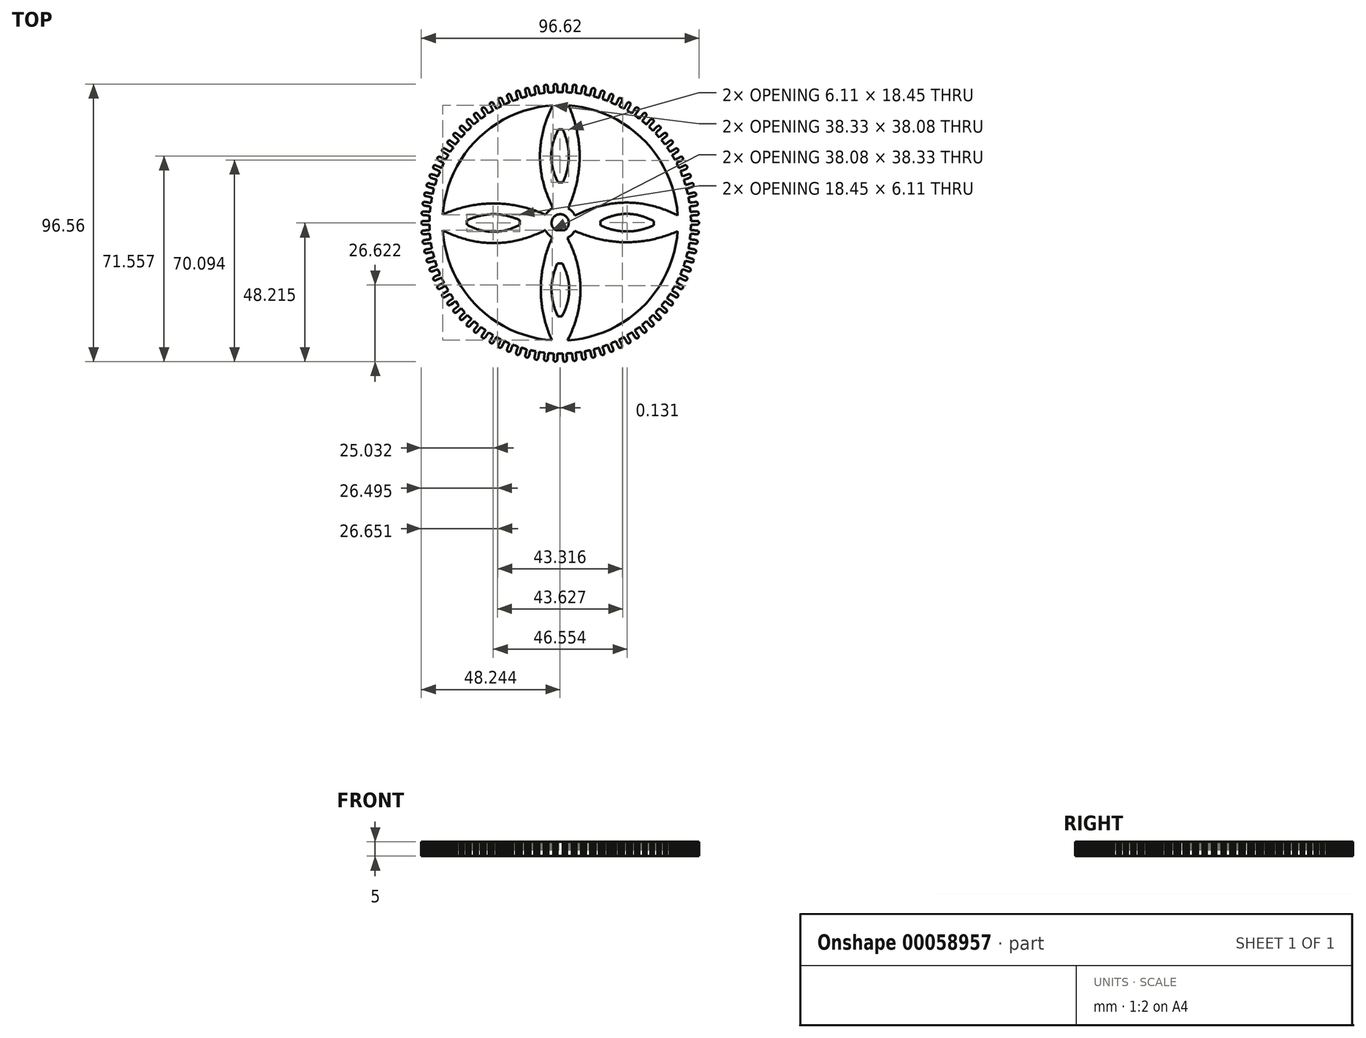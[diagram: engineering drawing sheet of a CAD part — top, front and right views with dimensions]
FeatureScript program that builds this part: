
annotation { "Feature Type Name" : "Feature", "Feature Type Description" : "" }
export const myFeature = defineFeature(function(context is Context, id is Id, definition is map)
    precondition{}
    {
        {
            var Q0;
            Q0=qCreatedBy(makeId("Top.planeOp"),FACE);
            var sketch = newSketch(context, id + "F0", { "sketchPlane" : qUnion([Q0])});
            skLineSegment(sketch, "E0", {"start": v(44.7, -0.63) * mm, "end": v(44.84, -0.63) * mm});
            skLineSegment(sketch, "E1", {"start": v(44.84, -0.63) * mm, "end": v(45, -0.64) * mm});
            skLineSegment(sketch, "E2", {"start": v(45, -0.64) * mm, "end": v(45.17, -0.64) * mm});
            skLineSegment(sketch, "E3", {"start": v(45.17, -0.64) * mm, "end": v(45.34, -0.64) * mm});
            skLineSegment(sketch, "E4", {"start": v(45.34, -0.64) * mm, "end": v(45.5, -0.64) * mm});
            skLineSegment(sketch, "E5", {"start": v(45.5, -0.64) * mm, "end": v(45.67, -0.65) * mm});
            skLineSegment(sketch, "E6", {"start": v(45.67, -0.65) * mm, "end": v(45.84, -0.65) * mm});
            skLineSegment(sketch, "E7", {"start": v(45.84, -0.65) * mm, "end": v(46.01, -0.65) * mm});
            skLineSegment(sketch, "E8", {"start": v(46.01, -0.65) * mm, "end": v(46.18, -0.65) * mm});
            skLineSegment(sketch, "E9", {"start": v(46.18, -0.65) * mm, "end": v(46.35, -0.66) * mm});
            skLineSegment(sketch, "E10", {"start": v(46.35, -0.66) * mm, "end": v(46.51, -0.66) * mm});
            skLineSegment(sketch, "E11", {"start": v(46.51, -0.66) * mm, "end": v(46.68, -0.66) * mm});
            skLineSegment(sketch, "E12", {"start": v(46.68, -0.66) * mm, "end": v(46.85, -0.66) * mm});
            skLineSegment(sketch, "E13", {"start": v(46.85, -0.66) * mm, "end": v(47.02, -0.64) * mm});
            skLineSegment(sketch, "E14", {"start": v(47.02, -0.64) * mm, "end": v(47.18, -0.57) * mm});
            skLineSegment(sketch, "E15", {"start": v(47.18, -0.57) * mm, "end": v(47.32, -0.47) * mm});
            skLineSegment(sketch, "E16", {"start": v(47.32, -0.47) * mm, "end": v(47.43, -0.33) * mm});
            skLineSegment(sketch, "E17", {"start": v(47.43, -0.33) * mm, "end": v(47.5, -0.17) * mm});
            skLineSegment(sketch, "E18", {"start": v(47.5, -0.17) * mm, "end": v(47.52, 0) * mm});
            skLineSegment(sketch, "E19", {"start": v(47.52, 0) * mm, "end": v(47.5, 0.17) * mm});
            skLineSegment(sketch, "E20", {"start": v(47.5, 0.17) * mm, "end": v(47.43, 0.33) * mm});
            skLineSegment(sketch, "E21", {"start": v(47.43, 0.33) * mm, "end": v(47.32, 0.47) * mm});
            skLineSegment(sketch, "E22", {"start": v(47.32, 0.47) * mm, "end": v(47.18, 0.57) * mm});
            skLineSegment(sketch, "E23", {"start": v(47.18, 0.57) * mm, "end": v(47.02, 0.64) * mm});
            skLineSegment(sketch, "E24", {"start": v(47.02, 0.64) * mm, "end": v(46.85, 0.66) * mm});
            skLineSegment(sketch, "E25", {"start": v(46.85, 0.66) * mm, "end": v(46.69, 0.66) * mm});
            skLineSegment(sketch, "E26", {"start": v(46.69, 0.66) * mm, "end": v(46.52, 0.66) * mm});
            skLineSegment(sketch, "E27", {"start": v(46.52, 0.66) * mm, "end": v(46.35, 0.66) * mm});
            skLineSegment(sketch, "E28", {"start": v(46.35, 0.66) * mm, "end": v(46.18, 0.65) * mm});
            skLineSegment(sketch, "E29", {"start": v(46.18, 0.65) * mm, "end": v(46.02, 0.65) * mm});
            skLineSegment(sketch, "E30", {"start": v(46.02, 0.65) * mm, "end": v(45.84, 0.65) * mm});
            skLineSegment(sketch, "E31", {"start": v(45.84, 0.65) * mm, "end": v(45.68, 0.65) * mm});
            skLineSegment(sketch, "E32", {"start": v(45.68, 0.65) * mm, "end": v(45.51, 0.64) * mm});
            skLineSegment(sketch, "E33", {"start": v(45.51, 0.64) * mm, "end": v(45.34, 0.64) * mm});
            skLineSegment(sketch, "E34", {"start": v(45.34, 0.64) * mm, "end": v(45.17, 0.64) * mm});
            skLineSegment(sketch, "E35", {"start": v(45.17, 0.64) * mm, "end": v(45, 0.64) * mm});
            skLineSegment(sketch, "E36", {"start": v(45, 0.64) * mm, "end": v(44.84, 0.63) * mm});
            skLineSegment(sketch, "E37", {"start": v(44.84, 0.63) * mm, "end": v(44.7, 0.63) * mm});
            skLineSegment(sketch, "E38", {"start": v(44.7, 0.63) * mm, "end": v(44.69, 0.8) * mm});
            skLineSegment(sketch, "E39", {"start": v(44.69, 0.8) * mm, "end": v(44.68, 0.96) * mm});
            skLineSegment(sketch, "E40", {"start": v(44.68, 0.96) * mm, "end": v(44.67, 1.13) * mm});
            skLineSegment(sketch, "E41", {"start": v(44.67, 1.13) * mm, "end": v(44.67, 1.3) * mm});
            skLineSegment(sketch, "E42", {"start": v(44.67, 1.3) * mm, "end": v(44.66, 1.46) * mm});
            skLineSegment(sketch, "E43", {"start": v(44.66, 1.46) * mm, "end": v(44.66, 1.63) * mm});
            skLineSegment(sketch, "E44", {"start": v(44.66, 1.63) * mm, "end": v(44.65, 1.8) * mm});
            skLineSegment(sketch, "E45", {"start": v(44.65, 1.8) * mm, "end": v(44.65, 1.96) * mm});
            skLineSegment(sketch, "E46", {"start": v(44.65, 1.96) * mm, "end": v(44.64, 2.13) * mm});
            skLineSegment(sketch, "E47", {"start": v(44.64, 2.13) * mm, "end": v(44.63, 2.3) * mm});
            skLineSegment(sketch, "E48", {"start": v(44.63, 2.3) * mm, "end": v(44.63, 2.46) * mm});
            skLineSegment(sketch, "E49", {"start": v(44.63, 2.46) * mm, "end": v(44.63, 2.54) * mm});
            skLineSegment(sketch, "E50", {"start": v(44.63, 2.54) * mm, "end": v(44.8, 2.55) * mm});
            skLineSegment(sketch, "E51", {"start": v(44.8, 2.55) * mm, "end": v(44.96, 2.56) * mm});
            skLineSegment(sketch, "E52", {"start": v(44.96, 2.56) * mm, "end": v(45.13, 2.57) * mm});
            skLineSegment(sketch, "E53", {"start": v(45.13, 2.57) * mm, "end": v(45.3, 2.58) * mm});
            skLineSegment(sketch, "E54", {"start": v(45.3, 2.58) * mm, "end": v(45.46, 2.59) * mm});
            skLineSegment(sketch, "E55", {"start": v(45.46, 2.59) * mm, "end": v(45.63, 2.6) * mm});
            skLineSegment(sketch, "E56", {"start": v(45.63, 2.6) * mm, "end": v(45.8, 2.6) * mm});
            skLineSegment(sketch, "E57", {"start": v(45.8, 2.6) * mm, "end": v(45.96, 2.62) * mm});
            skLineSegment(sketch, "E58", {"start": v(45.96, 2.62) * mm, "end": v(46.13, 2.63) * mm});
            skLineSegment(sketch, "E59", {"start": v(46.13, 2.63) * mm, "end": v(46.3, 2.64) * mm});
            skLineSegment(sketch, "E60", {"start": v(46.3, 2.64) * mm, "end": v(46.47, 2.65) * mm});
            skLineSegment(sketch, "E61", {"start": v(46.47, 2.65) * mm, "end": v(46.64, 2.65) * mm});
            skLineSegment(sketch, "E62", {"start": v(46.64, 2.65) * mm, "end": v(46.82, 2.67) * mm});
            skLineSegment(sketch, "E63", {"start": v(46.82, 2.67) * mm, "end": v(46.98, 2.7) * mm});
            skLineSegment(sketch, "E64", {"start": v(46.98, 2.7) * mm, "end": v(47.14, 2.8) * mm});
            skLineSegment(sketch, "E65", {"start": v(47.14, 2.8) * mm, "end": v(47.26, 2.91) * mm});
            skLineSegment(sketch, "E66", {"start": v(47.26, 2.91) * mm, "end": v(47.35, 3.06) * mm});
            skLineSegment(sketch, "E67", {"start": v(47.35, 3.06) * mm, "end": v(47.4, 3.23) * mm});
            skLineSegment(sketch, "E68", {"start": v(47.4, 3.23) * mm, "end": v(47.4, 3.4) * mm});
            skLineSegment(sketch, "E69", {"start": v(47.4, 3.4) * mm, "end": v(47.35, 3.57) * mm});
            skLineSegment(sketch, "E70", {"start": v(47.35, 3.57) * mm, "end": v(47.27, 3.72) * mm});
            skLineSegment(sketch, "E71", {"start": v(47.27, 3.72) * mm, "end": v(47.15, 3.85) * mm});
            skLineSegment(sketch, "E72", {"start": v(47.15, 3.85) * mm, "end": v(47, 3.93) * mm});
            skLineSegment(sketch, "E73", {"start": v(47, 3.93) * mm, "end": v(46.83, 3.98) * mm});
            skLineSegment(sketch, "E74", {"start": v(46.83, 3.98) * mm, "end": v(46.72, 3.99) * mm});
            skLineSegment(sketch, "E75", {"start": v(46.72, 3.99) * mm, "end": v(46.55, 3.97) * mm});
            skLineSegment(sketch, "E76", {"start": v(46.55, 3.97) * mm, "end": v(46.38, 3.96) * mm});
            skLineSegment(sketch, "E77", {"start": v(46.38, 3.96) * mm, "end": v(46.21, 3.94) * mm});
            skLineSegment(sketch, "E78", {"start": v(46.21, 3.94) * mm, "end": v(46.04, 3.93) * mm});
            skLineSegment(sketch, "E79", {"start": v(46.04, 3.93) * mm, "end": v(45.88, 3.92) * mm});
            skLineSegment(sketch, "E80", {"start": v(45.88, 3.92) * mm, "end": v(45.71, 3.9) * mm});
            skLineSegment(sketch, "E81", {"start": v(45.71, 3.9) * mm, "end": v(45.54, 3.89) * mm});
            skLineSegment(sketch, "E82", {"start": v(45.54, 3.89) * mm, "end": v(45.38, 3.87) * mm});
            skLineSegment(sketch, "E83", {"start": v(45.38, 3.87) * mm, "end": v(45.21, 3.86) * mm});
            skLineSegment(sketch, "E84", {"start": v(45.21, 3.86) * mm, "end": v(45.04, 3.85) * mm});
            skLineSegment(sketch, "E85", {"start": v(45.04, 3.85) * mm, "end": v(44.87, 3.83) * mm});
            skLineSegment(sketch, "E86", {"start": v(44.87, 3.83) * mm, "end": v(44.7, 3.82) * mm});
            skLineSegment(sketch, "E87", {"start": v(44.7, 3.82) * mm, "end": v(44.54, 3.8) * mm});
            skLineSegment(sketch, "E88", {"start": v(44.54, 3.8) * mm, "end": v(44.52, 3.97) * mm});
            skLineSegment(sketch, "E89", {"start": v(44.52, 3.97) * mm, "end": v(44.5, 4.13) * mm});
            skLineSegment(sketch, "E90", {"start": v(44.5, 4.13) * mm, "end": v(44.49, 4.3) * mm});
            skLineSegment(sketch, "E91", {"start": v(44.49, 4.3) * mm, "end": v(44.47, 4.47) * mm});
            skLineSegment(sketch, "E92", {"start": v(44.47, 4.47) * mm, "end": v(44.45, 4.63) * mm});
            skLineSegment(sketch, "E93", {"start": v(44.45, 4.63) * mm, "end": v(44.43, 4.8) * mm});
            skLineSegment(sketch, "E94", {"start": v(44.43, 4.8) * mm, "end": v(44.42, 4.96) * mm});
            skLineSegment(sketch, "E95", {"start": v(44.42, 4.96) * mm, "end": v(44.4, 5.13) * mm});
            skLineSegment(sketch, "E96", {"start": v(44.4, 5.13) * mm, "end": v(44.38, 5.3) * mm});
            skLineSegment(sketch, "E97", {"start": v(44.38, 5.3) * mm, "end": v(44.36, 5.46) * mm});
            skLineSegment(sketch, "E98", {"start": v(44.36, 5.46) * mm, "end": v(44.35, 5.62) * mm});
            skLineSegment(sketch, "E99", {"start": v(44.35, 5.62) * mm, "end": v(44.34, 5.7) * mm});
            skLineSegment(sketch, "E100", {"start": v(44.34, 5.7) * mm, "end": v(44.5, 5.72) * mm});
            skLineSegment(sketch, "E101", {"start": v(44.5, 5.72) * mm, "end": v(44.67, 5.75) * mm});
            skLineSegment(sketch, "E102", {"start": v(44.67, 5.75) * mm, "end": v(44.84, 5.77) * mm});
            skLineSegment(sketch, "E103", {"start": v(44.84, 5.77) * mm, "end": v(45, 5.79) * mm});
            skLineSegment(sketch, "E104", {"start": v(45, 5.79) * mm, "end": v(45.17, 5.8) * mm});
            skLineSegment(sketch, "E105", {"start": v(45.17, 5.8) * mm, "end": v(45.34, 5.83) * mm});
            skLineSegment(sketch, "E106", {"start": v(45.34, 5.83) * mm, "end": v(45.5, 5.85) * mm});
            skLineSegment(sketch, "E107", {"start": v(45.5, 5.85) * mm, "end": v(45.67, 5.87) * mm});
            skLineSegment(sketch, "E108", {"start": v(45.67, 5.87) * mm, "end": v(45.84, 5.9) * mm});
            skLineSegment(sketch, "E109", {"start": v(45.84, 5.9) * mm, "end": v(46, 5.91) * mm});
            skLineSegment(sketch, "E110", {"start": v(46, 5.91) * mm, "end": v(46.17, 5.94) * mm});
            skLineSegment(sketch, "E111", {"start": v(46.17, 5.94) * mm, "end": v(46.34, 5.96) * mm});
            skLineSegment(sketch, "E112", {"start": v(46.34, 5.96) * mm, "end": v(46.51, 5.98) * mm});
            skLineSegment(sketch, "E113", {"start": v(46.51, 5.98) * mm, "end": v(46.68, 6.03) * mm});
            skLineSegment(sketch, "E114", {"start": v(46.68, 6.03) * mm, "end": v(46.82, 6.13) * mm});
            skLineSegment(sketch, "E115", {"start": v(46.82, 6.13) * mm, "end": v(46.94, 6.26) * mm});
            skLineSegment(sketch, "E116", {"start": v(46.94, 6.26) * mm, "end": v(47.02, 6.41) * mm});
            skLineSegment(sketch, "E117", {"start": v(47.02, 6.41) * mm, "end": v(47.05, 6.58) * mm});
            skLineSegment(sketch, "E118", {"start": v(47.05, 6.58) * mm, "end": v(47.04, 6.76) * mm});
            skLineSegment(sketch, "E119", {"start": v(47.04, 6.76) * mm, "end": v(46.99, 6.92) * mm});
            skLineSegment(sketch, "E120", {"start": v(46.99, 6.92) * mm, "end": v(46.9, 7.07) * mm});
            skLineSegment(sketch, "E121", {"start": v(46.9, 7.07) * mm, "end": v(46.76, 7.18) * mm});
            skLineSegment(sketch, "E122", {"start": v(46.76, 7.18) * mm, "end": v(46.6, 7.26) * mm});
            skLineSegment(sketch, "E123", {"start": v(46.6, 7.26) * mm, "end": v(46.43, 7.3) * mm});
            skLineSegment(sketch, "E124", {"start": v(46.43, 7.3) * mm, "end": v(46.4, 7.3) * mm});
            skLineSegment(sketch, "E125", {"start": v(46.4, 7.3) * mm, "end": v(46.22, 7.28) * mm});
            skLineSegment(sketch, "E126", {"start": v(46.22, 7.28) * mm, "end": v(46.06, 7.25) * mm});
            skLineSegment(sketch, "E127", {"start": v(46.06, 7.25) * mm, "end": v(45.9, 7.22) * mm});
            skLineSegment(sketch, "E128", {"start": v(45.9, 7.22) * mm, "end": v(45.73, 7.2) * mm});
            skLineSegment(sketch, "E129", {"start": v(45.73, 7.2) * mm, "end": v(45.56, 7.17) * mm});
            skLineSegment(sketch, "E130", {"start": v(45.56, 7.17) * mm, "end": v(45.4, 7.15) * mm});
            skLineSegment(sketch, "E131", {"start": v(45.4, 7.15) * mm, "end": v(45.23, 7.12) * mm});
            skLineSegment(sketch, "E132", {"start": v(45.23, 7.12) * mm, "end": v(45.06, 7.1) * mm});
            skLineSegment(sketch, "E133", {"start": v(45.06, 7.1) * mm, "end": v(44.9, 7.07) * mm});
            skLineSegment(sketch, "E134", {"start": v(44.9, 7.07) * mm, "end": v(44.73, 7.04) * mm});
            skLineSegment(sketch, "E135", {"start": v(44.73, 7.04) * mm, "end": v(44.57, 7.02) * mm});
            skLineSegment(sketch, "E136", {"start": v(44.57, 7.02) * mm, "end": v(44.4, 7) * mm});
            skLineSegment(sketch, "E137", {"start": v(44.4, 7) * mm, "end": v(44.23, 6.97) * mm});
            skLineSegment(sketch, "E138", {"start": v(44.23, 6.97) * mm, "end": v(44.16, 6.96) * mm});
            skLineSegment(sketch, "E139", {"start": v(44.16, 6.96) * mm, "end": v(44.13, 7.12) * mm});
            skLineSegment(sketch, "E140", {"start": v(44.13, 7.12) * mm, "end": v(44.1, 7.28) * mm});
            skLineSegment(sketch, "E141", {"start": v(44.1, 7.28) * mm, "end": v(44.08, 7.45) * mm});
            skLineSegment(sketch, "E142", {"start": v(44.08, 7.45) * mm, "end": v(44.05, 7.61) * mm});
            skLineSegment(sketch, "E143", {"start": v(44.05, 7.61) * mm, "end": v(44.02, 7.78) * mm});
            skLineSegment(sketch, "E144", {"start": v(44.02, 7.78) * mm, "end": v(43.99, 7.94) * mm});
            skLineSegment(sketch, "E145", {"start": v(43.99, 7.94) * mm, "end": v(43.96, 8.1) * mm});
            skLineSegment(sketch, "E146", {"start": v(43.96, 8.1) * mm, "end": v(43.93, 8.27) * mm});
            skLineSegment(sketch, "E147", {"start": v(43.93, 8.27) * mm, "end": v(43.9, 8.43) * mm});
            skLineSegment(sketch, "E148", {"start": v(43.9, 8.43) * mm, "end": v(43.87, 8.6) * mm});
            skLineSegment(sketch, "E149", {"start": v(43.87, 8.6) * mm, "end": v(43.84, 8.76) * mm});
            skLineSegment(sketch, "E150", {"start": v(43.84, 8.76) * mm, "end": v(43.83, 8.84) * mm});
            skLineSegment(sketch, "E151", {"start": v(43.83, 8.84) * mm, "end": v(44, 8.87) * mm});
            skLineSegment(sketch, "E152", {"start": v(44, 8.87) * mm, "end": v(44.16, 8.9) * mm});
            skLineSegment(sketch, "E153", {"start": v(44.16, 8.9) * mm, "end": v(44.32, 8.94) * mm});
            skLineSegment(sketch, "E154", {"start": v(44.32, 8.94) * mm, "end": v(44.49, 8.97) * mm});
            skLineSegment(sketch, "E155", {"start": v(44.49, 8.97) * mm, "end": v(44.65, 9) * mm});
            skLineSegment(sketch, "E156", {"start": v(44.65, 9) * mm, "end": v(44.82, 9.03) * mm});
            skLineSegment(sketch, "E157", {"start": v(44.82, 9.03) * mm, "end": v(44.98, 9.07) * mm});
            skLineSegment(sketch, "E158", {"start": v(44.98, 9.07) * mm, "end": v(45.14, 9.1) * mm});
            skLineSegment(sketch, "E159", {"start": v(45.14, 9.1) * mm, "end": v(45.31, 9.13) * mm});
            skLineSegment(sketch, "E160", {"start": v(45.31, 9.13) * mm, "end": v(45.48, 9.16) * mm});
            skLineSegment(sketch, "E161", {"start": v(45.48, 9.16) * mm, "end": v(45.64, 9.2) * mm});
            skLineSegment(sketch, "E162", {"start": v(45.64, 9.2) * mm, "end": v(45.8, 9.23) * mm});
            skLineSegment(sketch, "E163", {"start": v(45.8, 9.23) * mm, "end": v(45.98, 9.27) * mm});
            skLineSegment(sketch, "E164", {"start": v(45.98, 9.27) * mm, "end": v(46.14, 9.33) * mm});
            skLineSegment(sketch, "E165", {"start": v(46.14, 9.33) * mm, "end": v(46.28, 9.44) * mm});
            skLineSegment(sketch, "E166", {"start": v(46.28, 9.44) * mm, "end": v(46.39, 9.57) * mm});
            skLineSegment(sketch, "E167", {"start": v(46.39, 9.57) * mm, "end": v(46.45, 9.73) * mm});
            skLineSegment(sketch, "E168", {"start": v(46.45, 9.73) * mm, "end": v(46.48, 9.9) * mm});
            skLineSegment(sketch, "E169", {"start": v(46.48, 9.9) * mm, "end": v(46.45, 10.08) * mm});
            skLineSegment(sketch, "E170", {"start": v(46.45, 10.08) * mm, "end": v(46.39, 10.24) * mm});
            skLineSegment(sketch, "E171", {"start": v(46.39, 10.24) * mm, "end": v(46.28, 10.38) * mm});
            skLineSegment(sketch, "E172", {"start": v(46.28, 10.38) * mm, "end": v(46.14, 10.48) * mm});
            skLineSegment(sketch, "E173", {"start": v(46.14, 10.48) * mm, "end": v(45.98, 10.55) * mm});
            skLineSegment(sketch, "E174", {"start": v(45.98, 10.55) * mm, "end": v(45.81, 10.57) * mm});
            skLineSegment(sketch, "E175", {"start": v(45.81, 10.57) * mm, "end": v(45.65, 10.54) * mm});
            skLineSegment(sketch, "E176", {"start": v(45.65, 10.54) * mm, "end": v(45.48, 10.5) * mm});
            skLineSegment(sketch, "E177", {"start": v(45.48, 10.5) * mm, "end": v(45.32, 10.47) * mm});
            skLineSegment(sketch, "E178", {"start": v(45.32, 10.47) * mm, "end": v(45.16, 10.44) * mm});
            skLineSegment(sketch, "E179", {"start": v(45.16, 10.44) * mm, "end": v(45, 10.4) * mm});
            skLineSegment(sketch, "E180", {"start": v(45, 10.4) * mm, "end": v(44.83, 10.36) * mm});
            skLineSegment(sketch, "E181", {"start": v(44.83, 10.36) * mm, "end": v(44.67, 10.32) * mm});
            skLineSegment(sketch, "E182", {"start": v(44.67, 10.32) * mm, "end": v(44.5, 10.29) * mm});
            skLineSegment(sketch, "E183", {"start": v(44.5, 10.29) * mm, "end": v(44.34, 10.25) * mm});
            skLineSegment(sketch, "E184", {"start": v(44.34, 10.25) * mm, "end": v(44.18, 10.21) * mm});
            skLineSegment(sketch, "E185", {"start": v(44.18, 10.21) * mm, "end": v(44.01, 10.18) * mm});
            skLineSegment(sketch, "E186", {"start": v(44.01, 10.18) * mm, "end": v(43.85, 10.14) * mm});
            skLineSegment(sketch, "E187", {"start": v(43.85, 10.14) * mm, "end": v(43.69, 10.1) * mm});
            skLineSegment(sketch, "E188", {"start": v(43.69, 10.1) * mm, "end": v(43.57, 10.07) * mm});
            skLineSegment(sketch, "E189", {"start": v(43.57, 10.07) * mm, "end": v(43.53, 10.24) * mm});
            skLineSegment(sketch, "E190", {"start": v(43.53, 10.24) * mm, "end": v(43.49, 10.4) * mm});
            skLineSegment(sketch, "E191", {"start": v(43.49, 10.4) * mm, "end": v(43.45, 10.56) * mm});
            skLineSegment(sketch, "E192", {"start": v(43.45, 10.56) * mm, "end": v(43.4, 10.72) * mm});
            skLineSegment(sketch, "E193", {"start": v(43.4, 10.72) * mm, "end": v(43.37, 10.88) * mm});
            skLineSegment(sketch, "E194", {"start": v(43.37, 10.88) * mm, "end": v(43.33, 11.04) * mm});
            skLineSegment(sketch, "E195", {"start": v(43.33, 11.04) * mm, "end": v(43.29, 11.2) * mm});
            skLineSegment(sketch, "E196", {"start": v(43.29, 11.2) * mm, "end": v(43.25, 11.37) * mm});
            skLineSegment(sketch, "E197", {"start": v(43.25, 11.37) * mm, "end": v(43.2, 11.53) * mm});
            skLineSegment(sketch, "E198", {"start": v(43.2, 11.53) * mm, "end": v(43.16, 11.69) * mm});
            skLineSegment(sketch, "E199", {"start": v(43.16, 11.69) * mm, "end": v(43.12, 11.85) * mm});
            skLineSegment(sketch, "E200", {"start": v(43.12, 11.85) * mm, "end": v(43.1, 11.93) * mm});
            skLineSegment(sketch, "E201", {"start": v(43.1, 11.93) * mm, "end": v(43.27, 11.97) * mm});
            skLineSegment(sketch, "E202", {"start": v(43.27, 11.97) * mm, "end": v(43.43, 12.02) * mm});
            skLineSegment(sketch, "E203", {"start": v(43.43, 12.02) * mm, "end": v(43.6, 12.06) * mm});
            skLineSegment(sketch, "E204", {"start": v(43.6, 12.06) * mm, "end": v(43.75, 12.1) * mm});
            skLineSegment(sketch, "E205", {"start": v(43.75, 12.1) * mm, "end": v(43.91, 12.15) * mm});
            skLineSegment(sketch, "E206", {"start": v(43.91, 12.15) * mm, "end": v(44.08, 12.2) * mm});
            skLineSegment(sketch, "E207", {"start": v(44.08, 12.2) * mm, "end": v(44.24, 12.24) * mm});
            skLineSegment(sketch, "E208", {"start": v(44.24, 12.24) * mm, "end": v(44.4, 12.28) * mm});
            skLineSegment(sketch, "E209", {"start": v(44.4, 12.28) * mm, "end": v(44.56, 12.33) * mm});
            skLineSegment(sketch, "E210", {"start": v(44.56, 12.33) * mm, "end": v(44.72, 12.37) * mm});
            skLineSegment(sketch, "E211", {"start": v(44.72, 12.37) * mm, "end": v(44.88, 12.41) * mm});
            skLineSegment(sketch, "E212", {"start": v(44.88, 12.41) * mm, "end": v(45.05, 12.46) * mm});
            skLineSegment(sketch, "E213", {"start": v(45.05, 12.46) * mm, "end": v(45.22, 12.5) * mm});
            skLineSegment(sketch, "E214", {"start": v(45.22, 12.5) * mm, "end": v(45.38, 12.58) * mm});
            skLineSegment(sketch, "E215", {"start": v(45.38, 12.58) * mm, "end": v(45.5, 12.7) * mm});
            skLineSegment(sketch, "E216", {"start": v(45.5, 12.7) * mm, "end": v(45.6, 12.84) * mm});
            skLineSegment(sketch, "E217", {"start": v(45.6, 12.84) * mm, "end": v(45.66, 13) * mm});
            skLineSegment(sketch, "E218", {"start": v(45.66, 13) * mm, "end": v(45.67, 13.18) * mm});
            skLineSegment(sketch, "E219", {"start": v(45.67, 13.18) * mm, "end": v(45.64, 13.35) * mm});
            skLineSegment(sketch, "E220", {"start": v(45.64, 13.35) * mm, "end": v(45.56, 13.5) * mm});
            skLineSegment(sketch, "E221", {"start": v(45.56, 13.5) * mm, "end": v(45.44, 13.63) * mm});
            skLineSegment(sketch, "E222", {"start": v(45.44, 13.63) * mm, "end": v(45.3, 13.73) * mm});
            skLineSegment(sketch, "E223", {"start": v(45.3, 13.73) * mm, "end": v(45.13, 13.78) * mm});
            skLineSegment(sketch, "E224", {"start": v(45.13, 13.78) * mm, "end": v(45, 13.8) * mm});
            skLineSegment(sketch, "E225", {"start": v(45, 13.8) * mm, "end": v(44.82, 13.77) * mm});
            skLineSegment(sketch, "E226", {"start": v(44.82, 13.77) * mm, "end": v(44.66, 13.72) * mm});
            skLineSegment(sketch, "E227", {"start": v(44.66, 13.72) * mm, "end": v(44.5, 13.67) * mm});
            skLineSegment(sketch, "E228", {"start": v(44.5, 13.67) * mm, "end": v(44.34, 13.62) * mm});
            skLineSegment(sketch, "E229", {"start": v(44.34, 13.62) * mm, "end": v(44.18, 13.57) * mm});
            skLineSegment(sketch, "E230", {"start": v(44.18, 13.57) * mm, "end": v(44.02, 13.53) * mm});
            skLineSegment(sketch, "E231", {"start": v(44.02, 13.53) * mm, "end": v(43.86, 13.48) * mm});
            skLineSegment(sketch, "E232", {"start": v(43.86, 13.48) * mm, "end": v(43.7, 13.43) * mm});
            skLineSegment(sketch, "E233", {"start": v(43.7, 13.43) * mm, "end": v(43.54, 13.38) * mm});
            skLineSegment(sketch, "E234", {"start": v(43.54, 13.38) * mm, "end": v(43.38, 13.33) * mm});
            skLineSegment(sketch, "E235", {"start": v(43.38, 13.33) * mm, "end": v(43.22, 13.28) * mm});
            skLineSegment(sketch, "E236", {"start": v(43.22, 13.28) * mm, "end": v(43.06, 13.24) * mm});
            skLineSegment(sketch, "E237", {"start": v(43.06, 13.24) * mm, "end": v(42.9, 13.19) * mm});
            skLineSegment(sketch, "E238", {"start": v(42.9, 13.19) * mm, "end": v(42.76, 13.14) * mm});
            skLineSegment(sketch, "E239", {"start": v(42.76, 13.14) * mm, "end": v(42.7, 13.3) * mm});
            skLineSegment(sketch, "E240", {"start": v(42.7, 13.3) * mm, "end": v(42.65, 13.46) * mm});
            skLineSegment(sketch, "E241", {"start": v(42.65, 13.46) * mm, "end": v(42.6, 13.62) * mm});
            skLineSegment(sketch, "E242", {"start": v(42.6, 13.62) * mm, "end": v(42.55, 13.78) * mm});
            skLineSegment(sketch, "E243", {"start": v(42.55, 13.78) * mm, "end": v(42.5, 13.94) * mm});
            skLineSegment(sketch, "E244", {"start": v(42.5, 13.94) * mm, "end": v(42.45, 14.1) * mm});
            skLineSegment(sketch, "E245", {"start": v(42.45, 14.1) * mm, "end": v(42.4, 14.25) * mm});
            skLineSegment(sketch, "E246", {"start": v(42.4, 14.25) * mm, "end": v(42.34, 14.41) * mm});
            skLineSegment(sketch, "E247", {"start": v(42.34, 14.41) * mm, "end": v(42.3, 14.57) * mm});
            skLineSegment(sketch, "E248", {"start": v(42.3, 14.57) * mm, "end": v(42.24, 14.73) * mm});
            skLineSegment(sketch, "E249", {"start": v(42.24, 14.73) * mm, "end": v(42.2, 14.89) * mm});
            skLineSegment(sketch, "E250", {"start": v(42.2, 14.89) * mm, "end": v(42.17, 14.96) * mm});
            skLineSegment(sketch, "E251", {"start": v(42.17, 14.96) * mm, "end": v(42.32, 15.02) * mm});
            skLineSegment(sketch, "E252", {"start": v(42.32, 15.02) * mm, "end": v(42.48, 15.07) * mm});
            skLineSegment(sketch, "E253", {"start": v(42.48, 15.07) * mm, "end": v(42.64, 15.13) * mm});
            skLineSegment(sketch, "E254", {"start": v(42.64, 15.13) * mm, "end": v(42.8, 15.18) * mm});
            skLineSegment(sketch, "E255", {"start": v(42.8, 15.18) * mm, "end": v(42.96, 15.24) * mm});
            skLineSegment(sketch, "E256", {"start": v(42.96, 15.24) * mm, "end": v(43.12, 15.3) * mm});
            skLineSegment(sketch, "E257", {"start": v(43.12, 15.3) * mm, "end": v(43.27, 15.35) * mm});
            skLineSegment(sketch, "E258", {"start": v(43.27, 15.35) * mm, "end": v(43.43, 15.4) * mm});
            skLineSegment(sketch, "E259", {"start": v(43.43, 15.4) * mm, "end": v(43.6, 15.46) * mm});
            skLineSegment(sketch, "E260", {"start": v(43.6, 15.46) * mm, "end": v(43.75, 15.51) * mm});
            skLineSegment(sketch, "E261", {"start": v(43.75, 15.51) * mm, "end": v(43.9, 15.57) * mm});
            skLineSegment(sketch, "E262", {"start": v(43.9, 15.57) * mm, "end": v(44.07, 15.63) * mm});
            skLineSegment(sketch, "E263", {"start": v(44.07, 15.63) * mm, "end": v(44.24, 15.69) * mm});
            skLineSegment(sketch, "E264", {"start": v(44.24, 15.69) * mm, "end": v(44.39, 15.77) * mm});
            skLineSegment(sketch, "E265", {"start": v(44.39, 15.77) * mm, "end": v(44.5, 15.9) * mm});
            skLineSegment(sketch, "E266", {"start": v(44.5, 15.9) * mm, "end": v(44.6, 16.05) * mm});
            skLineSegment(sketch, "E267", {"start": v(44.6, 16.05) * mm, "end": v(44.64, 16.21) * mm});
            skLineSegment(sketch, "E268", {"start": v(44.64, 16.21) * mm, "end": v(44.64, 16.39) * mm});
            skLineSegment(sketch, "E269", {"start": v(44.64, 16.39) * mm, "end": v(44.6, 16.55) * mm});
            skLineSegment(sketch, "E270", {"start": v(44.6, 16.55) * mm, "end": v(44.5, 16.7) * mm});
            skLineSegment(sketch, "E271", {"start": v(44.5, 16.7) * mm, "end": v(44.38, 16.83) * mm});
            skLineSegment(sketch, "E272", {"start": v(44.38, 16.83) * mm, "end": v(44.23, 16.91) * mm});
            skLineSegment(sketch, "E273", {"start": v(44.23, 16.91) * mm, "end": v(44.06, 16.95) * mm});
            skLineSegment(sketch, "E274", {"start": v(44.06, 16.95) * mm, "end": v(44, 16.96) * mm});
            skLineSegment(sketch, "E275", {"start": v(44, 16.96) * mm, "end": v(43.82, 16.94) * mm});
            skLineSegment(sketch, "E276", {"start": v(43.82, 16.94) * mm, "end": v(43.66, 16.88) * mm});
            skLineSegment(sketch, "E277", {"start": v(43.66, 16.88) * mm, "end": v(43.5, 16.82) * mm});
            skLineSegment(sketch, "E278", {"start": v(43.5, 16.82) * mm, "end": v(43.35, 16.76) * mm});
            skLineSegment(sketch, "E279", {"start": v(43.35, 16.76) * mm, "end": v(43.2, 16.7) * mm});
            skLineSegment(sketch, "E280", {"start": v(43.2, 16.7) * mm, "end": v(43.04, 16.65) * mm});
            skLineSegment(sketch, "E281", {"start": v(43.04, 16.65) * mm, "end": v(42.88, 16.58) * mm});
            skLineSegment(sketch, "E282", {"start": v(42.88, 16.58) * mm, "end": v(42.72, 16.53) * mm});
            skLineSegment(sketch, "E283", {"start": v(42.72, 16.53) * mm, "end": v(42.57, 16.47) * mm});
            skLineSegment(sketch, "E284", {"start": v(42.57, 16.47) * mm, "end": v(42.4, 16.4) * mm});
            skLineSegment(sketch, "E285", {"start": v(42.4, 16.4) * mm, "end": v(42.25, 16.35) * mm});
            skLineSegment(sketch, "E286", {"start": v(42.25, 16.35) * mm, "end": v(42.1, 16.29) * mm});
            skLineSegment(sketch, "E287", {"start": v(42.1, 16.29) * mm, "end": v(41.94, 16.23) * mm});
            skLineSegment(sketch, "E288", {"start": v(41.94, 16.23) * mm, "end": v(41.78, 16.17) * mm});
            skLineSegment(sketch, "E289", {"start": v(41.78, 16.17) * mm, "end": v(41.73, 16.15) * mm});
            skLineSegment(sketch, "E290", {"start": v(41.73, 16.15) * mm, "end": v(41.67, 16.3) * mm});
            skLineSegment(sketch, "E291", {"start": v(41.67, 16.3) * mm, "end": v(41.6, 16.46) * mm});
            skLineSegment(sketch, "E292", {"start": v(41.6, 16.46) * mm, "end": v(41.55, 16.61) * mm});
            skLineSegment(sketch, "E293", {"start": v(41.55, 16.61) * mm, "end": v(41.48, 16.77) * mm});
            skLineSegment(sketch, "E294", {"start": v(41.48, 16.77) * mm, "end": v(41.42, 16.92) * mm});
            skLineSegment(sketch, "E295", {"start": v(41.42, 16.92) * mm, "end": v(41.36, 17.08) * mm});
            skLineSegment(sketch, "E296", {"start": v(41.36, 17.08) * mm, "end": v(41.3, 17.23) * mm});
            skLineSegment(sketch, "E297", {"start": v(41.3, 17.23) * mm, "end": v(41.23, 17.38) * mm});
            skLineSegment(sketch, "E298", {"start": v(41.23, 17.38) * mm, "end": v(41.17, 17.54) * mm});
            skLineSegment(sketch, "E299", {"start": v(41.17, 17.54) * mm, "end": v(41.1, 17.7) * mm});
            skLineSegment(sketch, "E300", {"start": v(41.1, 17.7) * mm, "end": v(41.05, 17.85) * mm});
            skLineSegment(sketch, "E301", {"start": v(41.05, 17.85) * mm, "end": v(41.02, 17.92) * mm});
            skLineSegment(sketch, "E302", {"start": v(41.02, 17.92) * mm, "end": v(41.17, 17.99) * mm});
            skLineSegment(sketch, "E303", {"start": v(41.17, 17.99) * mm, "end": v(41.32, 18.05) * mm});
            skLineSegment(sketch, "E304", {"start": v(41.32, 18.05) * mm, "end": v(41.48, 18.12) * mm});
            skLineSegment(sketch, "E305", {"start": v(41.48, 18.12) * mm, "end": v(41.63, 18.19) * mm});
            skLineSegment(sketch, "E306", {"start": v(41.63, 18.19) * mm, "end": v(41.79, 18.25) * mm});
            skLineSegment(sketch, "E307", {"start": v(41.79, 18.25) * mm, "end": v(41.94, 18.32) * mm});
            skLineSegment(sketch, "E308", {"start": v(41.94, 18.32) * mm, "end": v(42.1, 18.38) * mm});
            skLineSegment(sketch, "E309", {"start": v(42.1, 18.38) * mm, "end": v(42.25, 18.45) * mm});
            skLineSegment(sketch, "E310", {"start": v(42.25, 18.45) * mm, "end": v(42.4, 18.52) * mm});
            skLineSegment(sketch, "E311", {"start": v(42.4, 18.52) * mm, "end": v(42.56, 18.58) * mm});
            skLineSegment(sketch, "E312", {"start": v(42.56, 18.58) * mm, "end": v(42.71, 18.65) * mm});
            skLineSegment(sketch, "E313", {"start": v(42.71, 18.65) * mm, "end": v(42.87, 18.72) * mm});
            skLineSegment(sketch, "E314", {"start": v(42.87, 18.72) * mm, "end": v(43.03, 18.79) * mm});
            skLineSegment(sketch, "E315", {"start": v(43.03, 18.79) * mm, "end": v(43.18, 18.89) * mm});
            skLineSegment(sketch, "E316", {"start": v(43.18, 18.89) * mm, "end": v(43.3, 19.02) * mm});
            skLineSegment(sketch, "E317", {"start": v(43.3, 19.02) * mm, "end": v(43.37, 19.17) * mm});
            skLineSegment(sketch, "E318", {"start": v(43.37, 19.17) * mm, "end": v(43.4, 19.34) * mm});
            skLineSegment(sketch, "E319", {"start": v(43.4, 19.34) * mm, "end": v(43.38, 19.52) * mm});
            skLineSegment(sketch, "E320", {"start": v(43.38, 19.52) * mm, "end": v(43.33, 19.68) * mm});
            skLineSegment(sketch, "E321", {"start": v(43.33, 19.68) * mm, "end": v(43.23, 19.82) * mm});
            skLineSegment(sketch, "E322", {"start": v(43.23, 19.82) * mm, "end": v(43.1, 19.94) * mm});
            skLineSegment(sketch, "E323", {"start": v(43.1, 19.94) * mm, "end": v(42.94, 20.01) * mm});
            skLineSegment(sketch, "E324", {"start": v(42.94, 20.01) * mm, "end": v(42.77, 20.04) * mm});
            skLineSegment(sketch, "E325", {"start": v(42.77, 20.04) * mm, "end": v(42.73, 20.04) * mm});
            skLineSegment(sketch, "E326", {"start": v(42.73, 20.04) * mm, "end": v(42.56, 20.02) * mm});
            skLineSegment(sketch, "E327", {"start": v(42.56, 20.02) * mm, "end": v(42.4, 19.95) * mm});
            skLineSegment(sketch, "E328", {"start": v(42.4, 19.95) * mm, "end": v(42.25, 19.88) * mm});
            skLineSegment(sketch, "E329", {"start": v(42.25, 19.88) * mm, "end": v(42.1, 19.81) * mm});
            skLineSegment(sketch, "E330", {"start": v(42.1, 19.81) * mm, "end": v(41.94, 19.74) * mm});
            skLineSegment(sketch, "E331", {"start": v(41.94, 19.74) * mm, "end": v(41.79, 19.67) * mm});
            skLineSegment(sketch, "E332", {"start": v(41.79, 19.67) * mm, "end": v(41.64, 19.6) * mm});
            skLineSegment(sketch, "E333", {"start": v(41.64, 19.6) * mm, "end": v(41.48, 19.53) * mm});
            skLineSegment(sketch, "E334", {"start": v(41.48, 19.53) * mm, "end": v(41.33, 19.46) * mm});
            skLineSegment(sketch, "E335", {"start": v(41.33, 19.46) * mm, "end": v(41.18, 19.4) * mm});
            skLineSegment(sketch, "E336", {"start": v(41.18, 19.4) * mm, "end": v(41.03, 19.32) * mm});
            skLineSegment(sketch, "E337", {"start": v(41.03, 19.32) * mm, "end": v(40.87, 19.25) * mm});
            skLineSegment(sketch, "E338", {"start": v(40.87, 19.25) * mm, "end": v(40.72, 19.18) * mm});
            skLineSegment(sketch, "E339", {"start": v(40.72, 19.18) * mm, "end": v(40.57, 19.1) * mm});
            skLineSegment(sketch, "E340", {"start": v(40.57, 19.1) * mm, "end": v(40.5, 19.08) * mm});
            skLineSegment(sketch, "E341", {"start": v(40.5, 19.08) * mm, "end": v(40.43, 19.23) * mm});
            skLineSegment(sketch, "E342", {"start": v(40.43, 19.23) * mm, "end": v(40.36, 19.38) * mm});
            skLineSegment(sketch, "E343", {"start": v(40.36, 19.38) * mm, "end": v(40.28, 19.53) * mm});
            skLineSegment(sketch, "E344", {"start": v(40.28, 19.53) * mm, "end": v(40.21, 19.68) * mm});
            skLineSegment(sketch, "E345", {"start": v(40.21, 19.68) * mm, "end": v(40.14, 19.82) * mm});
            skLineSegment(sketch, "E346", {"start": v(40.14, 19.82) * mm, "end": v(40.07, 19.97) * mm});
            skLineSegment(sketch, "E347", {"start": v(40.07, 19.97) * mm, "end": v(40, 20.12) * mm});
            skLineSegment(sketch, "E348", {"start": v(40, 20.12) * mm, "end": v(39.92, 20.27) * mm});
            skLineSegment(sketch, "E349", {"start": v(39.92, 20.27) * mm, "end": v(39.85, 20.42) * mm});
            skLineSegment(sketch, "E350", {"start": v(39.85, 20.42) * mm, "end": v(39.77, 20.57) * mm});
            skLineSegment(sketch, "E351", {"start": v(39.77, 20.57) * mm, "end": v(39.7, 20.72) * mm});
            skLineSegment(sketch, "E352", {"start": v(39.7, 20.72) * mm, "end": v(39.67, 20.8) * mm});
            skLineSegment(sketch, "E353", {"start": v(39.67, 20.8) * mm, "end": v(39.81, 20.87) * mm});
            skLineSegment(sketch, "E354", {"start": v(39.81, 20.87) * mm, "end": v(39.96, 20.95) * mm});
            skLineSegment(sketch, "E355", {"start": v(39.96, 20.95) * mm, "end": v(40.11, 21.03) * mm});
            skLineSegment(sketch, "E356", {"start": v(40.11, 21.03) * mm, "end": v(40.26, 21.1) * mm});
            skLineSegment(sketch, "E357", {"start": v(40.26, 21.1) * mm, "end": v(40.4, 21.18) * mm});
            skLineSegment(sketch, "E358", {"start": v(40.4, 21.18) * mm, "end": v(40.56, 21.26) * mm});
            skLineSegment(sketch, "E359", {"start": v(40.56, 21.26) * mm, "end": v(40.7, 21.33) * mm});
            skLineSegment(sketch, "E360", {"start": v(40.7, 21.33) * mm, "end": v(40.86, 21.4) * mm});
            skLineSegment(sketch, "E361", {"start": v(40.86, 21.4) * mm, "end": v(41, 21.49) * mm});
            skLineSegment(sketch, "E362", {"start": v(41, 21.49) * mm, "end": v(41.16, 21.56) * mm});
            skLineSegment(sketch, "E363", {"start": v(41.16, 21.56) * mm, "end": v(41.3, 21.64) * mm});
            skLineSegment(sketch, "E364", {"start": v(41.3, 21.64) * mm, "end": v(41.46, 21.72) * mm});
            skLineSegment(sketch, "E365", {"start": v(41.46, 21.72) * mm, "end": v(41.62, 21.8) * mm});
            skLineSegment(sketch, "E366", {"start": v(41.62, 21.8) * mm, "end": v(41.75, 21.9) * mm});
            skLineSegment(sketch, "E367", {"start": v(41.75, 21.9) * mm, "end": v(41.86, 22.05) * mm});
            skLineSegment(sketch, "E368", {"start": v(41.86, 22.05) * mm, "end": v(41.92, 22.2) * mm});
            skLineSegment(sketch, "E369", {"start": v(41.92, 22.2) * mm, "end": v(41.94, 22.38) * mm});
            skLineSegment(sketch, "E370", {"start": v(41.94, 22.38) * mm, "end": v(41.92, 22.55) * mm});
            skLineSegment(sketch, "E371", {"start": v(41.92, 22.55) * mm, "end": v(41.85, 22.7) * mm});
            skLineSegment(sketch, "E372", {"start": v(41.85, 22.7) * mm, "end": v(41.74, 22.85) * mm});
            skLineSegment(sketch, "E373", {"start": v(41.74, 22.85) * mm, "end": v(41.6, 22.95) * mm});
            skLineSegment(sketch, "E374", {"start": v(41.6, 22.95) * mm, "end": v(41.44, 23.01) * mm});
            skLineSegment(sketch, "E375", {"start": v(41.44, 23.01) * mm, "end": v(41.26, 23.03) * mm});
            skLineSegment(sketch, "E376", {"start": v(41.26, 23.03) * mm, "end": v(41.1, 23) * mm});
            skLineSegment(sketch, "E377", {"start": v(41.1, 23) * mm, "end": v(40.94, 22.94) * mm});
            skLineSegment(sketch, "E378", {"start": v(40.94, 22.94) * mm, "end": v(40.8, 22.86) * mm});
            skLineSegment(sketch, "E379", {"start": v(40.8, 22.86) * mm, "end": v(40.65, 22.78) * mm});
            skLineSegment(sketch, "E380", {"start": v(40.65, 22.78) * mm, "end": v(40.5, 22.7) * mm});
            skLineSegment(sketch, "E381", {"start": v(40.5, 22.7) * mm, "end": v(40.36, 22.62) * mm});
            skLineSegment(sketch, "E382", {"start": v(40.36, 22.62) * mm, "end": v(40.2, 22.54) * mm});
            skLineSegment(sketch, "E383", {"start": v(40.2, 22.54) * mm, "end": v(40.06, 22.46) * mm});
            skLineSegment(sketch, "E384", {"start": v(40.06, 22.46) * mm, "end": v(39.92, 22.38) * mm});
            skLineSegment(sketch, "E385", {"start": v(39.92, 22.38) * mm, "end": v(39.77, 22.3) * mm});
            skLineSegment(sketch, "E386", {"start": v(39.77, 22.3) * mm, "end": v(39.62, 22.21) * mm});
            skLineSegment(sketch, "E387", {"start": v(39.62, 22.21) * mm, "end": v(39.47, 22.13) * mm});
            skLineSegment(sketch, "E388", {"start": v(39.47, 22.13) * mm, "end": v(39.32, 22.05) * mm});
            skLineSegment(sketch, "E389", {"start": v(39.32, 22.05) * mm, "end": v(39.18, 21.97) * mm});
            skLineSegment(sketch, "E390", {"start": v(39.18, 21.97) * mm, "end": v(39.07, 21.91) * mm});
            skLineSegment(sketch, "E391", {"start": v(39.07, 21.91) * mm, "end": v(38.99, 22.06) * mm});
            skLineSegment(sketch, "E392", {"start": v(38.99, 22.06) * mm, "end": v(38.9, 22.2) * mm});
            skLineSegment(sketch, "E393", {"start": v(38.9, 22.2) * mm, "end": v(38.82, 22.34) * mm});
            skLineSegment(sketch, "E394", {"start": v(38.82, 22.34) * mm, "end": v(38.74, 22.49) * mm});
            skLineSegment(sketch, "E395", {"start": v(38.74, 22.49) * mm, "end": v(38.66, 22.63) * mm});
            skLineSegment(sketch, "E396", {"start": v(38.66, 22.63) * mm, "end": v(38.57, 22.78) * mm});
            skLineSegment(sketch, "E397", {"start": v(38.57, 22.78) * mm, "end": v(38.49, 22.92) * mm});
            skLineSegment(sketch, "E398", {"start": v(38.49, 22.92) * mm, "end": v(38.4, 23.06) * mm});
            skLineSegment(sketch, "E399", {"start": v(38.4, 23.06) * mm, "end": v(38.32, 23.2) * mm});
            skLineSegment(sketch, "E400", {"start": v(38.32, 23.2) * mm, "end": v(38.24, 23.35) * mm});
            skLineSegment(sketch, "E401", {"start": v(38.24, 23.35) * mm, "end": v(38.16, 23.5) * mm});
            skLineSegment(sketch, "E402", {"start": v(38.16, 23.5) * mm, "end": v(38.12, 23.57) * mm});
            skLineSegment(sketch, "E403", {"start": v(38.12, 23.57) * mm, "end": v(38.26, 23.65) * mm});
            skLineSegment(sketch, "E404", {"start": v(38.26, 23.65) * mm, "end": v(38.4, 23.74) * mm});
            skLineSegment(sketch, "E405", {"start": v(38.4, 23.74) * mm, "end": v(38.55, 23.83) * mm});
            skLineSegment(sketch, "E406", {"start": v(38.55, 23.83) * mm, "end": v(38.69, 23.91) * mm});
            skLineSegment(sketch, "E407", {"start": v(38.69, 23.91) * mm, "end": v(38.83, 24) * mm});
            skLineSegment(sketch, "E408", {"start": v(38.83, 24) * mm, "end": v(38.98, 24.09) * mm});
            skLineSegment(sketch, "E409", {"start": v(38.98, 24.09) * mm, "end": v(39.12, 24.17) * mm});
            skLineSegment(sketch, "E410", {"start": v(39.12, 24.17) * mm, "end": v(39.26, 24.26) * mm});
            skLineSegment(sketch, "E411", {"start": v(39.26, 24.26) * mm, "end": v(39.4, 24.35) * mm});
            skLineSegment(sketch, "E412", {"start": v(39.4, 24.35) * mm, "end": v(39.55, 24.44) * mm});
            skLineSegment(sketch, "E413", {"start": v(39.55, 24.44) * mm, "end": v(39.7, 24.52) * mm});
            skLineSegment(sketch, "E414", {"start": v(39.7, 24.52) * mm, "end": v(39.84, 24.61) * mm});
            skLineSegment(sketch, "E415", {"start": v(39.84, 24.61) * mm, "end": v(40, 24.7) * mm});
            skLineSegment(sketch, "E416", {"start": v(40, 24.7) * mm, "end": v(40.12, 24.82) * mm});
            skLineSegment(sketch, "E417", {"start": v(40.12, 24.82) * mm, "end": v(40.21, 24.97) * mm});
            skLineSegment(sketch, "E418", {"start": v(40.21, 24.97) * mm, "end": v(40.27, 25.13) * mm});
            skLineSegment(sketch, "E419", {"start": v(40.27, 25.13) * mm, "end": v(40.28, 25.3) * mm});
            skLineSegment(sketch, "E420", {"start": v(40.28, 25.3) * mm, "end": v(40.24, 25.47) * mm});
            skLineSegment(sketch, "E421", {"start": v(40.24, 25.47) * mm, "end": v(40.16, 25.63) * mm});
            skLineSegment(sketch, "E422", {"start": v(40.16, 25.63) * mm, "end": v(40.04, 25.76) * mm});
            skLineSegment(sketch, "E423", {"start": v(40.04, 25.76) * mm, "end": v(39.9, 25.85) * mm});
            skLineSegment(sketch, "E424", {"start": v(39.9, 25.85) * mm, "end": v(39.73, 25.9) * mm});
            skLineSegment(sketch, "E425", {"start": v(39.73, 25.9) * mm, "end": v(39.62, 25.91) * mm});
            skLineSegment(sketch, "E426", {"start": v(39.62, 25.91) * mm, "end": v(39.45, 25.9) * mm});
            skLineSegment(sketch, "E427", {"start": v(39.45, 25.9) * mm, "end": v(39.3, 25.83) * mm});
            skLineSegment(sketch, "E428", {"start": v(39.3, 25.83) * mm, "end": v(39.14, 25.73) * mm});
            skLineSegment(sketch, "E429", {"start": v(39.14, 25.73) * mm, "end": v(39, 25.64) * mm});
            skLineSegment(sketch, "E430", {"start": v(39, 25.64) * mm, "end": v(38.86, 25.55) * mm});
            skLineSegment(sketch, "E431", {"start": v(38.86, 25.55) * mm, "end": v(38.72, 25.46) * mm});
            skLineSegment(sketch, "E432", {"start": v(38.72, 25.46) * mm, "end": v(38.58, 25.37) * mm});
            skLineSegment(sketch, "E433", {"start": v(38.58, 25.37) * mm, "end": v(38.44, 25.28) * mm});
            skLineSegment(sketch, "E434", {"start": v(38.44, 25.28) * mm, "end": v(38.3, 25.18) * mm});
            skLineSegment(sketch, "E435", {"start": v(38.3, 25.18) * mm, "end": v(38.15, 25.1) * mm});
            skLineSegment(sketch, "E436", {"start": v(38.15, 25.1) * mm, "end": v(38.01, 25) * mm});
            skLineSegment(sketch, "E437", {"start": v(38.01, 25) * mm, "end": v(37.87, 24.91) * mm});
            skLineSegment(sketch, "E438", {"start": v(37.87, 24.91) * mm, "end": v(37.73, 24.82) * mm});
            skLineSegment(sketch, "E439", {"start": v(37.73, 24.82) * mm, "end": v(37.6, 24.73) * mm});
            skLineSegment(sketch, "E440", {"start": v(37.6, 24.73) * mm, "end": v(37.45, 24.64) * mm});
            skLineSegment(sketch, "E441", {"start": v(37.45, 24.64) * mm, "end": v(37.35, 24.78) * mm});
            skLineSegment(sketch, "E442", {"start": v(37.35, 24.78) * mm, "end": v(37.26, 24.91) * mm});
            skLineSegment(sketch, "E443", {"start": v(37.26, 24.91) * mm, "end": v(37.17, 25.05) * mm});
            skLineSegment(sketch, "E444", {"start": v(37.17, 25.05) * mm, "end": v(37.07, 25.2) * mm});
            skLineSegment(sketch, "E445", {"start": v(37.07, 25.2) * mm, "end": v(36.98, 25.33) * mm});
            skLineSegment(sketch, "E446", {"start": v(36.98, 25.33) * mm, "end": v(36.89, 25.47) * mm});
            skLineSegment(sketch, "E447", {"start": v(36.89, 25.47) * mm, "end": v(36.8, 25.6) * mm});
            skLineSegment(sketch, "E448", {"start": v(36.8, 25.6) * mm, "end": v(36.7, 25.74) * mm});
            skLineSegment(sketch, "E449", {"start": v(36.7, 25.74) * mm, "end": v(36.6, 25.88) * mm});
            skLineSegment(sketch, "E450", {"start": v(36.6, 25.88) * mm, "end": v(36.52, 26.02) * mm});
            skLineSegment(sketch, "E451", {"start": v(36.52, 26.02) * mm, "end": v(36.42, 26.16) * mm});
            skLineSegment(sketch, "E452", {"start": v(36.42, 26.16) * mm, "end": v(36.38, 26.22) * mm});
            skLineSegment(sketch, "E453", {"start": v(36.38, 26.22) * mm, "end": v(36.51, 26.32) * mm});
            skLineSegment(sketch, "E454", {"start": v(36.51, 26.32) * mm, "end": v(36.65, 26.41) * mm});
            skLineSegment(sketch, "E455", {"start": v(36.65, 26.41) * mm, "end": v(36.79, 26.51) * mm});
            skLineSegment(sketch, "E456", {"start": v(36.79, 26.51) * mm, "end": v(36.93, 26.6) * mm});
            skLineSegment(sketch, "E457", {"start": v(36.93, 26.6) * mm, "end": v(37.06, 26.7) * mm});
            skLineSegment(sketch, "E458", {"start": v(37.06, 26.7) * mm, "end": v(37.2, 26.8) * mm});
            skLineSegment(sketch, "E459", {"start": v(37.2, 26.8) * mm, "end": v(37.34, 26.9) * mm});
            skLineSegment(sketch, "E460", {"start": v(37.34, 26.9) * mm, "end": v(37.47, 27) * mm});
            skLineSegment(sketch, "E461", {"start": v(37.47, 27) * mm, "end": v(37.61, 27.1) * mm});
            skLineSegment(sketch, "E462", {"start": v(37.61, 27.1) * mm, "end": v(37.75, 27.2) * mm});
            skLineSegment(sketch, "E463", {"start": v(37.75, 27.2) * mm, "end": v(37.88, 27.29) * mm});
            skLineSegment(sketch, "E464", {"start": v(37.88, 27.29) * mm, "end": v(38.02, 27.38) * mm});
            skLineSegment(sketch, "E465", {"start": v(38.02, 27.38) * mm, "end": v(38.17, 27.49) * mm});
            skLineSegment(sketch, "E466", {"start": v(38.17, 27.49) * mm, "end": v(38.29, 27.61) * mm});
            skLineSegment(sketch, "E467", {"start": v(38.29, 27.61) * mm, "end": v(38.37, 27.77) * mm});
            skLineSegment(sketch, "E468", {"start": v(38.37, 27.77) * mm, "end": v(38.41, 27.93) * mm});
            skLineSegment(sketch, "E469", {"start": v(38.41, 27.93) * mm, "end": v(38.41, 28.1) * mm});
            skLineSegment(sketch, "E470", {"start": v(38.41, 28.1) * mm, "end": v(38.36, 28.27) * mm});
            skLineSegment(sketch, "E471", {"start": v(38.36, 28.27) * mm, "end": v(38.27, 28.42) * mm});
            skLineSegment(sketch, "E472", {"start": v(38.27, 28.42) * mm, "end": v(38.14, 28.54) * mm});
            skLineSegment(sketch, "E473", {"start": v(38.14, 28.54) * mm, "end": v(38, 28.62) * mm});
            skLineSegment(sketch, "E474", {"start": v(38, 28.62) * mm, "end": v(37.82, 28.66) * mm});
            skLineSegment(sketch, "E475", {"start": v(37.82, 28.66) * mm, "end": v(37.75, 28.67) * mm});
            skLineSegment(sketch, "E476", {"start": v(37.75, 28.67) * mm, "end": v(37.58, 28.64) * mm});
            skLineSegment(sketch, "E477", {"start": v(37.58, 28.64) * mm, "end": v(37.42, 28.58) * mm});
            skLineSegment(sketch, "E478", {"start": v(37.42, 28.58) * mm, "end": v(37.29, 28.48) * mm});
            skLineSegment(sketch, "E479", {"start": v(37.29, 28.48) * mm, "end": v(37.15, 28.38) * mm});
            skLineSegment(sketch, "E480", {"start": v(37.15, 28.38) * mm, "end": v(37.02, 28.28) * mm});
            skLineSegment(sketch, "E481", {"start": v(37.02, 28.28) * mm, "end": v(36.88, 28.18) * mm});
            skLineSegment(sketch, "E482", {"start": v(36.88, 28.18) * mm, "end": v(36.75, 28.08) * mm});
            skLineSegment(sketch, "E483", {"start": v(36.75, 28.08) * mm, "end": v(36.61, 27.98) * mm});
            skLineSegment(sketch, "E484", {"start": v(36.61, 27.98) * mm, "end": v(36.48, 27.88) * mm});
            skLineSegment(sketch, "E485", {"start": v(36.48, 27.88) * mm, "end": v(36.35, 27.78) * mm});
            skLineSegment(sketch, "E486", {"start": v(36.35, 27.78) * mm, "end": v(36.21, 27.68) * mm});
            skLineSegment(sketch, "E487", {"start": v(36.21, 27.68) * mm, "end": v(36.08, 27.58) * mm});
            skLineSegment(sketch, "E488", {"start": v(36.08, 27.58) * mm, "end": v(35.94, 27.48) * mm});
            skLineSegment(sketch, "E489", {"start": v(35.94, 27.48) * mm, "end": v(35.8, 27.38) * mm});
            skLineSegment(sketch, "E490", {"start": v(35.8, 27.38) * mm, "end": v(35.67, 27.28) * mm});
            skLineSegment(sketch, "E491", {"start": v(35.67, 27.28) * mm, "end": v(35.63, 27.25) * mm});
            skLineSegment(sketch, "E492", {"start": v(35.63, 27.25) * mm, "end": v(35.53, 27.38) * mm});
            skLineSegment(sketch, "E493", {"start": v(35.53, 27.38) * mm, "end": v(35.43, 27.5) * mm});
            skLineSegment(sketch, "E494", {"start": v(35.43, 27.5) * mm, "end": v(35.33, 27.64) * mm});
            skLineSegment(sketch, "E495", {"start": v(35.33, 27.64) * mm, "end": v(35.22, 27.77) * mm});
            skLineSegment(sketch, "E496", {"start": v(35.22, 27.77) * mm, "end": v(35.12, 27.9) * mm});
            skLineSegment(sketch, "E497", {"start": v(35.12, 27.9) * mm, "end": v(35.02, 28.03) * mm});
            skLineSegment(sketch, "E498", {"start": v(35.02, 28.03) * mm, "end": v(34.92, 28.16) * mm});
            skLineSegment(sketch, "E499", {"start": v(34.92, 28.16) * mm, "end": v(34.81, 28.3) * mm});
            skLineSegment(sketch, "E500", {"start": v(34.81, 28.3) * mm, "end": v(34.71, 28.43) * mm});
            skLineSegment(sketch, "E501", {"start": v(34.71, 28.43) * mm, "end": v(34.61, 28.56) * mm});
            skLineSegment(sketch, "E502", {"start": v(34.61, 28.56) * mm, "end": v(34.5, 28.69) * mm});
            skLineSegment(sketch, "E503", {"start": v(34.5, 28.69) * mm, "end": v(34.46, 28.75) * mm});
            skLineSegment(sketch, "E504", {"start": v(34.46, 28.75) * mm, "end": v(34.59, 28.86) * mm});
            skLineSegment(sketch, "E505", {"start": v(34.59, 28.86) * mm, "end": v(34.72, 28.96) * mm});
            skLineSegment(sketch, "E506", {"start": v(34.72, 28.96) * mm, "end": v(34.85, 29.07) * mm});
            skLineSegment(sketch, "E507", {"start": v(34.85, 29.07) * mm, "end": v(34.98, 29.18) * mm});
            skLineSegment(sketch, "E508", {"start": v(34.98, 29.18) * mm, "end": v(35.1, 29.28) * mm});
            skLineSegment(sketch, "E509", {"start": v(35.1, 29.28) * mm, "end": v(35.24, 29.39) * mm});
            skLineSegment(sketch, "E510", {"start": v(35.24, 29.39) * mm, "end": v(35.37, 29.5) * mm});
            skLineSegment(sketch, "E511", {"start": v(35.37, 29.5) * mm, "end": v(35.5, 29.6) * mm});
            skLineSegment(sketch, "E512", {"start": v(35.5, 29.6) * mm, "end": v(35.63, 29.7) * mm});
            skLineSegment(sketch, "E513", {"start": v(35.63, 29.7) * mm, "end": v(35.76, 29.81) * mm});
            skLineSegment(sketch, "E514", {"start": v(35.76, 29.81) * mm, "end": v(35.89, 29.92) * mm});
            skLineSegment(sketch, "E515", {"start": v(35.89, 29.92) * mm, "end": v(36.02, 30.03) * mm});
            skLineSegment(sketch, "E516", {"start": v(36.02, 30.03) * mm, "end": v(36.16, 30.14) * mm});
            skLineSegment(sketch, "E517", {"start": v(36.16, 30.14) * mm, "end": v(36.27, 30.27) * mm});
            skLineSegment(sketch, "E518", {"start": v(36.27, 30.27) * mm, "end": v(36.34, 30.43) * mm});
            skLineSegment(sketch, "E519", {"start": v(36.34, 30.43) * mm, "end": v(36.37, 30.6) * mm});
            skLineSegment(sketch, "E520", {"start": v(36.37, 30.6) * mm, "end": v(36.35, 30.77) * mm});
            skLineSegment(sketch, "E521", {"start": v(36.35, 30.77) * mm, "end": v(36.3, 30.94) * mm});
            skLineSegment(sketch, "E522", {"start": v(36.3, 30.94) * mm, "end": v(36.2, 31.08) * mm});
            skLineSegment(sketch, "E523", {"start": v(36.2, 31.08) * mm, "end": v(36.06, 31.19) * mm});
            skLineSegment(sketch, "E524", {"start": v(36.06, 31.19) * mm, "end": v(35.9, 31.26) * mm});
            skLineSegment(sketch, "E525", {"start": v(35.9, 31.26) * mm, "end": v(35.73, 31.29) * mm});
            skLineSegment(sketch, "E526", {"start": v(35.73, 31.29) * mm, "end": v(35.7, 31.29) * mm});
            skLineSegment(sketch, "E527", {"start": v(35.7, 31.29) * mm, "end": v(35.52, 31.26) * mm});
            skLineSegment(sketch, "E528", {"start": v(35.52, 31.26) * mm, "end": v(35.36, 31.2) * mm});
            skLineSegment(sketch, "E529", {"start": v(35.36, 31.2) * mm, "end": v(35.23, 31.08) * mm});
            skLineSegment(sketch, "E530", {"start": v(35.23, 31.08) * mm, "end": v(35.1, 30.98) * mm});
            skLineSegment(sketch, "E531", {"start": v(35.1, 30.98) * mm, "end": v(34.97, 30.87) * mm});
            skLineSegment(sketch, "E532", {"start": v(34.97, 30.87) * mm, "end": v(34.84, 30.75) * mm});
            skLineSegment(sketch, "E533", {"start": v(34.84, 30.75) * mm, "end": v(34.72, 30.65) * mm});
            skLineSegment(sketch, "E534", {"start": v(34.72, 30.65) * mm, "end": v(34.6, 30.54) * mm});
            skLineSegment(sketch, "E535", {"start": v(34.6, 30.54) * mm, "end": v(34.46, 30.43) * mm});
            skLineSegment(sketch, "E536", {"start": v(34.46, 30.43) * mm, "end": v(34.34, 30.32) * mm});
            skLineSegment(sketch, "E537", {"start": v(34.34, 30.32) * mm, "end": v(34.21, 30.2) * mm});
            skLineSegment(sketch, "E538", {"start": v(34.21, 30.2) * mm, "end": v(34.08, 30.1) * mm});
            skLineSegment(sketch, "E539", {"start": v(34.08, 30.1) * mm, "end": v(33.96, 29.99) * mm});
            skLineSegment(sketch, "E540", {"start": v(33.96, 29.99) * mm, "end": v(33.83, 29.88) * mm});
            skLineSegment(sketch, "E541", {"start": v(33.83, 29.88) * mm, "end": v(33.7, 29.77) * mm});
            skLineSegment(sketch, "E542", {"start": v(33.7, 29.77) * mm, "end": v(33.65, 29.72) * mm});
            skLineSegment(sketch, "E543", {"start": v(33.65, 29.72) * mm, "end": v(33.53, 29.84) * mm});
            skLineSegment(sketch, "E544", {"start": v(33.53, 29.84) * mm, "end": v(33.42, 29.97) * mm});
            skLineSegment(sketch, "E545", {"start": v(33.42, 29.97) * mm, "end": v(33.31, 30.1) * mm});
            skLineSegment(sketch, "E546", {"start": v(33.31, 30.1) * mm, "end": v(33.2, 30.21) * mm});
            skLineSegment(sketch, "E547", {"start": v(33.2, 30.21) * mm, "end": v(33.09, 30.34) * mm});
            skLineSegment(sketch, "E548", {"start": v(33.09, 30.34) * mm, "end": v(32.98, 30.46) * mm});
            skLineSegment(sketch, "E549", {"start": v(32.98, 30.46) * mm, "end": v(32.87, 30.59) * mm});
            skLineSegment(sketch, "E550", {"start": v(32.87, 30.59) * mm, "end": v(32.75, 30.7) * mm});
            skLineSegment(sketch, "E551", {"start": v(32.75, 30.7) * mm, "end": v(32.64, 30.83) * mm});
            skLineSegment(sketch, "E552", {"start": v(32.64, 30.83) * mm, "end": v(32.53, 30.96) * mm});
            skLineSegment(sketch, "E553", {"start": v(32.53, 30.96) * mm, "end": v(32.42, 31.08) * mm});
            skLineSegment(sketch, "E554", {"start": v(32.42, 31.08) * mm, "end": v(32.37, 31.14) * mm});
            skLineSegment(sketch, "E555", {"start": v(32.37, 31.14) * mm, "end": v(32.49, 31.25) * mm});
            skLineSegment(sketch, "E556", {"start": v(32.49, 31.25) * mm, "end": v(32.6, 31.37) * mm});
            skLineSegment(sketch, "E557", {"start": v(32.6, 31.37) * mm, "end": v(32.73, 31.49) * mm});
            skLineSegment(sketch, "E558", {"start": v(32.73, 31.49) * mm, "end": v(32.85, 31.6) * mm});
            skLineSegment(sketch, "E559", {"start": v(32.85, 31.6) * mm, "end": v(32.98, 31.71) * mm});
            skLineSegment(sketch, "E560", {"start": v(32.98, 31.71) * mm, "end": v(33.1, 31.83) * mm});
            skLineSegment(sketch, "E561", {"start": v(33.1, 31.83) * mm, "end": v(33.22, 31.94) * mm});
            skLineSegment(sketch, "E562", {"start": v(33.22, 31.94) * mm, "end": v(33.34, 32.06) * mm});
            skLineSegment(sketch, "E563", {"start": v(33.34, 32.06) * mm, "end": v(33.47, 32.18) * mm});
            skLineSegment(sketch, "E564", {"start": v(33.47, 32.18) * mm, "end": v(33.59, 32.29) * mm});
            skLineSegment(sketch, "E565", {"start": v(33.59, 32.29) * mm, "end": v(33.71, 32.4) * mm});
            skLineSegment(sketch, "E566", {"start": v(33.71, 32.4) * mm, "end": v(33.84, 32.52) * mm});
            skLineSegment(sketch, "E567", {"start": v(33.84, 32.52) * mm, "end": v(33.96, 32.64) * mm});
            skLineSegment(sketch, "E568", {"start": v(33.96, 32.64) * mm, "end": v(34.07, 32.78) * mm});
            skLineSegment(sketch, "E569", {"start": v(34.07, 32.78) * mm, "end": v(34.13, 32.95) * mm});
            skLineSegment(sketch, "E570", {"start": v(34.13, 32.95) * mm, "end": v(34.15, 33.12) * mm});
            skLineSegment(sketch, "E571", {"start": v(34.15, 33.12) * mm, "end": v(34.12, 33.3) * mm});
            skLineSegment(sketch, "E572", {"start": v(34.12, 33.3) * mm, "end": v(34.05, 33.45) * mm});
            skLineSegment(sketch, "E573", {"start": v(34.05, 33.45) * mm, "end": v(33.93, 33.58) * mm});
            skLineSegment(sketch, "E574", {"start": v(33.93, 33.58) * mm, "end": v(33.8, 33.68) * mm});
            skLineSegment(sketch, "E575", {"start": v(33.8, 33.68) * mm, "end": v(33.63, 33.74) * mm});
            skLineSegment(sketch, "E576", {"start": v(33.63, 33.74) * mm, "end": v(33.5, 33.76) * mm});
            skLineSegment(sketch, "E577", {"start": v(33.5, 33.76) * mm, "end": v(33.32, 33.74) * mm});
            skLineSegment(sketch, "E578", {"start": v(33.32, 33.74) * mm, "end": v(33.16, 33.68) * mm});
            skLineSegment(sketch, "E579", {"start": v(33.16, 33.68) * mm, "end": v(33.02, 33.57) * mm});
            skLineSegment(sketch, "E580", {"start": v(33.02, 33.57) * mm, "end": v(32.9, 33.45) * mm});
            skLineSegment(sketch, "E581", {"start": v(32.9, 33.45) * mm, "end": v(32.78, 33.34) * mm});
            skLineSegment(sketch, "E582", {"start": v(32.78, 33.34) * mm, "end": v(32.66, 33.22) * mm});
            skLineSegment(sketch, "E583", {"start": v(32.66, 33.22) * mm, "end": v(32.54, 33.1) * mm});
            skLineSegment(sketch, "E584", {"start": v(32.54, 33.1) * mm, "end": v(32.43, 32.98) * mm});
            skLineSegment(sketch, "E585", {"start": v(32.43, 32.98) * mm, "end": v(32.3, 32.86) * mm});
            skLineSegment(sketch, "E586", {"start": v(32.3, 32.86) * mm, "end": v(32.19, 32.74) * mm});
            skLineSegment(sketch, "E587", {"start": v(32.19, 32.74) * mm, "end": v(32.07, 32.63) * mm});
            skLineSegment(sketch, "E588", {"start": v(32.07, 32.63) * mm, "end": v(31.95, 32.5) * mm});
            skLineSegment(sketch, "E589", {"start": v(31.95, 32.5) * mm, "end": v(31.83, 32.39) * mm});
            skLineSegment(sketch, "E590", {"start": v(31.83, 32.39) * mm, "end": v(31.71, 32.27) * mm});
            skLineSegment(sketch, "E591", {"start": v(31.71, 32.27) * mm, "end": v(31.6, 32.15) * mm});
            skLineSegment(sketch, "E592", {"start": v(31.6, 32.15) * mm, "end": v(31.49, 32.05) * mm});
            skLineSegment(sketch, "E593", {"start": v(31.49, 32.05) * mm, "end": v(31.37, 32.17) * mm});
            skLineSegment(sketch, "E594", {"start": v(31.37, 32.17) * mm, "end": v(31.25, 32.28) * mm});
            skLineSegment(sketch, "E595", {"start": v(31.25, 32.28) * mm, "end": v(31.13, 32.4) * mm});
            skLineSegment(sketch, "E596", {"start": v(31.13, 32.4) * mm, "end": v(31, 32.51) * mm});
            skLineSegment(sketch, "E597", {"start": v(31, 32.51) * mm, "end": v(30.89, 32.63) * mm});
            skLineSegment(sketch, "E598", {"start": v(30.89, 32.63) * mm, "end": v(30.77, 32.74) * mm});
            skLineSegment(sketch, "E599", {"start": v(30.77, 32.74) * mm, "end": v(30.65, 32.86) * mm});
            skLineSegment(sketch, "E600", {"start": v(30.65, 32.86) * mm, "end": v(30.53, 32.97) * mm});
            skLineSegment(sketch, "E601", {"start": v(30.53, 32.97) * mm, "end": v(30.41, 33.1) * mm});
            skLineSegment(sketch, "E602", {"start": v(30.41, 33.1) * mm, "end": v(30.3, 33.2) * mm});
            skLineSegment(sketch, "E603", {"start": v(30.3, 33.2) * mm, "end": v(30.17, 33.32) * mm});
            skLineSegment(sketch, "E604", {"start": v(30.17, 33.32) * mm, "end": v(30.11, 33.38) * mm});
            skLineSegment(sketch, "E605", {"start": v(30.11, 33.38) * mm, "end": v(30.23, 33.5) * mm});
            skLineSegment(sketch, "E606", {"start": v(30.23, 33.5) * mm, "end": v(30.34, 33.62) * mm});
            skLineSegment(sketch, "E607", {"start": v(30.34, 33.62) * mm, "end": v(30.46, 33.75) * mm});
            skLineSegment(sketch, "E608", {"start": v(30.46, 33.75) * mm, "end": v(30.57, 33.87) * mm});
            skLineSegment(sketch, "E609", {"start": v(30.57, 33.87) * mm, "end": v(30.68, 34) * mm});
            skLineSegment(sketch, "E610", {"start": v(30.68, 34) * mm, "end": v(30.8, 34.12) * mm});
            skLineSegment(sketch, "E611", {"start": v(30.8, 34.12) * mm, "end": v(30.91, 34.24) * mm});
            skLineSegment(sketch, "E612", {"start": v(30.91, 34.24) * mm, "end": v(31.02, 34.36) * mm});
            skLineSegment(sketch, "E613", {"start": v(31.02, 34.36) * mm, "end": v(31.14, 34.49) * mm});
            skLineSegment(sketch, "E614", {"start": v(31.14, 34.49) * mm, "end": v(31.25, 34.6) * mm});
            skLineSegment(sketch, "E615", {"start": v(31.25, 34.6) * mm, "end": v(31.37, 34.73) * mm});
            skLineSegment(sketch, "E616", {"start": v(31.37, 34.73) * mm, "end": v(31.48, 34.86) * mm});
            skLineSegment(sketch, "E617", {"start": v(31.48, 34.86) * mm, "end": v(31.6, 34.99) * mm});
            skLineSegment(sketch, "E618", {"start": v(31.6, 34.99) * mm, "end": v(31.7, 35.14) * mm});
            skLineSegment(sketch, "E619", {"start": v(31.7, 35.14) * mm, "end": v(31.74, 35.3) * mm});
            skLineSegment(sketch, "E620", {"start": v(31.74, 35.3) * mm, "end": v(31.75, 35.48) * mm});
            skLineSegment(sketch, "E621", {"start": v(31.75, 35.48) * mm, "end": v(31.7, 35.64) * mm});
            skLineSegment(sketch, "E622", {"start": v(31.7, 35.64) * mm, "end": v(31.63, 35.8) * mm});
            skLineSegment(sketch, "E623", {"start": v(31.63, 35.8) * mm, "end": v(31.5, 35.92) * mm});
            skLineSegment(sketch, "E624", {"start": v(31.5, 35.92) * mm, "end": v(31.36, 36.01) * mm});
            skLineSegment(sketch, "E625", {"start": v(31.36, 36.01) * mm, "end": v(31.2, 36.06) * mm});
            skLineSegment(sketch, "E626", {"start": v(31.2, 36.06) * mm, "end": v(31.09, 36.07) * mm});
            skLineSegment(sketch, "E627", {"start": v(31.09, 36.07) * mm, "end": v(30.92, 36.05) * mm});
            skLineSegment(sketch, "E628", {"start": v(30.92, 36.05) * mm, "end": v(30.76, 35.98) * mm});
            skLineSegment(sketch, "E629", {"start": v(30.76, 35.98) * mm, "end": v(30.62, 35.87) * mm});
            skLineSegment(sketch, "E630", {"start": v(30.62, 35.87) * mm, "end": v(30.5, 35.74) * mm});
            skLineSegment(sketch, "E631", {"start": v(30.5, 35.74) * mm, "end": v(30.4, 35.61) * mm});
            skLineSegment(sketch, "E632", {"start": v(30.4, 35.61) * mm, "end": v(30.28, 35.49) * mm});
            skLineSegment(sketch, "E633", {"start": v(30.28, 35.49) * mm, "end": v(30.17, 35.36) * mm});
            skLineSegment(sketch, "E634", {"start": v(30.17, 35.36) * mm, "end": v(30.06, 35.24) * mm});
            skLineSegment(sketch, "E635", {"start": v(30.06, 35.24) * mm, "end": v(29.95, 35.11) * mm});
            skLineSegment(sketch, "E636", {"start": v(29.95, 35.11) * mm, "end": v(29.84, 34.98) * mm});
            skLineSegment(sketch, "E637", {"start": v(29.84, 34.98) * mm, "end": v(29.73, 34.86) * mm});
            skLineSegment(sketch, "E638", {"start": v(29.73, 34.86) * mm, "end": v(29.62, 34.73) * mm});
            skLineSegment(sketch, "E639", {"start": v(29.62, 34.73) * mm, "end": v(29.5, 34.6) * mm});
            skLineSegment(sketch, "E640", {"start": v(29.5, 34.6) * mm, "end": v(29.4, 34.48) * mm});
            skLineSegment(sketch, "E641", {"start": v(29.4, 34.48) * mm, "end": v(29.29, 34.35) * mm});
            skLineSegment(sketch, "E642", {"start": v(29.29, 34.35) * mm, "end": v(29.17, 34.22) * mm});
            skLineSegment(sketch, "E643", {"start": v(29.17, 34.22) * mm, "end": v(29.05, 34.33) * mm});
            skLineSegment(sketch, "E644", {"start": v(29.05, 34.33) * mm, "end": v(28.92, 34.44) * mm});
            skLineSegment(sketch, "E645", {"start": v(28.92, 34.44) * mm, "end": v(28.8, 34.54) * mm});
            skLineSegment(sketch, "E646", {"start": v(28.8, 34.54) * mm, "end": v(28.66, 34.65) * mm});
            skLineSegment(sketch, "E647", {"start": v(28.66, 34.65) * mm, "end": v(28.54, 34.76) * mm});
            skLineSegment(sketch, "E648", {"start": v(28.54, 34.76) * mm, "end": v(28.4, 34.87) * mm});
            skLineSegment(sketch, "E649", {"start": v(28.4, 34.87) * mm, "end": v(28.28, 34.97) * mm});
            skLineSegment(sketch, "E650", {"start": v(28.28, 34.97) * mm, "end": v(28.15, 35.08) * mm});
            skLineSegment(sketch, "E651", {"start": v(28.15, 35.08) * mm, "end": v(28.03, 35.19) * mm});
            skLineSegment(sketch, "E652", {"start": v(28.03, 35.19) * mm, "end": v(27.9, 35.3) * mm});
            skLineSegment(sketch, "E653", {"start": v(27.9, 35.3) * mm, "end": v(27.77, 35.4) * mm});
            skLineSegment(sketch, "E654", {"start": v(27.77, 35.4) * mm, "end": v(27.7, 35.45) * mm});
            skLineSegment(sketch, "E655", {"start": v(27.7, 35.45) * mm, "end": v(27.81, 35.58) * mm});
            skLineSegment(sketch, "E656", {"start": v(27.81, 35.58) * mm, "end": v(27.92, 35.71) * mm});
            skLineSegment(sketch, "E657", {"start": v(27.92, 35.71) * mm, "end": v(28.03, 35.84) * mm});
            skLineSegment(sketch, "E658", {"start": v(28.03, 35.84) * mm, "end": v(28.13, 35.97) * mm});
            skLineSegment(sketch, "E659", {"start": v(28.13, 35.97) * mm, "end": v(28.23, 36.1) * mm});
            skLineSegment(sketch, "E660", {"start": v(28.23, 36.1) * mm, "end": v(28.34, 36.24) * mm});
            skLineSegment(sketch, "E661", {"start": v(28.34, 36.24) * mm, "end": v(28.45, 36.37) * mm});
            skLineSegment(sketch, "E662", {"start": v(28.45, 36.37) * mm, "end": v(28.55, 36.5) * mm});
            skLineSegment(sketch, "E663", {"start": v(28.55, 36.5) * mm, "end": v(28.66, 36.63) * mm});
            skLineSegment(sketch, "E664", {"start": v(28.66, 36.63) * mm, "end": v(28.76, 36.76) * mm});
            skLineSegment(sketch, "E665", {"start": v(28.76, 36.76) * mm, "end": v(28.87, 36.89) * mm});
            skLineSegment(sketch, "E666", {"start": v(28.87, 36.89) * mm, "end": v(28.97, 37.02) * mm});
            skLineSegment(sketch, "E667", {"start": v(28.97, 37.02) * mm, "end": v(29.08, 37.16) * mm});
            skLineSegment(sketch, "E668", {"start": v(29.08, 37.16) * mm, "end": v(29.16, 37.32) * mm});
            skLineSegment(sketch, "E669", {"start": v(29.16, 37.32) * mm, "end": v(29.2, 37.49) * mm});
            skLineSegment(sketch, "E670", {"start": v(29.2, 37.49) * mm, "end": v(29.2, 37.66) * mm});
            skLineSegment(sketch, "E671", {"start": v(29.2, 37.66) * mm, "end": v(29.14, 37.82) * mm});
            skLineSegment(sketch, "E672", {"start": v(29.14, 37.82) * mm, "end": v(29.05, 37.97) * mm});
            skLineSegment(sketch, "E673", {"start": v(29.05, 37.97) * mm, "end": v(28.92, 38.09) * mm});
            skLineSegment(sketch, "E674", {"start": v(28.92, 38.09) * mm, "end": v(28.77, 38.17) * mm});
            skLineSegment(sketch, "E675", {"start": v(28.77, 38.17) * mm, "end": v(28.6, 38.2) * mm});
            skLineSegment(sketch, "E676", {"start": v(28.6, 38.2) * mm, "end": v(28.53, 38.2) * mm});
            skLineSegment(sketch, "E677", {"start": v(28.53, 38.2) * mm, "end": v(28.36, 38.18) * mm});
            skLineSegment(sketch, "E678", {"start": v(28.36, 38.18) * mm, "end": v(28.2, 38.11) * mm});
            skLineSegment(sketch, "E679", {"start": v(28.2, 38.11) * mm, "end": v(28.06, 38) * mm});
            skLineSegment(sketch, "E680", {"start": v(28.06, 38) * mm, "end": v(27.96, 37.87) * mm});
            skLineSegment(sketch, "E681", {"start": v(27.96, 37.87) * mm, "end": v(27.86, 37.74) * mm});
            skLineSegment(sketch, "E682", {"start": v(27.86, 37.74) * mm, "end": v(27.76, 37.6) * mm});
            skLineSegment(sketch, "E683", {"start": v(27.76, 37.6) * mm, "end": v(27.66, 37.47) * mm});
            skLineSegment(sketch, "E684", {"start": v(27.66, 37.47) * mm, "end": v(27.56, 37.34) * mm});
            skLineSegment(sketch, "E685", {"start": v(27.56, 37.34) * mm, "end": v(27.45, 37.2) * mm});
            skLineSegment(sketch, "E686", {"start": v(27.45, 37.2) * mm, "end": v(27.35, 37.07) * mm});
            skLineSegment(sketch, "E687", {"start": v(27.35, 37.07) * mm, "end": v(27.25, 36.94) * mm});
            skLineSegment(sketch, "E688", {"start": v(27.25, 36.94) * mm, "end": v(27.15, 36.8) * mm});
            skLineSegment(sketch, "E689", {"start": v(27.15, 36.8) * mm, "end": v(27.05, 36.67) * mm});
            skLineSegment(sketch, "E690", {"start": v(27.05, 36.67) * mm, "end": v(26.95, 36.54) * mm});
            skLineSegment(sketch, "E691", {"start": v(26.95, 36.54) * mm, "end": v(26.84, 36.4) * mm});
            skLineSegment(sketch, "E692", {"start": v(26.84, 36.4) * mm, "end": v(26.74, 36.27) * mm});
            skLineSegment(sketch, "E693", {"start": v(26.74, 36.27) * mm, "end": v(26.71, 36.23) * mm});
            skLineSegment(sketch, "E694", {"start": v(26.71, 36.23) * mm, "end": v(26.58, 36.33) * mm});
            skLineSegment(sketch, "E695", {"start": v(26.58, 36.33) * mm, "end": v(26.44, 36.43) * mm});
            skLineSegment(sketch, "E696", {"start": v(26.44, 36.43) * mm, "end": v(26.3, 36.52) * mm});
            skLineSegment(sketch, "E697", {"start": v(26.3, 36.52) * mm, "end": v(26.17, 36.62) * mm});
            skLineSegment(sketch, "E698", {"start": v(26.17, 36.62) * mm, "end": v(26.04, 36.72) * mm});
            skLineSegment(sketch, "E699", {"start": v(26.04, 36.72) * mm, "end": v(25.9, 36.82) * mm});
            skLineSegment(sketch, "E700", {"start": v(25.9, 36.82) * mm, "end": v(25.77, 36.91) * mm});
            skLineSegment(sketch, "E701", {"start": v(25.77, 36.91) * mm, "end": v(25.64, 37.01) * mm});
            skLineSegment(sketch, "E702", {"start": v(25.64, 37.01) * mm, "end": v(25.5, 37.11) * mm});
            skLineSegment(sketch, "E703", {"start": v(25.5, 37.11) * mm, "end": v(25.37, 37.2) * mm});
            skLineSegment(sketch, "E704", {"start": v(25.37, 37.2) * mm, "end": v(25.23, 37.3) * mm});
            skLineSegment(sketch, "E705", {"start": v(25.23, 37.3) * mm, "end": v(25.17, 37.35) * mm});
            skLineSegment(sketch, "E706", {"start": v(25.17, 37.35) * mm, "end": v(25.26, 37.5) * mm});
            skLineSegment(sketch, "E707", {"start": v(25.26, 37.5) * mm, "end": v(25.36, 37.63) * mm});
            skLineSegment(sketch, "E708", {"start": v(25.36, 37.63) * mm, "end": v(25.45, 37.77) * mm});
            skLineSegment(sketch, "E709", {"start": v(25.45, 37.77) * mm, "end": v(25.55, 37.9) * mm});
            skLineSegment(sketch, "E710", {"start": v(25.55, 37.9) * mm, "end": v(25.64, 38.04) * mm});
            skLineSegment(sketch, "E711", {"start": v(25.64, 38.04) * mm, "end": v(25.74, 38.18) * mm});
            skLineSegment(sketch, "E712", {"start": v(25.74, 38.18) * mm, "end": v(25.84, 38.32) * mm});
            skLineSegment(sketch, "E713", {"start": v(25.84, 38.32) * mm, "end": v(25.93, 38.45) * mm});
            skLineSegment(sketch, "E714", {"start": v(25.93, 38.45) * mm, "end": v(26.03, 38.6) * mm});
            skLineSegment(sketch, "E715", {"start": v(26.03, 38.6) * mm, "end": v(26.12, 38.73) * mm});
            skLineSegment(sketch, "E716", {"start": v(26.12, 38.73) * mm, "end": v(26.22, 38.87) * mm});
            skLineSegment(sketch, "E717", {"start": v(26.22, 38.87) * mm, "end": v(26.32, 39) * mm});
            skLineSegment(sketch, "E718", {"start": v(26.32, 39) * mm, "end": v(26.42, 39.16) * mm});
            skLineSegment(sketch, "E719", {"start": v(26.42, 39.16) * mm, "end": v(26.49, 39.32) * mm});
            skLineSegment(sketch, "E720", {"start": v(26.49, 39.32) * mm, "end": v(26.51, 39.49) * mm});
            skLineSegment(sketch, "E721", {"start": v(26.51, 39.49) * mm, "end": v(26.5, 39.66) * mm});
            skLineSegment(sketch, "E722", {"start": v(26.5, 39.66) * mm, "end": v(26.43, 39.82) * mm});
            skLineSegment(sketch, "E723", {"start": v(26.43, 39.82) * mm, "end": v(26.33, 39.96) * mm});
            skLineSegment(sketch, "E724", {"start": v(26.33, 39.96) * mm, "end": v(26.2, 40.07) * mm});
            skLineSegment(sketch, "E725", {"start": v(26.2, 40.07) * mm, "end": v(26.03, 40.14) * mm});
            skLineSegment(sketch, "E726", {"start": v(26.03, 40.14) * mm, "end": v(25.86, 40.16) * mm});
            skLineSegment(sketch, "E727", {"start": v(25.86, 40.16) * mm, "end": v(25.7, 40.14) * mm});
            skLineSegment(sketch, "E728", {"start": v(25.7, 40.14) * mm, "end": v(25.53, 40.08) * mm});
            skLineSegment(sketch, "E729", {"start": v(25.53, 40.08) * mm, "end": v(25.4, 39.97) * mm});
            skLineSegment(sketch, "E730", {"start": v(25.4, 39.97) * mm, "end": v(25.29, 39.84) * mm});
            skLineSegment(sketch, "E731", {"start": v(25.29, 39.84) * mm, "end": v(25.2, 39.7) * mm});
            skLineSegment(sketch, "E732", {"start": v(25.2, 39.7) * mm, "end": v(25.1, 39.57) * mm});
            skLineSegment(sketch, "E733", {"start": v(25.1, 39.57) * mm, "end": v(25.01, 39.43) * mm});
            skLineSegment(sketch, "E734", {"start": v(25.01, 39.43) * mm, "end": v(24.92, 39.29) * mm});
            skLineSegment(sketch, "E735", {"start": v(24.92, 39.29) * mm, "end": v(24.83, 39.14) * mm});
            skLineSegment(sketch, "E736", {"start": v(24.83, 39.14) * mm, "end": v(24.74, 39) * mm});
            skLineSegment(sketch, "E737", {"start": v(24.74, 39) * mm, "end": v(24.65, 38.87) * mm});
            skLineSegment(sketch, "E738", {"start": v(24.65, 38.87) * mm, "end": v(24.55, 38.72) * mm});
            skLineSegment(sketch, "E739", {"start": v(24.55, 38.72) * mm, "end": v(24.46, 38.58) * mm});
            skLineSegment(sketch, "E740", {"start": v(24.46, 38.58) * mm, "end": v(24.37, 38.44) * mm});
            skLineSegment(sketch, "E741", {"start": v(24.37, 38.44) * mm, "end": v(24.28, 38.3) * mm});
            skLineSegment(sketch, "E742", {"start": v(24.28, 38.3) * mm, "end": v(24.19, 38.16) * mm});
            skLineSegment(sketch, "E743", {"start": v(24.19, 38.16) * mm, "end": v(24.12, 38.06) * mm});
            skLineSegment(sketch, "E744", {"start": v(24.12, 38.06) * mm, "end": v(23.98, 38.15) * mm});
            skLineSegment(sketch, "E745", {"start": v(23.98, 38.15) * mm, "end": v(23.84, 38.24) * mm});
            skLineSegment(sketch, "E746", {"start": v(23.84, 38.24) * mm, "end": v(23.7, 38.33) * mm});
            skLineSegment(sketch, "E747", {"start": v(23.7, 38.33) * mm, "end": v(23.55, 38.41) * mm});
            skLineSegment(sketch, "E748", {"start": v(23.55, 38.41) * mm, "end": v(23.41, 38.5) * mm});
            skLineSegment(sketch, "E749", {"start": v(23.41, 38.5) * mm, "end": v(23.27, 38.59) * mm});
            skLineSegment(sketch, "E750", {"start": v(23.27, 38.59) * mm, "end": v(23.13, 38.68) * mm});
            skLineSegment(sketch, "E751", {"start": v(23.13, 38.68) * mm, "end": v(23, 38.77) * mm});
            skLineSegment(sketch, "E752", {"start": v(23, 38.77) * mm, "end": v(22.85, 38.85) * mm});
            skLineSegment(sketch, "E753", {"start": v(22.85, 38.85) * mm, "end": v(22.7, 38.94) * mm});
            skLineSegment(sketch, "E754", {"start": v(22.7, 38.94) * mm, "end": v(22.57, 39.03) * mm});
            skLineSegment(sketch, "E755", {"start": v(22.57, 39.03) * mm, "end": v(22.5, 39.07) * mm});
            skLineSegment(sketch, "E756", {"start": v(22.5, 39.07) * mm, "end": v(22.58, 39.22) * mm});
            skLineSegment(sketch, "E757", {"start": v(22.58, 39.22) * mm, "end": v(22.67, 39.36) * mm});
            skLineSegment(sketch, "E758", {"start": v(22.67, 39.36) * mm, "end": v(22.76, 39.5) * mm});
            skLineSegment(sketch, "E759", {"start": v(22.76, 39.5) * mm, "end": v(22.84, 39.65) * mm});
            skLineSegment(sketch, "E760", {"start": v(22.84, 39.65) * mm, "end": v(22.93, 39.8) * mm});
            skLineSegment(sketch, "E761", {"start": v(22.93, 39.8) * mm, "end": v(23.01, 39.94) * mm});
            skLineSegment(sketch, "E762", {"start": v(23.01, 39.94) * mm, "end": v(23.1, 40.08) * mm});
            skLineSegment(sketch, "E763", {"start": v(23.1, 40.08) * mm, "end": v(23.18, 40.23) * mm});
            skLineSegment(sketch, "E764", {"start": v(23.18, 40.23) * mm, "end": v(23.27, 40.37) * mm});
            skLineSegment(sketch, "E765", {"start": v(23.27, 40.37) * mm, "end": v(23.36, 40.51) * mm});
            skLineSegment(sketch, "E766", {"start": v(23.36, 40.51) * mm, "end": v(23.44, 40.66) * mm});
            skLineSegment(sketch, "E767", {"start": v(23.44, 40.66) * mm, "end": v(23.53, 40.8) * mm});
            skLineSegment(sketch, "E768", {"start": v(23.53, 40.8) * mm, "end": v(23.62, 40.96) * mm});
            skLineSegment(sketch, "E769", {"start": v(23.62, 40.96) * mm, "end": v(23.68, 41.12) * mm});
            skLineSegment(sketch, "E770", {"start": v(23.68, 41.12) * mm, "end": v(23.7, 41.3) * mm});
            skLineSegment(sketch, "E771", {"start": v(23.7, 41.3) * mm, "end": v(23.66, 41.47) * mm});
            skLineSegment(sketch, "E772", {"start": v(23.66, 41.47) * mm, "end": v(23.59, 41.62) * mm});
            skLineSegment(sketch, "E773", {"start": v(23.59, 41.62) * mm, "end": v(23.48, 41.75) * mm});
            skLineSegment(sketch, "E774", {"start": v(23.48, 41.75) * mm, "end": v(23.33, 41.85) * mm});
            skLineSegment(sketch, "E775", {"start": v(23.33, 41.85) * mm, "end": v(23.17, 41.91) * mm});
            skLineSegment(sketch, "E776", {"start": v(23.17, 41.91) * mm, "end": v(23.03, 41.93) * mm});
            skLineSegment(sketch, "E777", {"start": v(23.03, 41.93) * mm, "end": v(22.86, 41.9) * mm});
            skLineSegment(sketch, "E778", {"start": v(22.86, 41.9) * mm, "end": v(22.7, 41.84) * mm});
            skLineSegment(sketch, "E779", {"start": v(22.7, 41.84) * mm, "end": v(22.56, 41.73) * mm});
            skLineSegment(sketch, "E780", {"start": v(22.56, 41.73) * mm, "end": v(22.46, 41.6) * mm});
            skLineSegment(sketch, "E781", {"start": v(22.46, 41.6) * mm, "end": v(22.38, 41.45) * mm});
            skLineSegment(sketch, "E782", {"start": v(22.38, 41.45) * mm, "end": v(22.3, 41.3) * mm});
            skLineSegment(sketch, "E783", {"start": v(22.3, 41.3) * mm, "end": v(22.21, 41.15) * mm});
            skLineSegment(sketch, "E784", {"start": v(22.21, 41.15) * mm, "end": v(22.13, 41) * mm});
            skLineSegment(sketch, "E785", {"start": v(22.13, 41) * mm, "end": v(22.05, 40.86) * mm});
            skLineSegment(sketch, "E786", {"start": v(22.05, 40.86) * mm, "end": v(21.97, 40.71) * mm});
            skLineSegment(sketch, "E787", {"start": v(21.97, 40.71) * mm, "end": v(21.88, 40.57) * mm});
            skLineSegment(sketch, "E788", {"start": v(21.88, 40.57) * mm, "end": v(21.8, 40.42) * mm});
            skLineSegment(sketch, "E789", {"start": v(21.8, 40.42) * mm, "end": v(21.72, 40.27) * mm});
            skLineSegment(sketch, "E790", {"start": v(21.72, 40.27) * mm, "end": v(21.64, 40.13) * mm});
            skLineSegment(sketch, "E791", {"start": v(21.64, 40.13) * mm, "end": v(21.56, 39.98) * mm});
            skLineSegment(sketch, "E792", {"start": v(21.56, 39.98) * mm, "end": v(21.47, 39.83) * mm});
            skLineSegment(sketch, "E793", {"start": v(21.47, 39.83) * mm, "end": v(21.4, 39.7) * mm});
            skLineSegment(sketch, "E794", {"start": v(21.4, 39.7) * mm, "end": v(21.26, 39.78) * mm});
            skLineSegment(sketch, "E795", {"start": v(21.26, 39.78) * mm, "end": v(21.1, 39.86) * mm});
            skLineSegment(sketch, "E796", {"start": v(21.1, 39.86) * mm, "end": v(20.96, 39.94) * mm});
            skLineSegment(sketch, "E797", {"start": v(20.96, 39.94) * mm, "end": v(20.82, 40.02) * mm});
            skLineSegment(sketch, "E798", {"start": v(20.82, 40.02) * mm, "end": v(20.67, 40.1) * mm});
            skLineSegment(sketch, "E799", {"start": v(20.67, 40.1) * mm, "end": v(20.52, 40.17) * mm});
            skLineSegment(sketch, "E800", {"start": v(20.52, 40.17) * mm, "end": v(20.38, 40.25) * mm});
            skLineSegment(sketch, "E801", {"start": v(20.38, 40.25) * mm, "end": v(20.23, 40.33) * mm});
            skLineSegment(sketch, "E802", {"start": v(20.23, 40.33) * mm, "end": v(20.08, 40.4) * mm});
            skLineSegment(sketch, "E803", {"start": v(20.08, 40.4) * mm, "end": v(19.93, 40.49) * mm});
            skLineSegment(sketch, "E804", {"start": v(19.93, 40.49) * mm, "end": v(19.79, 40.56) * mm});
            skLineSegment(sketch, "E805", {"start": v(19.79, 40.56) * mm, "end": v(19.72, 40.6) * mm});
            skLineSegment(sketch, "E806", {"start": v(19.72, 40.6) * mm, "end": v(19.8, 40.75) * mm});
            skLineSegment(sketch, "E807", {"start": v(19.8, 40.75) * mm, "end": v(19.87, 40.9) * mm});
            skLineSegment(sketch, "E808", {"start": v(19.87, 40.9) * mm, "end": v(19.94, 41.05) * mm});
            skLineSegment(sketch, "E809", {"start": v(19.94, 41.05) * mm, "end": v(20.02, 41.2) * mm});
            skLineSegment(sketch, "E810", {"start": v(20.02, 41.2) * mm, "end": v(20.1, 41.35) * mm});
            skLineSegment(sketch, "E811", {"start": v(20.1, 41.35) * mm, "end": v(20.17, 41.5) * mm});
            skLineSegment(sketch, "E812", {"start": v(20.17, 41.5) * mm, "end": v(20.25, 41.65) * mm});
            skLineSegment(sketch, "E813", {"start": v(20.25, 41.65) * mm, "end": v(20.32, 41.8) * mm});
            skLineSegment(sketch, "E814", {"start": v(20.32, 41.8) * mm, "end": v(20.4, 41.95) * mm});
            skLineSegment(sketch, "E815", {"start": v(20.4, 41.95) * mm, "end": v(20.47, 42.1) * mm});
            skLineSegment(sketch, "E816", {"start": v(20.47, 42.1) * mm, "end": v(20.55, 42.25) * mm});
            skLineSegment(sketch, "E817", {"start": v(20.55, 42.25) * mm, "end": v(20.62, 42.4) * mm});
            skLineSegment(sketch, "E818", {"start": v(20.62, 42.4) * mm, "end": v(20.7, 42.56) * mm});
            skLineSegment(sketch, "E819", {"start": v(20.7, 42.56) * mm, "end": v(20.75, 42.73) * mm});
            skLineSegment(sketch, "E820", {"start": v(20.75, 42.73) * mm, "end": v(20.75, 42.9) * mm});
            skLineSegment(sketch, "E821", {"start": v(20.75, 42.9) * mm, "end": v(20.71, 43.07) * mm});
            skLineSegment(sketch, "E822", {"start": v(20.71, 43.07) * mm, "end": v(20.63, 43.22) * mm});
            skLineSegment(sketch, "E823", {"start": v(20.63, 43.22) * mm, "end": v(20.5, 43.35) * mm});
            skLineSegment(sketch, "E824", {"start": v(20.5, 43.35) * mm, "end": v(20.35, 43.43) * mm});
            skLineSegment(sketch, "E825", {"start": v(20.35, 43.43) * mm, "end": v(20.19, 43.48) * mm});
            skLineSegment(sketch, "E826", {"start": v(20.19, 43.48) * mm, "end": v(20.08, 43.49) * mm});
            skLineSegment(sketch, "E827", {"start": v(20.08, 43.49) * mm, "end": v(19.91, 43.46) * mm});
            skLineSegment(sketch, "E828", {"start": v(19.91, 43.46) * mm, "end": v(19.75, 43.4) * mm});
            skLineSegment(sketch, "E829", {"start": v(19.75, 43.4) * mm, "end": v(19.62, 43.28) * mm});
            skLineSegment(sketch, "E830", {"start": v(19.62, 43.28) * mm, "end": v(19.52, 43.14) * mm});
            skLineSegment(sketch, "E831", {"start": v(19.52, 43.14) * mm, "end": v(19.44, 42.98) * mm});
            skLineSegment(sketch, "E832", {"start": v(19.44, 42.98) * mm, "end": v(19.37, 42.83) * mm});
            skLineSegment(sketch, "E833", {"start": v(19.37, 42.83) * mm, "end": v(19.3, 42.68) * mm});
            skLineSegment(sketch, "E834", {"start": v(19.3, 42.68) * mm, "end": v(19.22, 42.52) * mm});
            skLineSegment(sketch, "E835", {"start": v(19.22, 42.52) * mm, "end": v(19.15, 42.37) * mm});
            skLineSegment(sketch, "E836", {"start": v(19.15, 42.37) * mm, "end": v(19.08, 42.22) * mm});
            skLineSegment(sketch, "E837", {"start": v(19.08, 42.22) * mm, "end": v(19, 42.07) * mm});
            skLineSegment(sketch, "E838", {"start": v(19, 42.07) * mm, "end": v(18.94, 41.92) * mm});
            skLineSegment(sketch, "E839", {"start": v(18.94, 41.92) * mm, "end": v(18.87, 41.77) * mm});
            skLineSegment(sketch, "E840", {"start": v(18.87, 41.77) * mm, "end": v(18.8, 41.61) * mm});
            skLineSegment(sketch, "E841", {"start": v(18.8, 41.61) * mm, "end": v(18.72, 41.46) * mm});
            skLineSegment(sketch, "E842", {"start": v(18.72, 41.46) * mm, "end": v(18.65, 41.31) * mm});
            skLineSegment(sketch, "E843", {"start": v(18.65, 41.31) * mm, "end": v(18.58, 41.16) * mm});
            skLineSegment(sketch, "E844", {"start": v(18.58, 41.16) * mm, "end": v(18.43, 41.22) * mm});
            skLineSegment(sketch, "E845", {"start": v(18.43, 41.22) * mm, "end": v(18.28, 41.3) * mm});
            skLineSegment(sketch, "E846", {"start": v(18.28, 41.3) * mm, "end": v(18.12, 41.36) * mm});
            skLineSegment(sketch, "E847", {"start": v(18.12, 41.36) * mm, "end": v(17.97, 41.43) * mm});
            skLineSegment(sketch, "E848", {"start": v(17.97, 41.43) * mm, "end": v(17.82, 41.5) * mm});
            skLineSegment(sketch, "E849", {"start": v(17.82, 41.5) * mm, "end": v(17.67, 41.56) * mm});
            skLineSegment(sketch, "E850", {"start": v(17.67, 41.56) * mm, "end": v(17.52, 41.63) * mm});
            skLineSegment(sketch, "E851", {"start": v(17.52, 41.63) * mm, "end": v(17.36, 41.7) * mm});
            skLineSegment(sketch, "E852", {"start": v(17.36, 41.7) * mm, "end": v(17.21, 41.77) * mm});
            skLineSegment(sketch, "E853", {"start": v(17.21, 41.77) * mm, "end": v(17.06, 41.83) * mm});
            skLineSegment(sketch, "E854", {"start": v(17.06, 41.83) * mm, "end": v(16.9, 41.9) * mm});
            skLineSegment(sketch, "E855", {"start": v(16.9, 41.9) * mm, "end": v(16.83, 41.93) * mm});
            skLineSegment(sketch, "E856", {"start": v(16.83, 41.93) * mm, "end": v(16.9, 42.09) * mm});
            skLineSegment(sketch, "E857", {"start": v(16.9, 42.09) * mm, "end": v(16.96, 42.24) * mm});
            skLineSegment(sketch, "E858", {"start": v(16.96, 42.24) * mm, "end": v(17.03, 42.4) * mm});
            skLineSegment(sketch, "E859", {"start": v(17.03, 42.4) * mm, "end": v(17.1, 42.55) * mm});
            skLineSegment(sketch, "E860", {"start": v(17.1, 42.55) * mm, "end": v(17.16, 42.7) * mm});
            skLineSegment(sketch, "E861", {"start": v(17.16, 42.7) * mm, "end": v(17.22, 42.86) * mm});
            skLineSegment(sketch, "E862", {"start": v(17.22, 42.86) * mm, "end": v(17.29, 43.02) * mm});
            skLineSegment(sketch, "E863", {"start": v(17.29, 43.02) * mm, "end": v(17.35, 43.17) * mm});
            skLineSegment(sketch, "E864", {"start": v(17.35, 43.17) * mm, "end": v(17.42, 43.33) * mm});
            skLineSegment(sketch, "E865", {"start": v(17.42, 43.33) * mm, "end": v(17.48, 43.48) * mm});
            skLineSegment(sketch, "E866", {"start": v(17.48, 43.48) * mm, "end": v(17.55, 43.63) * mm});
            skLineSegment(sketch, "E867", {"start": v(17.55, 43.63) * mm, "end": v(17.61, 43.8) * mm});
            skLineSegment(sketch, "E868", {"start": v(17.61, 43.8) * mm, "end": v(17.68, 43.96) * mm});
            skLineSegment(sketch, "E869", {"start": v(17.68, 43.96) * mm, "end": v(17.72, 44.13) * mm});
            skLineSegment(sketch, "E870", {"start": v(17.72, 44.13) * mm, "end": v(17.7, 44.3) * mm});
            skLineSegment(sketch, "E871", {"start": v(17.7, 44.3) * mm, "end": v(17.65, 44.47) * mm});
            skLineSegment(sketch, "E872", {"start": v(17.65, 44.47) * mm, "end": v(17.56, 44.61) * mm});
            skLineSegment(sketch, "E873", {"start": v(17.56, 44.61) * mm, "end": v(17.43, 44.73) * mm});
            skLineSegment(sketch, "E874", {"start": v(17.43, 44.73) * mm, "end": v(17.27, 44.8) * mm});
            skLineSegment(sketch, "E875", {"start": v(17.27, 44.8) * mm, "end": v(17.1, 44.84) * mm});
            skLineSegment(sketch, "E876", {"start": v(17.1, 44.84) * mm, "end": v(17.07, 44.84) * mm});
            skLineSegment(sketch, "E877", {"start": v(17.07, 44.84) * mm, "end": v(16.9, 44.82) * mm});
            skLineSegment(sketch, "E878", {"start": v(16.9, 44.82) * mm, "end": v(16.73, 44.76) * mm});
            skLineSegment(sketch, "E879", {"start": v(16.73, 44.76) * mm, "end": v(16.6, 44.65) * mm});
            skLineSegment(sketch, "E880", {"start": v(16.6, 44.65) * mm, "end": v(16.49, 44.52) * mm});
            skLineSegment(sketch, "E881", {"start": v(16.49, 44.52) * mm, "end": v(16.42, 44.35) * mm});
            skLineSegment(sketch, "E882", {"start": v(16.42, 44.35) * mm, "end": v(16.36, 44.2) * mm});
            skLineSegment(sketch, "E883", {"start": v(16.36, 44.2) * mm, "end": v(16.3, 44.04) * mm});
            skLineSegment(sketch, "E884", {"start": v(16.3, 44.04) * mm, "end": v(16.23, 43.88) * mm});
            skLineSegment(sketch, "E885", {"start": v(16.23, 43.88) * mm, "end": v(16.17, 43.73) * mm});
            skLineSegment(sketch, "E886", {"start": v(16.17, 43.73) * mm, "end": v(16.11, 43.57) * mm});
            skLineSegment(sketch, "E887", {"start": v(16.11, 43.57) * mm, "end": v(16.05, 43.41) * mm});
            skLineSegment(sketch, "E888", {"start": v(16.05, 43.41) * mm, "end": v(16, 43.26) * mm});
            skLineSegment(sketch, "E889", {"start": v(16, 43.26) * mm, "end": v(15.93, 43.1) * mm});
            skLineSegment(sketch, "E890", {"start": v(15.93, 43.1) * mm, "end": v(15.87, 42.94) * mm});
            skLineSegment(sketch, "E891", {"start": v(15.87, 42.94) * mm, "end": v(15.8, 42.79) * mm});
            skLineSegment(sketch, "E892", {"start": v(15.8, 42.79) * mm, "end": v(15.75, 42.63) * mm});
            skLineSegment(sketch, "E893", {"start": v(15.75, 42.63) * mm, "end": v(15.69, 42.48) * mm});
            skLineSegment(sketch, "E894", {"start": v(15.69, 42.48) * mm, "end": v(15.66, 42.4) * mm});
            skLineSegment(sketch, "E895", {"start": v(15.66, 42.4) * mm, "end": v(15.5, 42.47) * mm});
            skLineSegment(sketch, "E896", {"start": v(15.5, 42.47) * mm, "end": v(15.35, 42.52) * mm});
            skLineSegment(sketch, "E897", {"start": v(15.35, 42.52) * mm, "end": v(15.2, 42.58) * mm});
            skLineSegment(sketch, "E898", {"start": v(15.2, 42.58) * mm, "end": v(15.04, 42.64) * mm});
            skLineSegment(sketch, "E899", {"start": v(15.04, 42.64) * mm, "end": v(14.88, 42.7) * mm});
            skLineSegment(sketch, "E900", {"start": v(14.88, 42.7) * mm, "end": v(14.72, 42.75) * mm});
            skLineSegment(sketch, "E901", {"start": v(14.72, 42.75) * mm, "end": v(14.57, 42.8) * mm});
            skLineSegment(sketch, "E902", {"start": v(14.57, 42.8) * mm, "end": v(14.41, 42.86) * mm});
            skLineSegment(sketch, "E903", {"start": v(14.41, 42.86) * mm, "end": v(14.25, 42.92) * mm});
            skLineSegment(sketch, "E904", {"start": v(14.25, 42.92) * mm, "end": v(14.1, 42.98) * mm});
            skLineSegment(sketch, "E905", {"start": v(14.1, 42.98) * mm, "end": v(13.94, 43.03) * mm});
            skLineSegment(sketch, "E906", {"start": v(13.94, 43.03) * mm, "end": v(13.87, 43.06) * mm});
            skLineSegment(sketch, "E907", {"start": v(13.87, 43.06) * mm, "end": v(13.92, 43.22) * mm});
            skLineSegment(sketch, "E908", {"start": v(13.92, 43.22) * mm, "end": v(13.97, 43.38) * mm});
            skLineSegment(sketch, "E909", {"start": v(13.97, 43.38) * mm, "end": v(14.03, 43.54) * mm});
            skLineSegment(sketch, "E910", {"start": v(14.03, 43.54) * mm, "end": v(14.08, 43.7) * mm});
            skLineSegment(sketch, "E911", {"start": v(14.08, 43.7) * mm, "end": v(14.13, 43.85) * mm});
            skLineSegment(sketch, "E912", {"start": v(14.13, 43.85) * mm, "end": v(14.2, 44.02) * mm});
            skLineSegment(sketch, "E913", {"start": v(14.2, 44.02) * mm, "end": v(14.24, 44.17) * mm});
            skLineSegment(sketch, "E914", {"start": v(14.24, 44.17) * mm, "end": v(14.3, 44.33) * mm});
            skLineSegment(sketch, "E915", {"start": v(14.3, 44.33) * mm, "end": v(14.35, 44.5) * mm});
            skLineSegment(sketch, "E916", {"start": v(14.35, 44.5) * mm, "end": v(14.4, 44.65) * mm});
            skLineSegment(sketch, "E917", {"start": v(14.4, 44.65) * mm, "end": v(14.46, 44.8) * mm});
            skLineSegment(sketch, "E918", {"start": v(14.46, 44.8) * mm, "end": v(14.51, 44.97) * mm});
            skLineSegment(sketch, "E919", {"start": v(14.51, 44.97) * mm, "end": v(14.57, 45.14) * mm});
            skLineSegment(sketch, "E920", {"start": v(14.57, 45.14) * mm, "end": v(14.6, 45.31) * mm});
            skLineSegment(sketch, "E921", {"start": v(14.6, 45.31) * mm, "end": v(14.57, 45.48) * mm});
            skLineSegment(sketch, "E922", {"start": v(14.57, 45.48) * mm, "end": v(14.5, 45.64) * mm});
            skLineSegment(sketch, "E923", {"start": v(14.5, 45.64) * mm, "end": v(14.4, 45.78) * mm});
            skLineSegment(sketch, "E924", {"start": v(14.4, 45.78) * mm, "end": v(14.26, 45.89) * mm});
            skLineSegment(sketch, "E925", {"start": v(14.26, 45.89) * mm, "end": v(14.1, 45.95) * mm});
            skLineSegment(sketch, "E926", {"start": v(14.1, 45.95) * mm, "end": v(13.93, 45.98) * mm});
            skLineSegment(sketch, "E927", {"start": v(13.93, 45.98) * mm, "end": v(13.76, 45.95) * mm});
            skLineSegment(sketch, "E928", {"start": v(13.76, 45.95) * mm, "end": v(13.6, 45.89) * mm});
            skLineSegment(sketch, "E929", {"start": v(13.6, 45.89) * mm, "end": v(13.46, 45.78) * mm});
            skLineSegment(sketch, "E930", {"start": v(13.46, 45.78) * mm, "end": v(13.36, 45.64) * mm});
            skLineSegment(sketch, "E931", {"start": v(13.36, 45.64) * mm, "end": v(13.3, 45.49) * mm});
            skLineSegment(sketch, "E932", {"start": v(13.3, 45.49) * mm, "end": v(13.24, 45.33) * mm});
            skLineSegment(sketch, "E933", {"start": v(13.24, 45.33) * mm, "end": v(13.2, 45.17) * mm});
            skLineSegment(sketch, "E934", {"start": v(13.2, 45.17) * mm, "end": v(13.15, 45.01) * mm});
            skLineSegment(sketch, "E935", {"start": v(13.15, 45.01) * mm, "end": v(13.1, 44.85) * mm});
            skLineSegment(sketch, "E936", {"start": v(13.1, 44.85) * mm, "end": v(13.05, 44.7) * mm});
            skLineSegment(sketch, "E937", {"start": v(13.05, 44.7) * mm, "end": v(13, 44.53) * mm});
            skLineSegment(sketch, "E938", {"start": v(13, 44.53) * mm, "end": v(12.95, 44.37) * mm});
            skLineSegment(sketch, "E939", {"start": v(12.95, 44.37) * mm, "end": v(12.9, 44.2) * mm});
            skLineSegment(sketch, "E940", {"start": v(12.9, 44.2) * mm, "end": v(12.85, 44.05) * mm});
            skLineSegment(sketch, "E941", {"start": v(12.85, 44.05) * mm, "end": v(12.8, 43.9) * mm});
            skLineSegment(sketch, "E942", {"start": v(12.8, 43.9) * mm, "end": v(12.75, 43.73) * mm});
            skLineSegment(sketch, "E943", {"start": v(12.75, 43.73) * mm, "end": v(12.7, 43.57) * mm});
            skLineSegment(sketch, "E944", {"start": v(12.7, 43.57) * mm, "end": v(12.66, 43.45) * mm});
            skLineSegment(sketch, "E945", {"start": v(12.66, 43.45) * mm, "end": v(12.5, 43.5) * mm});
            skLineSegment(sketch, "E946", {"start": v(12.5, 43.5) * mm, "end": v(12.34, 43.54) * mm});
            skLineSegment(sketch, "E947", {"start": v(12.34, 43.54) * mm, "end": v(12.18, 43.6) * mm});
            skLineSegment(sketch, "E948", {"start": v(12.18, 43.6) * mm, "end": v(12.02, 43.64) * mm});
            skLineSegment(sketch, "E949", {"start": v(12.02, 43.64) * mm, "end": v(11.86, 43.68) * mm});
            skLineSegment(sketch, "E950", {"start": v(11.86, 43.68) * mm, "end": v(11.7, 43.73) * mm});
            skLineSegment(sketch, "E951", {"start": v(11.7, 43.73) * mm, "end": v(11.54, 43.77) * mm});
            skLineSegment(sketch, "E952", {"start": v(11.54, 43.77) * mm, "end": v(11.38, 43.82) * mm});
            skLineSegment(sketch, "E953", {"start": v(11.38, 43.82) * mm, "end": v(11.22, 43.87) * mm});
            skLineSegment(sketch, "E954", {"start": v(11.22, 43.87) * mm, "end": v(11.06, 43.91) * mm});
            skLineSegment(sketch, "E955", {"start": v(11.06, 43.91) * mm, "end": v(10.9, 43.96) * mm});
            skLineSegment(sketch, "E956", {"start": v(10.9, 43.96) * mm, "end": v(10.83, 43.98) * mm});
            skLineSegment(sketch, "E957", {"start": v(10.83, 43.98) * mm, "end": v(10.87, 44.14) * mm});
            skLineSegment(sketch, "E958", {"start": v(10.87, 44.14) * mm, "end": v(10.91, 44.3) * mm});
            skLineSegment(sketch, "E959", {"start": v(10.91, 44.3) * mm, "end": v(10.95, 44.47) * mm});
            skLineSegment(sketch, "E960", {"start": v(10.95, 44.47) * mm, "end": v(11, 44.63) * mm});
            skLineSegment(sketch, "E961", {"start": v(11, 44.63) * mm, "end": v(11.04, 44.79) * mm});
            skLineSegment(sketch, "E962", {"start": v(11.04, 44.79) * mm, "end": v(11.08, 44.95) * mm});
            skLineSegment(sketch, "E963", {"start": v(11.08, 44.95) * mm, "end": v(11.13, 45.11) * mm});
            skLineSegment(sketch, "E964", {"start": v(11.13, 45.11) * mm, "end": v(11.17, 45.28) * mm});
            skLineSegment(sketch, "E965", {"start": v(11.17, 45.28) * mm, "end": v(11.21, 45.44) * mm});
            skLineSegment(sketch, "E966", {"start": v(11.21, 45.44) * mm, "end": v(11.25, 45.6) * mm});
            skLineSegment(sketch, "E967", {"start": v(11.25, 45.6) * mm, "end": v(11.3, 45.76) * mm});
            skLineSegment(sketch, "E968", {"start": v(11.3, 45.76) * mm, "end": v(11.34, 45.93) * mm});
            skLineSegment(sketch, "E969", {"start": v(11.34, 45.93) * mm, "end": v(11.39, 46.1) * mm});
            skLineSegment(sketch, "E970", {"start": v(11.39, 46.1) * mm, "end": v(11.4, 46.27) * mm});
            skLineSegment(sketch, "E971", {"start": v(11.4, 46.27) * mm, "end": v(11.36, 46.44) * mm});
            skLineSegment(sketch, "E972", {"start": v(11.36, 46.44) * mm, "end": v(11.29, 46.6) * mm});
            skLineSegment(sketch, "E973", {"start": v(11.29, 46.6) * mm, "end": v(11.17, 46.73) * mm});
            skLineSegment(sketch, "E974", {"start": v(11.17, 46.73) * mm, "end": v(11.03, 46.83) * mm});
            skLineSegment(sketch, "E975", {"start": v(11.03, 46.83) * mm, "end": v(10.86, 46.88) * mm});
            skLineSegment(sketch, "E976", {"start": v(10.86, 46.88) * mm, "end": v(10.72, 46.9) * mm});
            skLineSegment(sketch, "E977", {"start": v(10.72, 46.9) * mm, "end": v(10.55, 46.87) * mm});
            skLineSegment(sketch, "E978", {"start": v(10.55, 46.87) * mm, "end": v(10.4, 46.8) * mm});
            skLineSegment(sketch, "E979", {"start": v(10.4, 46.8) * mm, "end": v(10.26, 46.69) * mm});
            skLineSegment(sketch, "E980", {"start": v(10.26, 46.69) * mm, "end": v(10.16, 46.55) * mm});
            skLineSegment(sketch, "E981", {"start": v(10.16, 46.55) * mm, "end": v(10.1, 46.39) * mm});
            skLineSegment(sketch, "E982", {"start": v(10.1, 46.39) * mm, "end": v(10.05, 46.23) * mm});
            skLineSegment(sketch, "E983", {"start": v(10.05, 46.23) * mm, "end": v(10.02, 46.06) * mm});
            skLineSegment(sketch, "E984", {"start": v(10.02, 46.06) * mm, "end": v(9.98, 45.9) * mm});
            skLineSegment(sketch, "E985", {"start": v(9.98, 45.9) * mm, "end": v(9.94, 45.73) * mm});
            skLineSegment(sketch, "E986", {"start": v(9.94, 45.73) * mm, "end": v(9.9, 45.57) * mm});
            skLineSegment(sketch, "E987", {"start": v(9.9, 45.57) * mm, "end": v(9.86, 45.4) * mm});
            skLineSegment(sketch, "E988", {"start": v(9.86, 45.4) * mm, "end": v(9.82, 45.24) * mm});
            skLineSegment(sketch, "E989", {"start": v(9.82, 45.24) * mm, "end": v(9.79, 45.08) * mm});
            skLineSegment(sketch, "E990", {"start": v(9.79, 45.08) * mm, "end": v(9.75, 44.92) * mm});
            skLineSegment(sketch, "E991", {"start": v(9.75, 44.92) * mm, "end": v(9.7, 44.75) * mm});
            skLineSegment(sketch, "E992", {"start": v(9.7, 44.75) * mm, "end": v(9.67, 44.6) * mm});
            skLineSegment(sketch, "E993", {"start": v(9.67, 44.6) * mm, "end": v(9.63, 44.43) * mm});
            skLineSegment(sketch, "E994", {"start": v(9.63, 44.43) * mm, "end": v(9.6, 44.29) * mm});
            skLineSegment(sketch, "E995", {"start": v(9.6, 44.29) * mm, "end": v(9.44, 44.32) * mm});
            skLineSegment(sketch, "E996", {"start": v(9.44, 44.32) * mm, "end": v(9.27, 44.35) * mm});
            skLineSegment(sketch, "E997", {"start": v(9.27, 44.35) * mm, "end": v(9.11, 44.39) * mm});
            skLineSegment(sketch, "E998", {"start": v(9.11, 44.39) * mm, "end": v(8.95, 44.42) * mm});
            skLineSegment(sketch, "E999", {"start": v(8.95, 44.42) * mm, "end": v(8.79, 44.46) * mm});
            skLineSegment(sketch, "E1000", {"start": v(8.79, 44.46) * mm, "end": v(8.62, 44.5) * mm});
            skLineSegment(sketch, "E1001", {"start": v(8.62, 44.5) * mm, "end": v(8.46, 44.53) * mm});
            skLineSegment(sketch, "E1002", {"start": v(8.46, 44.53) * mm, "end": v(8.3, 44.56) * mm});
            skLineSegment(sketch, "E1003", {"start": v(8.3, 44.56) * mm, "end": v(8.13, 44.6) * mm});
            skLineSegment(sketch, "E1004", {"start": v(8.13, 44.6) * mm, "end": v(7.97, 44.63) * mm});
            skLineSegment(sketch, "E1005", {"start": v(7.97, 44.63) * mm, "end": v(7.8, 44.67) * mm});
            skLineSegment(sketch, "E1006", {"start": v(7.8, 44.67) * mm, "end": v(7.73, 44.68) * mm});
            skLineSegment(sketch, "E1007", {"start": v(7.73, 44.68) * mm, "end": v(7.76, 44.85) * mm});
            skLineSegment(sketch, "E1008", {"start": v(7.76, 44.85) * mm, "end": v(7.8, 45) * mm});
            skLineSegment(sketch, "E1009", {"start": v(7.8, 45) * mm, "end": v(7.82, 45.18) * mm});
            skLineSegment(sketch, "E1010", {"start": v(7.82, 45.18) * mm, "end": v(7.86, 45.34) * mm});
            skLineSegment(sketch, "E1011", {"start": v(7.86, 45.34) * mm, "end": v(7.89, 45.5) * mm});
            skLineSegment(sketch, "E1012", {"start": v(7.89, 45.5) * mm, "end": v(7.92, 45.67) * mm});
            skLineSegment(sketch, "E1013", {"start": v(7.92, 45.67) * mm, "end": v(7.95, 45.84) * mm});
            skLineSegment(sketch, "E1014", {"start": v(7.95, 45.84) * mm, "end": v(7.98, 46) * mm});
            skLineSegment(sketch, "E1015", {"start": v(7.98, 46) * mm, "end": v(8.01, 46.17) * mm});
            skLineSegment(sketch, "E1016", {"start": v(8.01, 46.17) * mm, "end": v(8.04, 46.33) * mm});
            skLineSegment(sketch, "E1017", {"start": v(8.04, 46.33) * mm, "end": v(8.08, 46.5) * mm});
            skLineSegment(sketch, "E1018", {"start": v(8.08, 46.5) * mm, "end": v(8.1, 46.66) * mm});
            skLineSegment(sketch, "E1019", {"start": v(8.1, 46.66) * mm, "end": v(8.14, 46.84) * mm});
            skLineSegment(sketch, "E1020", {"start": v(8.14, 46.84) * mm, "end": v(8.14, 47.01) * mm});
            skLineSegment(sketch, "E1021", {"start": v(8.14, 47.01) * mm, "end": v(8.1, 47.18) * mm});
            skLineSegment(sketch, "E1022", {"start": v(8.1, 47.18) * mm, "end": v(8, 47.33) * mm});
            skLineSegment(sketch, "E1023", {"start": v(8, 47.33) * mm, "end": v(7.88, 47.45) * mm});
            skLineSegment(sketch, "E1024", {"start": v(7.88, 47.45) * mm, "end": v(7.73, 47.54) * mm});
            skLineSegment(sketch, "E1025", {"start": v(7.73, 47.54) * mm, "end": v(7.56, 47.58) * mm});
            skLineSegment(sketch, "E1026", {"start": v(7.56, 47.58) * mm, "end": v(7.5, 47.58) * mm});
            skLineSegment(sketch, "E1027", {"start": v(7.5, 47.58) * mm, "end": v(7.32, 47.57) * mm});
            skLineSegment(sketch, "E1028", {"start": v(7.32, 47.57) * mm, "end": v(7.16, 47.5) * mm});
            skLineSegment(sketch, "E1029", {"start": v(7.16, 47.5) * mm, "end": v(7.02, 47.4) * mm});
            skLineSegment(sketch, "E1030", {"start": v(7.02, 47.4) * mm, "end": v(6.91, 47.26) * mm});
            skLineSegment(sketch, "E1031", {"start": v(6.91, 47.26) * mm, "end": v(6.85, 47.1) * mm});
            skLineSegment(sketch, "E1032", {"start": v(6.85, 47.1) * mm, "end": v(6.82, 46.94) * mm});
            skLineSegment(sketch, "E1033", {"start": v(6.82, 46.94) * mm, "end": v(6.79, 46.77) * mm});
            skLineSegment(sketch, "E1034", {"start": v(6.79, 46.77) * mm, "end": v(6.76, 46.6) * mm});
            skLineSegment(sketch, "E1035", {"start": v(6.76, 46.6) * mm, "end": v(6.73, 46.44) * mm});
            skLineSegment(sketch, "E1036", {"start": v(6.73, 46.44) * mm, "end": v(6.7, 46.28) * mm});
            skLineSegment(sketch, "E1037", {"start": v(6.7, 46.28) * mm, "end": v(6.68, 46.1) * mm});
            skLineSegment(sketch, "E1038", {"start": v(6.68, 46.1) * mm, "end": v(6.65, 45.95) * mm});
            skLineSegment(sketch, "E1039", {"start": v(6.65, 45.95) * mm, "end": v(6.63, 45.78) * mm});
            skLineSegment(sketch, "E1040", {"start": v(6.63, 45.78) * mm, "end": v(6.6, 45.61) * mm});
            skLineSegment(sketch, "E1041", {"start": v(6.6, 45.61) * mm, "end": v(6.57, 45.45) * mm});
            skLineSegment(sketch, "E1042", {"start": v(6.57, 45.45) * mm, "end": v(6.55, 45.28) * mm});
            skLineSegment(sketch, "E1043", {"start": v(6.55, 45.28) * mm, "end": v(6.52, 45.12) * mm});
            skLineSegment(sketch, "E1044", {"start": v(6.52, 45.12) * mm, "end": v(6.5, 44.95) * mm});
            skLineSegment(sketch, "E1045", {"start": v(6.5, 44.95) * mm, "end": v(6.48, 44.9) * mm});
            skLineSegment(sketch, "E1046", {"start": v(6.48, 44.9) * mm, "end": v(6.32, 44.93) * mm});
            skLineSegment(sketch, "E1047", {"start": v(6.32, 44.93) * mm, "end": v(6.16, 44.95) * mm});
            skLineSegment(sketch, "E1048", {"start": v(6.16, 44.95) * mm, "end": v(6, 44.97) * mm});
            skLineSegment(sketch, "E1049", {"start": v(6, 44.97) * mm, "end": v(5.83, 45) * mm});
            skLineSegment(sketch, "E1050", {"start": v(5.83, 45) * mm, "end": v(5.66, 45.02) * mm});
            skLineSegment(sketch, "E1051", {"start": v(5.66, 45.02) * mm, "end": v(5.5, 45.04) * mm});
            skLineSegment(sketch, "E1052", {"start": v(5.5, 45.04) * mm, "end": v(5.33, 45.06) * mm});
            skLineSegment(sketch, "E1053", {"start": v(5.33, 45.06) * mm, "end": v(5.17, 45.09) * mm});
            skLineSegment(sketch, "E1054", {"start": v(5.17, 45.09) * mm, "end": v(5, 45.11) * mm});
            skLineSegment(sketch, "E1055", {"start": v(5, 45.11) * mm, "end": v(4.84, 45.13) * mm});
            skLineSegment(sketch, "E1056", {"start": v(4.84, 45.13) * mm, "end": v(4.67, 45.16) * mm});
            skLineSegment(sketch, "E1057", {"start": v(4.67, 45.16) * mm, "end": v(4.6, 45.17) * mm});
            skLineSegment(sketch, "E1058", {"start": v(4.6, 45.17) * mm, "end": v(4.61, 45.33) * mm});
            skLineSegment(sketch, "E1059", {"start": v(4.61, 45.33) * mm, "end": v(4.63, 45.5) * mm});
            skLineSegment(sketch, "E1060", {"start": v(4.63, 45.5) * mm, "end": v(4.65, 45.67) * mm});
            skLineSegment(sketch, "E1061", {"start": v(4.65, 45.67) * mm, "end": v(4.67, 45.83) * mm});
            skLineSegment(sketch, "E1062", {"start": v(4.67, 45.83) * mm, "end": v(4.7, 46) * mm});
            skLineSegment(sketch, "E1063", {"start": v(4.7, 46) * mm, "end": v(4.71, 46.17) * mm});
            skLineSegment(sketch, "E1064", {"start": v(4.71, 46.17) * mm, "end": v(4.73, 46.33) * mm});
            skLineSegment(sketch, "E1065", {"start": v(4.73, 46.33) * mm, "end": v(4.75, 46.5) * mm});
            skLineSegment(sketch, "E1066", {"start": v(4.75, 46.5) * mm, "end": v(4.77, 46.67) * mm});
            skLineSegment(sketch, "E1067", {"start": v(4.77, 46.67) * mm, "end": v(4.8, 46.83) * mm});
            skLineSegment(sketch, "E1068", {"start": v(4.8, 46.83) * mm, "end": v(4.81, 47) * mm});
            skLineSegment(sketch, "E1069", {"start": v(4.81, 47) * mm, "end": v(4.83, 47.17) * mm});
            skLineSegment(sketch, "E1070", {"start": v(4.83, 47.17) * mm, "end": v(4.85, 47.35) * mm});
            skLineSegment(sketch, "E1071", {"start": v(4.85, 47.35) * mm, "end": v(4.84, 47.52) * mm});
            skLineSegment(sketch, "E1072", {"start": v(4.84, 47.52) * mm, "end": v(4.78, 47.68) * mm});
            skLineSegment(sketch, "E1073", {"start": v(4.78, 47.68) * mm, "end": v(4.68, 47.83) * mm});
            skLineSegment(sketch, "E1074", {"start": v(4.68, 47.83) * mm, "end": v(4.55, 47.94) * mm});
            skLineSegment(sketch, "E1075", {"start": v(4.55, 47.94) * mm, "end": v(4.4, 48.02) * mm});
            skLineSegment(sketch, "E1076", {"start": v(4.4, 48.02) * mm, "end": v(4.22, 48.05) * mm});
            skLineSegment(sketch, "E1077", {"start": v(4.22, 48.05) * mm, "end": v(4.19, 48.05) * mm});
            skLineSegment(sketch, "E1078", {"start": v(4.19, 48.05) * mm, "end": v(4.02, 48.03) * mm});
            skLineSegment(sketch, "E1079", {"start": v(4.02, 48.03) * mm, "end": v(3.86, 47.96) * mm});
            skLineSegment(sketch, "E1080", {"start": v(3.86, 47.96) * mm, "end": v(3.72, 47.85) * mm});
            skLineSegment(sketch, "E1081", {"start": v(3.72, 47.85) * mm, "end": v(3.61, 47.71) * mm});
            skLineSegment(sketch, "E1082", {"start": v(3.61, 47.71) * mm, "end": v(3.55, 47.55) * mm});
            skLineSegment(sketch, "E1083", {"start": v(3.55, 47.55) * mm, "end": v(3.52, 47.38) * mm});
            skLineSegment(sketch, "E1084", {"start": v(3.52, 47.38) * mm, "end": v(3.5, 47.21) * mm});
            skLineSegment(sketch, "E1085", {"start": v(3.5, 47.21) * mm, "end": v(3.5, 47.05) * mm});
            skLineSegment(sketch, "E1086", {"start": v(3.5, 47.05) * mm, "end": v(3.48, 46.88) * mm});
            skLineSegment(sketch, "E1087", {"start": v(3.48, 46.88) * mm, "end": v(3.46, 46.71) * mm});
            skLineSegment(sketch, "E1088", {"start": v(3.46, 46.71) * mm, "end": v(3.45, 46.55) * mm});
            skLineSegment(sketch, "E1089", {"start": v(3.45, 46.55) * mm, "end": v(3.43, 46.38) * mm});
            skLineSegment(sketch, "E1090", {"start": v(3.43, 46.38) * mm, "end": v(3.42, 46.2) * mm});
            skLineSegment(sketch, "E1091", {"start": v(3.42, 46.2) * mm, "end": v(3.4, 46.04) * mm});
            skLineSegment(sketch, "E1092", {"start": v(3.4, 46.04) * mm, "end": v(3.39, 45.87) * mm});
            skLineSegment(sketch, "E1093", {"start": v(3.39, 45.87) * mm, "end": v(3.37, 45.7) * mm});
            skLineSegment(sketch, "E1094", {"start": v(3.37, 45.7) * mm, "end": v(3.36, 45.54) * mm});
            skLineSegment(sketch, "E1095", {"start": v(3.36, 45.54) * mm, "end": v(3.34, 45.37) * mm});
            skLineSegment(sketch, "E1096", {"start": v(3.34, 45.37) * mm, "end": v(3.33, 45.3) * mm});
            skLineSegment(sketch, "E1097", {"start": v(3.33, 45.3) * mm, "end": v(3.17, 45.31) * mm});
            skLineSegment(sketch, "E1098", {"start": v(3.17, 45.31) * mm, "end": v(3, 45.32) * mm});
            skLineSegment(sketch, "E1099", {"start": v(3, 45.32) * mm, "end": v(2.84, 45.33) * mm});
            skLineSegment(sketch, "E1100", {"start": v(2.84, 45.33) * mm, "end": v(2.67, 45.35) * mm});
            skLineSegment(sketch, "E1101", {"start": v(2.67, 45.35) * mm, "end": v(2.5, 45.36) * mm});
            skLineSegment(sketch, "E1102", {"start": v(2.5, 45.36) * mm, "end": v(2.34, 45.37) * mm});
            skLineSegment(sketch, "E1103", {"start": v(2.34, 45.37) * mm, "end": v(2.17, 45.38) * mm});
            skLineSegment(sketch, "E1104", {"start": v(2.17, 45.38) * mm, "end": v(2, 45.4) * mm});
            skLineSegment(sketch, "E1105", {"start": v(2, 45.4) * mm, "end": v(1.84, 45.4) * mm});
            skLineSegment(sketch, "E1106", {"start": v(1.84, 45.4) * mm, "end": v(1.68, 45.42) * mm});
            skLineSegment(sketch, "E1107", {"start": v(1.68, 45.42) * mm, "end": v(1.5, 45.43) * mm});
            skLineSegment(sketch, "E1108", {"start": v(1.5, 45.43) * mm, "end": v(1.43, 45.43) * mm});
            skLineSegment(sketch, "E1109", {"start": v(1.43, 45.43) * mm, "end": v(1.44, 45.6) * mm});
            skLineSegment(sketch, "E1110", {"start": v(1.44, 45.6) * mm, "end": v(1.44, 45.77) * mm});
            skLineSegment(sketch, "E1111", {"start": v(1.44, 45.77) * mm, "end": v(1.45, 45.94) * mm});
            skLineSegment(sketch, "E1112", {"start": v(1.45, 45.94) * mm, "end": v(1.46, 46.1) * mm});
            skLineSegment(sketch, "E1113", {"start": v(1.46, 46.1) * mm, "end": v(1.47, 46.27) * mm});
            skLineSegment(sketch, "E1114", {"start": v(1.47, 46.27) * mm, "end": v(1.48, 46.44) * mm});
            skLineSegment(sketch, "E1115", {"start": v(1.48, 46.44) * mm, "end": v(1.49, 46.6) * mm});
            skLineSegment(sketch, "E1116", {"start": v(1.49, 46.6) * mm, "end": v(1.5, 46.77) * mm});
            skLineSegment(sketch, "E1117", {"start": v(1.5, 46.77) * mm, "end": v(1.5, 46.94) * mm});
            skLineSegment(sketch, "E1118", {"start": v(1.5, 46.94) * mm, "end": v(1.51, 47.1) * mm});
            skLineSegment(sketch, "E1119", {"start": v(1.51, 47.1) * mm, "end": v(1.52, 47.28) * mm});
            skLineSegment(sketch, "E1120", {"start": v(1.52, 47.28) * mm, "end": v(1.53, 47.45) * mm});
            skLineSegment(sketch, "E1121", {"start": v(1.53, 47.45) * mm, "end": v(1.53, 47.63) * mm});
            skLineSegment(sketch, "E1122", {"start": v(1.53, 47.63) * mm, "end": v(1.5, 47.8) * mm});
            skLineSegment(sketch, "E1123", {"start": v(1.5, 47.8) * mm, "end": v(1.44, 47.96) * mm});
            skLineSegment(sketch, "E1124", {"start": v(1.44, 47.96) * mm, "end": v(1.33, 48.1) * mm});
            skLineSegment(sketch, "E1125", {"start": v(1.33, 48.1) * mm, "end": v(1.2, 48.2) * mm});
            skLineSegment(sketch, "E1126", {"start": v(1.2, 48.2) * mm, "end": v(1.03, 48.26) * mm});
            skLineSegment(sketch, "E1127", {"start": v(1.03, 48.26) * mm, "end": v(0.86, 48.28) * mm});
            skLineSegment(sketch, "E1128", {"start": v(0.86, 48.28) * mm, "end": v(0.69, 48.25) * mm});
            skLineSegment(sketch, "E1129", {"start": v(0.69, 48.25) * mm, "end": v(0.53, 48.18) * mm});
            skLineSegment(sketch, "E1130", {"start": v(0.53, 48.18) * mm, "end": v(0.4, 48.08) * mm});
            skLineSegment(sketch, "E1131", {"start": v(0.4, 48.08) * mm, "end": v(0.3, 47.94) * mm});
            skLineSegment(sketch, "E1132", {"start": v(0.3, 47.94) * mm, "end": v(0.23, 47.77) * mm});
            skLineSegment(sketch, "E1133", {"start": v(0.23, 47.77) * mm, "end": v(0.21, 47.6) * mm});
            skLineSegment(sketch, "E1134", {"start": v(0.21, 47.6) * mm, "end": v(0.2, 47.44) * mm});
            skLineSegment(sketch, "E1135", {"start": v(0.2, 47.44) * mm, "end": v(0.2, 47.28) * mm});
            skLineSegment(sketch, "E1136", {"start": v(0.2, 47.28) * mm, "end": v(0.2, 47.11) * mm});
            skLineSegment(sketch, "E1137", {"start": v(0.2, 47.11) * mm, "end": v(0.2, 46.94) * mm});
            skLineSegment(sketch, "E1138", {"start": v(0.2, 46.94) * mm, "end": v(0.2, 46.77) * mm});
            skLineSegment(sketch, "E1139", {"start": v(0.2, 46.77) * mm, "end": v(0.19, 46.6) * mm});
            skLineSegment(sketch, "E1140", {"start": v(0.19, 46.6) * mm, "end": v(0.19, 46.44) * mm});
            skLineSegment(sketch, "E1141", {"start": v(0.19, 46.44) * mm, "end": v(0.18, 46.27) * mm});
            skLineSegment(sketch, "E1142", {"start": v(0.18, 46.27) * mm, "end": v(0.18, 46.1) * mm});
            skLineSegment(sketch, "E1143", {"start": v(0.18, 46.1) * mm, "end": v(0.17, 45.94) * mm});
            skLineSegment(sketch, "E1144", {"start": v(0.17, 45.94) * mm, "end": v(0.17, 45.77) * mm});
            skLineSegment(sketch, "E1145", {"start": v(0.17, 45.77) * mm, "end": v(0.17, 45.6) * mm});
            skLineSegment(sketch, "E1146", {"start": v(0.17, 45.6) * mm, "end": v(0.16, 45.48) * mm});
            skLineSegment(sketch, "E1147", {"start": v(0.16, 45.48) * mm, "end": v(0, 45.48) * mm});
            skLineSegment(sketch, "E1148", {"start": v(0, 45.48) * mm, "end": v(-0.17, 45.48) * mm});
            skLineSegment(sketch, "E1149", {"start": v(-0.17, 45.48) * mm, "end": v(-0.33, 45.48) * mm});
            skLineSegment(sketch, "E1150", {"start": v(-0.33, 45.48) * mm, "end": v(-0.5, 45.48) * mm});
            skLineSegment(sketch, "E1151", {"start": v(-0.5, 45.48) * mm, "end": v(-0.67, 45.48) * mm});
            skLineSegment(sketch, "E1152", {"start": v(-0.67, 45.48) * mm, "end": v(-0.83, 45.48) * mm});
            skLineSegment(sketch, "E1153", {"start": v(-0.83, 45.48) * mm, "end": v(-1, 45.48) * mm});
            skLineSegment(sketch, "E1154", {"start": v(-1, 45.48) * mm, "end": v(-1.17, 45.48) * mm});
            skLineSegment(sketch, "E1155", {"start": v(-1.17, 45.48) * mm, "end": v(-1.33, 45.48) * mm});
            skLineSegment(sketch, "E1156", {"start": v(-1.33, 45.48) * mm, "end": v(-1.5, 45.48) * mm});
            skLineSegment(sketch, "E1157", {"start": v(-1.5, 45.48) * mm, "end": v(-1.67, 45.48) * mm});
            skLineSegment(sketch, "E1158", {"start": v(-1.67, 45.48) * mm, "end": v(-1.75, 45.48) * mm});
            skLineSegment(sketch, "E1159", {"start": v(-1.75, 45.48) * mm, "end": v(-1.75, 45.64) * mm});
            skLineSegment(sketch, "E1160", {"start": v(-1.75, 45.64) * mm, "end": v(-1.75, 45.81) * mm});
            skLineSegment(sketch, "E1161", {"start": v(-1.75, 45.81) * mm, "end": v(-1.76, 45.98) * mm});
            skLineSegment(sketch, "E1162", {"start": v(-1.76, 45.98) * mm, "end": v(-1.76, 46.15) * mm});
            skLineSegment(sketch, "E1163", {"start": v(-1.76, 46.15) * mm, "end": v(-1.76, 46.31) * mm});
            skLineSegment(sketch, "E1164", {"start": v(-1.76, 46.31) * mm, "end": v(-1.77, 46.49) * mm});
            skLineSegment(sketch, "E1165", {"start": v(-1.77, 46.49) * mm, "end": v(-1.77, 46.65) * mm});
            skLineSegment(sketch, "E1166", {"start": v(-1.77, 46.65) * mm, "end": v(-1.77, 46.82) * mm});
            skLineSegment(sketch, "E1167", {"start": v(-1.77, 46.82) * mm, "end": v(-1.78, 46.99) * mm});
            skLineSegment(sketch, "E1168", {"start": v(-1.78, 46.99) * mm, "end": v(-1.78, 47.16) * mm});
            skLineSegment(sketch, "E1169", {"start": v(-1.78, 47.16) * mm, "end": v(-1.79, 47.32) * mm});
            skLineSegment(sketch, "E1170", {"start": v(-1.79, 47.32) * mm, "end": v(-1.79, 47.5) * mm});
            skLineSegment(sketch, "E1171", {"start": v(-1.79, 47.5) * mm, "end": v(-1.8, 47.67) * mm});
            skLineSegment(sketch, "E1172", {"start": v(-1.8, 47.67) * mm, "end": v(-1.83, 47.84) * mm});
            skLineSegment(sketch, "E1173", {"start": v(-1.83, 47.84) * mm, "end": v(-1.9, 48) * mm});
            skLineSegment(sketch, "E1174", {"start": v(-1.9, 48) * mm, "end": v(-2.03, 48.12) * mm});
            skLineSegment(sketch, "E1175", {"start": v(-2.03, 48.12) * mm, "end": v(-2.17, 48.22) * mm});
            skLineSegment(sketch, "E1176", {"start": v(-2.17, 48.22) * mm, "end": v(-2.34, 48.27) * mm});
            skLineSegment(sketch, "E1177", {"start": v(-2.34, 48.27) * mm, "end": v(-2.44, 48.28) * mm});
            skLineSegment(sketch, "E1178", {"start": v(-2.44, 48.28) * mm, "end": v(-2.61, 48.26) * mm});
            skLineSegment(sketch, "E1179", {"start": v(-2.61, 48.26) * mm, "end": v(-2.78, 48.2) * mm});
            skLineSegment(sketch, "E1180", {"start": v(-2.78, 48.2) * mm, "end": v(-2.92, 48.1) * mm});
            skLineSegment(sketch, "E1181", {"start": v(-2.92, 48.1) * mm, "end": v(-3.02, 47.96) * mm});
            skLineSegment(sketch, "E1182", {"start": v(-3.02, 47.96) * mm, "end": v(-3.1, 47.8) * mm});
            skLineSegment(sketch, "E1183", {"start": v(-3.1, 47.8) * mm, "end": v(-3.12, 47.63) * mm});
            skLineSegment(sketch, "E1184", {"start": v(-3.12, 47.63) * mm, "end": v(-3.1, 47.45) * mm});
            skLineSegment(sketch, "E1185", {"start": v(-3.1, 47.45) * mm, "end": v(-3.1, 47.28) * mm});
            skLineSegment(sketch, "E1186", {"start": v(-3.1, 47.28) * mm, "end": v(-3.1, 47.11) * mm});
            skLineSegment(sketch, "E1187", {"start": v(-3.1, 47.11) * mm, "end": v(-3.08, 46.94) * mm});
            skLineSegment(sketch, "E1188", {"start": v(-3.08, 46.94) * mm, "end": v(-3.08, 46.78) * mm});
            skLineSegment(sketch, "E1189", {"start": v(-3.08, 46.78) * mm, "end": v(-3.07, 46.61) * mm});
            skLineSegment(sketch, "E1190", {"start": v(-3.07, 46.61) * mm, "end": v(-3.06, 46.44) * mm});
            skLineSegment(sketch, "E1191", {"start": v(-3.06, 46.44) * mm, "end": v(-3.05, 46.27) * mm});
            skLineSegment(sketch, "E1192", {"start": v(-3.05, 46.27) * mm, "end": v(-3.04, 46.1) * mm});
            skLineSegment(sketch, "E1193", {"start": v(-3.04, 46.1) * mm, "end": v(-3.03, 45.94) * mm});
            skLineSegment(sketch, "E1194", {"start": v(-3.03, 45.94) * mm, "end": v(-3.03, 45.77) * mm});
            skLineSegment(sketch, "E1195", {"start": v(-3.03, 45.77) * mm, "end": v(-3.02, 45.6) * mm});
            skLineSegment(sketch, "E1196", {"start": v(-3.02, 45.6) * mm, "end": v(-3, 45.43) * mm});
            skLineSegment(sketch, "E1197", {"start": v(-3, 45.43) * mm, "end": v(-3.18, 45.42) * mm});
            skLineSegment(sketch, "E1198", {"start": v(-3.18, 45.42) * mm, "end": v(-3.34, 45.41) * mm});
            skLineSegment(sketch, "E1199", {"start": v(-3.34, 45.41) * mm, "end": v(-3.5, 45.4) * mm});
            skLineSegment(sketch, "E1200", {"start": v(-3.5, 45.4) * mm, "end": v(-3.67, 45.39) * mm});
            skLineSegment(sketch, "E1201", {"start": v(-3.67, 45.39) * mm, "end": v(-3.84, 45.38) * mm});
            skLineSegment(sketch, "E1202", {"start": v(-3.84, 45.38) * mm, "end": v(-4, 45.36) * mm});
            skLineSegment(sketch, "E1203", {"start": v(-4, 45.36) * mm, "end": v(-4.17, 45.35) * mm});
            skLineSegment(sketch, "E1204", {"start": v(-4.17, 45.35) * mm, "end": v(-4.34, 45.34) * mm});
            skLineSegment(sketch, "E1205", {"start": v(-4.34, 45.34) * mm, "end": v(-4.5, 45.33) * mm});
            skLineSegment(sketch, "E1206", {"start": v(-4.5, 45.33) * mm, "end": v(-4.67, 45.32) * mm});
            skLineSegment(sketch, "E1207", {"start": v(-4.67, 45.32) * mm, "end": v(-4.84, 45.3) * mm});
            skLineSegment(sketch, "E1208", {"start": v(-4.84, 45.3) * mm, "end": v(-4.92, 45.3) * mm});
            skLineSegment(sketch, "E1209", {"start": v(-4.92, 45.3) * mm, "end": v(-4.93, 45.47) * mm});
            skLineSegment(sketch, "E1210", {"start": v(-4.93, 45.47) * mm, "end": v(-4.95, 45.63) * mm});
            skLineSegment(sketch, "E1211", {"start": v(-4.95, 45.63) * mm, "end": v(-4.96, 45.8) * mm});
            skLineSegment(sketch, "E1212", {"start": v(-4.96, 45.8) * mm, "end": v(-4.98, 45.97) * mm});
            skLineSegment(sketch, "E1213", {"start": v(-4.98, 45.97) * mm, "end": v(-5, 46.13) * mm});
            skLineSegment(sketch, "E1214", {"start": v(-5, 46.13) * mm, "end": v(-5, 46.3) * mm});
            skLineSegment(sketch, "E1215", {"start": v(-5, 46.3) * mm, "end": v(-5.02, 46.47) * mm});
            skLineSegment(sketch, "E1216", {"start": v(-5.02, 46.47) * mm, "end": v(-5.04, 46.64) * mm});
            skLineSegment(sketch, "E1217", {"start": v(-5.04, 46.64) * mm, "end": v(-5.05, 46.8) * mm});
            skLineSegment(sketch, "E1218", {"start": v(-5.05, 46.8) * mm, "end": v(-5.07, 46.97) * mm});
            skLineSegment(sketch, "E1219", {"start": v(-5.07, 46.97) * mm, "end": v(-5.08, 47.14) * mm});
            skLineSegment(sketch, "E1220", {"start": v(-5.08, 47.14) * mm, "end": v(-5.1, 47.3) * mm});
            skLineSegment(sketch, "E1221", {"start": v(-5.1, 47.3) * mm, "end": v(-5.12, 47.49) * mm});
            skLineSegment(sketch, "E1222", {"start": v(-5.12, 47.49) * mm, "end": v(-5.16, 47.65) * mm});
            skLineSegment(sketch, "E1223", {"start": v(-5.16, 47.65) * mm, "end": v(-5.25, 47.8) * mm});
            skLineSegment(sketch, "E1224", {"start": v(-5.25, 47.8) * mm, "end": v(-5.38, 47.92) * mm});
            skLineSegment(sketch, "E1225", {"start": v(-5.38, 47.92) * mm, "end": v(-5.53, 48) * mm});
            skLineSegment(sketch, "E1226", {"start": v(-5.53, 48) * mm, "end": v(-5.7, 48.04) * mm});
            skLineSegment(sketch, "E1227", {"start": v(-5.7, 48.04) * mm, "end": v(-5.77, 48.05) * mm});
            skLineSegment(sketch, "E1228", {"start": v(-5.77, 48.05) * mm, "end": v(-5.94, 48.03) * mm});
            skLineSegment(sketch, "E1229", {"start": v(-5.94, 48.03) * mm, "end": v(-6.1, 47.96) * mm});
            skLineSegment(sketch, "E1230", {"start": v(-6.1, 47.96) * mm, "end": v(-6.24, 47.85) * mm});
            skLineSegment(sketch, "E1231", {"start": v(-6.24, 47.85) * mm, "end": v(-6.35, 47.71) * mm});
            skLineSegment(sketch, "E1232", {"start": v(-6.35, 47.71) * mm, "end": v(-6.41, 47.55) * mm});
            skLineSegment(sketch, "E1233", {"start": v(-6.41, 47.55) * mm, "end": v(-6.43, 47.38) * mm});
            skLineSegment(sketch, "E1234", {"start": v(-6.43, 47.38) * mm, "end": v(-6.42, 47.22) * mm});
            skLineSegment(sketch, "E1235", {"start": v(-6.42, 47.22) * mm, "end": v(-6.4, 47.05) * mm});
            skLineSegment(sketch, "E1236", {"start": v(-6.4, 47.05) * mm, "end": v(-6.38, 46.88) * mm});
            skLineSegment(sketch, "E1237", {"start": v(-6.38, 46.88) * mm, "end": v(-6.36, 46.72) * mm});
            skLineSegment(sketch, "E1238", {"start": v(-6.36, 46.72) * mm, "end": v(-6.34, 46.55) * mm});
            skLineSegment(sketch, "E1239", {"start": v(-6.34, 46.55) * mm, "end": v(-6.32, 46.38) * mm});
            skLineSegment(sketch, "E1240", {"start": v(-6.32, 46.38) * mm, "end": v(-6.3, 46.22) * mm});
            skLineSegment(sketch, "E1241", {"start": v(-6.3, 46.22) * mm, "end": v(-6.28, 46.05) * mm});
            skLineSegment(sketch, "E1242", {"start": v(-6.28, 46.05) * mm, "end": v(-6.26, 45.88) * mm});
            skLineSegment(sketch, "E1243", {"start": v(-6.26, 45.88) * mm, "end": v(-6.24, 45.72) * mm});
            skLineSegment(sketch, "E1244", {"start": v(-6.24, 45.72) * mm, "end": v(-6.22, 45.55) * mm});
            skLineSegment(sketch, "E1245", {"start": v(-6.22, 45.55) * mm, "end": v(-6.2, 45.38) * mm});
            skLineSegment(sketch, "E1246", {"start": v(-6.2, 45.38) * mm, "end": v(-6.18, 45.22) * mm});
            skLineSegment(sketch, "E1247", {"start": v(-6.18, 45.22) * mm, "end": v(-6.17, 45.17) * mm});
            skLineSegment(sketch, "E1248", {"start": v(-6.17, 45.17) * mm, "end": v(-6.34, 45.14) * mm});
            skLineSegment(sketch, "E1249", {"start": v(-6.34, 45.14) * mm, "end": v(-6.5, 45.12) * mm});
            skLineSegment(sketch, "E1250", {"start": v(-6.5, 45.12) * mm, "end": v(-6.67, 45.1) * mm});
            skLineSegment(sketch, "E1251", {"start": v(-6.67, 45.1) * mm, "end": v(-6.83, 45.08) * mm});
            skLineSegment(sketch, "E1252", {"start": v(-6.83, 45.08) * mm, "end": v(-7, 45.05) * mm});
            skLineSegment(sketch, "E1253", {"start": v(-7, 45.05) * mm, "end": v(-7.16, 45.03) * mm});
            skLineSegment(sketch, "E1254", {"start": v(-7.16, 45.03) * mm, "end": v(-7.33, 45) * mm});
            skLineSegment(sketch, "E1255", {"start": v(-7.33, 45) * mm, "end": v(-7.5, 44.98) * mm});
            skLineSegment(sketch, "E1256", {"start": v(-7.5, 44.98) * mm, "end": v(-7.66, 44.96) * mm});
            skLineSegment(sketch, "E1257", {"start": v(-7.66, 44.96) * mm, "end": v(-7.82, 44.94) * mm});
            skLineSegment(sketch, "E1258", {"start": v(-7.82, 44.94) * mm, "end": v(-7.99, 44.91) * mm});
            skLineSegment(sketch, "E1259", {"start": v(-7.99, 44.91) * mm, "end": v(-8.07, 44.9) * mm});
            skLineSegment(sketch, "E1260", {"start": v(-8.07, 44.9) * mm, "end": v(-8.1, 45.07) * mm});
            skLineSegment(sketch, "E1261", {"start": v(-8.1, 45.07) * mm, "end": v(-8.12, 45.23) * mm});
            skLineSegment(sketch, "E1262", {"start": v(-8.12, 45.23) * mm, "end": v(-8.15, 45.4) * mm});
            skLineSegment(sketch, "E1263", {"start": v(-8.15, 45.4) * mm, "end": v(-8.17, 45.56) * mm});
            skLineSegment(sketch, "E1264", {"start": v(-8.17, 45.56) * mm, "end": v(-8.2, 45.73) * mm});
            skLineSegment(sketch, "E1265", {"start": v(-8.2, 45.73) * mm, "end": v(-8.23, 45.9) * mm});
            skLineSegment(sketch, "E1266", {"start": v(-8.23, 45.9) * mm, "end": v(-8.25, 46.06) * mm});
            skLineSegment(sketch, "E1267", {"start": v(-8.25, 46.06) * mm, "end": v(-8.28, 46.23) * mm});
            skLineSegment(sketch, "E1268", {"start": v(-8.28, 46.23) * mm, "end": v(-8.3, 46.4) * mm});
            skLineSegment(sketch, "E1269", {"start": v(-8.3, 46.4) * mm, "end": v(-8.33, 46.56) * mm});
            skLineSegment(sketch, "E1270", {"start": v(-8.33, 46.56) * mm, "end": v(-8.36, 46.72) * mm});
            skLineSegment(sketch, "E1271", {"start": v(-8.36, 46.72) * mm, "end": v(-8.39, 46.9) * mm});
            skLineSegment(sketch, "E1272", {"start": v(-8.39, 46.9) * mm, "end": v(-8.42, 47.07) * mm});
            skLineSegment(sketch, "E1273", {"start": v(-8.42, 47.07) * mm, "end": v(-8.48, 47.23) * mm});
            skLineSegment(sketch, "E1274", {"start": v(-8.48, 47.23) * mm, "end": v(-8.58, 47.37) * mm});
            skLineSegment(sketch, "E1275", {"start": v(-8.58, 47.37) * mm, "end": v(-8.71, 47.48) * mm});
            skLineSegment(sketch, "E1276", {"start": v(-8.71, 47.48) * mm, "end": v(-8.87, 47.56) * mm});
            skLineSegment(sketch, "E1277", {"start": v(-8.87, 47.56) * mm, "end": v(-9.04, 47.58) * mm});
            skLineSegment(sketch, "E1278", {"start": v(-9.04, 47.58) * mm, "end": v(-9.08, 47.58) * mm});
            skLineSegment(sketch, "E1279", {"start": v(-9.08, 47.58) * mm, "end": v(-9.25, 47.56) * mm});
            skLineSegment(sketch, "E1280", {"start": v(-9.25, 47.56) * mm, "end": v(-9.4, 47.49) * mm});
            skLineSegment(sketch, "E1281", {"start": v(-9.4, 47.49) * mm, "end": v(-9.54, 47.38) * mm});
            skLineSegment(sketch, "E1282", {"start": v(-9.54, 47.38) * mm, "end": v(-9.64, 47.24) * mm});
            skLineSegment(sketch, "E1283", {"start": v(-9.64, 47.24) * mm, "end": v(-9.7, 47.08) * mm});
            skLineSegment(sketch, "E1284", {"start": v(-9.7, 47.08) * mm, "end": v(-9.73, 46.9) * mm});
            skLineSegment(sketch, "E1285", {"start": v(-9.73, 46.9) * mm, "end": v(-9.7, 46.73) * mm});
            skLineSegment(sketch, "E1286", {"start": v(-9.7, 46.73) * mm, "end": v(-9.67, 46.57) * mm});
            skLineSegment(sketch, "E1287", {"start": v(-9.67, 46.57) * mm, "end": v(-9.64, 46.4) * mm});
            skLineSegment(sketch, "E1288", {"start": v(-9.64, 46.4) * mm, "end": v(-9.6, 46.24) * mm});
            skLineSegment(sketch, "E1289", {"start": v(-9.6, 46.24) * mm, "end": v(-9.58, 46.07) * mm});
            skLineSegment(sketch, "E1290", {"start": v(-9.58, 46.07) * mm, "end": v(-9.55, 45.91) * mm});
            skLineSegment(sketch, "E1291", {"start": v(-9.55, 45.91) * mm, "end": v(-9.51, 45.74) * mm});
            skLineSegment(sketch, "E1292", {"start": v(-9.51, 45.74) * mm, "end": v(-9.48, 45.58) * mm});
            skLineSegment(sketch, "E1293", {"start": v(-9.48, 45.58) * mm, "end": v(-9.45, 45.42) * mm});
            skLineSegment(sketch, "E1294", {"start": v(-9.45, 45.42) * mm, "end": v(-9.42, 45.25) * mm});
            skLineSegment(sketch, "E1295", {"start": v(-9.42, 45.25) * mm, "end": v(-9.39, 45.08) * mm});
            skLineSegment(sketch, "E1296", {"start": v(-9.39, 45.08) * mm, "end": v(-9.36, 44.92) * mm});
            skLineSegment(sketch, "E1297", {"start": v(-9.36, 44.92) * mm, "end": v(-9.32, 44.75) * mm});
            skLineSegment(sketch, "E1298", {"start": v(-9.32, 44.75) * mm, "end": v(-9.31, 44.68) * mm});
            skLineSegment(sketch, "E1299", {"start": v(-9.31, 44.68) * mm, "end": v(-9.47, 44.65) * mm});
            skLineSegment(sketch, "E1300", {"start": v(-9.47, 44.65) * mm, "end": v(-9.64, 44.61) * mm});
            skLineSegment(sketch, "E1301", {"start": v(-9.64, 44.61) * mm, "end": v(-9.8, 44.58) * mm});
            skLineSegment(sketch, "E1302", {"start": v(-9.8, 44.58) * mm, "end": v(-9.96, 44.54) * mm});
            skLineSegment(sketch, "E1303", {"start": v(-9.96, 44.54) * mm, "end": v(-10.13, 44.5) * mm});
            skLineSegment(sketch, "E1304", {"start": v(-10.13, 44.5) * mm, "end": v(-10.29, 44.47) * mm});
            skLineSegment(sketch, "E1305", {"start": v(-10.29, 44.47) * mm, "end": v(-10.45, 44.44) * mm});
            skLineSegment(sketch, "E1306", {"start": v(-10.45, 44.44) * mm, "end": v(-10.61, 44.4) * mm});
            skLineSegment(sketch, "E1307", {"start": v(-10.61, 44.4) * mm, "end": v(-10.78, 44.37) * mm});
            skLineSegment(sketch, "E1308", {"start": v(-10.78, 44.37) * mm, "end": v(-10.94, 44.34) * mm});
            skLineSegment(sketch, "E1309", {"start": v(-10.94, 44.34) * mm, "end": v(-11.1, 44.3) * mm});
            skLineSegment(sketch, "E1310", {"start": v(-11.1, 44.3) * mm, "end": v(-11.18, 44.29) * mm});
            skLineSegment(sketch, "E1311", {"start": v(-11.18, 44.29) * mm, "end": v(-11.22, 44.45) * mm});
            skLineSegment(sketch, "E1312", {"start": v(-11.22, 44.45) * mm, "end": v(-11.26, 44.6) * mm});
            skLineSegment(sketch, "E1313", {"start": v(-11.26, 44.6) * mm, "end": v(-11.3, 44.78) * mm});
            skLineSegment(sketch, "E1314", {"start": v(-11.3, 44.78) * mm, "end": v(-11.33, 44.94) * mm});
            skLineSegment(sketch, "E1315", {"start": v(-11.33, 44.94) * mm, "end": v(-11.37, 45.1) * mm});
            skLineSegment(sketch, "E1316", {"start": v(-11.37, 45.1) * mm, "end": v(-11.41, 45.27) * mm});
            skLineSegment(sketch, "E1317", {"start": v(-11.41, 45.27) * mm, "end": v(-11.45, 45.43) * mm});
            skLineSegment(sketch, "E1318", {"start": v(-11.45, 45.43) * mm, "end": v(-11.49, 45.6) * mm});
            skLineSegment(sketch, "E1319", {"start": v(-11.49, 45.6) * mm, "end": v(-11.53, 45.76) * mm});
            skLineSegment(sketch, "E1320", {"start": v(-11.53, 45.76) * mm, "end": v(-11.56, 45.92) * mm});
            skLineSegment(sketch, "E1321", {"start": v(-11.56, 45.92) * mm, "end": v(-11.6, 46.08) * mm});
            skLineSegment(sketch, "E1322", {"start": v(-11.6, 46.08) * mm, "end": v(-11.64, 46.25) * mm});
            skLineSegment(sketch, "E1323", {"start": v(-11.64, 46.25) * mm, "end": v(-11.68, 46.42) * mm});
            skLineSegment(sketch, "E1324", {"start": v(-11.68, 46.42) * mm, "end": v(-11.75, 46.58) * mm});
            skLineSegment(sketch, "E1325", {"start": v(-11.75, 46.58) * mm, "end": v(-11.86, 46.71) * mm});
            skLineSegment(sketch, "E1326", {"start": v(-11.86, 46.71) * mm, "end": v(-12, 46.82) * mm});
            skLineSegment(sketch, "E1327", {"start": v(-12, 46.82) * mm, "end": v(-12.17, 46.88) * mm});
            skLineSegment(sketch, "E1328", {"start": v(-12.17, 46.88) * mm, "end": v(-12.3, 46.9) * mm});
            skLineSegment(sketch, "E1329", {"start": v(-12.3, 46.9) * mm, "end": v(-12.48, 46.87) * mm});
            skLineSegment(sketch, "E1330", {"start": v(-12.48, 46.87) * mm, "end": v(-12.64, 46.81) * mm});
            skLineSegment(sketch, "E1331", {"start": v(-12.64, 46.81) * mm, "end": v(-12.78, 46.7) * mm});
            skLineSegment(sketch, "E1332", {"start": v(-12.78, 46.7) * mm, "end": v(-12.89, 46.57) * mm});
            skLineSegment(sketch, "E1333", {"start": v(-12.89, 46.57) * mm, "end": v(-12.95, 46.41) * mm});
            skLineSegment(sketch, "E1334", {"start": v(-12.95, 46.41) * mm, "end": v(-12.98, 46.24) * mm});
            skLineSegment(sketch, "E1335", {"start": v(-12.98, 46.24) * mm, "end": v(-12.96, 46.07) * mm});
            skLineSegment(sketch, "E1336", {"start": v(-12.96, 46.07) * mm, "end": v(-12.92, 45.9) * mm});
            skLineSegment(sketch, "E1337", {"start": v(-12.92, 45.9) * mm, "end": v(-12.87, 45.75) * mm});
            skLineSegment(sketch, "E1338", {"start": v(-12.87, 45.75) * mm, "end": v(-12.83, 45.58) * mm});
            skLineSegment(sketch, "E1339", {"start": v(-12.83, 45.58) * mm, "end": v(-12.79, 45.42) * mm});
            skLineSegment(sketch, "E1340", {"start": v(-12.79, 45.42) * mm, "end": v(-12.75, 45.26) * mm});
            skLineSegment(sketch, "E1341", {"start": v(-12.75, 45.26) * mm, "end": v(-12.7, 45.1) * mm});
            skLineSegment(sketch, "E1342", {"start": v(-12.7, 45.1) * mm, "end": v(-12.66, 44.93) * mm});
            skLineSegment(sketch, "E1343", {"start": v(-12.66, 44.93) * mm, "end": v(-12.62, 44.77) * mm});
            skLineSegment(sketch, "E1344", {"start": v(-12.62, 44.77) * mm, "end": v(-12.57, 44.6) * mm});
            skLineSegment(sketch, "E1345", {"start": v(-12.57, 44.6) * mm, "end": v(-12.53, 44.44) * mm});
            skLineSegment(sketch, "E1346", {"start": v(-12.53, 44.44) * mm, "end": v(-12.49, 44.28) * mm});
            skLineSegment(sketch, "E1347", {"start": v(-12.49, 44.28) * mm, "end": v(-12.44, 44.12) * mm});
            skLineSegment(sketch, "E1348", {"start": v(-12.44, 44.12) * mm, "end": v(-12.4, 43.98) * mm});
            skLineSegment(sketch, "E1349", {"start": v(-12.4, 43.98) * mm, "end": v(-12.57, 43.93) * mm});
            skLineSegment(sketch, "E1350", {"start": v(-12.57, 43.93) * mm, "end": v(-12.73, 43.89) * mm});
            skLineSegment(sketch, "E1351", {"start": v(-12.73, 43.89) * mm, "end": v(-12.89, 43.84) * mm});
            skLineSegment(sketch, "E1352", {"start": v(-12.89, 43.84) * mm, "end": v(-13.05, 43.8) * mm});
            skLineSegment(sketch, "E1353", {"start": v(-13.05, 43.8) * mm, "end": v(-13.2, 43.75) * mm});
            skLineSegment(sketch, "E1354", {"start": v(-13.2, 43.75) * mm, "end": v(-13.37, 43.7) * mm});
            skLineSegment(sketch, "E1355", {"start": v(-13.37, 43.7) * mm, "end": v(-13.53, 43.66) * mm});
            skLineSegment(sketch, "E1356", {"start": v(-13.53, 43.66) * mm, "end": v(-13.69, 43.61) * mm});
            skLineSegment(sketch, "E1357", {"start": v(-13.69, 43.61) * mm, "end": v(-13.85, 43.57) * mm});
            skLineSegment(sketch, "E1358", {"start": v(-13.85, 43.57) * mm, "end": v(-14, 43.52) * mm});
            skLineSegment(sketch, "E1359", {"start": v(-14, 43.52) * mm, "end": v(-14.17, 43.47) * mm});
            skLineSegment(sketch, "E1360", {"start": v(-14.17, 43.47) * mm, "end": v(-14.24, 43.45) * mm});
            skLineSegment(sketch, "E1361", {"start": v(-14.24, 43.45) * mm, "end": v(-14.3, 43.61) * mm});
            skLineSegment(sketch, "E1362", {"start": v(-14.3, 43.61) * mm, "end": v(-14.34, 43.77) * mm});
            skLineSegment(sketch, "E1363", {"start": v(-14.34, 43.77) * mm, "end": v(-14.4, 43.93) * mm});
            skLineSegment(sketch, "E1364", {"start": v(-14.4, 43.93) * mm, "end": v(-14.44, 44.1) * mm});
            skLineSegment(sketch, "E1365", {"start": v(-14.44, 44.1) * mm, "end": v(-14.5, 44.25) * mm});
            skLineSegment(sketch, "E1366", {"start": v(-14.5, 44.25) * mm, "end": v(-14.54, 44.42) * mm});
            skLineSegment(sketch, "E1367", {"start": v(-14.54, 44.42) * mm, "end": v(-14.6, 44.57) * mm});
            skLineSegment(sketch, "E1368", {"start": v(-14.6, 44.57) * mm, "end": v(-14.64, 44.73) * mm});
            skLineSegment(sketch, "E1369", {"start": v(-14.64, 44.73) * mm, "end": v(-14.7, 44.9) * mm});
            skLineSegment(sketch, "E1370", {"start": v(-14.7, 44.9) * mm, "end": v(-14.74, 45.06) * mm});
            skLineSegment(sketch, "E1371", {"start": v(-14.74, 45.06) * mm, "end": v(-14.8, 45.21) * mm});
            skLineSegment(sketch, "E1372", {"start": v(-14.8, 45.21) * mm, "end": v(-14.84, 45.38) * mm});
            skLineSegment(sketch, "E1373", {"start": v(-14.84, 45.38) * mm, "end": v(-14.9, 45.55) * mm});
            skLineSegment(sketch, "E1374", {"start": v(-14.9, 45.55) * mm, "end": v(-14.98, 45.7) * mm});
            skLineSegment(sketch, "E1375", {"start": v(-14.98, 45.7) * mm, "end": v(-15.1, 45.83) * mm});
            skLineSegment(sketch, "E1376", {"start": v(-15.1, 45.83) * mm, "end": v(-15.24, 45.92) * mm});
            skLineSegment(sketch, "E1377", {"start": v(-15.24, 45.92) * mm, "end": v(-15.4, 45.97) * mm});
            skLineSegment(sketch, "E1378", {"start": v(-15.4, 45.97) * mm, "end": v(-15.51, 45.98) * mm});
            skLineSegment(sketch, "E1379", {"start": v(-15.51, 45.98) * mm, "end": v(-15.69, 45.95) * mm});
            skLineSegment(sketch, "E1380", {"start": v(-15.69, 45.95) * mm, "end": v(-15.85, 45.89) * mm});
            skLineSegment(sketch, "E1381", {"start": v(-15.85, 45.89) * mm, "end": v(-15.98, 45.78) * mm});
            skLineSegment(sketch, "E1382", {"start": v(-15.98, 45.78) * mm, "end": v(-16.09, 45.64) * mm});
            skLineSegment(sketch, "E1383", {"start": v(-16.09, 45.64) * mm, "end": v(-16.15, 45.48) * mm});
            skLineSegment(sketch, "E1384", {"start": v(-16.15, 45.48) * mm, "end": v(-16.18, 45.31) * mm});
            skLineSegment(sketch, "E1385", {"start": v(-16.18, 45.31) * mm, "end": v(-16.15, 45.14) * mm});
            skLineSegment(sketch, "E1386", {"start": v(-16.15, 45.14) * mm, "end": v(-16.1, 44.97) * mm});
            skLineSegment(sketch, "E1387", {"start": v(-16.1, 44.97) * mm, "end": v(-16.04, 44.81) * mm});
            skLineSegment(sketch, "E1388", {"start": v(-16.04, 44.81) * mm, "end": v(-15.99, 44.65) * mm});
            skLineSegment(sketch, "E1389", {"start": v(-15.99, 44.65) * mm, "end": v(-15.93, 44.5) * mm});
            skLineSegment(sketch, "E1390", {"start": v(-15.93, 44.5) * mm, "end": v(-15.88, 44.34) * mm});
            skLineSegment(sketch, "E1391", {"start": v(-15.88, 44.34) * mm, "end": v(-15.83, 44.18) * mm});
            skLineSegment(sketch, "E1392", {"start": v(-15.83, 44.18) * mm, "end": v(-15.77, 44.02) * mm});
            skLineSegment(sketch, "E1393", {"start": v(-15.77, 44.02) * mm, "end": v(-15.72, 43.86) * mm});
            skLineSegment(sketch, "E1394", {"start": v(-15.72, 43.86) * mm, "end": v(-15.66, 43.7) * mm});
            skLineSegment(sketch, "E1395", {"start": v(-15.66, 43.7) * mm, "end": v(-15.6, 43.54) * mm});
            skLineSegment(sketch, "E1396", {"start": v(-15.6, 43.54) * mm, "end": v(-15.56, 43.38) * mm});
            skLineSegment(sketch, "E1397", {"start": v(-15.56, 43.38) * mm, "end": v(-15.5, 43.22) * mm});
            skLineSegment(sketch, "E1398", {"start": v(-15.5, 43.22) * mm, "end": v(-15.45, 43.06) * mm});
            skLineSegment(sketch, "E1399", {"start": v(-15.45, 43.06) * mm, "end": v(-15.6, 43) * mm});
            skLineSegment(sketch, "E1400", {"start": v(-15.6, 43) * mm, "end": v(-15.76, 42.95) * mm});
            skLineSegment(sketch, "E1401", {"start": v(-15.76, 42.95) * mm, "end": v(-15.92, 42.9) * mm});
            skLineSegment(sketch, "E1402", {"start": v(-15.92, 42.9) * mm, "end": v(-16.07, 42.83) * mm});
            skLineSegment(sketch, "E1403", {"start": v(-16.07, 42.83) * mm, "end": v(-16.23, 42.78) * mm});
            skLineSegment(sketch, "E1404", {"start": v(-16.23, 42.78) * mm, "end": v(-16.39, 42.72) * mm});
            skLineSegment(sketch, "E1405", {"start": v(-16.39, 42.72) * mm, "end": v(-16.54, 42.66) * mm});
            skLineSegment(sketch, "E1406", {"start": v(-16.54, 42.66) * mm, "end": v(-16.7, 42.6) * mm});
            skLineSegment(sketch, "E1407", {"start": v(-16.7, 42.6) * mm, "end": v(-16.85, 42.55) * mm});
            skLineSegment(sketch, "E1408", {"start": v(-16.85, 42.55) * mm, "end": v(-17.01, 42.5) * mm});
            skLineSegment(sketch, "E1409", {"start": v(-17.01, 42.5) * mm, "end": v(-17.17, 42.44) * mm});
            skLineSegment(sketch, "E1410", {"start": v(-17.17, 42.44) * mm, "end": v(-17.24, 42.4) * mm});
            skLineSegment(sketch, "E1411", {"start": v(-17.24, 42.4) * mm, "end": v(-17.3, 42.56) * mm});
            skLineSegment(sketch, "E1412", {"start": v(-17.3, 42.56) * mm, "end": v(-17.36, 42.72) * mm});
            skLineSegment(sketch, "E1413", {"start": v(-17.36, 42.72) * mm, "end": v(-17.43, 42.88) * mm});
            skLineSegment(sketch, "E1414", {"start": v(-17.43, 42.88) * mm, "end": v(-17.49, 43.03) * mm});
            skLineSegment(sketch, "E1415", {"start": v(-17.49, 43.03) * mm, "end": v(-17.55, 43.19) * mm});
            skLineSegment(sketch, "E1416", {"start": v(-17.55, 43.19) * mm, "end": v(-17.6, 43.35) * mm});
            skLineSegment(sketch, "E1417", {"start": v(-17.6, 43.35) * mm, "end": v(-17.67, 43.5) * mm});
            skLineSegment(sketch, "E1418", {"start": v(-17.67, 43.5) * mm, "end": v(-17.73, 43.66) * mm});
            skLineSegment(sketch, "E1419", {"start": v(-17.73, 43.66) * mm, "end": v(-17.79, 43.82) * mm});
            skLineSegment(sketch, "E1420", {"start": v(-17.79, 43.82) * mm, "end": v(-17.85, 43.97) * mm});
            skLineSegment(sketch, "E1421", {"start": v(-17.85, 43.97) * mm, "end": v(-17.91, 44.13) * mm});
            skLineSegment(sketch, "E1422", {"start": v(-17.91, 44.13) * mm, "end": v(-17.97, 44.29) * mm});
            skLineSegment(sketch, "E1423", {"start": v(-17.97, 44.29) * mm, "end": v(-18.04, 44.45) * mm});
            skLineSegment(sketch, "E1424", {"start": v(-18.04, 44.45) * mm, "end": v(-18.13, 44.6) * mm});
            skLineSegment(sketch, "E1425", {"start": v(-18.13, 44.6) * mm, "end": v(-18.26, 44.72) * mm});
            skLineSegment(sketch, "E1426", {"start": v(-18.26, 44.72) * mm, "end": v(-18.41, 44.8) * mm});
            skLineSegment(sketch, "E1427", {"start": v(-18.41, 44.8) * mm, "end": v(-18.58, 44.84) * mm});
            skLineSegment(sketch, "E1428", {"start": v(-18.58, 44.84) * mm, "end": v(-18.65, 44.84) * mm});
            skLineSegment(sketch, "E1429", {"start": v(-18.65, 44.84) * mm, "end": v(-18.82, 44.81) * mm});
            skLineSegment(sketch, "E1430", {"start": v(-18.82, 44.81) * mm, "end": v(-18.98, 44.74) * mm});
            skLineSegment(sketch, "E1431", {"start": v(-18.98, 44.74) * mm, "end": v(-19.12, 44.64) * mm});
            skLineSegment(sketch, "E1432", {"start": v(-19.12, 44.64) * mm, "end": v(-19.22, 44.5) * mm});
            skLineSegment(sketch, "E1433", {"start": v(-19.22, 44.5) * mm, "end": v(-19.28, 44.34) * mm});
            skLineSegment(sketch, "E1434", {"start": v(-19.28, 44.34) * mm, "end": v(-19.3, 44.16) * mm});
            skLineSegment(sketch, "E1435", {"start": v(-19.3, 44.16) * mm, "end": v(-19.28, 44) * mm});
            skLineSegment(sketch, "E1436", {"start": v(-19.28, 44) * mm, "end": v(-19.21, 43.84) * mm});
            skLineSegment(sketch, "E1437", {"start": v(-19.21, 43.84) * mm, "end": v(-19.15, 43.68) * mm});
            skLineSegment(sketch, "E1438", {"start": v(-19.15, 43.68) * mm, "end": v(-19.08, 43.53) * mm});
            skLineSegment(sketch, "E1439", {"start": v(-19.08, 43.53) * mm, "end": v(-19.02, 43.37) * mm});
            skLineSegment(sketch, "E1440", {"start": v(-19.02, 43.37) * mm, "end": v(-18.96, 43.22) * mm});
            skLineSegment(sketch, "E1441", {"start": v(-18.96, 43.22) * mm, "end": v(-18.89, 43.06) * mm});
            skLineSegment(sketch, "E1442", {"start": v(-18.89, 43.06) * mm, "end": v(-18.82, 42.9) * mm});
            skLineSegment(sketch, "E1443", {"start": v(-18.82, 42.9) * mm, "end": v(-18.76, 42.76) * mm});
            skLineSegment(sketch, "E1444", {"start": v(-18.76, 42.76) * mm, "end": v(-18.7, 42.6) * mm});
            skLineSegment(sketch, "E1445", {"start": v(-18.7, 42.6) * mm, "end": v(-18.63, 42.44) * mm});
            skLineSegment(sketch, "E1446", {"start": v(-18.63, 42.44) * mm, "end": v(-18.57, 42.3) * mm});
            skLineSegment(sketch, "E1447", {"start": v(-18.57, 42.3) * mm, "end": v(-18.5, 42.13) * mm});
            skLineSegment(sketch, "E1448", {"start": v(-18.5, 42.13) * mm, "end": v(-18.43, 41.98) * mm});
            skLineSegment(sketch, "E1449", {"start": v(-18.43, 41.98) * mm, "end": v(-18.42, 41.93) * mm});
            skLineSegment(sketch, "E1450", {"start": v(-18.42, 41.93) * mm, "end": v(-18.57, 41.87) * mm});
            skLineSegment(sketch, "E1451", {"start": v(-18.57, 41.87) * mm, "end": v(-18.72, 41.8) * mm});
            skLineSegment(sketch, "E1452", {"start": v(-18.72, 41.8) * mm, "end": v(-18.87, 41.73) * mm});
            skLineSegment(sketch, "E1453", {"start": v(-18.87, 41.73) * mm, "end": v(-19.02, 41.66) * mm});
            skLineSegment(sketch, "E1454", {"start": v(-19.02, 41.66) * mm, "end": v(-19.18, 41.6) * mm});
            skLineSegment(sketch, "E1455", {"start": v(-19.18, 41.6) * mm, "end": v(-19.33, 41.53) * mm});
            skLineSegment(sketch, "E1456", {"start": v(-19.33, 41.53) * mm, "end": v(-19.48, 41.46) * mm});
            skLineSegment(sketch, "E1457", {"start": v(-19.48, 41.46) * mm, "end": v(-19.63, 41.4) * mm});
            skLineSegment(sketch, "E1458", {"start": v(-19.63, 41.4) * mm, "end": v(-19.78, 41.33) * mm});
            skLineSegment(sketch, "E1459", {"start": v(-19.78, 41.33) * mm, "end": v(-19.94, 41.26) * mm});
            skLineSegment(sketch, "E1460", {"start": v(-19.94, 41.26) * mm, "end": v(-20.09, 41.2) * mm});
            skLineSegment(sketch, "E1461", {"start": v(-20.09, 41.2) * mm, "end": v(-20.16, 41.16) * mm});
            skLineSegment(sketch, "E1462", {"start": v(-20.16, 41.16) * mm, "end": v(-20.23, 41.3) * mm});
            skLineSegment(sketch, "E1463", {"start": v(-20.23, 41.3) * mm, "end": v(-20.3, 41.46) * mm});
            skLineSegment(sketch, "E1464", {"start": v(-20.3, 41.46) * mm, "end": v(-20.38, 41.61) * mm});
            skLineSegment(sketch, "E1465", {"start": v(-20.38, 41.61) * mm, "end": v(-20.45, 41.76) * mm});
            skLineSegment(sketch, "E1466", {"start": v(-20.45, 41.76) * mm, "end": v(-20.52, 41.91) * mm});
            skLineSegment(sketch, "E1467", {"start": v(-20.52, 41.91) * mm, "end": v(-20.6, 42.07) * mm});
            skLineSegment(sketch, "E1468", {"start": v(-20.6, 42.07) * mm, "end": v(-20.66, 42.22) * mm});
            skLineSegment(sketch, "E1469", {"start": v(-20.66, 42.22) * mm, "end": v(-20.73, 42.37) * mm});
            skLineSegment(sketch, "E1470", {"start": v(-20.73, 42.37) * mm, "end": v(-20.8, 42.52) * mm});
            skLineSegment(sketch, "E1471", {"start": v(-20.8, 42.52) * mm, "end": v(-20.88, 42.68) * mm});
            skLineSegment(sketch, "E1472", {"start": v(-20.88, 42.68) * mm, "end": v(-20.95, 42.83) * mm});
            skLineSegment(sketch, "E1473", {"start": v(-20.95, 42.83) * mm, "end": v(-21.02, 42.98) * mm});
            skLineSegment(sketch, "E1474", {"start": v(-21.02, 42.98) * mm, "end": v(-21.1, 43.14) * mm});
            skLineSegment(sketch, "E1475", {"start": v(-21.1, 43.14) * mm, "end": v(-21.2, 43.28) * mm});
            skLineSegment(sketch, "E1476", {"start": v(-21.2, 43.28) * mm, "end": v(-21.33, 43.4) * mm});
            skLineSegment(sketch, "E1477", {"start": v(-21.33, 43.4) * mm, "end": v(-21.5, 43.46) * mm});
            skLineSegment(sketch, "E1478", {"start": v(-21.5, 43.46) * mm, "end": v(-21.66, 43.49) * mm});
            skLineSegment(sketch, "E1479", {"start": v(-21.66, 43.49) * mm, "end": v(-21.84, 43.47) * mm});
            skLineSegment(sketch, "E1480", {"start": v(-21.84, 43.47) * mm, "end": v(-22, 43.4) * mm});
            skLineSegment(sketch, "E1481", {"start": v(-22, 43.4) * mm, "end": v(-22.14, 43.3) * mm});
            skLineSegment(sketch, "E1482", {"start": v(-22.14, 43.3) * mm, "end": v(-22.25, 43.16) * mm});
            skLineSegment(sketch, "E1483", {"start": v(-22.25, 43.16) * mm, "end": v(-22.32, 43) * mm});
            skLineSegment(sketch, "E1484", {"start": v(-22.32, 43) * mm, "end": v(-22.34, 42.83) * mm});
            skLineSegment(sketch, "E1485", {"start": v(-22.34, 42.83) * mm, "end": v(-22.32, 42.66) * mm});
            skLineSegment(sketch, "E1486", {"start": v(-22.32, 42.66) * mm, "end": v(-22.26, 42.5) * mm});
            skLineSegment(sketch, "E1487", {"start": v(-22.26, 42.5) * mm, "end": v(-22.18, 42.36) * mm});
            skLineSegment(sketch, "E1488", {"start": v(-22.18, 42.36) * mm, "end": v(-22.1, 42.2) * mm});
            skLineSegment(sketch, "E1489", {"start": v(-22.1, 42.2) * mm, "end": v(-22.03, 42.06) * mm});
            skLineSegment(sketch, "E1490", {"start": v(-22.03, 42.06) * mm, "end": v(-21.96, 41.91) * mm});
            skLineSegment(sketch, "E1491", {"start": v(-21.96, 41.91) * mm, "end": v(-21.88, 41.76) * mm});
            skLineSegment(sketch, "E1492", {"start": v(-21.88, 41.76) * mm, "end": v(-21.8, 41.61) * mm});
            skLineSegment(sketch, "E1493", {"start": v(-21.8, 41.61) * mm, "end": v(-21.73, 41.46) * mm});
            skLineSegment(sketch, "E1494", {"start": v(-21.73, 41.46) * mm, "end": v(-21.65, 41.3) * mm});
            skLineSegment(sketch, "E1495", {"start": v(-21.65, 41.3) * mm, "end": v(-21.58, 41.16) * mm});
            skLineSegment(sketch, "E1496", {"start": v(-21.58, 41.16) * mm, "end": v(-21.5, 41.01) * mm});
            skLineSegment(sketch, "E1497", {"start": v(-21.5, 41.01) * mm, "end": v(-21.43, 40.86) * mm});
            skLineSegment(sketch, "E1498", {"start": v(-21.43, 40.86) * mm, "end": v(-21.35, 40.71) * mm});
            skLineSegment(sketch, "E1499", {"start": v(-21.35, 40.71) * mm, "end": v(-21.3, 40.6) * mm});
            skLineSegment(sketch, "E1500", {"start": v(-21.3, 40.6) * mm, "end": v(-21.44, 40.52) * mm});
            skLineSegment(sketch, "E1501", {"start": v(-21.44, 40.52) * mm, "end": v(-21.6, 40.45) * mm});
            skLineSegment(sketch, "E1502", {"start": v(-21.6, 40.45) * mm, "end": v(-21.74, 40.37) * mm});
            skLineSegment(sketch, "E1503", {"start": v(-21.74, 40.37) * mm, "end": v(-21.89, 40.3) * mm});
            skLineSegment(sketch, "E1504", {"start": v(-21.89, 40.3) * mm, "end": v(-22.03, 40.21) * mm});
            skLineSegment(sketch, "E1505", {"start": v(-22.03, 40.21) * mm, "end": v(-22.18, 40.13) * mm});
            skLineSegment(sketch, "E1506", {"start": v(-22.18, 40.13) * mm, "end": v(-22.33, 40.06) * mm});
            skLineSegment(sketch, "E1507", {"start": v(-22.33, 40.06) * mm, "end": v(-22.47, 39.98) * mm});
            skLineSegment(sketch, "E1508", {"start": v(-22.47, 39.98) * mm, "end": v(-22.62, 39.9) * mm});
            skLineSegment(sketch, "E1509", {"start": v(-22.62, 39.9) * mm, "end": v(-22.77, 39.82) * mm});
            skLineSegment(sketch, "E1510", {"start": v(-22.77, 39.82) * mm, "end": v(-22.91, 39.74) * mm});
            skLineSegment(sketch, "E1511", {"start": v(-22.91, 39.74) * mm, "end": v(-22.99, 39.7) * mm});
            skLineSegment(sketch, "E1512", {"start": v(-22.99, 39.7) * mm, "end": v(-23.07, 39.85) * mm});
            skLineSegment(sketch, "E1513", {"start": v(-23.07, 39.85) * mm, "end": v(-23.15, 40) * mm});
            skLineSegment(sketch, "E1514", {"start": v(-23.15, 40) * mm, "end": v(-23.23, 40.15) * mm});
            skLineSegment(sketch, "E1515", {"start": v(-23.23, 40.15) * mm, "end": v(-23.31, 40.3) * mm});
            skLineSegment(sketch, "E1516", {"start": v(-23.31, 40.3) * mm, "end": v(-23.4, 40.44) * mm});
            skLineSegment(sketch, "E1517", {"start": v(-23.4, 40.44) * mm, "end": v(-23.48, 40.59) * mm});
            skLineSegment(sketch, "E1518", {"start": v(-23.48, 40.59) * mm, "end": v(-23.56, 40.73) * mm});
            skLineSegment(sketch, "E1519", {"start": v(-23.56, 40.73) * mm, "end": v(-23.64, 40.88) * mm});
            skLineSegment(sketch, "E1520", {"start": v(-23.64, 40.88) * mm, "end": v(-23.72, 41.03) * mm});
            skLineSegment(sketch, "E1521", {"start": v(-23.72, 41.03) * mm, "end": v(-23.8, 41.17) * mm});
            skLineSegment(sketch, "E1522", {"start": v(-23.8, 41.17) * mm, "end": v(-23.88, 41.32) * mm});
            skLineSegment(sketch, "E1523", {"start": v(-23.88, 41.32) * mm, "end": v(-23.97, 41.46) * mm});
            skLineSegment(sketch, "E1524", {"start": v(-23.97, 41.46) * mm, "end": v(-24.06, 41.62) * mm});
            skLineSegment(sketch, "E1525", {"start": v(-24.06, 41.62) * mm, "end": v(-24.17, 41.75) * mm});
            skLineSegment(sketch, "E1526", {"start": v(-24.17, 41.75) * mm, "end": v(-24.31, 41.85) * mm});
            skLineSegment(sketch, "E1527", {"start": v(-24.31, 41.85) * mm, "end": v(-24.47, 41.91) * mm});
            skLineSegment(sketch, "E1528", {"start": v(-24.47, 41.91) * mm, "end": v(-24.61, 41.93) * mm});
            skLineSegment(sketch, "E1529", {"start": v(-24.61, 41.93) * mm, "end": v(-24.78, 41.9) * mm});
            skLineSegment(sketch, "E1530", {"start": v(-24.78, 41.9) * mm, "end": v(-24.95, 41.84) * mm});
            skLineSegment(sketch, "E1531", {"start": v(-24.95, 41.84) * mm, "end": v(-25.08, 41.73) * mm});
            skLineSegment(sketch, "E1532", {"start": v(-25.08, 41.73) * mm, "end": v(-25.19, 41.6) * mm});
            skLineSegment(sketch, "E1533", {"start": v(-25.19, 41.6) * mm, "end": v(-25.25, 41.43) * mm});
            skLineSegment(sketch, "E1534", {"start": v(-25.25, 41.43) * mm, "end": v(-25.28, 41.26) * mm});
            skLineSegment(sketch, "E1535", {"start": v(-25.28, 41.26) * mm, "end": v(-25.25, 41.09) * mm});
            skLineSegment(sketch, "E1536", {"start": v(-25.25, 41.09) * mm, "end": v(-25.19, 40.93) * mm});
            skLineSegment(sketch, "E1537", {"start": v(-25.19, 40.93) * mm, "end": v(-25.1, 40.79) * mm});
            skLineSegment(sketch, "E1538", {"start": v(-25.1, 40.79) * mm, "end": v(-25.02, 40.64) * mm});
            skLineSegment(sketch, "E1539", {"start": v(-25.02, 40.64) * mm, "end": v(-24.93, 40.5) * mm});
            skLineSegment(sketch, "E1540", {"start": v(-24.93, 40.5) * mm, "end": v(-24.84, 40.35) * mm});
            skLineSegment(sketch, "E1541", {"start": v(-24.84, 40.35) * mm, "end": v(-24.76, 40.2) * mm});
            skLineSegment(sketch, "E1542", {"start": v(-24.76, 40.2) * mm, "end": v(-24.67, 40.06) * mm});
            skLineSegment(sketch, "E1543", {"start": v(-24.67, 40.06) * mm, "end": v(-24.58, 39.92) * mm});
            skLineSegment(sketch, "E1544", {"start": v(-24.58, 39.92) * mm, "end": v(-24.5, 39.78) * mm});
            skLineSegment(sketch, "E1545", {"start": v(-24.5, 39.78) * mm, "end": v(-24.41, 39.63) * mm});
            skLineSegment(sketch, "E1546", {"start": v(-24.41, 39.63) * mm, "end": v(-24.33, 39.49) * mm});
            skLineSegment(sketch, "E1547", {"start": v(-24.33, 39.49) * mm, "end": v(-24.24, 39.34) * mm});
            skLineSegment(sketch, "E1548", {"start": v(-24.24, 39.34) * mm, "end": v(-24.15, 39.2) * mm});
            skLineSegment(sketch, "E1549", {"start": v(-24.15, 39.2) * mm, "end": v(-24.08, 39.07) * mm});
            skLineSegment(sketch, "E1550", {"start": v(-24.08, 39.07) * mm, "end": v(-24.22, 38.99) * mm});
            skLineSegment(sketch, "E1551", {"start": v(-24.22, 38.99) * mm, "end": v(-24.36, 38.9) * mm});
            skLineSegment(sketch, "E1552", {"start": v(-24.36, 38.9) * mm, "end": v(-24.5, 38.8) * mm});
            skLineSegment(sketch, "E1553", {"start": v(-24.5, 38.8) * mm, "end": v(-24.64, 38.72) * mm});
            skLineSegment(sketch, "E1554", {"start": v(-24.64, 38.72) * mm, "end": v(-24.79, 38.63) * mm});
            skLineSegment(sketch, "E1555", {"start": v(-24.79, 38.63) * mm, "end": v(-24.93, 38.54) * mm});
            skLineSegment(sketch, "E1556", {"start": v(-24.93, 38.54) * mm, "end": v(-25.07, 38.46) * mm});
            skLineSegment(sketch, "E1557", {"start": v(-25.07, 38.46) * mm, "end": v(-25.2, 38.37) * mm});
            skLineSegment(sketch, "E1558", {"start": v(-25.2, 38.37) * mm, "end": v(-25.35, 38.28) * mm});
            skLineSegment(sketch, "E1559", {"start": v(-25.35, 38.28) * mm, "end": v(-25.5, 38.2) * mm});
            skLineSegment(sketch, "E1560", {"start": v(-25.5, 38.2) * mm, "end": v(-25.63, 38.1) * mm});
            skLineSegment(sketch, "E1561", {"start": v(-25.63, 38.1) * mm, "end": v(-25.7, 38.06) * mm});
            skLineSegment(sketch, "E1562", {"start": v(-25.7, 38.06) * mm, "end": v(-25.8, 38.2) * mm});
            skLineSegment(sketch, "E1563", {"start": v(-25.8, 38.2) * mm, "end": v(-25.88, 38.34) * mm});
            skLineSegment(sketch, "E1564", {"start": v(-25.88, 38.34) * mm, "end": v(-25.98, 38.48) * mm});
            skLineSegment(sketch, "E1565", {"start": v(-25.98, 38.48) * mm, "end": v(-26.07, 38.62) * mm});
            skLineSegment(sketch, "E1566", {"start": v(-26.07, 38.62) * mm, "end": v(-26.16, 38.76) * mm});
            skLineSegment(sketch, "E1567", {"start": v(-26.16, 38.76) * mm, "end": v(-26.25, 38.9) * mm});
            skLineSegment(sketch, "E1568", {"start": v(-26.25, 38.9) * mm, "end": v(-26.34, 39.04) * mm});
            skLineSegment(sketch, "E1569", {"start": v(-26.34, 39.04) * mm, "end": v(-26.43, 39.18) * mm});
            skLineSegment(sketch, "E1570", {"start": v(-26.43, 39.18) * mm, "end": v(-26.53, 39.33) * mm});
            skLineSegment(sketch, "E1571", {"start": v(-26.53, 39.33) * mm, "end": v(-26.62, 39.46) * mm});
            skLineSegment(sketch, "E1572", {"start": v(-26.62, 39.46) * mm, "end": v(-26.71, 39.6) * mm});
            skLineSegment(sketch, "E1573", {"start": v(-26.71, 39.6) * mm, "end": v(-26.8, 39.75) * mm});
            skLineSegment(sketch, "E1574", {"start": v(-26.8, 39.75) * mm, "end": v(-26.9, 39.9) * mm});
            skLineSegment(sketch, "E1575", {"start": v(-26.9, 39.9) * mm, "end": v(-27.02, 40.02) * mm});
            skLineSegment(sketch, "E1576", {"start": v(-27.02, 40.02) * mm, "end": v(-27.17, 40.1) * mm});
            skLineSegment(sketch, "E1577", {"start": v(-27.17, 40.1) * mm, "end": v(-27.34, 40.16) * mm});
            skLineSegment(sketch, "E1578", {"start": v(-27.34, 40.16) * mm, "end": v(-27.44, 40.16) * mm});
            skLineSegment(sketch, "E1579", {"start": v(-27.44, 40.16) * mm, "end": v(-27.62, 40.14) * mm});
            skLineSegment(sketch, "E1580", {"start": v(-27.62, 40.14) * mm, "end": v(-27.78, 40.07) * mm});
            skLineSegment(sketch, "E1581", {"start": v(-27.78, 40.07) * mm, "end": v(-27.91, 39.96) * mm});
            skLineSegment(sketch, "E1582", {"start": v(-27.91, 39.96) * mm, "end": v(-28.01, 39.82) * mm});
            skLineSegment(sketch, "E1583", {"start": v(-28.01, 39.82) * mm, "end": v(-28.08, 39.66) * mm});
            skLineSegment(sketch, "E1584", {"start": v(-28.08, 39.66) * mm, "end": v(-28.1, 39.49) * mm});
            skLineSegment(sketch, "E1585", {"start": v(-28.1, 39.49) * mm, "end": v(-28.07, 39.32) * mm});
            skLineSegment(sketch, "E1586", {"start": v(-28.07, 39.32) * mm, "end": v(-28, 39.16) * mm});
            skLineSegment(sketch, "E1587", {"start": v(-28, 39.16) * mm, "end": v(-27.9, 39) * mm});
            skLineSegment(sketch, "E1588", {"start": v(-27.9, 39) * mm, "end": v(-27.8, 38.87) * mm});
            skLineSegment(sketch, "E1589", {"start": v(-27.8, 38.87) * mm, "end": v(-27.7, 38.74) * mm});
            skLineSegment(sketch, "E1590", {"start": v(-27.7, 38.74) * mm, "end": v(-27.61, 38.6) * mm});
            skLineSegment(sketch, "E1591", {"start": v(-27.61, 38.6) * mm, "end": v(-27.52, 38.46) * mm});
            skLineSegment(sketch, "E1592", {"start": v(-27.52, 38.46) * mm, "end": v(-27.42, 38.32) * mm});
            skLineSegment(sketch, "E1593", {"start": v(-27.42, 38.32) * mm, "end": v(-27.32, 38.18) * mm});
            skLineSegment(sketch, "E1594", {"start": v(-27.32, 38.18) * mm, "end": v(-27.23, 38.04) * mm});
            skLineSegment(sketch, "E1595", {"start": v(-27.23, 38.04) * mm, "end": v(-27.13, 37.9) * mm});
            skLineSegment(sketch, "E1596", {"start": v(-27.13, 37.9) * mm, "end": v(-27.04, 37.77) * mm});
            skLineSegment(sketch, "E1597", {"start": v(-27.04, 37.77) * mm, "end": v(-26.94, 37.63) * mm});
            skLineSegment(sketch, "E1598", {"start": v(-26.94, 37.63) * mm, "end": v(-26.85, 37.5) * mm});
            skLineSegment(sketch, "E1599", {"start": v(-26.85, 37.5) * mm, "end": v(-26.75, 37.35) * mm});
            skLineSegment(sketch, "E1600", {"start": v(-26.75, 37.35) * mm, "end": v(-26.88, 37.26) * mm});
            skLineSegment(sketch, "E1601", {"start": v(-26.88, 37.26) * mm, "end": v(-27.02, 37.16) * mm});
            skLineSegment(sketch, "E1602", {"start": v(-27.02, 37.16) * mm, "end": v(-27.15, 37.06) * mm});
            skLineSegment(sketch, "E1603", {"start": v(-27.15, 37.06) * mm, "end": v(-27.29, 36.96) * mm});
            skLineSegment(sketch, "E1604", {"start": v(-27.29, 36.96) * mm, "end": v(-27.42, 36.86) * mm});
            skLineSegment(sketch, "E1605", {"start": v(-27.42, 36.86) * mm, "end": v(-27.56, 36.77) * mm});
            skLineSegment(sketch, "E1606", {"start": v(-27.56, 36.77) * mm, "end": v(-27.7, 36.67) * mm});
            skLineSegment(sketch, "E1607", {"start": v(-27.7, 36.67) * mm, "end": v(-27.83, 36.57) * mm});
            skLineSegment(sketch, "E1608", {"start": v(-27.83, 36.57) * mm, "end": v(-27.96, 36.47) * mm});
            skLineSegment(sketch, "E1609", {"start": v(-27.96, 36.47) * mm, "end": v(-28.1, 36.38) * mm});
            skLineSegment(sketch, "E1610", {"start": v(-28.1, 36.38) * mm, "end": v(-28.23, 36.28) * mm});
            skLineSegment(sketch, "E1611", {"start": v(-28.23, 36.28) * mm, "end": v(-28.3, 36.23) * mm});
            skLineSegment(sketch, "E1612", {"start": v(-28.3, 36.23) * mm, "end": v(-28.4, 36.36) * mm});
            skLineSegment(sketch, "E1613", {"start": v(-28.4, 36.36) * mm, "end": v(-28.5, 36.5) * mm});
            skLineSegment(sketch, "E1614", {"start": v(-28.5, 36.5) * mm, "end": v(-28.6, 36.63) * mm});
            skLineSegment(sketch, "E1615", {"start": v(-28.6, 36.63) * mm, "end": v(-28.7, 36.76) * mm});
            skLineSegment(sketch, "E1616", {"start": v(-28.7, 36.76) * mm, "end": v(-28.8, 36.9) * mm});
            skLineSegment(sketch, "E1617", {"start": v(-28.8, 36.9) * mm, "end": v(-28.9, 37.03) * mm});
            skLineSegment(sketch, "E1618", {"start": v(-28.9, 37.03) * mm, "end": v(-29, 37.17) * mm});
            skLineSegment(sketch, "E1619", {"start": v(-29, 37.17) * mm, "end": v(-29.1, 37.3) * mm});
            skLineSegment(sketch, "E1620", {"start": v(-29.1, 37.3) * mm, "end": v(-29.2, 37.43) * mm});
            skLineSegment(sketch, "E1621", {"start": v(-29.2, 37.43) * mm, "end": v(-29.3, 37.57) * mm});
            skLineSegment(sketch, "E1622", {"start": v(-29.3, 37.57) * mm, "end": v(-29.41, 37.7) * mm});
            skLineSegment(sketch, "E1623", {"start": v(-29.41, 37.7) * mm, "end": v(-29.51, 37.84) * mm});
            skLineSegment(sketch, "E1624", {"start": v(-29.51, 37.84) * mm, "end": v(-29.62, 37.98) * mm});
            skLineSegment(sketch, "E1625", {"start": v(-29.62, 37.98) * mm, "end": v(-29.75, 38.1) * mm});
            skLineSegment(sketch, "E1626", {"start": v(-29.75, 38.1) * mm, "end": v(-29.9, 38.17) * mm});
            skLineSegment(sketch, "E1627", {"start": v(-29.9, 38.17) * mm, "end": v(-30.08, 38.2) * mm});
            skLineSegment(sketch, "E1628", {"start": v(-30.08, 38.2) * mm, "end": v(-30.11, 38.2) * mm});
            skLineSegment(sketch, "E1629", {"start": v(-30.11, 38.2) * mm, "end": v(-30.28, 38.19) * mm});
            skLineSegment(sketch, "E1630", {"start": v(-30.28, 38.19) * mm, "end": v(-30.45, 38.13) * mm});
            skLineSegment(sketch, "E1631", {"start": v(-30.45, 38.13) * mm, "end": v(-30.59, 38.02) * mm});
            skLineSegment(sketch, "E1632", {"start": v(-30.59, 38.02) * mm, "end": v(-30.7, 37.89) * mm});
            skLineSegment(sketch, "E1633", {"start": v(-30.7, 37.89) * mm, "end": v(-30.76, 37.73) * mm});
            skLineSegment(sketch, "E1634", {"start": v(-30.76, 37.73) * mm, "end": v(-30.79, 37.56) * mm});
            skLineSegment(sketch, "E1635", {"start": v(-30.79, 37.56) * mm, "end": v(-30.77, 37.38) * mm});
            skLineSegment(sketch, "E1636", {"start": v(-30.77, 37.38) * mm, "end": v(-30.7, 37.22) * mm});
            skLineSegment(sketch, "E1637", {"start": v(-30.7, 37.22) * mm, "end": v(-30.6, 37.08) * mm});
            skLineSegment(sketch, "E1638", {"start": v(-30.6, 37.08) * mm, "end": v(-30.5, 36.95) * mm});
            skLineSegment(sketch, "E1639", {"start": v(-30.5, 36.95) * mm, "end": v(-30.4, 36.82) * mm});
            skLineSegment(sketch, "E1640", {"start": v(-30.4, 36.82) * mm, "end": v(-30.28, 36.69) * mm});
            skLineSegment(sketch, "E1641", {"start": v(-30.28, 36.69) * mm, "end": v(-30.18, 36.56) * mm});
            skLineSegment(sketch, "E1642", {"start": v(-30.18, 36.56) * mm, "end": v(-30.07, 36.43) * mm});
            skLineSegment(sketch, "E1643", {"start": v(-30.07, 36.43) * mm, "end": v(-29.97, 36.3) * mm});
            skLineSegment(sketch, "E1644", {"start": v(-29.97, 36.3) * mm, "end": v(-29.86, 36.16) * mm});
            skLineSegment(sketch, "E1645", {"start": v(-29.86, 36.16) * mm, "end": v(-29.76, 36.03) * mm});
            skLineSegment(sketch, "E1646", {"start": v(-29.76, 36.03) * mm, "end": v(-29.65, 35.9) * mm});
            skLineSegment(sketch, "E1647", {"start": v(-29.65, 35.9) * mm, "end": v(-29.55, 35.77) * mm});
            skLineSegment(sketch, "E1648", {"start": v(-29.55, 35.77) * mm, "end": v(-29.44, 35.64) * mm});
            skLineSegment(sketch, "E1649", {"start": v(-29.44, 35.64) * mm, "end": v(-29.34, 35.5) * mm});
            skLineSegment(sketch, "E1650", {"start": v(-29.34, 35.5) * mm, "end": v(-29.3, 35.45) * mm});
            skLineSegment(sketch, "E1651", {"start": v(-29.3, 35.45) * mm, "end": v(-29.42, 35.35) * mm});
            skLineSegment(sketch, "E1652", {"start": v(-29.42, 35.35) * mm, "end": v(-29.55, 35.24) * mm});
            skLineSegment(sketch, "E1653", {"start": v(-29.55, 35.24) * mm, "end": v(-29.67, 35.13) * mm});
            skLineSegment(sketch, "E1654", {"start": v(-29.67, 35.13) * mm, "end": v(-29.8, 35.02) * mm});
            skLineSegment(sketch, "E1655", {"start": v(-29.8, 35.02) * mm, "end": v(-29.93, 34.92) * mm});
            skLineSegment(sketch, "E1656", {"start": v(-29.93, 34.92) * mm, "end": v(-30.06, 34.81) * mm});
            skLineSegment(sketch, "E1657", {"start": v(-30.06, 34.81) * mm, "end": v(-30.18, 34.7) * mm});
            skLineSegment(sketch, "E1658", {"start": v(-30.18, 34.7) * mm, "end": v(-30.31, 34.6) * mm});
            skLineSegment(sketch, "E1659", {"start": v(-30.31, 34.6) * mm, "end": v(-30.44, 34.49) * mm});
            skLineSegment(sketch, "E1660", {"start": v(-30.44, 34.49) * mm, "end": v(-30.57, 34.38) * mm});
            skLineSegment(sketch, "E1661", {"start": v(-30.57, 34.38) * mm, "end": v(-30.7, 34.28) * mm});
            skLineSegment(sketch, "E1662", {"start": v(-30.7, 34.28) * mm, "end": v(-30.76, 34.22) * mm});
            skLineSegment(sketch, "E1663", {"start": v(-30.76, 34.22) * mm, "end": v(-30.86, 34.35) * mm});
            skLineSegment(sketch, "E1664", {"start": v(-30.86, 34.35) * mm, "end": v(-30.97, 34.47) * mm});
            skLineSegment(sketch, "E1665", {"start": v(-30.97, 34.47) * mm, "end": v(-31.09, 34.6) * mm});
            skLineSegment(sketch, "E1666", {"start": v(-31.09, 34.6) * mm, "end": v(-31.2, 34.73) * mm});
            skLineSegment(sketch, "E1667", {"start": v(-31.2, 34.73) * mm, "end": v(-31.3, 34.85) * mm});
            skLineSegment(sketch, "E1668", {"start": v(-31.3, 34.85) * mm, "end": v(-31.42, 34.98) * mm});
            skLineSegment(sketch, "E1669", {"start": v(-31.42, 34.98) * mm, "end": v(-31.53, 35.1) * mm});
            skLineSegment(sketch, "E1670", {"start": v(-31.53, 35.1) * mm, "end": v(-31.64, 35.23) * mm});
            skLineSegment(sketch, "E1671", {"start": v(-31.64, 35.23) * mm, "end": v(-31.75, 35.36) * mm});
            skLineSegment(sketch, "E1672", {"start": v(-31.75, 35.36) * mm, "end": v(-31.86, 35.49) * mm});
            skLineSegment(sketch, "E1673", {"start": v(-31.86, 35.49) * mm, "end": v(-31.97, 35.61) * mm});
            skLineSegment(sketch, "E1674", {"start": v(-31.97, 35.61) * mm, "end": v(-32.08, 35.74) * mm});
            skLineSegment(sketch, "E1675", {"start": v(-32.08, 35.74) * mm, "end": v(-32.2, 35.87) * mm});
            skLineSegment(sketch, "E1676", {"start": v(-32.2, 35.87) * mm, "end": v(-32.34, 35.98) * mm});
            skLineSegment(sketch, "E1677", {"start": v(-32.34, 35.98) * mm, "end": v(-32.5, 36.05) * mm});
            skLineSegment(sketch, "E1678", {"start": v(-32.5, 36.05) * mm, "end": v(-32.67, 36.07) * mm});
            skLineSegment(sketch, "E1679", {"start": v(-32.67, 36.07) * mm, "end": v(-32.84, 36.05) * mm});
            skLineSegment(sketch, "E1680", {"start": v(-32.84, 36.05) * mm, "end": v(-33, 35.98) * mm});
            skLineSegment(sketch, "E1681", {"start": v(-33, 35.98) * mm, "end": v(-33.14, 35.88) * mm});
            skLineSegment(sketch, "E1682", {"start": v(-33.14, 35.88) * mm, "end": v(-33.25, 35.74) * mm});
            skLineSegment(sketch, "E1683", {"start": v(-33.25, 35.74) * mm, "end": v(-33.31, 35.58) * mm});
            skLineSegment(sketch, "E1684", {"start": v(-33.31, 35.58) * mm, "end": v(-33.33, 35.4) * mm});
            skLineSegment(sketch, "E1685", {"start": v(-33.33, 35.4) * mm, "end": v(-33.31, 35.23) * mm});
            skLineSegment(sketch, "E1686", {"start": v(-33.31, 35.23) * mm, "end": v(-33.24, 35.07) * mm});
            skLineSegment(sketch, "E1687", {"start": v(-33.24, 35.07) * mm, "end": v(-33.14, 34.94) * mm});
            skLineSegment(sketch, "E1688", {"start": v(-33.14, 34.94) * mm, "end": v(-33.03, 34.82) * mm});
            skLineSegment(sketch, "E1689", {"start": v(-33.03, 34.82) * mm, "end": v(-32.92, 34.7) * mm});
            skLineSegment(sketch, "E1690", {"start": v(-32.92, 34.7) * mm, "end": v(-32.8, 34.58) * mm});
            skLineSegment(sketch, "E1691", {"start": v(-32.8, 34.58) * mm, "end": v(-32.7, 34.45) * mm});
            skLineSegment(sketch, "E1692", {"start": v(-32.7, 34.45) * mm, "end": v(-32.58, 34.33) * mm});
            skLineSegment(sketch, "E1693", {"start": v(-32.58, 34.33) * mm, "end": v(-32.46, 34.2) * mm});
            skLineSegment(sketch, "E1694", {"start": v(-32.46, 34.2) * mm, "end": v(-32.35, 34.08) * mm});
            skLineSegment(sketch, "E1695", {"start": v(-32.35, 34.08) * mm, "end": v(-32.23, 33.96) * mm});
            skLineSegment(sketch, "E1696", {"start": v(-32.23, 33.96) * mm, "end": v(-32.12, 33.84) * mm});
            skLineSegment(sketch, "E1697", {"start": v(-32.12, 33.84) * mm, "end": v(-32, 33.71) * mm});
            skLineSegment(sketch, "E1698", {"start": v(-32, 33.71) * mm, "end": v(-31.9, 33.59) * mm});
            skLineSegment(sketch, "E1699", {"start": v(-31.9, 33.59) * mm, "end": v(-31.78, 33.47) * mm});
            skLineSegment(sketch, "E1700", {"start": v(-31.78, 33.47) * mm, "end": v(-31.7, 33.38) * mm});
            skLineSegment(sketch, "E1701", {"start": v(-31.7, 33.38) * mm, "end": v(-31.81, 33.26) * mm});
            skLineSegment(sketch, "E1702", {"start": v(-31.81, 33.26) * mm, "end": v(-31.93, 33.15) * mm});
            skLineSegment(sketch, "E1703", {"start": v(-31.93, 33.15) * mm, "end": v(-32.05, 33.03) * mm});
            skLineSegment(sketch, "E1704", {"start": v(-32.05, 33.03) * mm, "end": v(-32.17, 32.92) * mm});
            skLineSegment(sketch, "E1705", {"start": v(-32.17, 32.92) * mm, "end": v(-32.3, 32.8) * mm});
            skLineSegment(sketch, "E1706", {"start": v(-32.3, 32.8) * mm, "end": v(-32.41, 32.68) * mm});
            skLineSegment(sketch, "E1707", {"start": v(-32.41, 32.68) * mm, "end": v(-32.53, 32.57) * mm});
            skLineSegment(sketch, "E1708", {"start": v(-32.53, 32.57) * mm, "end": v(-32.65, 32.45) * mm});
            skLineSegment(sketch, "E1709", {"start": v(-32.65, 32.45) * mm, "end": v(-32.77, 32.34) * mm});
            skLineSegment(sketch, "E1710", {"start": v(-32.77, 32.34) * mm, "end": v(-32.9, 32.22) * mm});
            skLineSegment(sketch, "E1711", {"start": v(-32.9, 32.22) * mm, "end": v(-33.01, 32.1) * mm});
            skLineSegment(sketch, "E1712", {"start": v(-33.01, 32.1) * mm, "end": v(-33.07, 32.05) * mm});
            skLineSegment(sketch, "E1713", {"start": v(-33.07, 32.05) * mm, "end": v(-33.19, 32.17) * mm});
            skLineSegment(sketch, "E1714", {"start": v(-33.19, 32.17) * mm, "end": v(-33.3, 32.28) * mm});
            skLineSegment(sketch, "E1715", {"start": v(-33.3, 32.28) * mm, "end": v(-33.43, 32.4) * mm});
            skLineSegment(sketch, "E1716", {"start": v(-33.43, 32.4) * mm, "end": v(-33.55, 32.52) * mm});
            skLineSegment(sketch, "E1717", {"start": v(-33.55, 32.52) * mm, "end": v(-33.66, 32.64) * mm});
            skLineSegment(sketch, "E1718", {"start": v(-33.66, 32.64) * mm, "end": v(-33.78, 32.76) * mm});
            skLineSegment(sketch, "E1719", {"start": v(-33.78, 32.76) * mm, "end": v(-33.9, 32.88) * mm});
            skLineSegment(sketch, "E1720", {"start": v(-33.9, 32.88) * mm, "end": v(-34.02, 33) * mm});
            skLineSegment(sketch, "E1721", {"start": v(-34.02, 33) * mm, "end": v(-34.14, 33.12) * mm});
            skLineSegment(sketch, "E1722", {"start": v(-34.14, 33.12) * mm, "end": v(-34.26, 33.23) * mm});
            skLineSegment(sketch, "E1723", {"start": v(-34.26, 33.23) * mm, "end": v(-34.38, 33.35) * mm});
            skLineSegment(sketch, "E1724", {"start": v(-34.38, 33.35) * mm, "end": v(-34.5, 33.47) * mm});
            skLineSegment(sketch, "E1725", {"start": v(-34.5, 33.47) * mm, "end": v(-34.63, 33.6) * mm});
            skLineSegment(sketch, "E1726", {"start": v(-34.63, 33.6) * mm, "end": v(-34.77, 33.7) * mm});
            skLineSegment(sketch, "E1727", {"start": v(-34.77, 33.7) * mm, "end": v(-34.94, 33.75) * mm});
            skLineSegment(sketch, "E1728", {"start": v(-34.94, 33.75) * mm, "end": v(-35.07, 33.76) * mm});
            skLineSegment(sketch, "E1729", {"start": v(-35.07, 33.76) * mm, "end": v(-35.25, 33.74) * mm});
            skLineSegment(sketch, "E1730", {"start": v(-35.25, 33.74) * mm, "end": v(-35.4, 33.67) * mm});
            skLineSegment(sketch, "E1731", {"start": v(-35.4, 33.67) * mm, "end": v(-35.54, 33.56) * mm});
            skLineSegment(sketch, "E1732", {"start": v(-35.54, 33.56) * mm, "end": v(-35.64, 33.42) * mm});
            skLineSegment(sketch, "E1733", {"start": v(-35.64, 33.42) * mm, "end": v(-35.7, 33.26) * mm});
            skLineSegment(sketch, "E1734", {"start": v(-35.7, 33.26) * mm, "end": v(-35.73, 33.08) * mm});
            skLineSegment(sketch, "E1735", {"start": v(-35.73, 33.08) * mm, "end": v(-35.7, 32.91) * mm});
            skLineSegment(sketch, "E1736", {"start": v(-35.7, 32.91) * mm, "end": v(-35.63, 32.75) * mm});
            skLineSegment(sketch, "E1737", {"start": v(-35.63, 32.75) * mm, "end": v(-35.52, 32.62) * mm});
            skLineSegment(sketch, "E1738", {"start": v(-35.52, 32.62) * mm, "end": v(-35.4, 32.5) * mm});
            skLineSegment(sketch, "E1739", {"start": v(-35.4, 32.5) * mm, "end": v(-35.28, 32.4) * mm});
            skLineSegment(sketch, "E1740", {"start": v(-35.28, 32.4) * mm, "end": v(-35.15, 32.27) * mm});
            skLineSegment(sketch, "E1741", {"start": v(-35.15, 32.27) * mm, "end": v(-35.03, 32.16) * mm});
            skLineSegment(sketch, "E1742", {"start": v(-35.03, 32.16) * mm, "end": v(-34.91, 32.05) * mm});
            skLineSegment(sketch, "E1743", {"start": v(-34.91, 32.05) * mm, "end": v(-34.79, 31.93) * mm});
            skLineSegment(sketch, "E1744", {"start": v(-34.79, 31.93) * mm, "end": v(-34.67, 31.82) * mm});
            skLineSegment(sketch, "E1745", {"start": v(-34.67, 31.82) * mm, "end": v(-34.54, 31.7) * mm});
            skLineSegment(sketch, "E1746", {"start": v(-34.54, 31.7) * mm, "end": v(-34.42, 31.58) * mm});
            skLineSegment(sketch, "E1747", {"start": v(-34.42, 31.58) * mm, "end": v(-34.3, 31.47) * mm});
            skLineSegment(sketch, "E1748", {"start": v(-34.3, 31.47) * mm, "end": v(-34.18, 31.36) * mm});
            skLineSegment(sketch, "E1749", {"start": v(-34.18, 31.36) * mm, "end": v(-34.05, 31.24) * mm});
            skLineSegment(sketch, "E1750", {"start": v(-34.05, 31.24) * mm, "end": v(-33.95, 31.14) * mm});
            skLineSegment(sketch, "E1751", {"start": v(-33.95, 31.14) * mm, "end": v(-34.06, 31.02) * mm});
            skLineSegment(sketch, "E1752", {"start": v(-34.06, 31.02) * mm, "end": v(-34.17, 30.9) * mm});
            skLineSegment(sketch, "E1753", {"start": v(-34.17, 30.9) * mm, "end": v(-34.28, 30.77) * mm});
            skLineSegment(sketch, "E1754", {"start": v(-34.28, 30.77) * mm, "end": v(-34.4, 30.65) * mm});
            skLineSegment(sketch, "E1755", {"start": v(-34.4, 30.65) * mm, "end": v(-34.5, 30.52) * mm});
            skLineSegment(sketch, "E1756", {"start": v(-34.5, 30.52) * mm, "end": v(-34.62, 30.4) * mm});
            skLineSegment(sketch, "E1757", {"start": v(-34.62, 30.4) * mm, "end": v(-34.73, 30.28) * mm});
            skLineSegment(sketch, "E1758", {"start": v(-34.73, 30.28) * mm, "end": v(-34.84, 30.15) * mm});
            skLineSegment(sketch, "E1759", {"start": v(-34.84, 30.15) * mm, "end": v(-34.95, 30.03) * mm});
            skLineSegment(sketch, "E1760", {"start": v(-34.95, 30.03) * mm, "end": v(-35.06, 29.9) * mm});
            skLineSegment(sketch, "E1761", {"start": v(-35.06, 29.9) * mm, "end": v(-35.17, 29.78) * mm});
            skLineSegment(sketch, "E1762", {"start": v(-35.17, 29.78) * mm, "end": v(-35.23, 29.72) * mm});
            skLineSegment(sketch, "E1763", {"start": v(-35.23, 29.72) * mm, "end": v(-35.35, 29.83) * mm});
            skLineSegment(sketch, "E1764", {"start": v(-35.35, 29.83) * mm, "end": v(-35.48, 29.94) * mm});
            skLineSegment(sketch, "E1765", {"start": v(-35.48, 29.94) * mm, "end": v(-35.6, 30.05) * mm});
            skLineSegment(sketch, "E1766", {"start": v(-35.6, 30.05) * mm, "end": v(-35.73, 30.16) * mm});
            skLineSegment(sketch, "E1767", {"start": v(-35.73, 30.16) * mm, "end": v(-35.86, 30.27) * mm});
            skLineSegment(sketch, "E1768", {"start": v(-35.86, 30.27) * mm, "end": v(-35.99, 30.38) * mm});
            skLineSegment(sketch, "E1769", {"start": v(-35.99, 30.38) * mm, "end": v(-36.12, 30.49) * mm});
            skLineSegment(sketch, "E1770", {"start": v(-36.12, 30.49) * mm, "end": v(-36.24, 30.6) * mm});
            skLineSegment(sketch, "E1771", {"start": v(-36.24, 30.6) * mm, "end": v(-36.37, 30.7) * mm});
            skLineSegment(sketch, "E1772", {"start": v(-36.37, 30.7) * mm, "end": v(-36.5, 30.82) * mm});
            skLineSegment(sketch, "E1773", {"start": v(-36.5, 30.82) * mm, "end": v(-36.62, 30.93) * mm});
            skLineSegment(sketch, "E1774", {"start": v(-36.62, 30.93) * mm, "end": v(-36.75, 31.04) * mm});
            skLineSegment(sketch, "E1775", {"start": v(-36.75, 31.04) * mm, "end": v(-36.89, 31.15) * mm});
            skLineSegment(sketch, "E1776", {"start": v(-36.89, 31.15) * mm, "end": v(-37.04, 31.24) * mm});
            skLineSegment(sketch, "E1777", {"start": v(-37.04, 31.24) * mm, "end": v(-37.2, 31.28) * mm});
            skLineSegment(sketch, "E1778", {"start": v(-37.2, 31.28) * mm, "end": v(-37.28, 31.29) * mm});
            skLineSegment(sketch, "E1779", {"start": v(-37.28, 31.29) * mm, "end": v(-37.45, 31.27) * mm});
            skLineSegment(sketch, "E1780", {"start": v(-37.45, 31.27) * mm, "end": v(-37.61, 31.2) * mm});
            skLineSegment(sketch, "E1781", {"start": v(-37.61, 31.2) * mm, "end": v(-37.75, 31.1) * mm});
            skLineSegment(sketch, "E1782", {"start": v(-37.75, 31.1) * mm, "end": v(-37.86, 30.97) * mm});
            skLineSegment(sketch, "E1783", {"start": v(-37.86, 30.97) * mm, "end": v(-37.93, 30.8) * mm});
            skLineSegment(sketch, "E1784", {"start": v(-37.93, 30.8) * mm, "end": v(-37.95, 30.64) * mm});
            skLineSegment(sketch, "E1785", {"start": v(-37.95, 30.64) * mm, "end": v(-37.93, 30.46) * mm});
            skLineSegment(sketch, "E1786", {"start": v(-37.93, 30.46) * mm, "end": v(-37.87, 30.3) * mm});
            skLineSegment(sketch, "E1787", {"start": v(-37.87, 30.3) * mm, "end": v(-37.76, 30.16) * mm});
            skLineSegment(sketch, "E1788", {"start": v(-37.76, 30.16) * mm, "end": v(-37.64, 30.06) * mm});
            skLineSegment(sketch, "E1789", {"start": v(-37.64, 30.06) * mm, "end": v(-37.5, 29.95) * mm});
            skLineSegment(sketch, "E1790", {"start": v(-37.5, 29.95) * mm, "end": v(-37.38, 29.84) * mm});
            skLineSegment(sketch, "E1791", {"start": v(-37.38, 29.84) * mm, "end": v(-37.25, 29.74) * mm});
            skLineSegment(sketch, "E1792", {"start": v(-37.25, 29.74) * mm, "end": v(-37.12, 29.63) * mm});
            skLineSegment(sketch, "E1793", {"start": v(-37.12, 29.63) * mm, "end": v(-36.99, 29.53) * mm});
            skLineSegment(sketch, "E1794", {"start": v(-36.99, 29.53) * mm, "end": v(-36.86, 29.42) * mm});
            skLineSegment(sketch, "E1795", {"start": v(-36.86, 29.42) * mm, "end": v(-36.73, 29.32) * mm});
            skLineSegment(sketch, "E1796", {"start": v(-36.73, 29.32) * mm, "end": v(-36.6, 29.2) * mm});
            skLineSegment(sketch, "E1797", {"start": v(-36.6, 29.2) * mm, "end": v(-36.47, 29.1) * mm});
            skLineSegment(sketch, "E1798", {"start": v(-36.47, 29.1) * mm, "end": v(-36.34, 29) * mm});
            skLineSegment(sketch, "E1799", {"start": v(-36.34, 29) * mm, "end": v(-36.2, 28.89) * mm});
            skLineSegment(sketch, "E1800", {"start": v(-36.2, 28.89) * mm, "end": v(-36.08, 28.78) * mm});
            skLineSegment(sketch, "E1801", {"start": v(-36.08, 28.78) * mm, "end": v(-36.04, 28.75) * mm});
            skLineSegment(sketch, "E1802", {"start": v(-36.04, 28.75) * mm, "end": v(-36.14, 28.62) * mm});
            skLineSegment(sketch, "E1803", {"start": v(-36.14, 28.62) * mm, "end": v(-36.24, 28.49) * mm});
            skLineSegment(sketch, "E1804", {"start": v(-36.24, 28.49) * mm, "end": v(-36.35, 28.36) * mm});
            skLineSegment(sketch, "E1805", {"start": v(-36.35, 28.36) * mm, "end": v(-36.45, 28.23) * mm});
            skLineSegment(sketch, "E1806", {"start": v(-36.45, 28.23) * mm, "end": v(-36.55, 28.1) * mm});
            skLineSegment(sketch, "E1807", {"start": v(-36.55, 28.1) * mm, "end": v(-36.65, 27.97) * mm});
            skLineSegment(sketch, "E1808", {"start": v(-36.65, 27.97) * mm, "end": v(-36.76, 27.83) * mm});
            skLineSegment(sketch, "E1809", {"start": v(-36.76, 27.83) * mm, "end": v(-36.86, 27.7) * mm});
            skLineSegment(sketch, "E1810", {"start": v(-36.86, 27.7) * mm, "end": v(-36.96, 27.57) * mm});
            skLineSegment(sketch, "E1811", {"start": v(-36.96, 27.57) * mm, "end": v(-37.06, 27.44) * mm});
            skLineSegment(sketch, "E1812", {"start": v(-37.06, 27.44) * mm, "end": v(-37.17, 27.3) * mm});
            skLineSegment(sketch, "E1813", {"start": v(-37.17, 27.3) * mm, "end": v(-37.22, 27.25) * mm});
            skLineSegment(sketch, "E1814", {"start": v(-37.22, 27.25) * mm, "end": v(-37.35, 27.35) * mm});
            skLineSegment(sketch, "E1815", {"start": v(-37.35, 27.35) * mm, "end": v(-37.48, 27.45) * mm});
            skLineSegment(sketch, "E1816", {"start": v(-37.48, 27.45) * mm, "end": v(-37.62, 27.55) * mm});
            skLineSegment(sketch, "E1817", {"start": v(-37.62, 27.55) * mm, "end": v(-37.75, 27.65) * mm});
            skLineSegment(sketch, "E1818", {"start": v(-37.75, 27.65) * mm, "end": v(-37.89, 27.75) * mm});
            skLineSegment(sketch, "E1819", {"start": v(-37.89, 27.75) * mm, "end": v(-38.02, 27.85) * mm});
            skLineSegment(sketch, "E1820", {"start": v(-38.02, 27.85) * mm, "end": v(-38.16, 27.95) * mm});
            skLineSegment(sketch, "E1821", {"start": v(-38.16, 27.95) * mm, "end": v(-38.29, 28.05) * mm});
            skLineSegment(sketch, "E1822", {"start": v(-38.29, 28.05) * mm, "end": v(-38.43, 28.15) * mm});
            skLineSegment(sketch, "E1823", {"start": v(-38.43, 28.15) * mm, "end": v(-38.56, 28.25) * mm});
            skLineSegment(sketch, "E1824", {"start": v(-38.56, 28.25) * mm, "end": v(-38.7, 28.35) * mm});
            skLineSegment(sketch, "E1825", {"start": v(-38.7, 28.35) * mm, "end": v(-38.83, 28.45) * mm});
            skLineSegment(sketch, "E1826", {"start": v(-38.83, 28.45) * mm, "end": v(-38.97, 28.56) * mm});
            skLineSegment(sketch, "E1827", {"start": v(-38.97, 28.56) * mm, "end": v(-39.13, 28.63) * mm});
            skLineSegment(sketch, "E1828", {"start": v(-39.13, 28.63) * mm, "end": v(-39.3, 28.67) * mm});
            skLineSegment(sketch, "E1829", {"start": v(-39.3, 28.67) * mm, "end": v(-39.34, 28.67) * mm});
            skLineSegment(sketch, "E1830", {"start": v(-39.34, 28.67) * mm, "end": v(-39.5, 28.65) * mm});
            skLineSegment(sketch, "E1831", {"start": v(-39.5, 28.65) * mm, "end": v(-39.67, 28.58) * mm});
            skLineSegment(sketch, "E1832", {"start": v(-39.67, 28.58) * mm, "end": v(-39.8, 28.47) * mm});
            skLineSegment(sketch, "E1833", {"start": v(-39.8, 28.47) * mm, "end": v(-39.91, 28.34) * mm});
            skLineSegment(sketch, "E1834", {"start": v(-39.91, 28.34) * mm, "end": v(-39.98, 28.18) * mm});
            skLineSegment(sketch, "E1835", {"start": v(-39.98, 28.18) * mm, "end": v(-40, 28) * mm});
            skLineSegment(sketch, "E1836", {"start": v(-40, 28) * mm, "end": v(-39.98, 27.83) * mm});
            skLineSegment(sketch, "E1837", {"start": v(-39.98, 27.83) * mm, "end": v(-39.9, 27.67) * mm});
            skLineSegment(sketch, "E1838", {"start": v(-39.9, 27.67) * mm, "end": v(-39.8, 27.54) * mm});
            skLineSegment(sketch, "E1839", {"start": v(-39.8, 27.54) * mm, "end": v(-39.66, 27.43) * mm});
            skLineSegment(sketch, "E1840", {"start": v(-39.66, 27.43) * mm, "end": v(-39.53, 27.33) * mm});
            skLineSegment(sketch, "E1841", {"start": v(-39.53, 27.33) * mm, "end": v(-39.4, 27.23) * mm});
            skLineSegment(sketch, "E1842", {"start": v(-39.4, 27.23) * mm, "end": v(-39.25, 27.14) * mm});
            skLineSegment(sketch, "E1843", {"start": v(-39.25, 27.14) * mm, "end": v(-39.12, 27.04) * mm});
            skLineSegment(sketch, "E1844", {"start": v(-39.12, 27.04) * mm, "end": v(-38.98, 26.94) * mm});
            skLineSegment(sketch, "E1845", {"start": v(-38.98, 26.94) * mm, "end": v(-38.84, 26.85) * mm});
            skLineSegment(sketch, "E1846", {"start": v(-38.84, 26.85) * mm, "end": v(-38.7, 26.75) * mm});
            skLineSegment(sketch, "E1847", {"start": v(-38.7, 26.75) * mm, "end": v(-38.57, 26.65) * mm});
            skLineSegment(sketch, "E1848", {"start": v(-38.57, 26.65) * mm, "end": v(-38.43, 26.55) * mm});
            skLineSegment(sketch, "E1849", {"start": v(-38.43, 26.55) * mm, "end": v(-38.3, 26.46) * mm});
            skLineSegment(sketch, "E1850", {"start": v(-38.3, 26.46) * mm, "end": v(-38.16, 26.36) * mm});
            skLineSegment(sketch, "E1851", {"start": v(-38.16, 26.36) * mm, "end": v(-38.02, 26.26) * mm});
            skLineSegment(sketch, "E1852", {"start": v(-38.02, 26.26) * mm, "end": v(-37.96, 26.22) * mm});
            skLineSegment(sketch, "E1853", {"start": v(-37.96, 26.22) * mm, "end": v(-38.05, 26.09) * mm});
            skLineSegment(sketch, "E1854", {"start": v(-38.05, 26.09) * mm, "end": v(-38.15, 25.95) * mm});
            skLineSegment(sketch, "E1855", {"start": v(-38.15, 25.95) * mm, "end": v(-38.24, 25.8) * mm});
            skLineSegment(sketch, "E1856", {"start": v(-38.24, 25.8) * mm, "end": v(-38.33, 25.67) * mm});
            skLineSegment(sketch, "E1857", {"start": v(-38.33, 25.67) * mm, "end": v(-38.42, 25.53) * mm});
            skLineSegment(sketch, "E1858", {"start": v(-38.42, 25.53) * mm, "end": v(-38.52, 25.4) * mm});
            skLineSegment(sketch, "E1859", {"start": v(-38.52, 25.4) * mm, "end": v(-38.61, 25.26) * mm});
            skLineSegment(sketch, "E1860", {"start": v(-38.61, 25.26) * mm, "end": v(-38.7, 25.12) * mm});
            skLineSegment(sketch, "E1861", {"start": v(-38.7, 25.12) * mm, "end": v(-38.8, 24.98) * mm});
            skLineSegment(sketch, "E1862", {"start": v(-38.8, 24.98) * mm, "end": v(-38.89, 24.84) * mm});
            skLineSegment(sketch, "E1863", {"start": v(-38.89, 24.84) * mm, "end": v(-38.98, 24.7) * mm});
            skLineSegment(sketch, "E1864", {"start": v(-38.98, 24.7) * mm, "end": v(-39.03, 24.64) * mm});
            skLineSegment(sketch, "E1865", {"start": v(-39.03, 24.64) * mm, "end": v(-39.17, 24.73) * mm});
            skLineSegment(sketch, "E1866", {"start": v(-39.17, 24.73) * mm, "end": v(-39.3, 24.82) * mm});
            skLineSegment(sketch, "E1867", {"start": v(-39.3, 24.82) * mm, "end": v(-39.45, 24.91) * mm});
            skLineSegment(sketch, "E1868", {"start": v(-39.45, 24.91) * mm, "end": v(-39.6, 25) * mm});
            skLineSegment(sketch, "E1869", {"start": v(-39.6, 25) * mm, "end": v(-39.73, 25.1) * mm});
            skLineSegment(sketch, "E1870", {"start": v(-39.73, 25.1) * mm, "end": v(-39.87, 25.18) * mm});
            skLineSegment(sketch, "E1871", {"start": v(-39.87, 25.18) * mm, "end": v(-40.01, 25.27) * mm});
            skLineSegment(sketch, "E1872", {"start": v(-40.01, 25.27) * mm, "end": v(-40.15, 25.36) * mm});
            skLineSegment(sketch, "E1873", {"start": v(-40.15, 25.36) * mm, "end": v(-40.3, 25.46) * mm});
            skLineSegment(sketch, "E1874", {"start": v(-40.3, 25.46) * mm, "end": v(-40.44, 25.55) * mm});
            skLineSegment(sketch, "E1875", {"start": v(-40.44, 25.55) * mm, "end": v(-40.58, 25.64) * mm});
            skLineSegment(sketch, "E1876", {"start": v(-40.58, 25.64) * mm, "end": v(-40.72, 25.73) * mm});
            skLineSegment(sketch, "E1877", {"start": v(-40.72, 25.73) * mm, "end": v(-40.87, 25.83) * mm});
            skLineSegment(sketch, "E1878", {"start": v(-40.87, 25.83) * mm, "end": v(-41.03, 25.9) * mm});
            skLineSegment(sketch, "E1879", {"start": v(-41.03, 25.9) * mm, "end": v(-41.2, 25.91) * mm});
            skLineSegment(sketch, "E1880", {"start": v(-41.2, 25.91) * mm, "end": v(-41.38, 25.89) * mm});
            skLineSegment(sketch, "E1881", {"start": v(-41.38, 25.89) * mm, "end": v(-41.54, 25.82) * mm});
            skLineSegment(sketch, "E1882", {"start": v(-41.54, 25.82) * mm, "end": v(-41.67, 25.7) * mm});
            skLineSegment(sketch, "E1883", {"start": v(-41.67, 25.7) * mm, "end": v(-41.78, 25.57) * mm});
            skLineSegment(sketch, "E1884", {"start": v(-41.78, 25.57) * mm, "end": v(-41.84, 25.4) * mm});
            skLineSegment(sketch, "E1885", {"start": v(-41.84, 25.4) * mm, "end": v(-41.86, 25.24) * mm});
            skLineSegment(sketch, "E1886", {"start": v(-41.86, 25.24) * mm, "end": v(-41.83, 25.06) * mm});
            skLineSegment(sketch, "E1887", {"start": v(-41.83, 25.06) * mm, "end": v(-41.76, 24.9) * mm});
            skLineSegment(sketch, "E1888", {"start": v(-41.76, 24.9) * mm, "end": v(-41.65, 24.77) * mm});
            skLineSegment(sketch, "E1889", {"start": v(-41.65, 24.77) * mm, "end": v(-41.52, 24.67) * mm});
            skLineSegment(sketch, "E1890", {"start": v(-41.52, 24.67) * mm, "end": v(-41.38, 24.58) * mm});
            skLineSegment(sketch, "E1891", {"start": v(-41.38, 24.58) * mm, "end": v(-41.24, 24.5) * mm});
            skLineSegment(sketch, "E1892", {"start": v(-41.24, 24.5) * mm, "end": v(-41.1, 24.41) * mm});
            skLineSegment(sketch, "E1893", {"start": v(-41.1, 24.41) * mm, "end": v(-40.95, 24.33) * mm});
            skLineSegment(sketch, "E1894", {"start": v(-40.95, 24.33) * mm, "end": v(-40.8, 24.24) * mm});
            skLineSegment(sketch, "E1895", {"start": v(-40.8, 24.24) * mm, "end": v(-40.66, 24.15) * mm});
            skLineSegment(sketch, "E1896", {"start": v(-40.66, 24.15) * mm, "end": v(-40.52, 24.07) * mm});
            skLineSegment(sketch, "E1897", {"start": v(-40.52, 24.07) * mm, "end": v(-40.38, 23.98) * mm});
            skLineSegment(sketch, "E1898", {"start": v(-40.38, 23.98) * mm, "end": v(-40.23, 23.9) * mm});
            skLineSegment(sketch, "E1899", {"start": v(-40.23, 23.9) * mm, "end": v(-40.1, 23.8) * mm});
            skLineSegment(sketch, "E1900", {"start": v(-40.1, 23.8) * mm, "end": v(-39.94, 23.72) * mm});
            skLineSegment(sketch, "E1901", {"start": v(-39.94, 23.72) * mm, "end": v(-39.8, 23.63) * mm});
            skLineSegment(sketch, "E1902", {"start": v(-39.8, 23.63) * mm, "end": v(-39.7, 23.57) * mm});
            skLineSegment(sketch, "E1903", {"start": v(-39.7, 23.57) * mm, "end": v(-39.78, 23.42) * mm});
            skLineSegment(sketch, "E1904", {"start": v(-39.78, 23.42) * mm, "end": v(-39.86, 23.28) * mm});
            skLineSegment(sketch, "E1905", {"start": v(-39.86, 23.28) * mm, "end": v(-39.95, 23.13) * mm});
            skLineSegment(sketch, "E1906", {"start": v(-39.95, 23.13) * mm, "end": v(-40.03, 23) * mm});
            skLineSegment(sketch, "E1907", {"start": v(-40.03, 23) * mm, "end": v(-40.11, 22.85) * mm});
            skLineSegment(sketch, "E1908", {"start": v(-40.11, 22.85) * mm, "end": v(-40.2, 22.7) * mm});
            skLineSegment(sketch, "E1909", {"start": v(-40.2, 22.7) * mm, "end": v(-40.28, 22.56) * mm});
            skLineSegment(sketch, "E1910", {"start": v(-40.28, 22.56) * mm, "end": v(-40.36, 22.41) * mm});
            skLineSegment(sketch, "E1911", {"start": v(-40.36, 22.41) * mm, "end": v(-40.45, 22.27) * mm});
            skLineSegment(sketch, "E1912", {"start": v(-40.45, 22.27) * mm, "end": v(-40.53, 22.13) * mm});
            skLineSegment(sketch, "E1913", {"start": v(-40.53, 22.13) * mm, "end": v(-40.61, 21.98) * mm});
            skLineSegment(sketch, "E1914", {"start": v(-40.61, 21.98) * mm, "end": v(-40.65, 21.91) * mm});
            skLineSegment(sketch, "E1915", {"start": v(-40.65, 21.91) * mm, "end": v(-40.8, 22) * mm});
            skLineSegment(sketch, "E1916", {"start": v(-40.8, 22) * mm, "end": v(-40.95, 22.07) * mm});
            skLineSegment(sketch, "E1917", {"start": v(-40.95, 22.07) * mm, "end": v(-41.1, 22.15) * mm});
            skLineSegment(sketch, "E1918", {"start": v(-41.1, 22.15) * mm, "end": v(-41.24, 22.23) * mm});
            skLineSegment(sketch, "E1919", {"start": v(-41.24, 22.23) * mm, "end": v(-41.39, 22.31) * mm});
            skLineSegment(sketch, "E1920", {"start": v(-41.39, 22.31) * mm, "end": v(-41.54, 22.4) * mm});
            skLineSegment(sketch, "E1921", {"start": v(-41.54, 22.4) * mm, "end": v(-41.68, 22.48) * mm});
            skLineSegment(sketch, "E1922", {"start": v(-41.68, 22.48) * mm, "end": v(-41.83, 22.56) * mm});
            skLineSegment(sketch, "E1923", {"start": v(-41.83, 22.56) * mm, "end": v(-41.98, 22.64) * mm});
            skLineSegment(sketch, "E1924", {"start": v(-41.98, 22.64) * mm, "end": v(-42.12, 22.72) * mm});
            skLineSegment(sketch, "E1925", {"start": v(-42.12, 22.72) * mm, "end": v(-42.27, 22.8) * mm});
            skLineSegment(sketch, "E1926", {"start": v(-42.27, 22.8) * mm, "end": v(-42.42, 22.88) * mm});
            skLineSegment(sketch, "E1927", {"start": v(-42.42, 22.88) * mm, "end": v(-42.58, 22.97) * mm});
            skLineSegment(sketch, "E1928", {"start": v(-42.58, 22.97) * mm, "end": v(-42.74, 23.02) * mm});
            skLineSegment(sketch, "E1929", {"start": v(-42.74, 23.02) * mm, "end": v(-42.85, 23.03) * mm});
            skLineSegment(sketch, "E1930", {"start": v(-42.85, 23.03) * mm, "end": v(-43.02, 23.01) * mm});
            skLineSegment(sketch, "E1931", {"start": v(-43.02, 23.01) * mm, "end": v(-43.18, 22.95) * mm});
            skLineSegment(sketch, "E1932", {"start": v(-43.18, 22.95) * mm, "end": v(-43.32, 22.85) * mm});
            skLineSegment(sketch, "E1933", {"start": v(-43.32, 22.85) * mm, "end": v(-43.43, 22.7) * mm});
            skLineSegment(sketch, "E1934", {"start": v(-43.43, 22.7) * mm, "end": v(-43.5, 22.55) * mm});
            skLineSegment(sketch, "E1935", {"start": v(-43.5, 22.55) * mm, "end": v(-43.52, 22.38) * mm});
            skLineSegment(sketch, "E1936", {"start": v(-43.52, 22.38) * mm, "end": v(-43.5, 22.2) * mm});
            skLineSegment(sketch, "E1937", {"start": v(-43.5, 22.2) * mm, "end": v(-43.44, 22.05) * mm});
            skLineSegment(sketch, "E1938", {"start": v(-43.44, 22.05) * mm, "end": v(-43.33, 21.9) * mm});
            skLineSegment(sketch, "E1939", {"start": v(-43.33, 21.9) * mm, "end": v(-43.2, 21.8) * mm});
            skLineSegment(sketch, "E1940", {"start": v(-43.2, 21.8) * mm, "end": v(-43.04, 21.72) * mm});
            skLineSegment(sketch, "E1941", {"start": v(-43.04, 21.72) * mm, "end": v(-42.9, 21.64) * mm});
            skLineSegment(sketch, "E1942", {"start": v(-42.9, 21.64) * mm, "end": v(-42.74, 21.56) * mm});
            skLineSegment(sketch, "E1943", {"start": v(-42.74, 21.56) * mm, "end": v(-42.6, 21.49) * mm});
            skLineSegment(sketch, "E1944", {"start": v(-42.6, 21.49) * mm, "end": v(-42.44, 21.4) * mm});
            skLineSegment(sketch, "E1945", {"start": v(-42.44, 21.4) * mm, "end": v(-42.3, 21.33) * mm});
            skLineSegment(sketch, "E1946", {"start": v(-42.3, 21.33) * mm, "end": v(-42.14, 21.26) * mm});
            skLineSegment(sketch, "E1947", {"start": v(-42.14, 21.26) * mm, "end": v(-42, 21.18) * mm});
            skLineSegment(sketch, "E1948", {"start": v(-42, 21.18) * mm, "end": v(-41.85, 21.1) * mm});
            skLineSegment(sketch, "E1949", {"start": v(-41.85, 21.1) * mm, "end": v(-41.7, 21.03) * mm});
            skLineSegment(sketch, "E1950", {"start": v(-41.7, 21.03) * mm, "end": v(-41.55, 20.95) * mm});
            skLineSegment(sketch, "E1951", {"start": v(-41.55, 20.95) * mm, "end": v(-41.4, 20.87) * mm});
            skLineSegment(sketch, "E1952", {"start": v(-41.4, 20.87) * mm, "end": v(-41.25, 20.8) * mm});
            skLineSegment(sketch, "E1953", {"start": v(-41.25, 20.8) * mm, "end": v(-41.32, 20.65) * mm});
            skLineSegment(sketch, "E1954", {"start": v(-41.32, 20.65) * mm, "end": v(-41.4, 20.5) * mm});
            skLineSegment(sketch, "E1955", {"start": v(-41.4, 20.5) * mm, "end": v(-41.47, 20.35) * mm});
            skLineSegment(sketch, "E1956", {"start": v(-41.47, 20.35) * mm, "end": v(-41.54, 20.2) * mm});
            skLineSegment(sketch, "E1957", {"start": v(-41.54, 20.2) * mm, "end": v(-41.61, 20.05) * mm});
            skLineSegment(sketch, "E1958", {"start": v(-41.61, 20.05) * mm, "end": v(-41.68, 19.9) * mm});
            skLineSegment(sketch, "E1959", {"start": v(-41.68, 19.9) * mm, "end": v(-41.76, 19.75) * mm});
            skLineSegment(sketch, "E1960", {"start": v(-41.76, 19.75) * mm, "end": v(-41.83, 19.6) * mm});
            skLineSegment(sketch, "E1961", {"start": v(-41.83, 19.6) * mm, "end": v(-41.9, 19.45) * mm});
            skLineSegment(sketch, "E1962", {"start": v(-41.9, 19.45) * mm, "end": v(-41.98, 19.3) * mm});
            skLineSegment(sketch, "E1963", {"start": v(-41.98, 19.3) * mm, "end": v(-42.05, 19.15) * mm});
            skLineSegment(sketch, "E1964", {"start": v(-42.05, 19.15) * mm, "end": v(-42.08, 19.08) * mm});
            skLineSegment(sketch, "E1965", {"start": v(-42.08, 19.08) * mm, "end": v(-42.24, 19.15) * mm});
            skLineSegment(sketch, "E1966", {"start": v(-42.24, 19.15) * mm, "end": v(-42.39, 19.22) * mm});
            skLineSegment(sketch, "E1967", {"start": v(-42.39, 19.22) * mm, "end": v(-42.54, 19.29) * mm});
            skLineSegment(sketch, "E1968", {"start": v(-42.54, 19.29) * mm, "end": v(-42.7, 19.36) * mm});
            skLineSegment(sketch, "E1969", {"start": v(-42.7, 19.36) * mm, "end": v(-42.84, 19.43) * mm});
            skLineSegment(sketch, "E1970", {"start": v(-42.84, 19.43) * mm, "end": v(-43, 19.5) * mm});
            skLineSegment(sketch, "E1971", {"start": v(-43, 19.5) * mm, "end": v(-43.15, 19.57) * mm});
            skLineSegment(sketch, "E1972", {"start": v(-43.15, 19.57) * mm, "end": v(-43.3, 19.64) * mm});
            skLineSegment(sketch, "E1973", {"start": v(-43.3, 19.64) * mm, "end": v(-43.46, 19.71) * mm});
            skLineSegment(sketch, "E1974", {"start": v(-43.46, 19.71) * mm, "end": v(-43.6, 19.78) * mm});
            skLineSegment(sketch, "E1975", {"start": v(-43.6, 19.78) * mm, "end": v(-43.76, 19.85) * mm});
            skLineSegment(sketch, "E1976", {"start": v(-43.76, 19.85) * mm, "end": v(-43.91, 19.92) * mm});
            skLineSegment(sketch, "E1977", {"start": v(-43.91, 19.92) * mm, "end": v(-44.08, 20) * mm});
            skLineSegment(sketch, "E1978", {"start": v(-44.08, 20) * mm, "end": v(-44.25, 20.04) * mm});
            skLineSegment(sketch, "E1979", {"start": v(-44.25, 20.04) * mm, "end": v(-44.32, 20.04) * mm});
            skLineSegment(sketch, "E1980", {"start": v(-44.32, 20.04) * mm, "end": v(-44.49, 20.02) * mm});
            skLineSegment(sketch, "E1981", {"start": v(-44.49, 20.02) * mm, "end": v(-44.65, 19.95) * mm});
            skLineSegment(sketch, "E1982", {"start": v(-44.65, 19.95) * mm, "end": v(-44.79, 19.85) * mm});
            skLineSegment(sketch, "E1983", {"start": v(-44.79, 19.85) * mm, "end": v(-44.9, 19.71) * mm});
            skLineSegment(sketch, "E1984", {"start": v(-44.9, 19.71) * mm, "end": v(-44.96, 19.55) * mm});
            skLineSegment(sketch, "E1985", {"start": v(-44.96, 19.55) * mm, "end": v(-44.98, 19.38) * mm});
            skLineSegment(sketch, "E1986", {"start": v(-44.98, 19.38) * mm, "end": v(-44.96, 19.2) * mm});
            skLineSegment(sketch, "E1987", {"start": v(-44.96, 19.2) * mm, "end": v(-44.9, 19.05) * mm});
            skLineSegment(sketch, "E1988", {"start": v(-44.9, 19.05) * mm, "end": v(-44.78, 18.9) * mm});
            skLineSegment(sketch, "E1989", {"start": v(-44.78, 18.9) * mm, "end": v(-44.65, 18.8) * mm});
            skLineSegment(sketch, "E1990", {"start": v(-44.65, 18.8) * mm, "end": v(-44.5, 18.74) * mm});
            skLineSegment(sketch, "E1991", {"start": v(-44.5, 18.74) * mm, "end": v(-44.34, 18.67) * mm});
            skLineSegment(sketch, "E1992", {"start": v(-44.34, 18.67) * mm, "end": v(-44.19, 18.6) * mm});
            skLineSegment(sketch, "E1993", {"start": v(-44.19, 18.6) * mm, "end": v(-44.03, 18.54) * mm});
            skLineSegment(sketch, "E1994", {"start": v(-44.03, 18.54) * mm, "end": v(-43.88, 18.47) * mm});
            skLineSegment(sketch, "E1995", {"start": v(-43.88, 18.47) * mm, "end": v(-43.72, 18.4) * mm});
            skLineSegment(sketch, "E1996", {"start": v(-43.72, 18.4) * mm, "end": v(-43.57, 18.34) * mm});
            skLineSegment(sketch, "E1997", {"start": v(-43.57, 18.34) * mm, "end": v(-43.42, 18.27) * mm});
            skLineSegment(sketch, "E1998", {"start": v(-43.42, 18.27) * mm, "end": v(-43.26, 18.2) * mm});
            skLineSegment(sketch, "E1999", {"start": v(-43.26, 18.2) * mm, "end": v(-43.1, 18.14) * mm});
            skLineSegment(sketch, "E2000", {"start": v(-43.1, 18.14) * mm, "end": v(-42.95, 18.07) * mm});
            skLineSegment(sketch, "E2001", {"start": v(-42.95, 18.07) * mm, "end": v(-42.8, 18) * mm});
            skLineSegment(sketch, "E2002", {"start": v(-42.8, 18) * mm, "end": v(-42.64, 17.94) * mm});
            skLineSegment(sketch, "E2003", {"start": v(-42.64, 17.94) * mm, "end": v(-42.6, 17.92) * mm});
            skLineSegment(sketch, "E2004", {"start": v(-42.6, 17.92) * mm, "end": v(-42.66, 17.77) * mm});
            skLineSegment(sketch, "E2005", {"start": v(-42.66, 17.77) * mm, "end": v(-42.72, 17.61) * mm});
            skLineSegment(sketch, "E2006", {"start": v(-42.72, 17.61) * mm, "end": v(-42.79, 17.46) * mm});
            skLineSegment(sketch, "E2007", {"start": v(-42.79, 17.46) * mm, "end": v(-42.85, 17.3) * mm});
            skLineSegment(sketch, "E2008", {"start": v(-42.85, 17.3) * mm, "end": v(-42.91, 17.15) * mm});
            skLineSegment(sketch, "E2009", {"start": v(-42.91, 17.15) * mm, "end": v(-42.97, 17) * mm});
            skLineSegment(sketch, "E2010", {"start": v(-42.97, 17) * mm, "end": v(-43.04, 16.84) * mm});
            skLineSegment(sketch, "E2011", {"start": v(-43.04, 16.84) * mm, "end": v(-43.1, 16.69) * mm});
            skLineSegment(sketch, "E2012", {"start": v(-43.1, 16.69) * mm, "end": v(-43.16, 16.53) * mm});
            skLineSegment(sketch, "E2013", {"start": v(-43.16, 16.53) * mm, "end": v(-43.22, 16.38) * mm});
            skLineSegment(sketch, "E2014", {"start": v(-43.22, 16.38) * mm, "end": v(-43.28, 16.23) * mm});
            skLineSegment(sketch, "E2015", {"start": v(-43.28, 16.23) * mm, "end": v(-43.31, 16.15) * mm});
            skLineSegment(sketch, "E2016", {"start": v(-43.31, 16.15) * mm, "end": v(-43.47, 16.2) * mm});
            skLineSegment(sketch, "E2017", {"start": v(-43.47, 16.2) * mm, "end": v(-43.63, 16.27) * mm});
            skLineSegment(sketch, "E2018", {"start": v(-43.63, 16.27) * mm, "end": v(-43.79, 16.33) * mm});
            skLineSegment(sketch, "E2019", {"start": v(-43.79, 16.33) * mm, "end": v(-43.94, 16.39) * mm});
            skLineSegment(sketch, "E2020", {"start": v(-43.94, 16.39) * mm, "end": v(-44.1, 16.45) * mm});
            skLineSegment(sketch, "E2021", {"start": v(-44.1, 16.45) * mm, "end": v(-44.26, 16.5) * mm});
            skLineSegment(sketch, "E2022", {"start": v(-44.26, 16.5) * mm, "end": v(-44.41, 16.57) * mm});
            skLineSegment(sketch, "E2023", {"start": v(-44.41, 16.57) * mm, "end": v(-44.57, 16.63) * mm});
            skLineSegment(sketch, "E2024", {"start": v(-44.57, 16.63) * mm, "end": v(-44.73, 16.69) * mm});
            skLineSegment(sketch, "E2025", {"start": v(-44.73, 16.69) * mm, "end": v(-44.88, 16.75) * mm});
            skLineSegment(sketch, "E2026", {"start": v(-44.88, 16.75) * mm, "end": v(-45.04, 16.8) * mm});
            skLineSegment(sketch, "E2027", {"start": v(-45.04, 16.8) * mm, "end": v(-45.2, 16.87) * mm});
            skLineSegment(sketch, "E2028", {"start": v(-45.2, 16.87) * mm, "end": v(-45.37, 16.93) * mm});
            skLineSegment(sketch, "E2029", {"start": v(-45.37, 16.93) * mm, "end": v(-45.54, 16.96) * mm});
            skLineSegment(sketch, "E2030", {"start": v(-45.54, 16.96) * mm, "end": v(-45.57, 16.96) * mm});
            skLineSegment(sketch, "E2031", {"start": v(-45.57, 16.96) * mm, "end": v(-45.74, 16.93) * mm});
            skLineSegment(sketch, "E2032", {"start": v(-45.74, 16.93) * mm, "end": v(-45.9, 16.86) * mm});
            skLineSegment(sketch, "E2033", {"start": v(-45.9, 16.86) * mm, "end": v(-46.04, 16.76) * mm});
            skLineSegment(sketch, "E2034", {"start": v(-46.04, 16.76) * mm, "end": v(-46.14, 16.62) * mm});
            skLineSegment(sketch, "E2035", {"start": v(-46.14, 16.62) * mm, "end": v(-46.2, 16.46) * mm});
            skLineSegment(sketch, "E2036", {"start": v(-46.2, 16.46) * mm, "end": v(-46.23, 16.28) * mm});
            skLineSegment(sketch, "E2037", {"start": v(-46.23, 16.28) * mm, "end": v(-46.2, 16.11) * mm});
            skLineSegment(sketch, "E2038", {"start": v(-46.2, 16.11) * mm, "end": v(-46.13, 15.95) * mm});
            skLineSegment(sketch, "E2039", {"start": v(-46.13, 15.95) * mm, "end": v(-46.02, 15.82) * mm});
            skLineSegment(sketch, "E2040", {"start": v(-46.02, 15.82) * mm, "end": v(-45.88, 15.72) * mm});
            skLineSegment(sketch, "E2041", {"start": v(-45.88, 15.72) * mm, "end": v(-45.72, 15.65) * mm});
            skLineSegment(sketch, "E2042", {"start": v(-45.72, 15.65) * mm, "end": v(-45.56, 15.6) * mm});
            skLineSegment(sketch, "E2043", {"start": v(-45.56, 15.6) * mm, "end": v(-45.4, 15.54) * mm});
            skLineSegment(sketch, "E2044", {"start": v(-45.4, 15.54) * mm, "end": v(-45.24, 15.48) * mm});
            skLineSegment(sketch, "E2045", {"start": v(-45.24, 15.48) * mm, "end": v(-45.09, 15.43) * mm});
            skLineSegment(sketch, "E2046", {"start": v(-45.09, 15.43) * mm, "end": v(-44.93, 15.37) * mm});
            skLineSegment(sketch, "E2047", {"start": v(-44.93, 15.37) * mm, "end": v(-44.77, 15.32) * mm});
            skLineSegment(sketch, "E2048", {"start": v(-44.77, 15.32) * mm, "end": v(-44.6, 15.26) * mm});
            skLineSegment(sketch, "E2049", {"start": v(-44.6, 15.26) * mm, "end": v(-44.45, 15.2) * mm});
            skLineSegment(sketch, "E2050", {"start": v(-44.45, 15.2) * mm, "end": v(-44.3, 15.15) * mm});
            skLineSegment(sketch, "E2051", {"start": v(-44.3, 15.15) * mm, "end": v(-44.13, 15.1) * mm});
            skLineSegment(sketch, "E2052", {"start": v(-44.13, 15.1) * mm, "end": v(-43.98, 15.04) * mm});
            skLineSegment(sketch, "E2053", {"start": v(-43.98, 15.04) * mm, "end": v(-43.82, 14.99) * mm});
            skLineSegment(sketch, "E2054", {"start": v(-43.82, 14.99) * mm, "end": v(-43.75, 14.96) * mm});
            skLineSegment(sketch, "E2055", {"start": v(-43.75, 14.96) * mm, "end": v(-43.8, 14.8) * mm});
            skLineSegment(sketch, "E2056", {"start": v(-43.8, 14.8) * mm, "end": v(-43.85, 14.65) * mm});
            skLineSegment(sketch, "E2057", {"start": v(-43.85, 14.65) * mm, "end": v(-43.9, 14.49) * mm});
            skLineSegment(sketch, "E2058", {"start": v(-43.9, 14.49) * mm, "end": v(-43.95, 14.33) * mm});
            skLineSegment(sketch, "E2059", {"start": v(-43.95, 14.33) * mm, "end": v(-44, 14.17) * mm});
            skLineSegment(sketch, "E2060", {"start": v(-44, 14.17) * mm, "end": v(-44.06, 14.01) * mm});
            skLineSegment(sketch, "E2061", {"start": v(-44.06, 14.01) * mm, "end": v(-44.1, 13.85) * mm});
            skLineSegment(sketch, "E2062", {"start": v(-44.1, 13.85) * mm, "end": v(-44.16, 13.7) * mm});
            skLineSegment(sketch, "E2063", {"start": v(-44.16, 13.7) * mm, "end": v(-44.21, 13.54) * mm});
            skLineSegment(sketch, "E2064", {"start": v(-44.21, 13.54) * mm, "end": v(-44.26, 13.38) * mm});
            skLineSegment(sketch, "E2065", {"start": v(-44.26, 13.38) * mm, "end": v(-44.31, 13.22) * mm});
            skLineSegment(sketch, "E2066", {"start": v(-44.31, 13.22) * mm, "end": v(-44.34, 13.14) * mm});
            skLineSegment(sketch, "E2067", {"start": v(-44.34, 13.14) * mm, "end": v(-44.5, 13.2) * mm});
            skLineSegment(sketch, "E2068", {"start": v(-44.5, 13.2) * mm, "end": v(-44.66, 13.24) * mm});
            skLineSegment(sketch, "E2069", {"start": v(-44.66, 13.24) * mm, "end": v(-44.82, 13.3) * mm});
            skLineSegment(sketch, "E2070", {"start": v(-44.82, 13.3) * mm, "end": v(-44.98, 13.34) * mm});
            skLineSegment(sketch, "E2071", {"start": v(-44.98, 13.34) * mm, "end": v(-45.14, 13.39) * mm});
            skLineSegment(sketch, "E2072", {"start": v(-45.14, 13.39) * mm, "end": v(-45.3, 13.44) * mm});
            skLineSegment(sketch, "E2073", {"start": v(-45.3, 13.44) * mm, "end": v(-45.46, 13.48) * mm});
            skLineSegment(sketch, "E2074", {"start": v(-45.46, 13.48) * mm, "end": v(-45.62, 13.53) * mm});
            skLineSegment(sketch, "E2075", {"start": v(-45.62, 13.53) * mm, "end": v(-45.79, 13.58) * mm});
            skLineSegment(sketch, "E2076", {"start": v(-45.79, 13.58) * mm, "end": v(-45.94, 13.63) * mm});
            skLineSegment(sketch, "E2077", {"start": v(-45.94, 13.63) * mm, "end": v(-46.1, 13.68) * mm});
            skLineSegment(sketch, "E2078", {"start": v(-46.1, 13.68) * mm, "end": v(-46.27, 13.73) * mm});
            skLineSegment(sketch, "E2079", {"start": v(-46.27, 13.73) * mm, "end": v(-46.44, 13.78) * mm});
            skLineSegment(sketch, "E2080", {"start": v(-46.44, 13.78) * mm, "end": v(-46.58, 13.8) * mm});
            skLineSegment(sketch, "E2081", {"start": v(-46.58, 13.8) * mm, "end": v(-46.75, 13.78) * mm});
            skLineSegment(sketch, "E2082", {"start": v(-46.75, 13.78) * mm, "end": v(-46.91, 13.71) * mm});
            skLineSegment(sketch, "E2083", {"start": v(-46.91, 13.71) * mm, "end": v(-47.05, 13.61) * mm});
            skLineSegment(sketch, "E2084", {"start": v(-47.05, 13.61) * mm, "end": v(-47.16, 13.47) * mm});
            skLineSegment(sketch, "E2085", {"start": v(-47.16, 13.47) * mm, "end": v(-47.23, 13.32) * mm});
            skLineSegment(sketch, "E2086", {"start": v(-47.23, 13.32) * mm, "end": v(-47.25, 13.14) * mm});
            skLineSegment(sketch, "E2087", {"start": v(-47.25, 13.14) * mm, "end": v(-47.23, 12.97) * mm});
            skLineSegment(sketch, "E2088", {"start": v(-47.23, 12.97) * mm, "end": v(-47.17, 12.81) * mm});
            skLineSegment(sketch, "E2089", {"start": v(-47.17, 12.81) * mm, "end": v(-47.07, 12.67) * mm});
            skLineSegment(sketch, "E2090", {"start": v(-47.07, 12.67) * mm, "end": v(-46.93, 12.56) * mm});
            skLineSegment(sketch, "E2091", {"start": v(-46.93, 12.56) * mm, "end": v(-46.77, 12.5) * mm});
            skLineSegment(sketch, "E2092", {"start": v(-46.77, 12.5) * mm, "end": v(-46.6, 12.45) * mm});
            skLineSegment(sketch, "E2093", {"start": v(-46.6, 12.45) * mm, "end": v(-46.45, 12.4) * mm});
            skLineSegment(sketch, "E2094", {"start": v(-46.45, 12.4) * mm, "end": v(-46.28, 12.36) * mm});
            skLineSegment(sketch, "E2095", {"start": v(-46.28, 12.36) * mm, "end": v(-46.12, 12.32) * mm});
            skLineSegment(sketch, "E2096", {"start": v(-46.12, 12.32) * mm, "end": v(-45.96, 12.28) * mm});
            skLineSegment(sketch, "E2097", {"start": v(-45.96, 12.28) * mm, "end": v(-45.8, 12.23) * mm});
            skLineSegment(sketch, "E2098", {"start": v(-45.8, 12.23) * mm, "end": v(-45.64, 12.19) * mm});
            skLineSegment(sketch, "E2099", {"start": v(-45.64, 12.19) * mm, "end": v(-45.48, 12.14) * mm});
            skLineSegment(sketch, "E2100", {"start": v(-45.48, 12.14) * mm, "end": v(-45.31, 12.1) * mm});
            skLineSegment(sketch, "E2101", {"start": v(-45.31, 12.1) * mm, "end": v(-45.15, 12.06) * mm});
            skLineSegment(sketch, "E2102", {"start": v(-45.15, 12.06) * mm, "end": v(-45, 12.01) * mm});
            skLineSegment(sketch, "E2103", {"start": v(-45, 12.01) * mm, "end": v(-44.83, 11.97) * mm});
            skLineSegment(sketch, "E2104", {"start": v(-44.83, 11.97) * mm, "end": v(-44.69, 11.93) * mm});
            skLineSegment(sketch, "E2105", {"start": v(-44.69, 11.93) * mm, "end": v(-44.73, 11.77) * mm});
            skLineSegment(sketch, "E2106", {"start": v(-44.73, 11.77) * mm, "end": v(-44.77, 11.6) * mm});
            skLineSegment(sketch, "E2107", {"start": v(-44.77, 11.6) * mm, "end": v(-44.8, 11.44) * mm});
            skLineSegment(sketch, "E2108", {"start": v(-44.8, 11.44) * mm, "end": v(-44.85, 11.28) * mm});
            skLineSegment(sketch, "E2109", {"start": v(-44.85, 11.28) * mm, "end": v(-44.89, 11.12) * mm});
            skLineSegment(sketch, "E2110", {"start": v(-44.89, 11.12) * mm, "end": v(-44.93, 10.96) * mm});
            skLineSegment(sketch, "E2111", {"start": v(-44.93, 10.96) * mm, "end": v(-44.97, 10.8) * mm});
            skLineSegment(sketch, "E2112", {"start": v(-44.97, 10.8) * mm, "end": v(-45, 10.64) * mm});
            skLineSegment(sketch, "E2113", {"start": v(-45, 10.64) * mm, "end": v(-45.05, 10.48) * mm});
            skLineSegment(sketch, "E2114", {"start": v(-45.05, 10.48) * mm, "end": v(-45.09, 10.31) * mm});
            skLineSegment(sketch, "E2115", {"start": v(-45.09, 10.31) * mm, "end": v(-45.13, 10.15) * mm});
            skLineSegment(sketch, "E2116", {"start": v(-45.13, 10.15) * mm, "end": v(-45.15, 10.07) * mm});
            skLineSegment(sketch, "E2117", {"start": v(-45.15, 10.07) * mm, "end": v(-45.31, 10.11) * mm});
            skLineSegment(sketch, "E2118", {"start": v(-45.31, 10.11) * mm, "end": v(-45.47, 10.15) * mm});
            skLineSegment(sketch, "E2119", {"start": v(-45.47, 10.15) * mm, "end": v(-45.64, 10.19) * mm});
            skLineSegment(sketch, "E2120", {"start": v(-45.64, 10.19) * mm, "end": v(-45.8, 10.22) * mm});
            skLineSegment(sketch, "E2121", {"start": v(-45.8, 10.22) * mm, "end": v(-45.96, 10.26) * mm});
            skLineSegment(sketch, "E2122", {"start": v(-45.96, 10.26) * mm, "end": v(-46.13, 10.3) * mm});
            skLineSegment(sketch, "E2123", {"start": v(-46.13, 10.3) * mm, "end": v(-46.3, 10.33) * mm});
            skLineSegment(sketch, "E2124", {"start": v(-46.3, 10.33) * mm, "end": v(-46.46, 10.37) * mm});
            skLineSegment(sketch, "E2125", {"start": v(-46.46, 10.37) * mm, "end": v(-46.62, 10.4) * mm});
            skLineSegment(sketch, "E2126", {"start": v(-46.62, 10.4) * mm, "end": v(-46.79, 10.45) * mm});
            skLineSegment(sketch, "E2127", {"start": v(-46.79, 10.45) * mm, "end": v(-46.95, 10.48) * mm});
            skLineSegment(sketch, "E2128", {"start": v(-46.95, 10.48) * mm, "end": v(-47.11, 10.52) * mm});
            skLineSegment(sketch, "E2129", {"start": v(-47.11, 10.52) * mm, "end": v(-47.29, 10.56) * mm});
            skLineSegment(sketch, "E2130", {"start": v(-47.29, 10.56) * mm, "end": v(-47.4, 10.57) * mm});
            skLineSegment(sketch, "E2131", {"start": v(-47.4, 10.57) * mm, "end": v(-47.56, 10.55) * mm});
            skLineSegment(sketch, "E2132", {"start": v(-47.56, 10.55) * mm, "end": v(-47.73, 10.48) * mm});
            skLineSegment(sketch, "E2133", {"start": v(-47.73, 10.48) * mm, "end": v(-47.86, 10.38) * mm});
            skLineSegment(sketch, "E2134", {"start": v(-47.86, 10.38) * mm, "end": v(-47.97, 10.24) * mm});
            skLineSegment(sketch, "E2135", {"start": v(-47.97, 10.24) * mm, "end": v(-48.04, 10.08) * mm});
            skLineSegment(sketch, "E2136", {"start": v(-48.04, 10.08) * mm, "end": v(-48.06, 9.9) * mm});
            skLineSegment(sketch, "E2137", {"start": v(-48.06, 9.9) * mm, "end": v(-48.04, 9.73) * mm});
            skLineSegment(sketch, "E2138", {"start": v(-48.04, 9.73) * mm, "end": v(-47.97, 9.57) * mm});
            skLineSegment(sketch, "E2139", {"start": v(-47.97, 9.57) * mm, "end": v(-47.86, 9.44) * mm});
            skLineSegment(sketch, "E2140", {"start": v(-47.86, 9.44) * mm, "end": v(-47.72, 9.33) * mm});
            skLineSegment(sketch, "E2141", {"start": v(-47.72, 9.33) * mm, "end": v(-47.56, 9.27) * mm});
            skLineSegment(sketch, "E2142", {"start": v(-47.56, 9.27) * mm, "end": v(-47.39, 9.23) * mm});
            skLineSegment(sketch, "E2143", {"start": v(-47.39, 9.23) * mm, "end": v(-47.23, 9.2) * mm});
            skLineSegment(sketch, "E2144", {"start": v(-47.23, 9.2) * mm, "end": v(-47.06, 9.17) * mm});
            skLineSegment(sketch, "E2145", {"start": v(-47.06, 9.17) * mm, "end": v(-46.9, 9.13) * mm});
            skLineSegment(sketch, "E2146", {"start": v(-46.9, 9.13) * mm, "end": v(-46.73, 9.1) * mm});
            skLineSegment(sketch, "E2147", {"start": v(-46.73, 9.1) * mm, "end": v(-46.57, 9.07) * mm});
            skLineSegment(sketch, "E2148", {"start": v(-46.57, 9.07) * mm, "end": v(-46.4, 9.03) * mm});
            skLineSegment(sketch, "E2149", {"start": v(-46.4, 9.03) * mm, "end": v(-46.24, 9) * mm});
            skLineSegment(sketch, "E2150", {"start": v(-46.24, 9) * mm, "end": v(-46.07, 8.97) * mm});
            skLineSegment(sketch, "E2151", {"start": v(-46.07, 8.97) * mm, "end": v(-45.9, 8.94) * mm});
            skLineSegment(sketch, "E2152", {"start": v(-45.9, 8.94) * mm, "end": v(-45.74, 8.9) * mm});
            skLineSegment(sketch, "E2153", {"start": v(-45.74, 8.9) * mm, "end": v(-45.58, 8.87) * mm});
            skLineSegment(sketch, "E2154", {"start": v(-45.58, 8.87) * mm, "end": v(-45.41, 8.84) * mm});
            skLineSegment(sketch, "E2155", {"start": v(-45.41, 8.84) * mm, "end": v(-45.44, 8.67) * mm});
            skLineSegment(sketch, "E2156", {"start": v(-45.44, 8.67) * mm, "end": v(-45.47, 8.51) * mm});
            skLineSegment(sketch, "E2157", {"start": v(-45.47, 8.51) * mm, "end": v(-45.5, 8.35) * mm});
            skLineSegment(sketch, "E2158", {"start": v(-45.5, 8.35) * mm, "end": v(-45.53, 8.18) * mm});
            skLineSegment(sketch, "E2159", {"start": v(-45.53, 8.18) * mm, "end": v(-45.56, 8.02) * mm});
            skLineSegment(sketch, "E2160", {"start": v(-45.56, 8.02) * mm, "end": v(-45.58, 7.86) * mm});
            skLineSegment(sketch, "E2161", {"start": v(-45.58, 7.86) * mm, "end": v(-45.61, 7.7) * mm});
            skLineSegment(sketch, "E2162", {"start": v(-45.61, 7.7) * mm, "end": v(-45.64, 7.53) * mm});
            skLineSegment(sketch, "E2163", {"start": v(-45.64, 7.53) * mm, "end": v(-45.67, 7.36) * mm});
            skLineSegment(sketch, "E2164", {"start": v(-45.67, 7.36) * mm, "end": v(-45.7, 7.2) * mm});
            skLineSegment(sketch, "E2165", {"start": v(-45.7, 7.2) * mm, "end": v(-45.73, 7.04) * mm});
            skLineSegment(sketch, "E2166", {"start": v(-45.73, 7.04) * mm, "end": v(-45.74, 6.96) * mm});
            skLineSegment(sketch, "E2167", {"start": v(-45.74, 6.96) * mm, "end": v(-45.9, 6.98) * mm});
            skLineSegment(sketch, "E2168", {"start": v(-45.9, 6.98) * mm, "end": v(-46.07, 7) * mm});
            skLineSegment(sketch, "E2169", {"start": v(-46.07, 7) * mm, "end": v(-46.24, 7.03) * mm});
            skLineSegment(sketch, "E2170", {"start": v(-46.24, 7.03) * mm, "end": v(-46.4, 7.06) * mm});
            skLineSegment(sketch, "E2171", {"start": v(-46.4, 7.06) * mm, "end": v(-46.57, 7.08) * mm});
            skLineSegment(sketch, "E2172", {"start": v(-46.57, 7.08) * mm, "end": v(-46.74, 7.11) * mm});
            skLineSegment(sketch, "E2173", {"start": v(-46.74, 7.11) * mm, "end": v(-46.9, 7.14) * mm});
            skLineSegment(sketch, "E2174", {"start": v(-46.9, 7.14) * mm, "end": v(-47.07, 7.16) * mm});
            skLineSegment(sketch, "E2175", {"start": v(-47.07, 7.16) * mm, "end": v(-47.24, 7.19) * mm});
            skLineSegment(sketch, "E2176", {"start": v(-47.24, 7.19) * mm, "end": v(-47.4, 7.21) * mm});
            skLineSegment(sketch, "E2177", {"start": v(-47.4, 7.21) * mm, "end": v(-47.57, 7.24) * mm});
            skLineSegment(sketch, "E2178", {"start": v(-47.57, 7.24) * mm, "end": v(-47.74, 7.26) * mm});
            skLineSegment(sketch, "E2179", {"start": v(-47.74, 7.26) * mm, "end": v(-47.91, 7.3) * mm});
            skLineSegment(sketch, "E2180", {"start": v(-47.91, 7.3) * mm, "end": v(-47.98, 7.3) * mm});
            skLineSegment(sketch, "E2181", {"start": v(-47.98, 7.3) * mm, "end": v(-48.15, 7.27) * mm});
            skLineSegment(sketch, "E2182", {"start": v(-48.15, 7.27) * mm, "end": v(-48.31, 7.2) * mm});
            skLineSegment(sketch, "E2183", {"start": v(-48.31, 7.2) * mm, "end": v(-48.45, 7.1) * mm});
            skLineSegment(sketch, "E2184", {"start": v(-48.45, 7.1) * mm, "end": v(-48.55, 6.95) * mm});
            skLineSegment(sketch, "E2185", {"start": v(-48.55, 6.95) * mm, "end": v(-48.62, 6.8) * mm});
            skLineSegment(sketch, "E2186", {"start": v(-48.62, 6.8) * mm, "end": v(-48.64, 6.62) * mm});
            skLineSegment(sketch, "E2187", {"start": v(-48.64, 6.62) * mm, "end": v(-48.61, 6.45) * mm});
            skLineSegment(sketch, "E2188", {"start": v(-48.61, 6.45) * mm, "end": v(-48.54, 6.29) * mm});
            skLineSegment(sketch, "E2189", {"start": v(-48.54, 6.29) * mm, "end": v(-48.43, 6.15) * mm});
            skLineSegment(sketch, "E2190", {"start": v(-48.43, 6.15) * mm, "end": v(-48.3, 6.05) * mm});
            skLineSegment(sketch, "E2191", {"start": v(-48.3, 6.05) * mm, "end": v(-48.13, 5.99) * mm});
            skLineSegment(sketch, "E2192", {"start": v(-48.13, 5.99) * mm, "end": v(-47.97, 5.96) * mm});
            skLineSegment(sketch, "E2193", {"start": v(-47.97, 5.96) * mm, "end": v(-47.8, 5.94) * mm});
            skLineSegment(sketch, "E2194", {"start": v(-47.8, 5.94) * mm, "end": v(-47.63, 5.92) * mm});
            skLineSegment(sketch, "E2195", {"start": v(-47.63, 5.92) * mm, "end": v(-47.47, 5.9) * mm});
            skLineSegment(sketch, "E2196", {"start": v(-47.47, 5.9) * mm, "end": v(-47.3, 5.88) * mm});
            skLineSegment(sketch, "E2197", {"start": v(-47.3, 5.88) * mm, "end": v(-47.13, 5.86) * mm});
            skLineSegment(sketch, "E2198", {"start": v(-47.13, 5.86) * mm, "end": v(-46.97, 5.84) * mm});
            skLineSegment(sketch, "E2199", {"start": v(-46.97, 5.84) * mm, "end": v(-46.8, 5.82) * mm});
            skLineSegment(sketch, "E2200", {"start": v(-46.8, 5.82) * mm, "end": v(-46.63, 5.8) * mm});
            skLineSegment(sketch, "E2201", {"start": v(-46.63, 5.8) * mm, "end": v(-46.47, 5.77) * mm});
            skLineSegment(sketch, "E2202", {"start": v(-46.47, 5.77) * mm, "end": v(-46.3, 5.75) * mm});
            skLineSegment(sketch, "E2203", {"start": v(-46.3, 5.75) * mm, "end": v(-46.13, 5.73) * mm});
            skLineSegment(sketch, "E2204", {"start": v(-46.13, 5.73) * mm, "end": v(-45.97, 5.71) * mm});
            skLineSegment(sketch, "E2205", {"start": v(-45.97, 5.71) * mm, "end": v(-45.92, 5.7) * mm});
            skLineSegment(sketch, "E2206", {"start": v(-45.92, 5.7) * mm, "end": v(-45.94, 5.54) * mm});
            skLineSegment(sketch, "E2207", {"start": v(-45.94, 5.54) * mm, "end": v(-45.95, 5.37) * mm});
            skLineSegment(sketch, "E2208", {"start": v(-45.95, 5.37) * mm, "end": v(-45.97, 5.2) * mm});
            skLineSegment(sketch, "E2209", {"start": v(-45.97, 5.2) * mm, "end": v(-45.99, 5.04) * mm});
            skLineSegment(sketch, "E2210", {"start": v(-45.99, 5.04) * mm, "end": v(-46, 4.88) * mm});
            skLineSegment(sketch, "E2211", {"start": v(-46, 4.88) * mm, "end": v(-46.02, 4.71) * mm});
            skLineSegment(sketch, "E2212", {"start": v(-46.02, 4.71) * mm, "end": v(-46.04, 4.55) * mm});
            skLineSegment(sketch, "E2213", {"start": v(-46.04, 4.55) * mm, "end": v(-46.06, 4.38) * mm});
            skLineSegment(sketch, "E2214", {"start": v(-46.06, 4.38) * mm, "end": v(-46.08, 4.21) * mm});
            skLineSegment(sketch, "E2215", {"start": v(-46.08, 4.21) * mm, "end": v(-46.1, 4.05) * mm});
            skLineSegment(sketch, "E2216", {"start": v(-46.1, 4.05) * mm, "end": v(-46.11, 3.88) * mm});
            skLineSegment(sketch, "E2217", {"start": v(-46.11, 3.88) * mm, "end": v(-46.12, 3.8) * mm});
            skLineSegment(sketch, "E2218", {"start": v(-46.12, 3.8) * mm, "end": v(-46.29, 3.82) * mm});
            skLineSegment(sketch, "E2219", {"start": v(-46.29, 3.82) * mm, "end": v(-46.45, 3.83) * mm});
            skLineSegment(sketch, "E2220", {"start": v(-46.45, 3.83) * mm, "end": v(-46.62, 3.85) * mm});
            skLineSegment(sketch, "E2221", {"start": v(-46.62, 3.85) * mm, "end": v(-46.79, 3.86) * mm});
            skLineSegment(sketch, "E2222", {"start": v(-46.79, 3.86) * mm, "end": v(-46.95, 3.87) * mm});
            skLineSegment(sketch, "E2223", {"start": v(-46.95, 3.87) * mm, "end": v(-47.12, 3.89) * mm});
            skLineSegment(sketch, "E2224", {"start": v(-47.12, 3.89) * mm, "end": v(-47.29, 3.9) * mm});
            skLineSegment(sketch, "E2225", {"start": v(-47.29, 3.9) * mm, "end": v(-47.46, 3.92) * mm});
            skLineSegment(sketch, "E2226", {"start": v(-47.46, 3.92) * mm, "end": v(-47.63, 3.93) * mm});
            skLineSegment(sketch, "E2227", {"start": v(-47.63, 3.93) * mm, "end": v(-47.8, 3.94) * mm});
            skLineSegment(sketch, "E2228", {"start": v(-47.8, 3.94) * mm, "end": v(-47.96, 3.96) * mm});
            skLineSegment(sketch, "E2229", {"start": v(-47.96, 3.96) * mm, "end": v(-48.13, 3.97) * mm});
            skLineSegment(sketch, "E2230", {"start": v(-48.13, 3.97) * mm, "end": v(-48.3, 3.99) * mm});
            skLineSegment(sketch, "E2231", {"start": v(-48.3, 3.99) * mm, "end": v(-48.48, 3.97) * mm});
            skLineSegment(sketch, "E2232", {"start": v(-48.48, 3.97) * mm, "end": v(-48.64, 3.9) * mm});
            skLineSegment(sketch, "E2233", {"start": v(-48.64, 3.9) * mm, "end": v(-48.78, 3.8) * mm});
            skLineSegment(sketch, "E2234", {"start": v(-48.78, 3.8) * mm, "end": v(-48.89, 3.67) * mm});
            skLineSegment(sketch, "E2235", {"start": v(-48.89, 3.67) * mm, "end": v(-48.96, 3.5) * mm});
            skLineSegment(sketch, "E2236", {"start": v(-48.96, 3.5) * mm, "end": v(-48.98, 3.34) * mm});
            skLineSegment(sketch, "E2237", {"start": v(-48.98, 3.34) * mm, "end": v(-48.96, 3.16) * mm});
            skLineSegment(sketch, "E2238", {"start": v(-48.96, 3.16) * mm, "end": v(-48.9, 3) * mm});
            skLineSegment(sketch, "E2239", {"start": v(-48.9, 3) * mm, "end": v(-48.8, 2.86) * mm});
            skLineSegment(sketch, "E2240", {"start": v(-48.8, 2.86) * mm, "end": v(-48.66, 2.75) * mm});
            skLineSegment(sketch, "E2241", {"start": v(-48.66, 2.75) * mm, "end": v(-48.5, 2.69) * mm});
            skLineSegment(sketch, "E2242", {"start": v(-48.5, 2.69) * mm, "end": v(-48.34, 2.66) * mm});
            skLineSegment(sketch, "E2243", {"start": v(-48.34, 2.66) * mm, "end": v(-48.17, 2.65) * mm});
            skLineSegment(sketch, "E2244", {"start": v(-48.17, 2.65) * mm, "end": v(-48, 2.64) * mm});
            skLineSegment(sketch, "E2245", {"start": v(-48, 2.64) * mm, "end": v(-47.84, 2.63) * mm});
            skLineSegment(sketch, "E2246", {"start": v(-47.84, 2.63) * mm, "end": v(-47.67, 2.62) * mm});
            skLineSegment(sketch, "E2247", {"start": v(-47.67, 2.62) * mm, "end": v(-47.5, 2.61) * mm});
            skLineSegment(sketch, "E2248", {"start": v(-47.5, 2.61) * mm, "end": v(-47.33, 2.6) * mm});
            skLineSegment(sketch, "E2249", {"start": v(-47.33, 2.6) * mm, "end": v(-47.17, 2.6) * mm});
            skLineSegment(sketch, "E2250", {"start": v(-47.17, 2.6) * mm, "end": v(-47, 2.59) * mm});
            skLineSegment(sketch, "E2251", {"start": v(-47, 2.59) * mm, "end": v(-46.83, 2.58) * mm});
            skLineSegment(sketch, "E2252", {"start": v(-46.83, 2.58) * mm, "end": v(-46.67, 2.57) * mm});
            skLineSegment(sketch, "E2253", {"start": v(-46.67, 2.57) * mm, "end": v(-46.5, 2.56) * mm});
            skLineSegment(sketch, "E2254", {"start": v(-46.5, 2.56) * mm, "end": v(-46.33, 2.55) * mm});
            skLineSegment(sketch, "E2255", {"start": v(-46.33, 2.55) * mm, "end": v(-46.2, 2.54) * mm});
            skLineSegment(sketch, "E2256", {"start": v(-46.2, 2.54) * mm, "end": v(-46.21, 2.38) * mm});
            skLineSegment(sketch, "E2257", {"start": v(-46.21, 2.38) * mm, "end": v(-46.22, 2.2) * mm});
            skLineSegment(sketch, "E2258", {"start": v(-46.22, 2.2) * mm, "end": v(-46.22, 2.04) * mm});
            skLineSegment(sketch, "E2259", {"start": v(-46.22, 2.04) * mm, "end": v(-46.23, 1.88) * mm});
            skLineSegment(sketch, "E2260", {"start": v(-46.23, 1.88) * mm, "end": v(-46.24, 1.71) * mm});
            skLineSegment(sketch, "E2261", {"start": v(-46.24, 1.71) * mm, "end": v(-46.24, 1.54) * mm});
            skLineSegment(sketch, "E2262", {"start": v(-46.24, 1.54) * mm, "end": v(-46.25, 1.38) * mm});
            skLineSegment(sketch, "E2263", {"start": v(-46.25, 1.38) * mm, "end": v(-46.25, 1.21) * mm});
            skLineSegment(sketch, "E2264", {"start": v(-46.25, 1.21) * mm, "end": v(-46.26, 1.05) * mm});
            skLineSegment(sketch, "E2265", {"start": v(-46.26, 1.05) * mm, "end": v(-46.27, 0.88) * mm});
            skLineSegment(sketch, "E2266", {"start": v(-46.27, 0.88) * mm, "end": v(-46.27, 0.71) * mm});
            skLineSegment(sketch, "E2267", {"start": v(-46.27, 0.71) * mm, "end": v(-46.27, 0.63) * mm});
            skLineSegment(sketch, "E2268", {"start": v(-46.27, 0.63) * mm, "end": v(-46.44, 0.63) * mm});
            skLineSegment(sketch, "E2269", {"start": v(-46.44, 0.63) * mm, "end": v(-46.6, 0.64) * mm});
            skLineSegment(sketch, "E2270", {"start": v(-46.6, 0.64) * mm, "end": v(-46.78, 0.64) * mm});
            skLineSegment(sketch, "E2271", {"start": v(-46.78, 0.64) * mm, "end": v(-46.94, 0.64) * mm});
            skLineSegment(sketch, "E2272", {"start": v(-46.94, 0.64) * mm, "end": v(-47.11, 0.64) * mm});
            skLineSegment(sketch, "E2273", {"start": v(-47.11, 0.64) * mm, "end": v(-47.28, 0.65) * mm});
            skLineSegment(sketch, "E2274", {"start": v(-47.28, 0.65) * mm, "end": v(-47.45, 0.65) * mm});
            skLineSegment(sketch, "E2275", {"start": v(-47.45, 0.65) * mm, "end": v(-47.61, 0.65) * mm});
            skLineSegment(sketch, "E2276", {"start": v(-47.61, 0.65) * mm, "end": v(-47.79, 0.65) * mm});
            skLineSegment(sketch, "E2277", {"start": v(-47.79, 0.65) * mm, "end": v(-47.95, 0.66) * mm});
            skLineSegment(sketch, "E2278", {"start": v(-47.95, 0.66) * mm, "end": v(-48.12, 0.66) * mm});
            skLineSegment(sketch, "E2279", {"start": v(-48.12, 0.66) * mm, "end": v(-48.29, 0.66) * mm});
            skLineSegment(sketch, "E2280", {"start": v(-48.29, 0.66) * mm, "end": v(-48.43, 0.66) * mm});
            skLineSegment(sketch, "E2281", {"start": v(-48.43, 0.66) * mm, "end": v(-48.6, 0.64) * mm});
            skLineSegment(sketch, "E2282", {"start": v(-48.6, 0.64) * mm, "end": v(-48.77, 0.57) * mm});
            skLineSegment(sketch, "E2283", {"start": v(-48.77, 0.57) * mm, "end": v(-48.9, 0.47) * mm});
            skLineSegment(sketch, "E2284", {"start": v(-48.9, 0.47) * mm, "end": v(-49.01, 0.33) * mm});
            skLineSegment(sketch, "E2285", {"start": v(-49.01, 0.33) * mm, "end": v(-49.08, 0.17) * mm});
            skLineSegment(sketch, "E2286", {"start": v(-49.08, 0.17) * mm, "end": v(-49.1, 0) * mm});
            skLineSegment(sketch, "E2287", {"start": v(-49.1, 0) * mm, "end": v(-49.08, -0.17) * mm});
            skLineSegment(sketch, "E2288", {"start": v(-49.08, -0.17) * mm, "end": v(-49.01, -0.33) * mm});
            skLineSegment(sketch, "E2289", {"start": v(-49.01, -0.33) * mm, "end": v(-48.9, -0.47) * mm});
            skLineSegment(sketch, "E2290", {"start": v(-48.9, -0.47) * mm, "end": v(-48.77, -0.57) * mm});
            skLineSegment(sketch, "E2291", {"start": v(-48.77, -0.57) * mm, "end": v(-48.6, -0.64) * mm});
            skLineSegment(sketch, "E2292", {"start": v(-48.6, -0.64) * mm, "end": v(-48.43, -0.66) * mm});
            skLineSegment(sketch, "E2293", {"start": v(-48.43, -0.66) * mm, "end": v(-48.27, -0.66) * mm});
            skLineSegment(sketch, "E2294", {"start": v(-48.27, -0.66) * mm, "end": v(-48.1, -0.66) * mm});
            skLineSegment(sketch, "E2295", {"start": v(-48.1, -0.66) * mm, "end": v(-47.93, -0.66) * mm});
            skLineSegment(sketch, "E2296", {"start": v(-47.93, -0.66) * mm, "end": v(-47.76, -0.65) * mm});
            skLineSegment(sketch, "E2297", {"start": v(-47.76, -0.65) * mm, "end": v(-47.6, -0.65) * mm});
            skLineSegment(sketch, "E2298", {"start": v(-47.6, -0.65) * mm, "end": v(-47.43, -0.65) * mm});
            skLineSegment(sketch, "E2299", {"start": v(-47.43, -0.65) * mm, "end": v(-47.26, -0.65) * mm});
            skLineSegment(sketch, "E2300", {"start": v(-47.26, -0.65) * mm, "end": v(-47.1, -0.64) * mm});
            skLineSegment(sketch, "E2301", {"start": v(-47.1, -0.64) * mm, "end": v(-46.92, -0.64) * mm});
            skLineSegment(sketch, "E2302", {"start": v(-46.92, -0.64) * mm, "end": v(-46.76, -0.64) * mm});
            skLineSegment(sketch, "E2303", {"start": v(-46.76, -0.64) * mm, "end": v(-46.59, -0.64) * mm});
            skLineSegment(sketch, "E2304", {"start": v(-46.59, -0.64) * mm, "end": v(-46.42, -0.63) * mm});
            skLineSegment(sketch, "E2305", {"start": v(-46.42, -0.63) * mm, "end": v(-46.27, -0.63) * mm});
            skLineSegment(sketch, "E2306", {"start": v(-46.27, -0.63) * mm, "end": v(-46.27, -0.8) * mm});
            skLineSegment(sketch, "E2307", {"start": v(-46.27, -0.8) * mm, "end": v(-46.26, -0.96) * mm});
            skLineSegment(sketch, "E2308", {"start": v(-46.26, -0.96) * mm, "end": v(-46.26, -1.13) * mm});
            skLineSegment(sketch, "E2309", {"start": v(-46.26, -1.13) * mm, "end": v(-46.25, -1.3) * mm});
            skLineSegment(sketch, "E2310", {"start": v(-46.25, -1.3) * mm, "end": v(-46.25, -1.46) * mm});
            skLineSegment(sketch, "E2311", {"start": v(-46.25, -1.46) * mm, "end": v(-46.24, -1.63) * mm});
            skLineSegment(sketch, "E2312", {"start": v(-46.24, -1.63) * mm, "end": v(-46.23, -1.8) * mm});
            skLineSegment(sketch, "E2313", {"start": v(-46.23, -1.8) * mm, "end": v(-46.23, -1.96) * mm});
            skLineSegment(sketch, "E2314", {"start": v(-46.23, -1.96) * mm, "end": v(-46.22, -2.13) * mm});
            skLineSegment(sketch, "E2315", {"start": v(-46.22, -2.13) * mm, "end": v(-46.22, -2.3) * mm});
            skLineSegment(sketch, "E2316", {"start": v(-46.22, -2.3) * mm, "end": v(-46.21, -2.46) * mm});
            skLineSegment(sketch, "E2317", {"start": v(-46.21, -2.46) * mm, "end": v(-46.2, -2.54) * mm});
            skLineSegment(sketch, "E2318", {"start": v(-46.2, -2.54) * mm, "end": v(-46.37, -2.55) * mm});
            skLineSegment(sketch, "E2319", {"start": v(-46.37, -2.55) * mm, "end": v(-46.54, -2.56) * mm});
            skLineSegment(sketch, "E2320", {"start": v(-46.54, -2.56) * mm, "end": v(-46.71, -2.57) * mm});
            skLineSegment(sketch, "E2321", {"start": v(-46.71, -2.57) * mm, "end": v(-46.88, -2.58) * mm});
            skLineSegment(sketch, "E2322", {"start": v(-46.88, -2.58) * mm, "end": v(-47.04, -2.59) * mm});
            skLineSegment(sketch, "E2323", {"start": v(-47.04, -2.59) * mm, "end": v(-47.21, -2.6) * mm});
            skLineSegment(sketch, "E2324", {"start": v(-47.21, -2.6) * mm, "end": v(-47.38, -2.6) * mm});
            skLineSegment(sketch, "E2325", {"start": v(-47.38, -2.6) * mm, "end": v(-47.55, -2.62) * mm});
            skLineSegment(sketch, "E2326", {"start": v(-47.55, -2.62) * mm, "end": v(-47.72, -2.63) * mm});
            skLineSegment(sketch, "E2327", {"start": v(-47.72, -2.63) * mm, "end": v(-47.88, -2.64) * mm});
            skLineSegment(sketch, "E2328", {"start": v(-47.88, -2.64) * mm, "end": v(-48.05, -2.65) * mm});
            skLineSegment(sketch, "E2329", {"start": v(-48.05, -2.65) * mm, "end": v(-48.22, -2.65) * mm});
            skLineSegment(sketch, "E2330", {"start": v(-48.22, -2.65) * mm, "end": v(-48.4, -2.67) * mm});
            skLineSegment(sketch, "E2331", {"start": v(-48.4, -2.67) * mm, "end": v(-48.57, -2.7) * mm});
            skLineSegment(sketch, "E2332", {"start": v(-48.57, -2.7) * mm, "end": v(-48.72, -2.8) * mm});
            skLineSegment(sketch, "E2333", {"start": v(-48.72, -2.8) * mm, "end": v(-48.84, -2.91) * mm});
            skLineSegment(sketch, "E2334", {"start": v(-48.84, -2.91) * mm, "end": v(-48.93, -3.06) * mm});
            skLineSegment(sketch, "E2335", {"start": v(-48.93, -3.06) * mm, "end": v(-48.98, -3.23) * mm});
            skLineSegment(sketch, "E2336", {"start": v(-48.98, -3.23) * mm, "end": v(-48.98, -3.4) * mm});
            skLineSegment(sketch, "E2337", {"start": v(-48.98, -3.4) * mm, "end": v(-48.94, -3.57) * mm});
            skLineSegment(sketch, "E2338", {"start": v(-48.94, -3.57) * mm, "end": v(-48.85, -3.72) * mm});
            skLineSegment(sketch, "E2339", {"start": v(-48.85, -3.72) * mm, "end": v(-48.73, -3.85) * mm});
            skLineSegment(sketch, "E2340", {"start": v(-48.73, -3.85) * mm, "end": v(-48.58, -3.93) * mm});
            skLineSegment(sketch, "E2341", {"start": v(-48.58, -3.93) * mm, "end": v(-48.41, -3.98) * mm});
            skLineSegment(sketch, "E2342", {"start": v(-48.41, -3.98) * mm, "end": v(-48.24, -3.98) * mm});
            skLineSegment(sketch, "E2343", {"start": v(-48.24, -3.98) * mm, "end": v(-48.08, -3.97) * mm});
            skLineSegment(sketch, "E2344", {"start": v(-48.08, -3.97) * mm, "end": v(-47.91, -3.95) * mm});
            skLineSegment(sketch, "E2345", {"start": v(-47.91, -3.95) * mm, "end": v(-47.75, -3.94) * mm});
            skLineSegment(sketch, "E2346", {"start": v(-47.75, -3.94) * mm, "end": v(-47.58, -3.93) * mm});
            skLineSegment(sketch, "E2347", {"start": v(-47.58, -3.93) * mm, "end": v(-47.41, -3.91) * mm});
            skLineSegment(sketch, "E2348", {"start": v(-47.41, -3.91) * mm, "end": v(-47.24, -3.9) * mm});
            skLineSegment(sketch, "E2349", {"start": v(-47.24, -3.9) * mm, "end": v(-47.08, -3.88) * mm});
            skLineSegment(sketch, "E2350", {"start": v(-47.08, -3.88) * mm, "end": v(-46.9, -3.87) * mm});
            skLineSegment(sketch, "E2351", {"start": v(-46.9, -3.87) * mm, "end": v(-46.74, -3.86) * mm});
            skLineSegment(sketch, "E2352", {"start": v(-46.74, -3.86) * mm, "end": v(-46.58, -3.84) * mm});
            skLineSegment(sketch, "E2353", {"start": v(-46.58, -3.84) * mm, "end": v(-46.4, -3.83) * mm});
            skLineSegment(sketch, "E2354", {"start": v(-46.4, -3.83) * mm, "end": v(-46.24, -3.81) * mm});
            skLineSegment(sketch, "E2355", {"start": v(-46.24, -3.81) * mm, "end": v(-46.12, -3.8) * mm});
            skLineSegment(sketch, "E2356", {"start": v(-46.12, -3.8) * mm, "end": v(-46.1, -3.97) * mm});
            skLineSegment(sketch, "E2357", {"start": v(-46.1, -3.97) * mm, "end": v(-46.08, -4.13) * mm});
            skLineSegment(sketch, "E2358", {"start": v(-46.08, -4.13) * mm, "end": v(-46.07, -4.3) * mm});
            skLineSegment(sketch, "E2359", {"start": v(-46.07, -4.3) * mm, "end": v(-46.05, -4.47) * mm});
            skLineSegment(sketch, "E2360", {"start": v(-46.05, -4.47) * mm, "end": v(-46.03, -4.63) * mm});
            skLineSegment(sketch, "E2361", {"start": v(-46.03, -4.63) * mm, "end": v(-46.01, -4.8) * mm});
            skLineSegment(sketch, "E2362", {"start": v(-46.01, -4.8) * mm, "end": v(-46, -4.96) * mm});
            skLineSegment(sketch, "E2363", {"start": v(-46, -4.96) * mm, "end": v(-45.98, -5.13) * mm});
            skLineSegment(sketch, "E2364", {"start": v(-45.98, -5.13) * mm, "end": v(-45.96, -5.3) * mm});
            skLineSegment(sketch, "E2365", {"start": v(-45.96, -5.3) * mm, "end": v(-45.95, -5.46) * mm});
            skLineSegment(sketch, "E2366", {"start": v(-45.95, -5.46) * mm, "end": v(-45.93, -5.62) * mm});
            skLineSegment(sketch, "E2367", {"start": v(-45.93, -5.62) * mm, "end": v(-45.92, -5.7) * mm});
            skLineSegment(sketch, "E2368", {"start": v(-45.92, -5.7) * mm, "end": v(-46.08, -5.72) * mm});
            skLineSegment(sketch, "E2369", {"start": v(-46.08, -5.72) * mm, "end": v(-46.25, -5.75) * mm});
            skLineSegment(sketch, "E2370", {"start": v(-46.25, -5.75) * mm, "end": v(-46.42, -5.77) * mm});
            skLineSegment(sketch, "E2371", {"start": v(-46.42, -5.77) * mm, "end": v(-46.58, -5.79) * mm});
            skLineSegment(sketch, "E2372", {"start": v(-46.58, -5.79) * mm, "end": v(-46.75, -5.8) * mm});
            skLineSegment(sketch, "E2373", {"start": v(-46.75, -5.8) * mm, "end": v(-46.92, -5.83) * mm});
            skLineSegment(sketch, "E2374", {"start": v(-46.92, -5.83) * mm, "end": v(-47.08, -5.85) * mm});
            skLineSegment(sketch, "E2375", {"start": v(-47.08, -5.85) * mm, "end": v(-47.25, -5.87) * mm});
            skLineSegment(sketch, "E2376", {"start": v(-47.25, -5.87) * mm, "end": v(-47.42, -5.9) * mm});
            skLineSegment(sketch, "E2377", {"start": v(-47.42, -5.9) * mm, "end": v(-47.58, -5.91) * mm});
            skLineSegment(sketch, "E2378", {"start": v(-47.58, -5.91) * mm, "end": v(-47.75, -5.94) * mm});
            skLineSegment(sketch, "E2379", {"start": v(-47.75, -5.94) * mm, "end": v(-47.92, -5.96) * mm});
            skLineSegment(sketch, "E2380", {"start": v(-47.92, -5.96) * mm, "end": v(-48.1, -5.98) * mm});
            skLineSegment(sketch, "E2381", {"start": v(-48.1, -5.98) * mm, "end": v(-48.26, -6.03) * mm});
            skLineSegment(sketch, "E2382", {"start": v(-48.26, -6.03) * mm, "end": v(-48.4, -6.13) * mm});
            skLineSegment(sketch, "E2383", {"start": v(-48.4, -6.13) * mm, "end": v(-48.52, -6.26) * mm});
            skLineSegment(sketch, "E2384", {"start": v(-48.52, -6.26) * mm, "end": v(-48.6, -6.41) * mm});
            skLineSegment(sketch, "E2385", {"start": v(-48.6, -6.41) * mm, "end": v(-48.63, -6.58) * mm});
            skLineSegment(sketch, "E2386", {"start": v(-48.63, -6.58) * mm, "end": v(-48.62, -6.76) * mm});
            skLineSegment(sketch, "E2387", {"start": v(-48.62, -6.76) * mm, "end": v(-48.57, -6.92) * mm});
            skLineSegment(sketch, "E2388", {"start": v(-48.57, -6.92) * mm, "end": v(-48.47, -7.07) * mm});
            skLineSegment(sketch, "E2389", {"start": v(-48.47, -7.07) * mm, "end": v(-48.34, -7.18) * mm});
            skLineSegment(sketch, "E2390", {"start": v(-48.34, -7.18) * mm, "end": v(-48.19, -7.26) * mm});
            skLineSegment(sketch, "E2391", {"start": v(-48.19, -7.26) * mm, "end": v(-48.02, -7.3) * mm});
            skLineSegment(sketch, "E2392", {"start": v(-48.02, -7.3) * mm, "end": v(-47.85, -7.28) * mm});
            skLineSegment(sketch, "E2393", {"start": v(-47.85, -7.28) * mm, "end": v(-47.69, -7.26) * mm});
            skLineSegment(sketch, "E2394", {"start": v(-47.69, -7.26) * mm, "end": v(-47.52, -7.23) * mm});
            skLineSegment(sketch, "E2395", {"start": v(-47.52, -7.23) * mm, "end": v(-47.36, -7.2) * mm});
            skLineSegment(sketch, "E2396", {"start": v(-47.36, -7.2) * mm, "end": v(-47.2, -7.18) * mm});
            skLineSegment(sketch, "E2397", {"start": v(-47.2, -7.18) * mm, "end": v(-47.02, -7.15) * mm});
            skLineSegment(sketch, "E2398", {"start": v(-47.02, -7.15) * mm, "end": v(-46.86, -7.13) * mm});
            skLineSegment(sketch, "E2399", {"start": v(-46.86, -7.13) * mm, "end": v(-46.7, -7.1) * mm});
            skLineSegment(sketch, "E2400", {"start": v(-46.7, -7.1) * mm, "end": v(-46.53, -7.08) * mm});
            skLineSegment(sketch, "E2401", {"start": v(-46.53, -7.08) * mm, "end": v(-46.36, -7.05) * mm});
            skLineSegment(sketch, "E2402", {"start": v(-46.36, -7.05) * mm, "end": v(-46.2, -7.03) * mm});
            skLineSegment(sketch, "E2403", {"start": v(-46.2, -7.03) * mm, "end": v(-46.03, -7) * mm});
            skLineSegment(sketch, "E2404", {"start": v(-46.03, -7) * mm, "end": v(-45.86, -6.97) * mm});
            skLineSegment(sketch, "E2405", {"start": v(-45.86, -6.97) * mm, "end": v(-45.74, -6.96) * mm});
            skLineSegment(sketch, "E2406", {"start": v(-45.74, -6.96) * mm, "end": v(-45.71, -7.12) * mm});
            skLineSegment(sketch, "E2407", {"start": v(-45.71, -7.12) * mm, "end": v(-45.69, -7.28) * mm});
            skLineSegment(sketch, "E2408", {"start": v(-45.69, -7.28) * mm, "end": v(-45.66, -7.45) * mm});
            skLineSegment(sketch, "E2409", {"start": v(-45.66, -7.45) * mm, "end": v(-45.63, -7.61) * mm});
            skLineSegment(sketch, "E2410", {"start": v(-45.63, -7.61) * mm, "end": v(-45.6, -7.78) * mm});
            skLineSegment(sketch, "E2411", {"start": v(-45.6, -7.78) * mm, "end": v(-45.57, -7.94) * mm});
            skLineSegment(sketch, "E2412", {"start": v(-45.57, -7.94) * mm, "end": v(-45.54, -8.1) * mm});
            skLineSegment(sketch, "E2413", {"start": v(-45.54, -8.1) * mm, "end": v(-45.51, -8.27) * mm});
            skLineSegment(sketch, "E2414", {"start": v(-45.51, -8.27) * mm, "end": v(-45.48, -8.43) * mm});
            skLineSegment(sketch, "E2415", {"start": v(-45.48, -8.43) * mm, "end": v(-45.45, -8.6) * mm});
            skLineSegment(sketch, "E2416", {"start": v(-45.45, -8.6) * mm, "end": v(-45.43, -8.76) * mm});
            skLineSegment(sketch, "E2417", {"start": v(-45.43, -8.76) * mm, "end": v(-45.41, -8.84) * mm});
            skLineSegment(sketch, "E2418", {"start": v(-45.41, -8.84) * mm, "end": v(-45.57, -8.87) * mm});
            skLineSegment(sketch, "E2419", {"start": v(-45.57, -8.87) * mm, "end": v(-45.74, -8.9) * mm});
            skLineSegment(sketch, "E2420", {"start": v(-45.74, -8.9) * mm, "end": v(-45.9, -8.94) * mm});
            skLineSegment(sketch, "E2421", {"start": v(-45.9, -8.94) * mm, "end": v(-46.07, -8.97) * mm});
            skLineSegment(sketch, "E2422", {"start": v(-46.07, -8.97) * mm, "end": v(-46.23, -9) * mm});
            skLineSegment(sketch, "E2423", {"start": v(-46.23, -9) * mm, "end": v(-46.4, -9.03) * mm});
            skLineSegment(sketch, "E2424", {"start": v(-46.4, -9.03) * mm, "end": v(-46.56, -9.07) * mm});
            skLineSegment(sketch, "E2425", {"start": v(-46.56, -9.07) * mm, "end": v(-46.73, -9.1) * mm});
            skLineSegment(sketch, "E2426", {"start": v(-46.73, -9.1) * mm, "end": v(-46.9, -9.13) * mm});
            skLineSegment(sketch, "E2427", {"start": v(-46.9, -9.13) * mm, "end": v(-47.06, -9.16) * mm});
            skLineSegment(sketch, "E2428", {"start": v(-47.06, -9.16) * mm, "end": v(-47.22, -9.2) * mm});
            skLineSegment(sketch, "E2429", {"start": v(-47.22, -9.2) * mm, "end": v(-47.39, -9.23) * mm});
            skLineSegment(sketch, "E2430", {"start": v(-47.39, -9.23) * mm, "end": v(-47.56, -9.27) * mm});
            skLineSegment(sketch, "E2431", {"start": v(-47.56, -9.27) * mm, "end": v(-47.72, -9.33) * mm});
            skLineSegment(sketch, "E2432", {"start": v(-47.72, -9.33) * mm, "end": v(-47.86, -9.44) * mm});
            skLineSegment(sketch, "E2433", {"start": v(-47.86, -9.44) * mm, "end": v(-47.97, -9.57) * mm});
            skLineSegment(sketch, "E2434", {"start": v(-47.97, -9.57) * mm, "end": v(-48.04, -9.73) * mm});
            skLineSegment(sketch, "E2435", {"start": v(-48.04, -9.73) * mm, "end": v(-48.06, -9.9) * mm});
            skLineSegment(sketch, "E2436", {"start": v(-48.06, -9.9) * mm, "end": v(-48.04, -10.08) * mm});
            skLineSegment(sketch, "E2437", {"start": v(-48.04, -10.08) * mm, "end": v(-47.97, -10.24) * mm});
            skLineSegment(sketch, "E2438", {"start": v(-47.97, -10.24) * mm, "end": v(-47.86, -10.38) * mm});
            skLineSegment(sketch, "E2439", {"start": v(-47.86, -10.38) * mm, "end": v(-47.73, -10.48) * mm});
            skLineSegment(sketch, "E2440", {"start": v(-47.73, -10.48) * mm, "end": v(-47.56, -10.55) * mm});
            skLineSegment(sketch, "E2441", {"start": v(-47.56, -10.55) * mm, "end": v(-47.4, -10.57) * mm});
            skLineSegment(sketch, "E2442", {"start": v(-47.4, -10.57) * mm, "end": v(-47.23, -10.54) * mm});
            skLineSegment(sketch, "E2443", {"start": v(-47.23, -10.54) * mm, "end": v(-47.07, -10.5) * mm});
            skLineSegment(sketch, "E2444", {"start": v(-47.07, -10.5) * mm, "end": v(-46.9, -10.47) * mm});
            skLineSegment(sketch, "E2445", {"start": v(-46.9, -10.47) * mm, "end": v(-46.74, -10.44) * mm});
            skLineSegment(sketch, "E2446", {"start": v(-46.74, -10.44) * mm, "end": v(-46.58, -10.4) * mm});
            skLineSegment(sketch, "E2447", {"start": v(-46.58, -10.4) * mm, "end": v(-46.41, -10.36) * mm});
            skLineSegment(sketch, "E2448", {"start": v(-46.41, -10.36) * mm, "end": v(-46.25, -10.32) * mm});
            skLineSegment(sketch, "E2449", {"start": v(-46.25, -10.32) * mm, "end": v(-46.09, -10.29) * mm});
            skLineSegment(sketch, "E2450", {"start": v(-46.09, -10.29) * mm, "end": v(-45.92, -10.25) * mm});
            skLineSegment(sketch, "E2451", {"start": v(-45.92, -10.25) * mm, "end": v(-45.76, -10.21) * mm});
            skLineSegment(sketch, "E2452", {"start": v(-45.76, -10.21) * mm, "end": v(-45.6, -10.18) * mm});
            skLineSegment(sketch, "E2453", {"start": v(-45.6, -10.18) * mm, "end": v(-45.43, -10.14) * mm});
            skLineSegment(sketch, "E2454", {"start": v(-45.43, -10.14) * mm, "end": v(-45.27, -10.1) * mm});
            skLineSegment(sketch, "E2455", {"start": v(-45.27, -10.1) * mm, "end": v(-45.15, -10.07) * mm});
            skLineSegment(sketch, "E2456", {"start": v(-45.15, -10.07) * mm, "end": v(-45.1, -10.24) * mm});
            skLineSegment(sketch, "E2457", {"start": v(-45.1, -10.24) * mm, "end": v(-45.07, -10.4) * mm});
            skLineSegment(sketch, "E2458", {"start": v(-45.07, -10.4) * mm, "end": v(-45.03, -10.56) * mm});
            skLineSegment(sketch, "E2459", {"start": v(-45.03, -10.56) * mm, "end": v(-44.99, -10.72) * mm});
            skLineSegment(sketch, "E2460", {"start": v(-44.99, -10.72) * mm, "end": v(-44.95, -10.88) * mm});
            skLineSegment(sketch, "E2461", {"start": v(-44.95, -10.88) * mm, "end": v(-44.9, -11.04) * mm});
            skLineSegment(sketch, "E2462", {"start": v(-44.9, -11.04) * mm, "end": v(-44.87, -11.2) * mm});
            skLineSegment(sketch, "E2463", {"start": v(-44.87, -11.2) * mm, "end": v(-44.83, -11.37) * mm});
            skLineSegment(sketch, "E2464", {"start": v(-44.83, -11.37) * mm, "end": v(-44.79, -11.53) * mm});
            skLineSegment(sketch, "E2465", {"start": v(-44.79, -11.53) * mm, "end": v(-44.75, -11.69) * mm});
            skLineSegment(sketch, "E2466", {"start": v(-44.75, -11.69) * mm, "end": v(-44.7, -11.85) * mm});
            skLineSegment(sketch, "E2467", {"start": v(-44.7, -11.85) * mm, "end": v(-44.69, -11.93) * mm});
            skLineSegment(sketch, "E2468", {"start": v(-44.69, -11.93) * mm, "end": v(-44.85, -11.97) * mm});
            skLineSegment(sketch, "E2469", {"start": v(-44.85, -11.97) * mm, "end": v(-45, -12.02) * mm});
            skLineSegment(sketch, "E2470", {"start": v(-45, -12.02) * mm, "end": v(-45.17, -12.06) * mm});
            skLineSegment(sketch, "E2471", {"start": v(-45.17, -12.06) * mm, "end": v(-45.33, -12.1) * mm});
            skLineSegment(sketch, "E2472", {"start": v(-45.33, -12.1) * mm, "end": v(-45.5, -12.15) * mm});
            skLineSegment(sketch, "E2473", {"start": v(-45.5, -12.15) * mm, "end": v(-45.66, -12.2) * mm});
            skLineSegment(sketch, "E2474", {"start": v(-45.66, -12.2) * mm, "end": v(-45.82, -12.24) * mm});
            skLineSegment(sketch, "E2475", {"start": v(-45.82, -12.24) * mm, "end": v(-45.98, -12.28) * mm});
            skLineSegment(sketch, "E2476", {"start": v(-45.98, -12.28) * mm, "end": v(-46.15, -12.33) * mm});
            skLineSegment(sketch, "E2477", {"start": v(-46.15, -12.33) * mm, "end": v(-46.3, -12.37) * mm});
            skLineSegment(sketch, "E2478", {"start": v(-46.3, -12.37) * mm, "end": v(-46.47, -12.41) * mm});
            skLineSegment(sketch, "E2479", {"start": v(-46.47, -12.41) * mm, "end": v(-46.63, -12.46) * mm});
            skLineSegment(sketch, "E2480", {"start": v(-46.63, -12.46) * mm, "end": v(-46.8, -12.5) * mm});
            skLineSegment(sketch, "E2481", {"start": v(-46.8, -12.5) * mm, "end": v(-46.96, -12.58) * mm});
            skLineSegment(sketch, "E2482", {"start": v(-46.96, -12.58) * mm, "end": v(-47.09, -12.7) * mm});
            skLineSegment(sketch, "E2483", {"start": v(-47.09, -12.7) * mm, "end": v(-47.19, -12.84) * mm});
            skLineSegment(sketch, "E2484", {"start": v(-47.19, -12.84) * mm, "end": v(-47.24, -13) * mm});
            skLineSegment(sketch, "E2485", {"start": v(-47.24, -13) * mm, "end": v(-47.25, -13.18) * mm});
            skLineSegment(sketch, "E2486", {"start": v(-47.25, -13.18) * mm, "end": v(-47.22, -13.35) * mm});
            skLineSegment(sketch, "E2487", {"start": v(-47.22, -13.35) * mm, "end": v(-47.14, -13.5) * mm});
            skLineSegment(sketch, "E2488", {"start": v(-47.14, -13.5) * mm, "end": v(-47.03, -13.63) * mm});
            skLineSegment(sketch, "E2489", {"start": v(-47.03, -13.63) * mm, "end": v(-46.88, -13.73) * mm});
            skLineSegment(sketch, "E2490", {"start": v(-46.88, -13.73) * mm, "end": v(-46.72, -13.78) * mm});
            skLineSegment(sketch, "E2491", {"start": v(-46.72, -13.78) * mm, "end": v(-46.54, -13.8) * mm});
            skLineSegment(sketch, "E2492", {"start": v(-46.54, -13.8) * mm, "end": v(-46.38, -13.76) * mm});
            skLineSegment(sketch, "E2493", {"start": v(-46.38, -13.76) * mm, "end": v(-46.22, -13.71) * mm});
            skLineSegment(sketch, "E2494", {"start": v(-46.22, -13.71) * mm, "end": v(-46.06, -13.66) * mm});
            skLineSegment(sketch, "E2495", {"start": v(-46.06, -13.66) * mm, "end": v(-45.9, -13.62) * mm});
            skLineSegment(sketch, "E2496", {"start": v(-45.9, -13.62) * mm, "end": v(-45.74, -13.57) * mm});
            skLineSegment(sketch, "E2497", {"start": v(-45.74, -13.57) * mm, "end": v(-45.58, -13.52) * mm});
            skLineSegment(sketch, "E2498", {"start": v(-45.58, -13.52) * mm, "end": v(-45.42, -13.47) * mm});
            skLineSegment(sketch, "E2499", {"start": v(-45.42, -13.47) * mm, "end": v(-45.26, -13.42) * mm});
            skLineSegment(sketch, "E2500", {"start": v(-45.26, -13.42) * mm, "end": v(-45.1, -13.37) * mm});
            skLineSegment(sketch, "E2501", {"start": v(-45.1, -13.37) * mm, "end": v(-44.94, -13.33) * mm});
            skLineSegment(sketch, "E2502", {"start": v(-44.94, -13.33) * mm, "end": v(-44.78, -13.28) * mm});
            skLineSegment(sketch, "E2503", {"start": v(-44.78, -13.28) * mm, "end": v(-44.61, -13.23) * mm});
            skLineSegment(sketch, "E2504", {"start": v(-44.61, -13.23) * mm, "end": v(-44.45, -13.18) * mm});
            skLineSegment(sketch, "E2505", {"start": v(-44.45, -13.18) * mm, "end": v(-44.34, -13.14) * mm});
            skLineSegment(sketch, "E2506", {"start": v(-44.34, -13.14) * mm, "end": v(-44.29, -13.3) * mm});
            skLineSegment(sketch, "E2507", {"start": v(-44.29, -13.3) * mm, "end": v(-44.24, -13.46) * mm});
            skLineSegment(sketch, "E2508", {"start": v(-44.24, -13.46) * mm, "end": v(-44.18, -13.62) * mm});
            skLineSegment(sketch, "E2509", {"start": v(-44.18, -13.62) * mm, "end": v(-44.13, -13.78) * mm});
            skLineSegment(sketch, "E2510", {"start": v(-44.13, -13.78) * mm, "end": v(-44.08, -13.94) * mm});
            skLineSegment(sketch, "E2511", {"start": v(-44.08, -13.94) * mm, "end": v(-44.03, -14.1) * mm});
            skLineSegment(sketch, "E2512", {"start": v(-44.03, -14.1) * mm, "end": v(-43.98, -14.25) * mm});
            skLineSegment(sketch, "E2513", {"start": v(-43.98, -14.25) * mm, "end": v(-43.93, -14.41) * mm});
            skLineSegment(sketch, "E2514", {"start": v(-43.93, -14.41) * mm, "end": v(-43.88, -14.57) * mm});
            skLineSegment(sketch, "E2515", {"start": v(-43.88, -14.57) * mm, "end": v(-43.82, -14.73) * mm});
            skLineSegment(sketch, "E2516", {"start": v(-43.82, -14.73) * mm, "end": v(-43.77, -14.89) * mm});
            skLineSegment(sketch, "E2517", {"start": v(-43.77, -14.89) * mm, "end": v(-43.75, -14.96) * mm});
            skLineSegment(sketch, "E2518", {"start": v(-43.75, -14.96) * mm, "end": v(-43.9, -15.02) * mm});
            skLineSegment(sketch, "E2519", {"start": v(-43.9, -15.02) * mm, "end": v(-44.06, -15.07) * mm});
            skLineSegment(sketch, "E2520", {"start": v(-44.06, -15.07) * mm, "end": v(-44.22, -15.13) * mm});
            skLineSegment(sketch, "E2521", {"start": v(-44.22, -15.13) * mm, "end": v(-44.38, -15.18) * mm});
            skLineSegment(sketch, "E2522", {"start": v(-44.38, -15.18) * mm, "end": v(-44.54, -15.24) * mm});
            skLineSegment(sketch, "E2523", {"start": v(-44.54, -15.24) * mm, "end": v(-44.7, -15.3) * mm});
            skLineSegment(sketch, "E2524", {"start": v(-44.7, -15.3) * mm, "end": v(-44.86, -15.35) * mm});
            skLineSegment(sketch, "E2525", {"start": v(-44.86, -15.35) * mm, "end": v(-45.01, -15.4) * mm});
            skLineSegment(sketch, "E2526", {"start": v(-45.01, -15.4) * mm, "end": v(-45.17, -15.46) * mm});
            skLineSegment(sketch, "E2527", {"start": v(-45.17, -15.46) * mm, "end": v(-45.33, -15.51) * mm});
            skLineSegment(sketch, "E2528", {"start": v(-45.33, -15.51) * mm, "end": v(-45.49, -15.57) * mm});
            skLineSegment(sketch, "E2529", {"start": v(-45.49, -15.57) * mm, "end": v(-45.65, -15.63) * mm});
            skLineSegment(sketch, "E2530", {"start": v(-45.65, -15.63) * mm, "end": v(-45.82, -15.69) * mm});
            skLineSegment(sketch, "E2531", {"start": v(-45.82, -15.69) * mm, "end": v(-45.97, -15.77) * mm});
            skLineSegment(sketch, "E2532", {"start": v(-45.97, -15.77) * mm, "end": v(-46.1, -15.9) * mm});
            skLineSegment(sketch, "E2533", {"start": v(-46.1, -15.9) * mm, "end": v(-46.18, -16.05) * mm});
            skLineSegment(sketch, "E2534", {"start": v(-46.18, -16.05) * mm, "end": v(-46.22, -16.21) * mm});
            skLineSegment(sketch, "E2535", {"start": v(-46.22, -16.21) * mm, "end": v(-46.22, -16.39) * mm});
            skLineSegment(sketch, "E2536", {"start": v(-46.22, -16.39) * mm, "end": v(-46.17, -16.55) * mm});
            skLineSegment(sketch, "E2537", {"start": v(-46.17, -16.55) * mm, "end": v(-46.09, -16.7) * mm});
            skLineSegment(sketch, "E2538", {"start": v(-46.09, -16.7) * mm, "end": v(-45.96, -16.83) * mm});
            skLineSegment(sketch, "E2539", {"start": v(-45.96, -16.83) * mm, "end": v(-45.81, -16.91) * mm});
            skLineSegment(sketch, "E2540", {"start": v(-45.81, -16.91) * mm, "end": v(-45.64, -16.95) * mm});
            skLineSegment(sketch, "E2541", {"start": v(-45.64, -16.95) * mm, "end": v(-45.47, -16.95) * mm});
            skLineSegment(sketch, "E2542", {"start": v(-45.47, -16.95) * mm, "end": v(-45.3, -16.9) * mm});
            skLineSegment(sketch, "E2543", {"start": v(-45.3, -16.9) * mm, "end": v(-45.15, -16.85) * mm});
            skLineSegment(sketch, "E2544", {"start": v(-45.15, -16.85) * mm, "end": v(-45, -16.79) * mm});
            skLineSegment(sketch, "E2545", {"start": v(-45, -16.79) * mm, "end": v(-44.84, -16.73) * mm});
            skLineSegment(sketch, "E2546", {"start": v(-44.84, -16.73) * mm, "end": v(-44.69, -16.67) * mm});
            skLineSegment(sketch, "E2547", {"start": v(-44.69, -16.67) * mm, "end": v(-44.53, -16.61) * mm});
            skLineSegment(sketch, "E2548", {"start": v(-44.53, -16.61) * mm, "end": v(-44.37, -16.55) * mm});
            skLineSegment(sketch, "E2549", {"start": v(-44.37, -16.55) * mm, "end": v(-44.22, -16.5) * mm});
            skLineSegment(sketch, "E2550", {"start": v(-44.22, -16.5) * mm, "end": v(-44.06, -16.43) * mm});
            skLineSegment(sketch, "E2551", {"start": v(-44.06, -16.43) * mm, "end": v(-43.9, -16.37) * mm});
            skLineSegment(sketch, "E2552", {"start": v(-43.9, -16.37) * mm, "end": v(-43.74, -16.31) * mm});
            skLineSegment(sketch, "E2553", {"start": v(-43.74, -16.31) * mm, "end": v(-43.58, -16.25) * mm});
            skLineSegment(sketch, "E2554", {"start": v(-43.58, -16.25) * mm, "end": v(-43.43, -16.2) * mm});
            skLineSegment(sketch, "E2555", {"start": v(-43.43, -16.2) * mm, "end": v(-43.31, -16.15) * mm});
            skLineSegment(sketch, "E2556", {"start": v(-43.31, -16.15) * mm, "end": v(-43.25, -16.3) * mm});
            skLineSegment(sketch, "E2557", {"start": v(-43.25, -16.3) * mm, "end": v(-43.2, -16.46) * mm});
            skLineSegment(sketch, "E2558", {"start": v(-43.2, -16.46) * mm, "end": v(-43.13, -16.61) * mm});
            skLineSegment(sketch, "E2559", {"start": v(-43.13, -16.61) * mm, "end": v(-43.07, -16.77) * mm});
            skLineSegment(sketch, "E2560", {"start": v(-43.07, -16.77) * mm, "end": v(-43, -16.92) * mm});
            skLineSegment(sketch, "E2561", {"start": v(-43, -16.92) * mm, "end": v(-42.94, -17.08) * mm});
            skLineSegment(sketch, "E2562", {"start": v(-42.94, -17.08) * mm, "end": v(-42.88, -17.23) * mm});
            skLineSegment(sketch, "E2563", {"start": v(-42.88, -17.23) * mm, "end": v(-42.82, -17.38) * mm});
            skLineSegment(sketch, "E2564", {"start": v(-42.82, -17.38) * mm, "end": v(-42.75, -17.54) * mm});
            skLineSegment(sketch, "E2565", {"start": v(-42.75, -17.54) * mm, "end": v(-42.7, -17.7) * mm});
            skLineSegment(sketch, "E2566", {"start": v(-42.7, -17.7) * mm, "end": v(-42.63, -17.85) * mm});
            skLineSegment(sketch, "E2567", {"start": v(-42.63, -17.85) * mm, "end": v(-42.6, -17.92) * mm});
            skLineSegment(sketch, "E2568", {"start": v(-42.6, -17.92) * mm, "end": v(-42.75, -17.99) * mm});
            skLineSegment(sketch, "E2569", {"start": v(-42.75, -17.99) * mm, "end": v(-42.9, -18.05) * mm});
            skLineSegment(sketch, "E2570", {"start": v(-42.9, -18.05) * mm, "end": v(-43.06, -18.12) * mm});
            skLineSegment(sketch, "E2571", {"start": v(-43.06, -18.12) * mm, "end": v(-43.21, -18.19) * mm});
            skLineSegment(sketch, "E2572", {"start": v(-43.21, -18.19) * mm, "end": v(-43.37, -18.25) * mm});
            skLineSegment(sketch, "E2573", {"start": v(-43.37, -18.25) * mm, "end": v(-43.53, -18.32) * mm});
            skLineSegment(sketch, "E2574", {"start": v(-43.53, -18.32) * mm, "end": v(-43.68, -18.38) * mm});
            skLineSegment(sketch, "E2575", {"start": v(-43.68, -18.38) * mm, "end": v(-43.83, -18.45) * mm});
            skLineSegment(sketch, "E2576", {"start": v(-43.83, -18.45) * mm, "end": v(-43.99, -18.52) * mm});
            skLineSegment(sketch, "E2577", {"start": v(-43.99, -18.52) * mm, "end": v(-44.14, -18.58) * mm});
            skLineSegment(sketch, "E2578", {"start": v(-44.14, -18.58) * mm, "end": v(-44.3, -18.65) * mm});
            skLineSegment(sketch, "E2579", {"start": v(-44.3, -18.65) * mm, "end": v(-44.45, -18.72) * mm});
            skLineSegment(sketch, "E2580", {"start": v(-44.45, -18.72) * mm, "end": v(-44.62, -18.79) * mm});
            skLineSegment(sketch, "E2581", {"start": v(-44.62, -18.79) * mm, "end": v(-44.76, -18.89) * mm});
            skLineSegment(sketch, "E2582", {"start": v(-44.76, -18.89) * mm, "end": v(-44.87, -19.02) * mm});
            skLineSegment(sketch, "E2583", {"start": v(-44.87, -19.02) * mm, "end": v(-44.95, -19.17) * mm});
            skLineSegment(sketch, "E2584", {"start": v(-44.95, -19.17) * mm, "end": v(-44.98, -19.34) * mm});
            skLineSegment(sketch, "E2585", {"start": v(-44.98, -19.34) * mm, "end": v(-44.97, -19.52) * mm});
            skLineSegment(sketch, "E2586", {"start": v(-44.97, -19.52) * mm, "end": v(-44.9, -19.68) * mm});
            skLineSegment(sketch, "E2587", {"start": v(-44.9, -19.68) * mm, "end": v(-44.8, -19.82) * mm});
            skLineSegment(sketch, "E2588", {"start": v(-44.8, -19.82) * mm, "end": v(-44.68, -19.94) * mm});
            skLineSegment(sketch, "E2589", {"start": v(-44.68, -19.94) * mm, "end": v(-44.52, -20.01) * mm});
            skLineSegment(sketch, "E2590", {"start": v(-44.52, -20.01) * mm, "end": v(-44.35, -20.04) * mm});
            skLineSegment(sketch, "E2591", {"start": v(-44.35, -20.04) * mm, "end": v(-44.18, -20.03) * mm});
            skLineSegment(sketch, "E2592", {"start": v(-44.18, -20.03) * mm, "end": v(-44.02, -19.97) * mm});
            skLineSegment(sketch, "E2593", {"start": v(-44.02, -19.97) * mm, "end": v(-43.87, -19.9) * mm});
            skLineSegment(sketch, "E2594", {"start": v(-43.87, -19.9) * mm, "end": v(-43.72, -19.83) * mm});
            skLineSegment(sketch, "E2595", {"start": v(-43.72, -19.83) * mm, "end": v(-43.57, -19.76) * mm});
            skLineSegment(sketch, "E2596", {"start": v(-43.57, -19.76) * mm, "end": v(-43.42, -19.7) * mm});
            skLineSegment(sketch, "E2597", {"start": v(-43.42, -19.7) * mm, "end": v(-43.26, -19.62) * mm});
            skLineSegment(sketch, "E2598", {"start": v(-43.26, -19.62) * mm, "end": v(-43.1, -19.55) * mm});
            skLineSegment(sketch, "E2599", {"start": v(-43.1, -19.55) * mm, "end": v(-42.96, -19.48) * mm});
            skLineSegment(sketch, "E2600", {"start": v(-42.96, -19.48) * mm, "end": v(-42.8, -19.4) * mm});
            skLineSegment(sketch, "E2601", {"start": v(-42.8, -19.4) * mm, "end": v(-42.65, -19.34) * mm});
            skLineSegment(sketch, "E2602", {"start": v(-42.65, -19.34) * mm, "end": v(-42.5, -19.27) * mm});
            skLineSegment(sketch, "E2603", {"start": v(-42.5, -19.27) * mm, "end": v(-42.35, -19.2) * mm});
            skLineSegment(sketch, "E2604", {"start": v(-42.35, -19.2) * mm, "end": v(-42.2, -19.13) * mm});
            skLineSegment(sketch, "E2605", {"start": v(-42.2, -19.13) * mm, "end": v(-42.08, -19.08) * mm});
            skLineSegment(sketch, "E2606", {"start": v(-42.08, -19.08) * mm, "end": v(-42.01, -19.23) * mm});
            skLineSegment(sketch, "E2607", {"start": v(-42.01, -19.23) * mm, "end": v(-41.94, -19.38) * mm});
            skLineSegment(sketch, "E2608", {"start": v(-41.94, -19.38) * mm, "end": v(-41.87, -19.53) * mm});
            skLineSegment(sketch, "E2609", {"start": v(-41.87, -19.53) * mm, "end": v(-41.8, -19.68) * mm});
            skLineSegment(sketch, "E2610", {"start": v(-41.8, -19.68) * mm, "end": v(-41.72, -19.82) * mm});
            skLineSegment(sketch, "E2611", {"start": v(-41.72, -19.82) * mm, "end": v(-41.65, -19.97) * mm});
            skLineSegment(sketch, "E2612", {"start": v(-41.65, -19.97) * mm, "end": v(-41.57, -20.12) * mm});
            skLineSegment(sketch, "E2613", {"start": v(-41.57, -20.12) * mm, "end": v(-41.5, -20.27) * mm});
            skLineSegment(sketch, "E2614", {"start": v(-41.5, -20.27) * mm, "end": v(-41.43, -20.42) * mm});
            skLineSegment(sketch, "E2615", {"start": v(-41.43, -20.42) * mm, "end": v(-41.36, -20.57) * mm});
            skLineSegment(sketch, "E2616", {"start": v(-41.36, -20.57) * mm, "end": v(-41.28, -20.72) * mm});
            skLineSegment(sketch, "E2617", {"start": v(-41.28, -20.72) * mm, "end": v(-41.25, -20.8) * mm});
            skLineSegment(sketch, "E2618", {"start": v(-41.25, -20.8) * mm, "end": v(-41.4, -20.87) * mm});
            skLineSegment(sketch, "E2619", {"start": v(-41.4, -20.87) * mm, "end": v(-41.54, -20.95) * mm});
            skLineSegment(sketch, "E2620", {"start": v(-41.54, -20.95) * mm, "end": v(-41.7, -21.03) * mm});
            skLineSegment(sketch, "E2621", {"start": v(-41.7, -21.03) * mm, "end": v(-41.84, -21.1) * mm});
            skLineSegment(sketch, "E2622", {"start": v(-41.84, -21.1) * mm, "end": v(-42, -21.18) * mm});
            skLineSegment(sketch, "E2623", {"start": v(-42, -21.18) * mm, "end": v(-42.14, -21.26) * mm});
            skLineSegment(sketch, "E2624", {"start": v(-42.14, -21.26) * mm, "end": v(-42.3, -21.33) * mm});
            skLineSegment(sketch, "E2625", {"start": v(-42.3, -21.33) * mm, "end": v(-42.44, -21.4) * mm});
            skLineSegment(sketch, "E2626", {"start": v(-42.44, -21.4) * mm, "end": v(-42.6, -21.49) * mm});
            skLineSegment(sketch, "E2627", {"start": v(-42.6, -21.49) * mm, "end": v(-42.74, -21.56) * mm});
            skLineSegment(sketch, "E2628", {"start": v(-42.74, -21.56) * mm, "end": v(-42.89, -21.64) * mm});
            skLineSegment(sketch, "E2629", {"start": v(-42.89, -21.64) * mm, "end": v(-43.04, -21.72) * mm});
            skLineSegment(sketch, "E2630", {"start": v(-43.04, -21.72) * mm, "end": v(-43.2, -21.8) * mm});
            skLineSegment(sketch, "E2631", {"start": v(-43.2, -21.8) * mm, "end": v(-43.33, -21.9) * mm});
            skLineSegment(sketch, "E2632", {"start": v(-43.33, -21.9) * mm, "end": v(-43.44, -22.05) * mm});
            skLineSegment(sketch, "E2633", {"start": v(-43.44, -22.05) * mm, "end": v(-43.5, -22.2) * mm});
            skLineSegment(sketch, "E2634", {"start": v(-43.5, -22.2) * mm, "end": v(-43.52, -22.38) * mm});
            skLineSegment(sketch, "E2635", {"start": v(-43.52, -22.38) * mm, "end": v(-43.5, -22.55) * mm});
            skLineSegment(sketch, "E2636", {"start": v(-43.5, -22.55) * mm, "end": v(-43.43, -22.7) * mm});
            skLineSegment(sketch, "E2637", {"start": v(-43.43, -22.7) * mm, "end": v(-43.32, -22.85) * mm});
            skLineSegment(sketch, "E2638", {"start": v(-43.32, -22.85) * mm, "end": v(-43.18, -22.95) * mm});
            skLineSegment(sketch, "E2639", {"start": v(-43.18, -22.95) * mm, "end": v(-43.02, -23.01) * mm});
            skLineSegment(sketch, "E2640", {"start": v(-43.02, -23.01) * mm, "end": v(-42.85, -23.03) * mm});
            skLineSegment(sketch, "E2641", {"start": v(-42.85, -23.03) * mm, "end": v(-42.67, -23) * mm});
            skLineSegment(sketch, "E2642", {"start": v(-42.67, -23) * mm, "end": v(-42.52, -22.94) * mm});
            skLineSegment(sketch, "E2643", {"start": v(-42.52, -22.94) * mm, "end": v(-42.38, -22.86) * mm});
            skLineSegment(sketch, "E2644", {"start": v(-42.38, -22.86) * mm, "end": v(-42.23, -22.78) * mm});
            skLineSegment(sketch, "E2645", {"start": v(-42.23, -22.78) * mm, "end": v(-42.08, -22.7) * mm});
            skLineSegment(sketch, "E2646", {"start": v(-42.08, -22.7) * mm, "end": v(-41.94, -22.62) * mm});
            skLineSegment(sketch, "E2647", {"start": v(-41.94, -22.62) * mm, "end": v(-41.79, -22.54) * mm});
            skLineSegment(sketch, "E2648", {"start": v(-41.79, -22.54) * mm, "end": v(-41.64, -22.46) * mm});
            skLineSegment(sketch, "E2649", {"start": v(-41.64, -22.46) * mm, "end": v(-41.5, -22.38) * mm});
            skLineSegment(sketch, "E2650", {"start": v(-41.5, -22.38) * mm, "end": v(-41.35, -22.3) * mm});
            skLineSegment(sketch, "E2651", {"start": v(-41.35, -22.3) * mm, "end": v(-41.2, -22.21) * mm});
            skLineSegment(sketch, "E2652", {"start": v(-41.2, -22.21) * mm, "end": v(-41.06, -22.13) * mm});
            skLineSegment(sketch, "E2653", {"start": v(-41.06, -22.13) * mm, "end": v(-40.9, -22.05) * mm});
            skLineSegment(sketch, "E2654", {"start": v(-40.9, -22.05) * mm, "end": v(-40.76, -21.97) * mm});
            skLineSegment(sketch, "E2655", {"start": v(-40.76, -21.97) * mm, "end": v(-40.65, -21.91) * mm});
            skLineSegment(sketch, "E2656", {"start": v(-40.65, -21.91) * mm, "end": v(-40.57, -22.06) * mm});
            skLineSegment(sketch, "E2657", {"start": v(-40.57, -22.06) * mm, "end": v(-40.49, -22.2) * mm});
            skLineSegment(sketch, "E2658", {"start": v(-40.49, -22.2) * mm, "end": v(-40.4, -22.34) * mm});
            skLineSegment(sketch, "E2659", {"start": v(-40.4, -22.34) * mm, "end": v(-40.32, -22.49) * mm});
            skLineSegment(sketch, "E2660", {"start": v(-40.32, -22.49) * mm, "end": v(-40.24, -22.63) * mm});
            skLineSegment(sketch, "E2661", {"start": v(-40.24, -22.63) * mm, "end": v(-40.15, -22.78) * mm});
            skLineSegment(sketch, "E2662", {"start": v(-40.15, -22.78) * mm, "end": v(-40.07, -22.92) * mm});
            skLineSegment(sketch, "E2663", {"start": v(-40.07, -22.92) * mm, "end": v(-39.99, -23.06) * mm});
            skLineSegment(sketch, "E2664", {"start": v(-39.99, -23.06) * mm, "end": v(-39.9, -23.2) * mm});
            skLineSegment(sketch, "E2665", {"start": v(-39.9, -23.2) * mm, "end": v(-39.82, -23.35) * mm});
            skLineSegment(sketch, "E2666", {"start": v(-39.82, -23.35) * mm, "end": v(-39.74, -23.5) * mm});
            skLineSegment(sketch, "E2667", {"start": v(-39.74, -23.5) * mm, "end": v(-39.7, -23.57) * mm});
            skLineSegment(sketch, "E2668", {"start": v(-39.7, -23.57) * mm, "end": v(-39.84, -23.65) * mm});
            skLineSegment(sketch, "E2669", {"start": v(-39.84, -23.65) * mm, "end": v(-39.98, -23.74) * mm});
            skLineSegment(sketch, "E2670", {"start": v(-39.98, -23.74) * mm, "end": v(-40.13, -23.83) * mm});
            skLineSegment(sketch, "E2671", {"start": v(-40.13, -23.83) * mm, "end": v(-40.27, -23.91) * mm});
            skLineSegment(sketch, "E2672", {"start": v(-40.27, -23.91) * mm, "end": v(-40.41, -24) * mm});
            skLineSegment(sketch, "E2673", {"start": v(-40.41, -24) * mm, "end": v(-40.56, -24.09) * mm});
            skLineSegment(sketch, "E2674", {"start": v(-40.56, -24.09) * mm, "end": v(-40.7, -24.17) * mm});
            skLineSegment(sketch, "E2675", {"start": v(-40.7, -24.17) * mm, "end": v(-40.84, -24.26) * mm});
            skLineSegment(sketch, "E2676", {"start": v(-40.84, -24.26) * mm, "end": v(-41, -24.35) * mm});
            skLineSegment(sketch, "E2677", {"start": v(-41, -24.35) * mm, "end": v(-41.13, -24.44) * mm});
            skLineSegment(sketch, "E2678", {"start": v(-41.13, -24.44) * mm, "end": v(-41.28, -24.52) * mm});
            skLineSegment(sketch, "E2679", {"start": v(-41.28, -24.52) * mm, "end": v(-41.42, -24.61) * mm});
            skLineSegment(sketch, "E2680", {"start": v(-41.42, -24.61) * mm, "end": v(-41.57, -24.7) * mm});
            skLineSegment(sketch, "E2681", {"start": v(-41.57, -24.7) * mm, "end": v(-41.7, -24.82) * mm});
            skLineSegment(sketch, "E2682", {"start": v(-41.7, -24.82) * mm, "end": v(-41.8, -24.97) * mm});
            skLineSegment(sketch, "E2683", {"start": v(-41.8, -24.97) * mm, "end": v(-41.85, -25.13) * mm});
            skLineSegment(sketch, "E2684", {"start": v(-41.85, -25.13) * mm, "end": v(-41.86, -25.3) * mm});
            skLineSegment(sketch, "E2685", {"start": v(-41.86, -25.3) * mm, "end": v(-41.82, -25.47) * mm});
            skLineSegment(sketch, "E2686", {"start": v(-41.82, -25.47) * mm, "end": v(-41.74, -25.63) * mm});
            skLineSegment(sketch, "E2687", {"start": v(-41.74, -25.63) * mm, "end": v(-41.62, -25.76) * mm});
            skLineSegment(sketch, "E2688", {"start": v(-41.62, -25.76) * mm, "end": v(-41.48, -25.85) * mm});
            skLineSegment(sketch, "E2689", {"start": v(-41.48, -25.85) * mm, "end": v(-41.31, -25.9) * mm});
            skLineSegment(sketch, "E2690", {"start": v(-41.31, -25.9) * mm, "end": v(-41.14, -25.9) * mm});
            skLineSegment(sketch, "E2691", {"start": v(-41.14, -25.9) * mm, "end": v(-40.97, -25.87) * mm});
            skLineSegment(sketch, "E2692", {"start": v(-40.97, -25.87) * mm, "end": v(-40.82, -25.8) * mm});
            skLineSegment(sketch, "E2693", {"start": v(-40.82, -25.8) * mm, "end": v(-40.68, -25.7) * mm});
            skLineSegment(sketch, "E2694", {"start": v(-40.68, -25.7) * mm, "end": v(-40.54, -25.61) * mm});
            skLineSegment(sketch, "E2695", {"start": v(-40.54, -25.61) * mm, "end": v(-40.4, -25.52) * mm});
            skLineSegment(sketch, "E2696", {"start": v(-40.4, -25.52) * mm, "end": v(-40.26, -25.43) * mm});
            skLineSegment(sketch, "E2697", {"start": v(-40.26, -25.43) * mm, "end": v(-40.12, -25.34) * mm});
            skLineSegment(sketch, "E2698", {"start": v(-40.12, -25.34) * mm, "end": v(-39.98, -25.25) * mm});
            skLineSegment(sketch, "E2699", {"start": v(-39.98, -25.25) * mm, "end": v(-39.84, -25.16) * mm});
            skLineSegment(sketch, "E2700", {"start": v(-39.84, -25.16) * mm, "end": v(-39.7, -25.07) * mm});
            skLineSegment(sketch, "E2701", {"start": v(-39.7, -25.07) * mm, "end": v(-39.55, -24.98) * mm});
            skLineSegment(sketch, "E2702", {"start": v(-39.55, -24.98) * mm, "end": v(-39.41, -24.89) * mm});
            skLineSegment(sketch, "E2703", {"start": v(-39.41, -24.89) * mm, "end": v(-39.27, -24.8) * mm});
            skLineSegment(sketch, "E2704", {"start": v(-39.27, -24.8) * mm, "end": v(-39.13, -24.7) * mm});
            skLineSegment(sketch, "E2705", {"start": v(-39.13, -24.7) * mm, "end": v(-39.03, -24.64) * mm});
            skLineSegment(sketch, "E2706", {"start": v(-39.03, -24.64) * mm, "end": v(-38.93, -24.78) * mm});
            skLineSegment(sketch, "E2707", {"start": v(-38.93, -24.78) * mm, "end": v(-38.84, -24.91) * mm});
            skLineSegment(sketch, "E2708", {"start": v(-38.84, -24.91) * mm, "end": v(-38.75, -25.05) * mm});
            skLineSegment(sketch, "E2709", {"start": v(-38.75, -25.05) * mm, "end": v(-38.66, -25.2) * mm});
            skLineSegment(sketch, "E2710", {"start": v(-38.66, -25.2) * mm, "end": v(-38.56, -25.33) * mm});
            skLineSegment(sketch, "E2711", {"start": v(-38.56, -25.33) * mm, "end": v(-38.47, -25.47) * mm});
            skLineSegment(sketch, "E2712", {"start": v(-38.47, -25.47) * mm, "end": v(-38.38, -25.6) * mm});
            skLineSegment(sketch, "E2713", {"start": v(-38.38, -25.6) * mm, "end": v(-38.28, -25.74) * mm});
            skLineSegment(sketch, "E2714", {"start": v(-38.28, -25.74) * mm, "end": v(-38.2, -25.88) * mm});
            skLineSegment(sketch, "E2715", {"start": v(-38.2, -25.88) * mm, "end": v(-38.1, -26.02) * mm});
            skLineSegment(sketch, "E2716", {"start": v(-38.1, -26.02) * mm, "end": v(-38, -26.16) * mm});
            skLineSegment(sketch, "E2717", {"start": v(-38, -26.16) * mm, "end": v(-37.96, -26.22) * mm});
            skLineSegment(sketch, "E2718", {"start": v(-37.96, -26.22) * mm, "end": v(-38.1, -26.32) * mm});
            skLineSegment(sketch, "E2719", {"start": v(-38.1, -26.32) * mm, "end": v(-38.23, -26.41) * mm});
            skLineSegment(sketch, "E2720", {"start": v(-38.23, -26.41) * mm, "end": v(-38.37, -26.51) * mm});
            skLineSegment(sketch, "E2721", {"start": v(-38.37, -26.51) * mm, "end": v(-38.5, -26.6) * mm});
            skLineSegment(sketch, "E2722", {"start": v(-38.5, -26.6) * mm, "end": v(-38.64, -26.7) * mm});
            skLineSegment(sketch, "E2723", {"start": v(-38.64, -26.7) * mm, "end": v(-38.78, -26.8) * mm});
            skLineSegment(sketch, "E2724", {"start": v(-38.78, -26.8) * mm, "end": v(-38.92, -26.9) * mm});
            skLineSegment(sketch, "E2725", {"start": v(-38.92, -26.9) * mm, "end": v(-39.05, -27) * mm});
            skLineSegment(sketch, "E2726", {"start": v(-39.05, -27) * mm, "end": v(-39.2, -27.1) * mm});
            skLineSegment(sketch, "E2727", {"start": v(-39.2, -27.1) * mm, "end": v(-39.33, -27.2) * mm});
            skLineSegment(sketch, "E2728", {"start": v(-39.33, -27.2) * mm, "end": v(-39.47, -27.29) * mm});
            skLineSegment(sketch, "E2729", {"start": v(-39.47, -27.29) * mm, "end": v(-39.6, -27.38) * mm});
            skLineSegment(sketch, "E2730", {"start": v(-39.6, -27.38) * mm, "end": v(-39.75, -27.49) * mm});
            skLineSegment(sketch, "E2731", {"start": v(-39.75, -27.49) * mm, "end": v(-39.87, -27.61) * mm});
            skLineSegment(sketch, "E2732", {"start": v(-39.87, -27.61) * mm, "end": v(-39.96, -27.77) * mm});
            skLineSegment(sketch, "E2733", {"start": v(-39.96, -27.77) * mm, "end": v(-40, -27.93) * mm});
            skLineSegment(sketch, "E2734", {"start": v(-40, -27.93) * mm, "end": v(-40, -28.1) * mm});
            skLineSegment(sketch, "E2735", {"start": v(-40, -28.1) * mm, "end": v(-39.94, -28.27) * mm});
            skLineSegment(sketch, "E2736", {"start": v(-39.94, -28.27) * mm, "end": v(-39.85, -28.42) * mm});
            skLineSegment(sketch, "E2737", {"start": v(-39.85, -28.42) * mm, "end": v(-39.73, -28.54) * mm});
            skLineSegment(sketch, "E2738", {"start": v(-39.73, -28.54) * mm, "end": v(-39.57, -28.62) * mm});
            skLineSegment(sketch, "E2739", {"start": v(-39.57, -28.62) * mm, "end": v(-39.4, -28.66) * mm});
            skLineSegment(sketch, "E2740", {"start": v(-39.4, -28.66) * mm, "end": v(-39.23, -28.66) * mm});
            skLineSegment(sketch, "E2741", {"start": v(-39.23, -28.66) * mm, "end": v(-39.07, -28.6) * mm});
            skLineSegment(sketch, "E2742", {"start": v(-39.07, -28.6) * mm, "end": v(-38.92, -28.52) * mm});
            skLineSegment(sketch, "E2743", {"start": v(-38.92, -28.52) * mm, "end": v(-38.8, -28.42) * mm});
            skLineSegment(sketch, "E2744", {"start": v(-38.8, -28.42) * mm, "end": v(-38.66, -28.32) * mm});
            skLineSegment(sketch, "E2745", {"start": v(-38.66, -28.32) * mm, "end": v(-38.52, -28.22) * mm});
            skLineSegment(sketch, "E2746", {"start": v(-38.52, -28.22) * mm, "end": v(-38.4, -28.12) * mm});
            skLineSegment(sketch, "E2747", {"start": v(-38.4, -28.12) * mm, "end": v(-38.25, -28.02) * mm});
            skLineSegment(sketch, "E2748", {"start": v(-38.25, -28.02) * mm, "end": v(-38.12, -27.92) * mm});
            skLineSegment(sketch, "E2749", {"start": v(-38.12, -27.92) * mm, "end": v(-37.99, -27.82) * mm});
            skLineSegment(sketch, "E2750", {"start": v(-37.99, -27.82) * mm, "end": v(-37.85, -27.72) * mm});
            skLineSegment(sketch, "E2751", {"start": v(-37.85, -27.72) * mm, "end": v(-37.72, -27.62) * mm});
            skLineSegment(sketch, "E2752", {"start": v(-37.72, -27.62) * mm, "end": v(-37.58, -27.52) * mm});
            skLineSegment(sketch, "E2753", {"start": v(-37.58, -27.52) * mm, "end": v(-37.45, -27.42) * mm});
            skLineSegment(sketch, "E2754", {"start": v(-37.45, -27.42) * mm, "end": v(-37.31, -27.32) * mm});
            skLineSegment(sketch, "E2755", {"start": v(-37.31, -27.32) * mm, "end": v(-37.22, -27.25) * mm});
            skLineSegment(sketch, "E2756", {"start": v(-37.22, -27.25) * mm, "end": v(-37.11, -27.38) * mm});
            skLineSegment(sketch, "E2757", {"start": v(-37.11, -27.38) * mm, "end": v(-37.01, -27.5) * mm});
            skLineSegment(sketch, "E2758", {"start": v(-37.01, -27.5) * mm, "end": v(-36.9, -27.64) * mm});
            skLineSegment(sketch, "E2759", {"start": v(-36.9, -27.64) * mm, "end": v(-36.8, -27.77) * mm});
            skLineSegment(sketch, "E2760", {"start": v(-36.8, -27.77) * mm, "end": v(-36.7, -27.9) * mm});
            skLineSegment(sketch, "E2761", {"start": v(-36.7, -27.9) * mm, "end": v(-36.6, -28.03) * mm});
            skLineSegment(sketch, "E2762", {"start": v(-36.6, -28.03) * mm, "end": v(-36.5, -28.16) * mm});
            skLineSegment(sketch, "E2763", {"start": v(-36.5, -28.16) * mm, "end": v(-36.4, -28.3) * mm});
            skLineSegment(sketch, "E2764", {"start": v(-36.4, -28.3) * mm, "end": v(-36.3, -28.43) * mm});
            skLineSegment(sketch, "E2765", {"start": v(-36.3, -28.43) * mm, "end": v(-36.2, -28.56) * mm});
            skLineSegment(sketch, "E2766", {"start": v(-36.2, -28.56) * mm, "end": v(-36.09, -28.69) * mm});
            skLineSegment(sketch, "E2767", {"start": v(-36.09, -28.69) * mm, "end": v(-36.04, -28.75) * mm});
            skLineSegment(sketch, "E2768", {"start": v(-36.04, -28.75) * mm, "end": v(-36.17, -28.86) * mm});
            skLineSegment(sketch, "E2769", {"start": v(-36.17, -28.86) * mm, "end": v(-36.3, -28.96) * mm});
            skLineSegment(sketch, "E2770", {"start": v(-36.3, -28.96) * mm, "end": v(-36.43, -29.07) * mm});
            skLineSegment(sketch, "E2771", {"start": v(-36.43, -29.07) * mm, "end": v(-36.56, -29.18) * mm});
            skLineSegment(sketch, "E2772", {"start": v(-36.56, -29.18) * mm, "end": v(-36.69, -29.28) * mm});
            skLineSegment(sketch, "E2773", {"start": v(-36.69, -29.28) * mm, "end": v(-36.82, -29.39) * mm});
            skLineSegment(sketch, "E2774", {"start": v(-36.82, -29.39) * mm, "end": v(-36.95, -29.5) * mm});
            skLineSegment(sketch, "E2775", {"start": v(-36.95, -29.5) * mm, "end": v(-37.08, -29.6) * mm});
            skLineSegment(sketch, "E2776", {"start": v(-37.08, -29.6) * mm, "end": v(-37.21, -29.7) * mm});
            skLineSegment(sketch, "E2777", {"start": v(-37.21, -29.7) * mm, "end": v(-37.34, -29.81) * mm});
            skLineSegment(sketch, "E2778", {"start": v(-37.34, -29.81) * mm, "end": v(-37.47, -29.92) * mm});
            skLineSegment(sketch, "E2779", {"start": v(-37.47, -29.92) * mm, "end": v(-37.6, -30.03) * mm});
            skLineSegment(sketch, "E2780", {"start": v(-37.6, -30.03) * mm, "end": v(-37.74, -30.14) * mm});
            skLineSegment(sketch, "E2781", {"start": v(-37.74, -30.14) * mm, "end": v(-37.85, -30.27) * mm});
            skLineSegment(sketch, "E2782", {"start": v(-37.85, -30.27) * mm, "end": v(-37.92, -30.43) * mm});
            skLineSegment(sketch, "E2783", {"start": v(-37.92, -30.43) * mm, "end": v(-37.95, -30.6) * mm});
            skLineSegment(sketch, "E2784", {"start": v(-37.95, -30.6) * mm, "end": v(-37.94, -30.77) * mm});
            skLineSegment(sketch, "E2785", {"start": v(-37.94, -30.77) * mm, "end": v(-37.88, -30.94) * mm});
            skLineSegment(sketch, "E2786", {"start": v(-37.88, -30.94) * mm, "end": v(-37.77, -31.08) * mm});
            skLineSegment(sketch, "E2787", {"start": v(-37.77, -31.08) * mm, "end": v(-37.64, -31.19) * mm});
            skLineSegment(sketch, "E2788", {"start": v(-37.64, -31.19) * mm, "end": v(-37.48, -31.26) * mm});
            skLineSegment(sketch, "E2789", {"start": v(-37.48, -31.26) * mm, "end": v(-37.31, -31.29) * mm});
            skLineSegment(sketch, "E2790", {"start": v(-37.31, -31.29) * mm, "end": v(-37.14, -31.27) * mm});
            skLineSegment(sketch, "E2791", {"start": v(-37.14, -31.27) * mm, "end": v(-36.98, -31.2) * mm});
            skLineSegment(sketch, "E2792", {"start": v(-36.98, -31.2) * mm, "end": v(-36.84, -31.11) * mm});
            skLineSegment(sketch, "E2793", {"start": v(-36.84, -31.11) * mm, "end": v(-36.71, -31) * mm});
            skLineSegment(sketch, "E2794", {"start": v(-36.71, -31) * mm, "end": v(-36.59, -30.9) * mm});
            skLineSegment(sketch, "E2795", {"start": v(-36.59, -30.9) * mm, "end": v(-36.46, -30.79) * mm});
            skLineSegment(sketch, "E2796", {"start": v(-36.46, -30.79) * mm, "end": v(-36.34, -30.68) * mm});
            skLineSegment(sketch, "E2797", {"start": v(-36.34, -30.68) * mm, "end": v(-36.2, -30.57) * mm});
            skLineSegment(sketch, "E2798", {"start": v(-36.2, -30.57) * mm, "end": v(-36.08, -30.46) * mm});
            skLineSegment(sketch, "E2799", {"start": v(-36.08, -30.46) * mm, "end": v(-35.96, -30.35) * mm});
            skLineSegment(sketch, "E2800", {"start": v(-35.96, -30.35) * mm, "end": v(-35.83, -30.24) * mm});
            skLineSegment(sketch, "E2801", {"start": v(-35.83, -30.24) * mm, "end": v(-35.7, -30.13) * mm});
            skLineSegment(sketch, "E2802", {"start": v(-35.7, -30.13) * mm, "end": v(-35.57, -30.02) * mm});
            skLineSegment(sketch, "E2803", {"start": v(-35.57, -30.02) * mm, "end": v(-35.44, -29.9) * mm});
            skLineSegment(sketch, "E2804", {"start": v(-35.44, -29.9) * mm, "end": v(-35.32, -29.8) * mm});
            skLineSegment(sketch, "E2805", {"start": v(-35.32, -29.8) * mm, "end": v(-35.23, -29.72) * mm});
            skLineSegment(sketch, "E2806", {"start": v(-35.23, -29.72) * mm, "end": v(-35.12, -29.84) * mm});
            skLineSegment(sketch, "E2807", {"start": v(-35.12, -29.84) * mm, "end": v(-35, -29.97) * mm});
            skLineSegment(sketch, "E2808", {"start": v(-35, -29.97) * mm, "end": v(-34.9, -30.1) * mm});
            skLineSegment(sketch, "E2809", {"start": v(-34.9, -30.1) * mm, "end": v(-34.78, -30.21) * mm});
            skLineSegment(sketch, "E2810", {"start": v(-34.78, -30.21) * mm, "end": v(-34.67, -30.34) * mm});
            skLineSegment(sketch, "E2811", {"start": v(-34.67, -30.34) * mm, "end": v(-34.56, -30.46) * mm});
            skLineSegment(sketch, "E2812", {"start": v(-34.56, -30.46) * mm, "end": v(-34.45, -30.59) * mm});
            skLineSegment(sketch, "E2813", {"start": v(-34.45, -30.59) * mm, "end": v(-34.34, -30.7) * mm});
            skLineSegment(sketch, "E2814", {"start": v(-34.34, -30.7) * mm, "end": v(-34.22, -30.83) * mm});
            skLineSegment(sketch, "E2815", {"start": v(-34.22, -30.83) * mm, "end": v(-34.11, -30.96) * mm});
            skLineSegment(sketch, "E2816", {"start": v(-34.11, -30.96) * mm, "end": v(-34, -31.08) * mm});
            skLineSegment(sketch, "E2817", {"start": v(-34, -31.08) * mm, "end": v(-33.95, -31.14) * mm});
            skLineSegment(sketch, "E2818", {"start": v(-33.95, -31.14) * mm, "end": v(-34.07, -31.25) * mm});
            skLineSegment(sketch, "E2819", {"start": v(-34.07, -31.25) * mm, "end": v(-34.2, -31.37) * mm});
            skLineSegment(sketch, "E2820", {"start": v(-34.2, -31.37) * mm, "end": v(-34.32, -31.49) * mm});
            skLineSegment(sketch, "E2821", {"start": v(-34.32, -31.49) * mm, "end": v(-34.44, -31.6) * mm});
            skLineSegment(sketch, "E2822", {"start": v(-34.44, -31.6) * mm, "end": v(-34.56, -31.71) * mm});
            skLineSegment(sketch, "E2823", {"start": v(-34.56, -31.71) * mm, "end": v(-34.68, -31.83) * mm});
            skLineSegment(sketch, "E2824", {"start": v(-34.68, -31.83) * mm, "end": v(-34.8, -31.94) * mm});
            skLineSegment(sketch, "E2825", {"start": v(-34.8, -31.94) * mm, "end": v(-34.92, -32.06) * mm});
            skLineSegment(sketch, "E2826", {"start": v(-34.92, -32.06) * mm, "end": v(-35.05, -32.18) * mm});
            skLineSegment(sketch, "E2827", {"start": v(-35.05, -32.18) * mm, "end": v(-35.17, -32.29) * mm});
            skLineSegment(sketch, "E2828", {"start": v(-35.17, -32.29) * mm, "end": v(-35.3, -32.4) * mm});
            skLineSegment(sketch, "E2829", {"start": v(-35.3, -32.4) * mm, "end": v(-35.42, -32.52) * mm});
            skLineSegment(sketch, "E2830", {"start": v(-35.42, -32.52) * mm, "end": v(-35.55, -32.64) * mm});
            skLineSegment(sketch, "E2831", {"start": v(-35.55, -32.64) * mm, "end": v(-35.65, -32.78) * mm});
            skLineSegment(sketch, "E2832", {"start": v(-35.65, -32.78) * mm, "end": v(-35.7, -32.95) * mm});
            skLineSegment(sketch, "E2833", {"start": v(-35.7, -32.95) * mm, "end": v(-35.73, -33.12) * mm});
            skLineSegment(sketch, "E2834", {"start": v(-35.73, -33.12) * mm, "end": v(-35.7, -33.3) * mm});
            skLineSegment(sketch, "E2835", {"start": v(-35.7, -33.3) * mm, "end": v(-35.63, -33.45) * mm});
            skLineSegment(sketch, "E2836", {"start": v(-35.63, -33.45) * mm, "end": v(-35.52, -33.58) * mm});
            skLineSegment(sketch, "E2837", {"start": v(-35.52, -33.58) * mm, "end": v(-35.38, -33.68) * mm});
            skLineSegment(sketch, "E2838", {"start": v(-35.38, -33.68) * mm, "end": v(-35.21, -33.74) * mm});
            skLineSegment(sketch, "E2839", {"start": v(-35.21, -33.74) * mm, "end": v(-35.04, -33.76) * mm});
            skLineSegment(sketch, "E2840", {"start": v(-35.04, -33.76) * mm, "end": v(-34.87, -33.73) * mm});
            skLineSegment(sketch, "E2841", {"start": v(-34.87, -33.73) * mm, "end": v(-34.71, -33.66) * mm});
            skLineSegment(sketch, "E2842", {"start": v(-34.71, -33.66) * mm, "end": v(-34.58, -33.55) * mm});
            skLineSegment(sketch, "E2843", {"start": v(-34.58, -33.55) * mm, "end": v(-34.46, -33.43) * mm});
            skLineSegment(sketch, "E2844", {"start": v(-34.46, -33.43) * mm, "end": v(-34.35, -33.32) * mm});
            skLineSegment(sketch, "E2845", {"start": v(-34.35, -33.32) * mm, "end": v(-34.23, -33.2) * mm});
            skLineSegment(sketch, "E2846", {"start": v(-34.23, -33.2) * mm, "end": v(-34.11, -33.08) * mm});
            skLineSegment(sketch, "E2847", {"start": v(-34.11, -33.08) * mm, "end": v(-33.99, -32.96) * mm});
            skLineSegment(sketch, "E2848", {"start": v(-33.99, -32.96) * mm, "end": v(-33.87, -32.85) * mm});
            skLineSegment(sketch, "E2849", {"start": v(-33.87, -32.85) * mm, "end": v(-33.75, -32.73) * mm});
            skLineSegment(sketch, "E2850", {"start": v(-33.75, -32.73) * mm, "end": v(-33.63, -32.6) * mm});
            skLineSegment(sketch, "E2851", {"start": v(-33.63, -32.6) * mm, "end": v(-33.51, -32.5) * mm});
            skLineSegment(sketch, "E2852", {"start": v(-33.51, -32.5) * mm, "end": v(-33.4, -32.37) * mm});
            skLineSegment(sketch, "E2853", {"start": v(-33.4, -32.37) * mm, "end": v(-33.27, -32.25) * mm});
            skLineSegment(sketch, "E2854", {"start": v(-33.27, -32.25) * mm, "end": v(-33.16, -32.14) * mm});
            skLineSegment(sketch, "E2855", {"start": v(-33.16, -32.14) * mm, "end": v(-33.07, -32.05) * mm});
            skLineSegment(sketch, "E2856", {"start": v(-33.07, -32.05) * mm, "end": v(-32.95, -32.17) * mm});
            skLineSegment(sketch, "E2857", {"start": v(-32.95, -32.17) * mm, "end": v(-32.83, -32.28) * mm});
            skLineSegment(sketch, "E2858", {"start": v(-32.83, -32.28) * mm, "end": v(-32.71, -32.4) * mm});
            skLineSegment(sketch, "E2859", {"start": v(-32.71, -32.4) * mm, "end": v(-32.6, -32.51) * mm});
            skLineSegment(sketch, "E2860", {"start": v(-32.6, -32.51) * mm, "end": v(-32.47, -32.63) * mm});
            skLineSegment(sketch, "E2861", {"start": v(-32.47, -32.63) * mm, "end": v(-32.35, -32.74) * mm});
            skLineSegment(sketch, "E2862", {"start": v(-32.35, -32.74) * mm, "end": v(-32.23, -32.86) * mm});
            skLineSegment(sketch, "E2863", {"start": v(-32.23, -32.86) * mm, "end": v(-32.11, -32.97) * mm});
            skLineSegment(sketch, "E2864", {"start": v(-32.11, -32.97) * mm, "end": v(-32, -33.1) * mm});
            skLineSegment(sketch, "E2865", {"start": v(-32, -33.1) * mm, "end": v(-31.87, -33.2) * mm});
            skLineSegment(sketch, "E2866", {"start": v(-31.87, -33.2) * mm, "end": v(-31.75, -33.32) * mm});
            skLineSegment(sketch, "E2867", {"start": v(-31.75, -33.32) * mm, "end": v(-31.7, -33.38) * mm});
            skLineSegment(sketch, "E2868", {"start": v(-31.7, -33.38) * mm, "end": v(-31.8, -33.5) * mm});
            skLineSegment(sketch, "E2869", {"start": v(-31.8, -33.5) * mm, "end": v(-31.92, -33.62) * mm});
            skLineSegment(sketch, "E2870", {"start": v(-31.92, -33.62) * mm, "end": v(-32.04, -33.75) * mm});
            skLineSegment(sketch, "E2871", {"start": v(-32.04, -33.75) * mm, "end": v(-32.15, -33.87) * mm});
            skLineSegment(sketch, "E2872", {"start": v(-32.15, -33.87) * mm, "end": v(-32.26, -34) * mm});
            skLineSegment(sketch, "E2873", {"start": v(-32.26, -34) * mm, "end": v(-32.38, -34.12) * mm});
            skLineSegment(sketch, "E2874", {"start": v(-32.38, -34.12) * mm, "end": v(-32.5, -34.24) * mm});
            skLineSegment(sketch, "E2875", {"start": v(-32.5, -34.24) * mm, "end": v(-32.6, -34.36) * mm});
            skLineSegment(sketch, "E2876", {"start": v(-32.6, -34.36) * mm, "end": v(-32.72, -34.49) * mm});
            skLineSegment(sketch, "E2877", {"start": v(-32.72, -34.49) * mm, "end": v(-32.83, -34.6) * mm});
            skLineSegment(sketch, "E2878", {"start": v(-32.83, -34.6) * mm, "end": v(-32.95, -34.73) * mm});
            skLineSegment(sketch, "E2879", {"start": v(-32.95, -34.73) * mm, "end": v(-33.06, -34.86) * mm});
            skLineSegment(sketch, "E2880", {"start": v(-33.06, -34.86) * mm, "end": v(-33.18, -34.99) * mm});
            skLineSegment(sketch, "E2881", {"start": v(-33.18, -34.99) * mm, "end": v(-33.28, -35.14) * mm});
            skLineSegment(sketch, "E2882", {"start": v(-33.28, -35.14) * mm, "end": v(-33.33, -35.3) * mm});
            skLineSegment(sketch, "E2883", {"start": v(-33.33, -35.3) * mm, "end": v(-33.33, -35.48) * mm});
            skLineSegment(sketch, "E2884", {"start": v(-33.33, -35.48) * mm, "end": v(-33.3, -35.64) * mm});
            skLineSegment(sketch, "E2885", {"start": v(-33.3, -35.64) * mm, "end": v(-33.2, -35.8) * mm});
            skLineSegment(sketch, "E2886", {"start": v(-33.2, -35.8) * mm, "end": v(-33.09, -35.92) * mm});
            skLineSegment(sketch, "E2887", {"start": v(-33.09, -35.92) * mm, "end": v(-32.94, -36.01) * mm});
            skLineSegment(sketch, "E2888", {"start": v(-32.94, -36.01) * mm, "end": v(-32.77, -36.06) * mm});
            skLineSegment(sketch, "E2889", {"start": v(-32.77, -36.06) * mm, "end": v(-32.6, -36.07) * mm});
            skLineSegment(sketch, "E2890", {"start": v(-32.6, -36.07) * mm, "end": v(-32.43, -36.03) * mm});
            skLineSegment(sketch, "E2891", {"start": v(-32.43, -36.03) * mm, "end": v(-32.28, -35.94) * mm});
            skLineSegment(sketch, "E2892", {"start": v(-32.28, -35.94) * mm, "end": v(-32.16, -35.83) * mm});
            skLineSegment(sketch, "E2893", {"start": v(-32.16, -35.83) * mm, "end": v(-32.05, -35.7) * mm});
            skLineSegment(sketch, "E2894", {"start": v(-32.05, -35.7) * mm, "end": v(-31.94, -35.58) * mm});
            skLineSegment(sketch, "E2895", {"start": v(-31.94, -35.58) * mm, "end": v(-31.83, -35.45) * mm});
            skLineSegment(sketch, "E2896", {"start": v(-31.83, -35.45) * mm, "end": v(-31.72, -35.33) * mm});
            skLineSegment(sketch, "E2897", {"start": v(-31.72, -35.33) * mm, "end": v(-31.6, -35.2) * mm});
            skLineSegment(sketch, "E2898", {"start": v(-31.6, -35.2) * mm, "end": v(-31.5, -35.07) * mm});
            skLineSegment(sketch, "E2899", {"start": v(-31.5, -35.07) * mm, "end": v(-31.39, -34.95) * mm});
            skLineSegment(sketch, "E2900", {"start": v(-31.39, -34.95) * mm, "end": v(-31.28, -34.82) * mm});
            skLineSegment(sketch, "E2901", {"start": v(-31.28, -34.82) * mm, "end": v(-31.17, -34.7) * mm});
            skLineSegment(sketch, "E2902", {"start": v(-31.17, -34.7) * mm, "end": v(-31.06, -34.57) * mm});
            skLineSegment(sketch, "E2903", {"start": v(-31.06, -34.57) * mm, "end": v(-30.95, -34.44) * mm});
            skLineSegment(sketch, "E2904", {"start": v(-30.95, -34.44) * mm, "end": v(-30.84, -34.32) * mm});
            skLineSegment(sketch, "E2905", {"start": v(-30.84, -34.32) * mm, "end": v(-30.76, -34.22) * mm});
            skLineSegment(sketch, "E2906", {"start": v(-30.76, -34.22) * mm, "end": v(-30.63, -34.33) * mm});
            skLineSegment(sketch, "E2907", {"start": v(-30.63, -34.33) * mm, "end": v(-30.5, -34.44) * mm});
            skLineSegment(sketch, "E2908", {"start": v(-30.5, -34.44) * mm, "end": v(-30.37, -34.54) * mm});
            skLineSegment(sketch, "E2909", {"start": v(-30.37, -34.54) * mm, "end": v(-30.25, -34.65) * mm});
            skLineSegment(sketch, "E2910", {"start": v(-30.25, -34.65) * mm, "end": v(-30.12, -34.76) * mm});
            skLineSegment(sketch, "E2911", {"start": v(-30.12, -34.76) * mm, "end": v(-30, -34.87) * mm});
            skLineSegment(sketch, "E2912", {"start": v(-30, -34.87) * mm, "end": v(-29.86, -34.97) * mm});
            skLineSegment(sketch, "E2913", {"start": v(-29.86, -34.97) * mm, "end": v(-29.74, -35.08) * mm});
            skLineSegment(sketch, "E2914", {"start": v(-29.74, -35.08) * mm, "end": v(-29.6, -35.19) * mm});
            skLineSegment(sketch, "E2915", {"start": v(-29.6, -35.19) * mm, "end": v(-29.48, -35.3) * mm});
            skLineSegment(sketch, "E2916", {"start": v(-29.48, -35.3) * mm, "end": v(-29.35, -35.4) * mm});
            skLineSegment(sketch, "E2917", {"start": v(-29.35, -35.4) * mm, "end": v(-29.3, -35.45) * mm});
            skLineSegment(sketch, "E2918", {"start": v(-29.3, -35.45) * mm, "end": v(-29.4, -35.58) * mm});
            skLineSegment(sketch, "E2919", {"start": v(-29.4, -35.58) * mm, "end": v(-29.5, -35.71) * mm});
            skLineSegment(sketch, "E2920", {"start": v(-29.5, -35.71) * mm, "end": v(-29.6, -35.84) * mm});
            skLineSegment(sketch, "E2921", {"start": v(-29.6, -35.84) * mm, "end": v(-29.71, -35.97) * mm});
            skLineSegment(sketch, "E2922", {"start": v(-29.71, -35.97) * mm, "end": v(-29.82, -36.1) * mm});
            skLineSegment(sketch, "E2923", {"start": v(-29.82, -36.1) * mm, "end": v(-29.92, -36.24) * mm});
            skLineSegment(sketch, "E2924", {"start": v(-29.92, -36.24) * mm, "end": v(-30.03, -36.37) * mm});
            skLineSegment(sketch, "E2925", {"start": v(-30.03, -36.37) * mm, "end": v(-30.13, -36.5) * mm});
            skLineSegment(sketch, "E2926", {"start": v(-30.13, -36.5) * mm, "end": v(-30.24, -36.63) * mm});
            skLineSegment(sketch, "E2927", {"start": v(-30.24, -36.63) * mm, "end": v(-30.34, -36.76) * mm});
            skLineSegment(sketch, "E2928", {"start": v(-30.34, -36.76) * mm, "end": v(-30.45, -36.89) * mm});
            skLineSegment(sketch, "E2929", {"start": v(-30.45, -36.89) * mm, "end": v(-30.55, -37.02) * mm});
            skLineSegment(sketch, "E2930", {"start": v(-30.55, -37.02) * mm, "end": v(-30.67, -37.16) * mm});
            skLineSegment(sketch, "E2931", {"start": v(-30.67, -37.16) * mm, "end": v(-30.75, -37.32) * mm});
            skLineSegment(sketch, "E2932", {"start": v(-30.75, -37.32) * mm, "end": v(-30.78, -37.49) * mm});
            skLineSegment(sketch, "E2933", {"start": v(-30.78, -37.49) * mm, "end": v(-30.78, -37.66) * mm});
            skLineSegment(sketch, "E2934", {"start": v(-30.78, -37.66) * mm, "end": v(-30.73, -37.82) * mm});
            skLineSegment(sketch, "E2935", {"start": v(-30.73, -37.82) * mm, "end": v(-30.63, -37.97) * mm});
            skLineSegment(sketch, "E2936", {"start": v(-30.63, -37.97) * mm, "end": v(-30.5, -38.09) * mm});
            skLineSegment(sketch, "E2937", {"start": v(-30.5, -38.09) * mm, "end": v(-30.35, -38.17) * mm});
            skLineSegment(sketch, "E2938", {"start": v(-30.35, -38.17) * mm, "end": v(-30.18, -38.2) * mm});
            skLineSegment(sketch, "E2939", {"start": v(-30.18, -38.2) * mm, "end": v(-30, -38.2) * mm});
            skLineSegment(sketch, "E2940", {"start": v(-30, -38.2) * mm, "end": v(-29.84, -38.15) * mm});
            skLineSegment(sketch, "E2941", {"start": v(-29.84, -38.15) * mm, "end": v(-29.7, -38.05) * mm});
            skLineSegment(sketch, "E2942", {"start": v(-29.7, -38.05) * mm, "end": v(-29.59, -37.93) * mm});
            skLineSegment(sketch, "E2943", {"start": v(-29.59, -37.93) * mm, "end": v(-29.48, -37.8) * mm});
            skLineSegment(sketch, "E2944", {"start": v(-29.48, -37.8) * mm, "end": v(-29.38, -37.66) * mm});
            skLineSegment(sketch, "E2945", {"start": v(-29.38, -37.66) * mm, "end": v(-29.28, -37.53) * mm});
            skLineSegment(sketch, "E2946", {"start": v(-29.28, -37.53) * mm, "end": v(-29.18, -37.4) * mm});
            skLineSegment(sketch, "E2947", {"start": v(-29.18, -37.4) * mm, "end": v(-29.08, -37.26) * mm});
            skLineSegment(sketch, "E2948", {"start": v(-29.08, -37.26) * mm, "end": v(-28.98, -37.13) * mm});
            skLineSegment(sketch, "E2949", {"start": v(-28.98, -37.13) * mm, "end": v(-28.88, -37) * mm});
            skLineSegment(sketch, "E2950", {"start": v(-28.88, -37) * mm, "end": v(-28.77, -36.86) * mm});
            skLineSegment(sketch, "E2951", {"start": v(-28.77, -36.86) * mm, "end": v(-28.67, -36.73) * mm});
            skLineSegment(sketch, "E2952", {"start": v(-28.67, -36.73) * mm, "end": v(-28.57, -36.6) * mm});
            skLineSegment(sketch, "E2953", {"start": v(-28.57, -36.6) * mm, "end": v(-28.47, -36.46) * mm});
            skLineSegment(sketch, "E2954", {"start": v(-28.47, -36.46) * mm, "end": v(-28.37, -36.33) * mm});
            skLineSegment(sketch, "E2955", {"start": v(-28.37, -36.33) * mm, "end": v(-28.3, -36.23) * mm});
            skLineSegment(sketch, "E2956", {"start": v(-28.3, -36.23) * mm, "end": v(-28.16, -36.33) * mm});
            skLineSegment(sketch, "E2957", {"start": v(-28.16, -36.33) * mm, "end": v(-28.03, -36.43) * mm});
            skLineSegment(sketch, "E2958", {"start": v(-28.03, -36.43) * mm, "end": v(-27.9, -36.52) * mm});
            skLineSegment(sketch, "E2959", {"start": v(-27.9, -36.52) * mm, "end": v(-27.76, -36.62) * mm});
            skLineSegment(sketch, "E2960", {"start": v(-27.76, -36.62) * mm, "end": v(-27.62, -36.72) * mm});
            skLineSegment(sketch, "E2961", {"start": v(-27.62, -36.72) * mm, "end": v(-27.49, -36.82) * mm});
            skLineSegment(sketch, "E2962", {"start": v(-27.49, -36.82) * mm, "end": v(-27.35, -36.91) * mm});
            skLineSegment(sketch, "E2963", {"start": v(-27.35, -36.91) * mm, "end": v(-27.22, -37.01) * mm});
            skLineSegment(sketch, "E2964", {"start": v(-27.22, -37.01) * mm, "end": v(-27.08, -37.11) * mm});
            skLineSegment(sketch, "E2965", {"start": v(-27.08, -37.11) * mm, "end": v(-26.95, -37.2) * mm});
            skLineSegment(sketch, "E2966", {"start": v(-26.95, -37.2) * mm, "end": v(-26.81, -37.3) * mm});
            skLineSegment(sketch, "E2967", {"start": v(-26.81, -37.3) * mm, "end": v(-26.75, -37.35) * mm});
            skLineSegment(sketch, "E2968", {"start": v(-26.75, -37.35) * mm, "end": v(-26.84, -37.5) * mm});
            skLineSegment(sketch, "E2969", {"start": v(-26.84, -37.5) * mm, "end": v(-26.94, -37.63) * mm});
            skLineSegment(sketch, "E2970", {"start": v(-26.94, -37.63) * mm, "end": v(-27.04, -37.77) * mm});
            skLineSegment(sketch, "E2971", {"start": v(-27.04, -37.77) * mm, "end": v(-27.13, -37.9) * mm});
            skLineSegment(sketch, "E2972", {"start": v(-27.13, -37.9) * mm, "end": v(-27.23, -38.04) * mm});
            skLineSegment(sketch, "E2973", {"start": v(-27.23, -38.04) * mm, "end": v(-27.32, -38.18) * mm});
            skLineSegment(sketch, "E2974", {"start": v(-27.32, -38.18) * mm, "end": v(-27.42, -38.32) * mm});
            skLineSegment(sketch, "E2975", {"start": v(-27.42, -38.32) * mm, "end": v(-27.51, -38.45) * mm});
            skLineSegment(sketch, "E2976", {"start": v(-27.51, -38.45) * mm, "end": v(-27.61, -38.6) * mm});
            skLineSegment(sketch, "E2977", {"start": v(-27.61, -38.6) * mm, "end": v(-27.7, -38.73) * mm});
            skLineSegment(sketch, "E2978", {"start": v(-27.7, -38.73) * mm, "end": v(-27.8, -38.87) * mm});
            skLineSegment(sketch, "E2979", {"start": v(-27.8, -38.87) * mm, "end": v(-27.9, -39) * mm});
            skLineSegment(sketch, "E2980", {"start": v(-27.9, -39) * mm, "end": v(-28, -39.16) * mm});
            skLineSegment(sketch, "E2981", {"start": v(-28, -39.16) * mm, "end": v(-28.07, -39.32) * mm});
            skLineSegment(sketch, "E2982", {"start": v(-28.07, -39.32) * mm, "end": v(-28.1, -39.49) * mm});
            skLineSegment(sketch, "E2983", {"start": v(-28.1, -39.49) * mm, "end": v(-28.08, -39.66) * mm});
            skLineSegment(sketch, "E2984", {"start": v(-28.08, -39.66) * mm, "end": v(-28.01, -39.82) * mm});
            skLineSegment(sketch, "E2985", {"start": v(-28.01, -39.82) * mm, "end": v(-27.91, -39.96) * mm});
            skLineSegment(sketch, "E2986", {"start": v(-27.91, -39.96) * mm, "end": v(-27.78, -40.07) * mm});
            skLineSegment(sketch, "E2987", {"start": v(-27.78, -40.07) * mm, "end": v(-27.62, -40.14) * mm});
            skLineSegment(sketch, "E2988", {"start": v(-27.62, -40.14) * mm, "end": v(-27.44, -40.16) * mm});
            skLineSegment(sketch, "E2989", {"start": v(-27.44, -40.16) * mm, "end": v(-27.27, -40.14) * mm});
            skLineSegment(sketch, "E2990", {"start": v(-27.27, -40.14) * mm, "end": v(-27.11, -40.08) * mm});
            skLineSegment(sketch, "E2991", {"start": v(-27.11, -40.08) * mm, "end": v(-26.97, -39.97) * mm});
            skLineSegment(sketch, "E2992", {"start": v(-26.97, -39.97) * mm, "end": v(-26.87, -39.84) * mm});
            skLineSegment(sketch, "E2993", {"start": v(-26.87, -39.84) * mm, "end": v(-26.78, -39.7) * mm});
            skLineSegment(sketch, "E2994", {"start": v(-26.78, -39.7) * mm, "end": v(-26.69, -39.57) * mm});
            skLineSegment(sketch, "E2995", {"start": v(-26.69, -39.57) * mm, "end": v(-26.6, -39.43) * mm});
            skLineSegment(sketch, "E2996", {"start": v(-26.6, -39.43) * mm, "end": v(-26.5, -39.29) * mm});
            skLineSegment(sketch, "E2997", {"start": v(-26.5, -39.29) * mm, "end": v(-26.41, -39.14) * mm});
            skLineSegment(sketch, "E2998", {"start": v(-26.41, -39.14) * mm, "end": v(-26.32, -39) * mm});
            skLineSegment(sketch, "E2999", {"start": v(-26.32, -39) * mm, "end": v(-26.23, -38.87) * mm});
            skLineSegment(sketch, "E3000", {"start": v(-26.23, -38.87) * mm, "end": v(-26.13, -38.72) * mm});
            skLineSegment(sketch, "E3001", {"start": v(-26.13, -38.72) * mm, "end": v(-26.04, -38.58) * mm});
            skLineSegment(sketch, "E3002", {"start": v(-26.04, -38.58) * mm, "end": v(-25.95, -38.44) * mm});
            skLineSegment(sketch, "E3003", {"start": v(-25.95, -38.44) * mm, "end": v(-25.86, -38.3) * mm});
            skLineSegment(sketch, "E3004", {"start": v(-25.86, -38.3) * mm, "end": v(-25.77, -38.16) * mm});
            skLineSegment(sketch, "E3005", {"start": v(-25.77, -38.16) * mm, "end": v(-25.7, -38.06) * mm});
            skLineSegment(sketch, "E3006", {"start": v(-25.7, -38.06) * mm, "end": v(-25.56, -38.15) * mm});
            skLineSegment(sketch, "E3007", {"start": v(-25.56, -38.15) * mm, "end": v(-25.42, -38.24) * mm});
            skLineSegment(sketch, "E3008", {"start": v(-25.42, -38.24) * mm, "end": v(-25.28, -38.33) * mm});
            skLineSegment(sketch, "E3009", {"start": v(-25.28, -38.33) * mm, "end": v(-25.14, -38.41) * mm});
            skLineSegment(sketch, "E3010", {"start": v(-25.14, -38.41) * mm, "end": v(-25, -38.5) * mm});
            skLineSegment(sketch, "E3011", {"start": v(-25, -38.5) * mm, "end": v(-24.85, -38.59) * mm});
            skLineSegment(sketch, "E3012", {"start": v(-24.85, -38.59) * mm, "end": v(-24.71, -38.68) * mm});
            skLineSegment(sketch, "E3013", {"start": v(-24.71, -38.68) * mm, "end": v(-24.57, -38.77) * mm});
            skLineSegment(sketch, "E3014", {"start": v(-24.57, -38.77) * mm, "end": v(-24.43, -38.85) * mm});
            skLineSegment(sketch, "E3015", {"start": v(-24.43, -38.85) * mm, "end": v(-24.29, -38.94) * mm});
            skLineSegment(sketch, "E3016", {"start": v(-24.29, -38.94) * mm, "end": v(-24.15, -39.03) * mm});
            skLineSegment(sketch, "E3017", {"start": v(-24.15, -39.03) * mm, "end": v(-24.08, -39.07) * mm});
            skLineSegment(sketch, "E3018", {"start": v(-24.08, -39.07) * mm, "end": v(-24.17, -39.22) * mm});
            skLineSegment(sketch, "E3019", {"start": v(-24.17, -39.22) * mm, "end": v(-24.25, -39.36) * mm});
            skLineSegment(sketch, "E3020", {"start": v(-24.25, -39.36) * mm, "end": v(-24.34, -39.5) * mm});
            skLineSegment(sketch, "E3021", {"start": v(-24.34, -39.5) * mm, "end": v(-24.42, -39.65) * mm});
            skLineSegment(sketch, "E3022", {"start": v(-24.42, -39.65) * mm, "end": v(-24.5, -39.8) * mm});
            skLineSegment(sketch, "E3023", {"start": v(-24.5, -39.8) * mm, "end": v(-24.6, -39.94) * mm});
            skLineSegment(sketch, "E3024", {"start": v(-24.6, -39.94) * mm, "end": v(-24.68, -40.08) * mm});
            skLineSegment(sketch, "E3025", {"start": v(-24.68, -40.08) * mm, "end": v(-24.77, -40.23) * mm});
            skLineSegment(sketch, "E3026", {"start": v(-24.77, -40.23) * mm, "end": v(-24.85, -40.37) * mm});
            skLineSegment(sketch, "E3027", {"start": v(-24.85, -40.37) * mm, "end": v(-24.94, -40.51) * mm});
            skLineSegment(sketch, "E3028", {"start": v(-24.94, -40.51) * mm, "end": v(-25.02, -40.66) * mm});
            skLineSegment(sketch, "E3029", {"start": v(-25.02, -40.66) * mm, "end": v(-25.11, -40.8) * mm});
            skLineSegment(sketch, "E3030", {"start": v(-25.11, -40.8) * mm, "end": v(-25.2, -40.96) * mm});
            skLineSegment(sketch, "E3031", {"start": v(-25.2, -40.96) * mm, "end": v(-25.26, -41.12) * mm});
            skLineSegment(sketch, "E3032", {"start": v(-25.26, -41.12) * mm, "end": v(-25.28, -41.3) * mm});
            skLineSegment(sketch, "E3033", {"start": v(-25.28, -41.3) * mm, "end": v(-25.24, -41.47) * mm});
            skLineSegment(sketch, "E3034", {"start": v(-25.24, -41.47) * mm, "end": v(-25.17, -41.62) * mm});
            skLineSegment(sketch, "E3035", {"start": v(-25.17, -41.62) * mm, "end": v(-25.06, -41.75) * mm});
            skLineSegment(sketch, "E3036", {"start": v(-25.06, -41.75) * mm, "end": v(-24.91, -41.85) * mm});
            skLineSegment(sketch, "E3037", {"start": v(-24.91, -41.85) * mm, "end": v(-24.75, -41.91) * mm});
            skLineSegment(sketch, "E3038", {"start": v(-24.75, -41.91) * mm, "end": v(-24.58, -41.92) * mm});
            skLineSegment(sketch, "E3039", {"start": v(-24.58, -41.92) * mm, "end": v(-24.4, -41.9) * mm});
            skLineSegment(sketch, "E3040", {"start": v(-24.4, -41.9) * mm, "end": v(-24.25, -41.82) * mm});
            skLineSegment(sketch, "E3041", {"start": v(-24.25, -41.82) * mm, "end": v(-24.12, -41.7) * mm});
            skLineSegment(sketch, "E3042", {"start": v(-24.12, -41.7) * mm, "end": v(-24.03, -41.56) * mm});
            skLineSegment(sketch, "E3043", {"start": v(-24.03, -41.56) * mm, "end": v(-23.94, -41.42) * mm});
            skLineSegment(sketch, "E3044", {"start": v(-23.94, -41.42) * mm, "end": v(-23.86, -41.28) * mm});
            skLineSegment(sketch, "E3045", {"start": v(-23.86, -41.28) * mm, "end": v(-23.78, -41.13) * mm});
            skLineSegment(sketch, "E3046", {"start": v(-23.78, -41.13) * mm, "end": v(-23.7, -40.99) * mm});
            skLineSegment(sketch, "E3047", {"start": v(-23.7, -40.99) * mm, "end": v(-23.62, -40.84) * mm});
            skLineSegment(sketch, "E3048", {"start": v(-23.62, -40.84) * mm, "end": v(-23.54, -40.7) * mm});
            skLineSegment(sketch, "E3049", {"start": v(-23.54, -40.7) * mm, "end": v(-23.45, -40.55) * mm});
            skLineSegment(sketch, "E3050", {"start": v(-23.45, -40.55) * mm, "end": v(-23.37, -40.4) * mm});
            skLineSegment(sketch, "E3051", {"start": v(-23.37, -40.4) * mm, "end": v(-23.3, -40.25) * mm});
            skLineSegment(sketch, "E3052", {"start": v(-23.3, -40.25) * mm, "end": v(-23.2, -40.1) * mm});
            skLineSegment(sketch, "E3053", {"start": v(-23.2, -40.1) * mm, "end": v(-23.13, -39.96) * mm});
            skLineSegment(sketch, "E3054", {"start": v(-23.13, -39.96) * mm, "end": v(-23.04, -39.81) * mm});
            skLineSegment(sketch, "E3055", {"start": v(-23.04, -39.81) * mm, "end": v(-22.99, -39.7) * mm});
            skLineSegment(sketch, "E3056", {"start": v(-22.99, -39.7) * mm, "end": v(-22.84, -39.78) * mm});
            skLineSegment(sketch, "E3057", {"start": v(-22.84, -39.78) * mm, "end": v(-22.7, -39.86) * mm});
            skLineSegment(sketch, "E3058", {"start": v(-22.7, -39.86) * mm, "end": v(-22.54, -39.94) * mm});
            skLineSegment(sketch, "E3059", {"start": v(-22.54, -39.94) * mm, "end": v(-22.4, -40.02) * mm});
            skLineSegment(sketch, "E3060", {"start": v(-22.4, -40.02) * mm, "end": v(-22.25, -40.1) * mm});
            skLineSegment(sketch, "E3061", {"start": v(-22.25, -40.1) * mm, "end": v(-22.1, -40.17) * mm});
            skLineSegment(sketch, "E3062", {"start": v(-22.1, -40.17) * mm, "end": v(-21.96, -40.25) * mm});
            skLineSegment(sketch, "E3063", {"start": v(-21.96, -40.25) * mm, "end": v(-21.8, -40.33) * mm});
            skLineSegment(sketch, "E3064", {"start": v(-21.8, -40.33) * mm, "end": v(-21.66, -40.4) * mm});
            skLineSegment(sketch, "E3065", {"start": v(-21.66, -40.4) * mm, "end": v(-21.52, -40.49) * mm});
            skLineSegment(sketch, "E3066", {"start": v(-21.52, -40.49) * mm, "end": v(-21.37, -40.56) * mm});
            skLineSegment(sketch, "E3067", {"start": v(-21.37, -40.56) * mm, "end": v(-21.3, -40.6) * mm});
            skLineSegment(sketch, "E3068", {"start": v(-21.3, -40.6) * mm, "end": v(-21.37, -40.75) * mm});
            skLineSegment(sketch, "E3069", {"start": v(-21.37, -40.75) * mm, "end": v(-21.45, -40.9) * mm});
            skLineSegment(sketch, "E3070", {"start": v(-21.45, -40.9) * mm, "end": v(-21.52, -41.05) * mm});
            skLineSegment(sketch, "E3071", {"start": v(-21.52, -41.05) * mm, "end": v(-21.6, -41.2) * mm});
            skLineSegment(sketch, "E3072", {"start": v(-21.6, -41.2) * mm, "end": v(-21.67, -41.35) * mm});
            skLineSegment(sketch, "E3073", {"start": v(-21.67, -41.35) * mm, "end": v(-21.75, -41.5) * mm});
            skLineSegment(sketch, "E3074", {"start": v(-21.75, -41.5) * mm, "end": v(-21.83, -41.65) * mm});
            skLineSegment(sketch, "E3075", {"start": v(-21.83, -41.65) * mm, "end": v(-21.9, -41.8) * mm});
            skLineSegment(sketch, "E3076", {"start": v(-21.9, -41.8) * mm, "end": v(-21.98, -41.95) * mm});
            skLineSegment(sketch, "E3077", {"start": v(-21.98, -41.95) * mm, "end": v(-22.05, -42.1) * mm});
            skLineSegment(sketch, "E3078", {"start": v(-22.05, -42.1) * mm, "end": v(-22.13, -42.25) * mm});
            skLineSegment(sketch, "E3079", {"start": v(-22.13, -42.25) * mm, "end": v(-22.2, -42.4) * mm});
            skLineSegment(sketch, "E3080", {"start": v(-22.2, -42.4) * mm, "end": v(-22.29, -42.56) * mm});
            skLineSegment(sketch, "E3081", {"start": v(-22.29, -42.56) * mm, "end": v(-22.33, -42.73) * mm});
            skLineSegment(sketch, "E3082", {"start": v(-22.33, -42.73) * mm, "end": v(-22.34, -42.9) * mm});
            skLineSegment(sketch, "E3083", {"start": v(-22.34, -42.9) * mm, "end": v(-22.3, -43.07) * mm});
            skLineSegment(sketch, "E3084", {"start": v(-22.3, -43.07) * mm, "end": v(-22.2, -43.22) * mm});
            skLineSegment(sketch, "E3085", {"start": v(-22.2, -43.22) * mm, "end": v(-22.09, -43.35) * mm});
            skLineSegment(sketch, "E3086", {"start": v(-22.09, -43.35) * mm, "end": v(-21.94, -43.43) * mm});
            skLineSegment(sketch, "E3087", {"start": v(-21.94, -43.43) * mm, "end": v(-21.77, -43.48) * mm});
            skLineSegment(sketch, "E3088", {"start": v(-21.77, -43.48) * mm, "end": v(-21.6, -43.48) * mm});
            skLineSegment(sketch, "E3089", {"start": v(-21.6, -43.48) * mm, "end": v(-21.43, -43.44) * mm});
            skLineSegment(sketch, "E3090", {"start": v(-21.43, -43.44) * mm, "end": v(-21.28, -43.35) * mm});
            skLineSegment(sketch, "E3091", {"start": v(-21.28, -43.35) * mm, "end": v(-21.15, -43.23) * mm});
            skLineSegment(sketch, "E3092", {"start": v(-21.15, -43.23) * mm, "end": v(-21.07, -43.08) * mm});
            skLineSegment(sketch, "E3093", {"start": v(-21.07, -43.08) * mm, "end": v(-21, -42.94) * mm});
            skLineSegment(sketch, "E3094", {"start": v(-21, -42.94) * mm, "end": v(-20.93, -42.79) * mm});
            skLineSegment(sketch, "E3095", {"start": v(-20.93, -42.79) * mm, "end": v(-20.86, -42.63) * mm});
            skLineSegment(sketch, "E3096", {"start": v(-20.86, -42.63) * mm, "end": v(-20.79, -42.48) * mm});
            skLineSegment(sketch, "E3097", {"start": v(-20.79, -42.48) * mm, "end": v(-20.71, -42.33) * mm});
            skLineSegment(sketch, "E3098", {"start": v(-20.71, -42.33) * mm, "end": v(-20.64, -42.18) * mm});
            skLineSegment(sketch, "E3099", {"start": v(-20.64, -42.18) * mm, "end": v(-20.57, -42.03) * mm});
            skLineSegment(sketch, "E3100", {"start": v(-20.57, -42.03) * mm, "end": v(-20.5, -41.87) * mm});
            skLineSegment(sketch, "E3101", {"start": v(-20.5, -41.87) * mm, "end": v(-20.43, -41.72) * mm});
            skLineSegment(sketch, "E3102", {"start": v(-20.43, -41.72) * mm, "end": v(-20.36, -41.57) * mm});
            skLineSegment(sketch, "E3103", {"start": v(-20.36, -41.57) * mm, "end": v(-20.28, -41.42) * mm});
            skLineSegment(sketch, "E3104", {"start": v(-20.28, -41.42) * mm, "end": v(-20.21, -41.27) * mm});
            skLineSegment(sketch, "E3105", {"start": v(-20.21, -41.27) * mm, "end": v(-20.16, -41.16) * mm});
            skLineSegment(sketch, "E3106", {"start": v(-20.16, -41.16) * mm, "end": v(-20, -41.22) * mm});
            skLineSegment(sketch, "E3107", {"start": v(-20, -41.22) * mm, "end": v(-19.86, -41.3) * mm});
            skLineSegment(sketch, "E3108", {"start": v(-19.86, -41.3) * mm, "end": v(-19.7, -41.36) * mm});
            skLineSegment(sketch, "E3109", {"start": v(-19.7, -41.36) * mm, "end": v(-19.55, -41.43) * mm});
            skLineSegment(sketch, "E3110", {"start": v(-19.55, -41.43) * mm, "end": v(-19.4, -41.5) * mm});
            skLineSegment(sketch, "E3111", {"start": v(-19.4, -41.5) * mm, "end": v(-19.25, -41.56) * mm});
            skLineSegment(sketch, "E3112", {"start": v(-19.25, -41.56) * mm, "end": v(-19.1, -41.63) * mm});
            skLineSegment(sketch, "E3113", {"start": v(-19.1, -41.63) * mm, "end": v(-18.95, -41.7) * mm});
            skLineSegment(sketch, "E3114", {"start": v(-18.95, -41.7) * mm, "end": v(-18.8, -41.77) * mm});
            skLineSegment(sketch, "E3115", {"start": v(-18.8, -41.77) * mm, "end": v(-18.64, -41.83) * mm});
            skLineSegment(sketch, "E3116", {"start": v(-18.64, -41.83) * mm, "end": v(-18.49, -41.9) * mm});
            skLineSegment(sketch, "E3117", {"start": v(-18.49, -41.9) * mm, "end": v(-18.42, -41.93) * mm});
            skLineSegment(sketch, "E3118", {"start": v(-18.42, -41.93) * mm, "end": v(-18.48, -42.09) * mm});
            skLineSegment(sketch, "E3119", {"start": v(-18.48, -42.09) * mm, "end": v(-18.54, -42.24) * mm});
            skLineSegment(sketch, "E3120", {"start": v(-18.54, -42.24) * mm, "end": v(-18.61, -42.4) * mm});
            skLineSegment(sketch, "E3121", {"start": v(-18.61, -42.4) * mm, "end": v(-18.67, -42.55) * mm});
            skLineSegment(sketch, "E3122", {"start": v(-18.67, -42.55) * mm, "end": v(-18.74, -42.7) * mm});
            skLineSegment(sketch, "E3123", {"start": v(-18.74, -42.7) * mm, "end": v(-18.8, -42.86) * mm});
            skLineSegment(sketch, "E3124", {"start": v(-18.8, -42.86) * mm, "end": v(-18.87, -43.02) * mm});
            skLineSegment(sketch, "E3125", {"start": v(-18.87, -43.02) * mm, "end": v(-18.93, -43.17) * mm});
            skLineSegment(sketch, "E3126", {"start": v(-18.93, -43.17) * mm, "end": v(-19, -43.33) * mm});
            skLineSegment(sketch, "E3127", {"start": v(-19, -43.33) * mm, "end": v(-19.07, -43.48) * mm});
            skLineSegment(sketch, "E3128", {"start": v(-19.07, -43.48) * mm, "end": v(-19.13, -43.63) * mm});
            skLineSegment(sketch, "E3129", {"start": v(-19.13, -43.63) * mm, "end": v(-19.2, -43.8) * mm});
            skLineSegment(sketch, "E3130", {"start": v(-19.2, -43.8) * mm, "end": v(-19.26, -43.96) * mm});
            skLineSegment(sketch, "E3131", {"start": v(-19.26, -43.96) * mm, "end": v(-19.3, -44.13) * mm});
            skLineSegment(sketch, "E3132", {"start": v(-19.3, -44.13) * mm, "end": v(-19.3, -44.3) * mm});
            skLineSegment(sketch, "E3133", {"start": v(-19.3, -44.3) * mm, "end": v(-19.24, -44.47) * mm});
            skLineSegment(sketch, "E3134", {"start": v(-19.24, -44.47) * mm, "end": v(-19.14, -44.61) * mm});
            skLineSegment(sketch, "E3135", {"start": v(-19.14, -44.61) * mm, "end": v(-19.01, -44.73) * mm});
            skLineSegment(sketch, "E3136", {"start": v(-19.01, -44.73) * mm, "end": v(-18.86, -44.8) * mm});
            skLineSegment(sketch, "E3137", {"start": v(-18.86, -44.8) * mm, "end": v(-18.68, -44.84) * mm});
            skLineSegment(sketch, "E3138", {"start": v(-18.68, -44.84) * mm, "end": v(-18.51, -44.83) * mm});
            skLineSegment(sketch, "E3139", {"start": v(-18.51, -44.83) * mm, "end": v(-18.35, -44.77) * mm});
            skLineSegment(sketch, "E3140", {"start": v(-18.35, -44.77) * mm, "end": v(-18.2, -44.68) * mm});
            skLineSegment(sketch, "E3141", {"start": v(-18.2, -44.68) * mm, "end": v(-18.09, -44.54) * mm});
            skLineSegment(sketch, "E3142", {"start": v(-18.09, -44.54) * mm, "end": v(-18.02, -44.4) * mm});
            skLineSegment(sketch, "E3143", {"start": v(-18.02, -44.4) * mm, "end": v(-17.95, -44.24) * mm});
            skLineSegment(sketch, "E3144", {"start": v(-17.95, -44.24) * mm, "end": v(-17.9, -44.09) * mm});
            skLineSegment(sketch, "E3145", {"start": v(-17.9, -44.09) * mm, "end": v(-17.83, -43.93) * mm});
            skLineSegment(sketch, "E3146", {"start": v(-17.83, -43.93) * mm, "end": v(-17.77, -43.78) * mm});
            skLineSegment(sketch, "E3147", {"start": v(-17.77, -43.78) * mm, "end": v(-17.71, -43.62) * mm});
            skLineSegment(sketch, "E3148", {"start": v(-17.71, -43.62) * mm, "end": v(-17.65, -43.46) * mm});
            skLineSegment(sketch, "E3149", {"start": v(-17.65, -43.46) * mm, "end": v(-17.6, -43.3) * mm});
            skLineSegment(sketch, "E3150", {"start": v(-17.6, -43.3) * mm, "end": v(-17.53, -43.15) * mm});
            skLineSegment(sketch, "E3151", {"start": v(-17.53, -43.15) * mm, "end": v(-17.47, -43) * mm});
            skLineSegment(sketch, "E3152", {"start": v(-17.47, -43) * mm, "end": v(-17.4, -42.84) * mm});
            skLineSegment(sketch, "E3153", {"start": v(-17.4, -42.84) * mm, "end": v(-17.35, -42.68) * mm});
            skLineSegment(sketch, "E3154", {"start": v(-17.35, -42.68) * mm, "end": v(-17.29, -42.52) * mm});
            skLineSegment(sketch, "E3155", {"start": v(-17.29, -42.52) * mm, "end": v(-17.24, -42.4) * mm});
            skLineSegment(sketch, "E3156", {"start": v(-17.24, -42.4) * mm, "end": v(-17.09, -42.47) * mm});
            skLineSegment(sketch, "E3157", {"start": v(-17.09, -42.47) * mm, "end": v(-16.93, -42.52) * mm});
            skLineSegment(sketch, "E3158", {"start": v(-16.93, -42.52) * mm, "end": v(-16.77, -42.58) * mm});
            skLineSegment(sketch, "E3159", {"start": v(-16.77, -42.58) * mm, "end": v(-16.62, -42.64) * mm});
            skLineSegment(sketch, "E3160", {"start": v(-16.62, -42.64) * mm, "end": v(-16.46, -42.7) * mm});
            skLineSegment(sketch, "E3161", {"start": v(-16.46, -42.7) * mm, "end": v(-16.3, -42.75) * mm});
            skLineSegment(sketch, "E3162", {"start": v(-16.3, -42.75) * mm, "end": v(-16.15, -42.8) * mm});
            skLineSegment(sketch, "E3163", {"start": v(-16.15, -42.8) * mm, "end": v(-16, -42.86) * mm});
            skLineSegment(sketch, "E3164", {"start": v(-16, -42.86) * mm, "end": v(-15.84, -42.92) * mm});
            skLineSegment(sketch, "E3165", {"start": v(-15.84, -42.92) * mm, "end": v(-15.68, -42.98) * mm});
            skLineSegment(sketch, "E3166", {"start": v(-15.68, -42.98) * mm, "end": v(-15.52, -43.03) * mm});
            skLineSegment(sketch, "E3167", {"start": v(-15.52, -43.03) * mm, "end": v(-15.45, -43.06) * mm});
            skLineSegment(sketch, "E3168", {"start": v(-15.45, -43.06) * mm, "end": v(-15.5, -43.22) * mm});
            skLineSegment(sketch, "E3169", {"start": v(-15.5, -43.22) * mm, "end": v(-15.55, -43.38) * mm});
            skLineSegment(sketch, "E3170", {"start": v(-15.55, -43.38) * mm, "end": v(-15.6, -43.54) * mm});
            skLineSegment(sketch, "E3171", {"start": v(-15.6, -43.54) * mm, "end": v(-15.66, -43.7) * mm});
            skLineSegment(sketch, "E3172", {"start": v(-15.66, -43.7) * mm, "end": v(-15.72, -43.85) * mm});
            skLineSegment(sketch, "E3173", {"start": v(-15.72, -43.85) * mm, "end": v(-15.77, -44.02) * mm});
            skLineSegment(sketch, "E3174", {"start": v(-15.77, -44.02) * mm, "end": v(-15.83, -44.17) * mm});
            skLineSegment(sketch, "E3175", {"start": v(-15.83, -44.17) * mm, "end": v(-15.88, -44.33) * mm});
            skLineSegment(sketch, "E3176", {"start": v(-15.88, -44.33) * mm, "end": v(-15.93, -44.5) * mm});
            skLineSegment(sketch, "E3177", {"start": v(-15.93, -44.5) * mm, "end": v(-15.99, -44.65) * mm});
            skLineSegment(sketch, "E3178", {"start": v(-15.99, -44.65) * mm, "end": v(-16.04, -44.8) * mm});
            skLineSegment(sketch, "E3179", {"start": v(-16.04, -44.8) * mm, "end": v(-16.1, -44.97) * mm});
            skLineSegment(sketch, "E3180", {"start": v(-16.1, -44.97) * mm, "end": v(-16.15, -45.14) * mm});
            skLineSegment(sketch, "E3181", {"start": v(-16.15, -45.14) * mm, "end": v(-16.18, -45.31) * mm});
            skLineSegment(sketch, "E3182", {"start": v(-16.18, -45.31) * mm, "end": v(-16.15, -45.48) * mm});
            skLineSegment(sketch, "E3183", {"start": v(-16.15, -45.48) * mm, "end": v(-16.09, -45.64) * mm});
            skLineSegment(sketch, "E3184", {"start": v(-16.09, -45.64) * mm, "end": v(-15.98, -45.78) * mm});
            skLineSegment(sketch, "E3185", {"start": v(-15.98, -45.78) * mm, "end": v(-15.85, -45.89) * mm});
            skLineSegment(sketch, "E3186", {"start": v(-15.85, -45.89) * mm, "end": v(-15.69, -45.95) * mm});
            skLineSegment(sketch, "E3187", {"start": v(-15.69, -45.95) * mm, "end": v(-15.51, -45.98) * mm});
            skLineSegment(sketch, "E3188", {"start": v(-15.51, -45.98) * mm, "end": v(-15.34, -45.95) * mm});
            skLineSegment(sketch, "E3189", {"start": v(-15.34, -45.95) * mm, "end": v(-15.18, -45.89) * mm});
            skLineSegment(sketch, "E3190", {"start": v(-15.18, -45.89) * mm, "end": v(-15.04, -45.78) * mm});
            skLineSegment(sketch, "E3191", {"start": v(-15.04, -45.78) * mm, "end": v(-14.94, -45.64) * mm});
            skLineSegment(sketch, "E3192", {"start": v(-14.94, -45.64) * mm, "end": v(-14.88, -45.49) * mm});
            skLineSegment(sketch, "E3193", {"start": v(-14.88, -45.49) * mm, "end": v(-14.83, -45.33) * mm});
            skLineSegment(sketch, "E3194", {"start": v(-14.83, -45.33) * mm, "end": v(-14.78, -45.17) * mm});
            skLineSegment(sketch, "E3195", {"start": v(-14.78, -45.17) * mm, "end": v(-14.73, -45.01) * mm});
            skLineSegment(sketch, "E3196", {"start": v(-14.73, -45.01) * mm, "end": v(-14.68, -44.85) * mm});
            skLineSegment(sketch, "E3197", {"start": v(-14.68, -44.85) * mm, "end": v(-14.63, -44.7) * mm});
            skLineSegment(sketch, "E3198", {"start": v(-14.63, -44.7) * mm, "end": v(-14.58, -44.53) * mm});
            skLineSegment(sketch, "E3199", {"start": v(-14.58, -44.53) * mm, "end": v(-14.53, -44.37) * mm});
            skLineSegment(sketch, "E3200", {"start": v(-14.53, -44.37) * mm, "end": v(-14.48, -44.2) * mm});
            skLineSegment(sketch, "E3201", {"start": v(-14.48, -44.2) * mm, "end": v(-14.43, -44.05) * mm});
            skLineSegment(sketch, "E3202", {"start": v(-14.43, -44.05) * mm, "end": v(-14.38, -43.9) * mm});
            skLineSegment(sketch, "E3203", {"start": v(-14.38, -43.9) * mm, "end": v(-14.33, -43.73) * mm});
            skLineSegment(sketch, "E3204", {"start": v(-14.33, -43.73) * mm, "end": v(-14.28, -43.57) * mm});
            skLineSegment(sketch, "E3205", {"start": v(-14.28, -43.57) * mm, "end": v(-14.24, -43.45) * mm});
            skLineSegment(sketch, "E3206", {"start": v(-14.24, -43.45) * mm, "end": v(-14.08, -43.5) * mm});
            skLineSegment(sketch, "E3207", {"start": v(-14.08, -43.5) * mm, "end": v(-13.92, -43.54) * mm});
            skLineSegment(sketch, "E3208", {"start": v(-13.92, -43.54) * mm, "end": v(-13.77, -43.6) * mm});
            skLineSegment(sketch, "E3209", {"start": v(-13.77, -43.6) * mm, "end": v(-13.6, -43.64) * mm});
            skLineSegment(sketch, "E3210", {"start": v(-13.6, -43.64) * mm, "end": v(-13.45, -43.68) * mm});
            skLineSegment(sketch, "E3211", {"start": v(-13.45, -43.68) * mm, "end": v(-13.29, -43.73) * mm});
            skLineSegment(sketch, "E3212", {"start": v(-13.29, -43.73) * mm, "end": v(-13.13, -43.77) * mm});
            skLineSegment(sketch, "E3213", {"start": v(-13.13, -43.77) * mm, "end": v(-12.97, -43.82) * mm});
            skLineSegment(sketch, "E3214", {"start": v(-12.97, -43.82) * mm, "end": v(-12.8, -43.87) * mm});
            skLineSegment(sketch, "E3215", {"start": v(-12.8, -43.87) * mm, "end": v(-12.65, -43.91) * mm});
            skLineSegment(sketch, "E3216", {"start": v(-12.65, -43.91) * mm, "end": v(-12.49, -43.96) * mm});
            skLineSegment(sketch, "E3217", {"start": v(-12.49, -43.96) * mm, "end": v(-12.4, -43.98) * mm});
            skLineSegment(sketch, "E3218", {"start": v(-12.4, -43.98) * mm, "end": v(-12.45, -44.14) * mm});
            skLineSegment(sketch, "E3219", {"start": v(-12.45, -44.14) * mm, "end": v(-12.5, -44.3) * mm});
            skLineSegment(sketch, "E3220", {"start": v(-12.5, -44.3) * mm, "end": v(-12.54, -44.47) * mm});
            skLineSegment(sketch, "E3221", {"start": v(-12.54, -44.47) * mm, "end": v(-12.58, -44.63) * mm});
            skLineSegment(sketch, "E3222", {"start": v(-12.58, -44.63) * mm, "end": v(-12.62, -44.79) * mm});
            skLineSegment(sketch, "E3223", {"start": v(-12.62, -44.79) * mm, "end": v(-12.66, -44.95) * mm});
            skLineSegment(sketch, "E3224", {"start": v(-12.66, -44.95) * mm, "end": v(-12.7, -45.11) * mm});
            skLineSegment(sketch, "E3225", {"start": v(-12.7, -45.11) * mm, "end": v(-12.75, -45.28) * mm});
            skLineSegment(sketch, "E3226", {"start": v(-12.75, -45.28) * mm, "end": v(-12.8, -45.44) * mm});
            skLineSegment(sketch, "E3227", {"start": v(-12.8, -45.44) * mm, "end": v(-12.84, -45.6) * mm});
            skLineSegment(sketch, "E3228", {"start": v(-12.84, -45.6) * mm, "end": v(-12.88, -45.76) * mm});
            skLineSegment(sketch, "E3229", {"start": v(-12.88, -45.76) * mm, "end": v(-12.92, -45.93) * mm});
            skLineSegment(sketch, "E3230", {"start": v(-12.92, -45.93) * mm, "end": v(-12.97, -46.1) * mm});
            skLineSegment(sketch, "E3231", {"start": v(-12.97, -46.1) * mm, "end": v(-12.98, -46.27) * mm});
            skLineSegment(sketch, "E3232", {"start": v(-12.98, -46.27) * mm, "end": v(-12.94, -46.44) * mm});
            skLineSegment(sketch, "E3233", {"start": v(-12.94, -46.44) * mm, "end": v(-12.87, -46.6) * mm});
            skLineSegment(sketch, "E3234", {"start": v(-12.87, -46.6) * mm, "end": v(-12.75, -46.73) * mm});
            skLineSegment(sketch, "E3235", {"start": v(-12.75, -46.73) * mm, "end": v(-12.6, -46.83) * mm});
            skLineSegment(sketch, "E3236", {"start": v(-12.6, -46.83) * mm, "end": v(-12.44, -46.88) * mm});
            skLineSegment(sketch, "E3237", {"start": v(-12.44, -46.88) * mm, "end": v(-12.27, -46.9) * mm});
            skLineSegment(sketch, "E3238", {"start": v(-12.27, -46.9) * mm, "end": v(-12.1, -46.86) * mm});
            skLineSegment(sketch, "E3239", {"start": v(-12.1, -46.86) * mm, "end": v(-11.95, -46.78) * mm});
            skLineSegment(sketch, "E3240", {"start": v(-11.95, -46.78) * mm, "end": v(-11.82, -46.66) * mm});
            skLineSegment(sketch, "E3241", {"start": v(-11.82, -46.66) * mm, "end": v(-11.72, -46.52) * mm});
            skLineSegment(sketch, "E3242", {"start": v(-11.72, -46.52) * mm, "end": v(-11.67, -46.36) * mm});
            skLineSegment(sketch, "E3243", {"start": v(-11.67, -46.36) * mm, "end": v(-11.63, -46.2) * mm});
            skLineSegment(sketch, "E3244", {"start": v(-11.63, -46.2) * mm, "end": v(-11.6, -46.04) * mm});
            skLineSegment(sketch, "E3245", {"start": v(-11.6, -46.04) * mm, "end": v(-11.55, -45.88) * mm});
            skLineSegment(sketch, "E3246", {"start": v(-11.55, -45.88) * mm, "end": v(-11.52, -45.71) * mm});
            skLineSegment(sketch, "E3247", {"start": v(-11.52, -45.71) * mm, "end": v(-11.48, -45.55) * mm});
            skLineSegment(sketch, "E3248", {"start": v(-11.48, -45.55) * mm, "end": v(-11.44, -45.38) * mm});
            skLineSegment(sketch, "E3249", {"start": v(-11.44, -45.38) * mm, "end": v(-11.4, -45.22) * mm});
            skLineSegment(sketch, "E3250", {"start": v(-11.4, -45.22) * mm, "end": v(-11.36, -45.06) * mm});
            skLineSegment(sketch, "E3251", {"start": v(-11.36, -45.06) * mm, "end": v(-11.32, -44.9) * mm});
            skLineSegment(sketch, "E3252", {"start": v(-11.32, -44.9) * mm, "end": v(-11.29, -44.73) * mm});
            skLineSegment(sketch, "E3253", {"start": v(-11.29, -44.73) * mm, "end": v(-11.25, -44.57) * mm});
            skLineSegment(sketch, "E3254", {"start": v(-11.25, -44.57) * mm, "end": v(-11.2, -44.4) * mm});
            skLineSegment(sketch, "E3255", {"start": v(-11.2, -44.4) * mm, "end": v(-11.18, -44.29) * mm});
            skLineSegment(sketch, "E3256", {"start": v(-11.18, -44.29) * mm, "end": v(-11.02, -44.32) * mm});
            skLineSegment(sketch, "E3257", {"start": v(-11.02, -44.32) * mm, "end": v(-10.86, -44.35) * mm});
            skLineSegment(sketch, "E3258", {"start": v(-10.86, -44.35) * mm, "end": v(-10.7, -44.39) * mm});
            skLineSegment(sketch, "E3259", {"start": v(-10.7, -44.39) * mm, "end": v(-10.53, -44.42) * mm});
            skLineSegment(sketch, "E3260", {"start": v(-10.53, -44.42) * mm, "end": v(-10.37, -44.46) * mm});
            skLineSegment(sketch, "E3261", {"start": v(-10.37, -44.46) * mm, "end": v(-10.2, -44.5) * mm});
            skLineSegment(sketch, "E3262", {"start": v(-10.2, -44.5) * mm, "end": v(-10.04, -44.53) * mm});
            skLineSegment(sketch, "E3263", {"start": v(-10.04, -44.53) * mm, "end": v(-9.88, -44.56) * mm});
            skLineSegment(sketch, "E3264", {"start": v(-9.88, -44.56) * mm, "end": v(-9.72, -44.6) * mm});
            skLineSegment(sketch, "E3265", {"start": v(-9.72, -44.6) * mm, "end": v(-9.55, -44.63) * mm});
            skLineSegment(sketch, "E3266", {"start": v(-9.55, -44.63) * mm, "end": v(-9.4, -44.67) * mm});
            skLineSegment(sketch, "E3267", {"start": v(-9.4, -44.67) * mm, "end": v(-9.31, -44.68) * mm});
            skLineSegment(sketch, "E3268", {"start": v(-9.31, -44.68) * mm, "end": v(-9.34, -44.85) * mm});
            skLineSegment(sketch, "E3269", {"start": v(-9.34, -44.85) * mm, "end": v(-9.37, -45) * mm});
            skLineSegment(sketch, "E3270", {"start": v(-9.37, -45) * mm, "end": v(-9.4, -45.18) * mm});
            skLineSegment(sketch, "E3271", {"start": v(-9.4, -45.18) * mm, "end": v(-9.44, -45.34) * mm});
            skLineSegment(sketch, "E3272", {"start": v(-9.44, -45.34) * mm, "end": v(-9.47, -45.5) * mm});
            skLineSegment(sketch, "E3273", {"start": v(-9.47, -45.5) * mm, "end": v(-9.5, -45.67) * mm});
            skLineSegment(sketch, "E3274", {"start": v(-9.5, -45.67) * mm, "end": v(-9.53, -45.84) * mm});
            skLineSegment(sketch, "E3275", {"start": v(-9.53, -45.84) * mm, "end": v(-9.56, -46) * mm});
            skLineSegment(sketch, "E3276", {"start": v(-9.56, -46) * mm, "end": v(-9.6, -46.17) * mm});
            skLineSegment(sketch, "E3277", {"start": v(-9.6, -46.17) * mm, "end": v(-9.63, -46.33) * mm});
            skLineSegment(sketch, "E3278", {"start": v(-9.63, -46.33) * mm, "end": v(-9.66, -46.5) * mm});
            skLineSegment(sketch, "E3279", {"start": v(-9.66, -46.5) * mm, "end": v(-9.69, -46.66) * mm});
            skLineSegment(sketch, "E3280", {"start": v(-9.69, -46.66) * mm, "end": v(-9.72, -46.84) * mm});
            skLineSegment(sketch, "E3281", {"start": v(-9.72, -46.84) * mm, "end": v(-9.72, -47.01) * mm});
            skLineSegment(sketch, "E3282", {"start": v(-9.72, -47.01) * mm, "end": v(-9.68, -47.18) * mm});
            skLineSegment(sketch, "E3283", {"start": v(-9.68, -47.18) * mm, "end": v(-9.59, -47.33) * mm});
            skLineSegment(sketch, "E3284", {"start": v(-9.59, -47.33) * mm, "end": v(-9.46, -47.45) * mm});
            skLineSegment(sketch, "E3285", {"start": v(-9.46, -47.45) * mm, "end": v(-9.31, -47.54) * mm});
            skLineSegment(sketch, "E3286", {"start": v(-9.31, -47.54) * mm, "end": v(-9.15, -47.58) * mm});
            skLineSegment(sketch, "E3287", {"start": v(-9.15, -47.58) * mm, "end": v(-8.97, -47.58) * mm});
            skLineSegment(sketch, "E3288", {"start": v(-8.97, -47.58) * mm, "end": v(-8.8, -47.53) * mm});
            skLineSegment(sketch, "E3289", {"start": v(-8.8, -47.53) * mm, "end": v(-8.66, -47.44) * mm});
            skLineSegment(sketch, "E3290", {"start": v(-8.66, -47.44) * mm, "end": v(-8.53, -47.32) * mm});
            skLineSegment(sketch, "E3291", {"start": v(-8.53, -47.32) * mm, "end": v(-8.45, -47.17) * mm});
            skLineSegment(sketch, "E3292", {"start": v(-8.45, -47.17) * mm, "end": v(-8.41, -47) * mm});
            skLineSegment(sketch, "E3293", {"start": v(-8.41, -47) * mm, "end": v(-8.38, -46.84) * mm});
            skLineSegment(sketch, "E3294", {"start": v(-8.38, -46.84) * mm, "end": v(-8.35, -46.68) * mm});
            skLineSegment(sketch, "E3295", {"start": v(-8.35, -46.68) * mm, "end": v(-8.33, -46.51) * mm});
            skLineSegment(sketch, "E3296", {"start": v(-8.33, -46.51) * mm, "end": v(-8.3, -46.35) * mm});
            skLineSegment(sketch, "E3297", {"start": v(-8.3, -46.35) * mm, "end": v(-8.27, -46.18) * mm});
            skLineSegment(sketch, "E3298", {"start": v(-8.27, -46.18) * mm, "end": v(-8.25, -46.02) * mm});
            skLineSegment(sketch, "E3299", {"start": v(-8.25, -46.02) * mm, "end": v(-8.22, -45.85) * mm});
            skLineSegment(sketch, "E3300", {"start": v(-8.22, -45.85) * mm, "end": v(-8.2, -45.68) * mm});
            skLineSegment(sketch, "E3301", {"start": v(-8.2, -45.68) * mm, "end": v(-8.17, -45.52) * mm});
            skLineSegment(sketch, "E3302", {"start": v(-8.17, -45.52) * mm, "end": v(-8.14, -45.36) * mm});
            skLineSegment(sketch, "E3303", {"start": v(-8.14, -45.36) * mm, "end": v(-8.11, -45.19) * mm});
            skLineSegment(sketch, "E3304", {"start": v(-8.11, -45.19) * mm, "end": v(-8.09, -45.02) * mm});
            skLineSegment(sketch, "E3305", {"start": v(-8.09, -45.02) * mm, "end": v(-8.07, -44.9) * mm});
            skLineSegment(sketch, "E3306", {"start": v(-8.07, -44.9) * mm, "end": v(-7.9, -44.93) * mm});
            skLineSegment(sketch, "E3307", {"start": v(-7.9, -44.93) * mm, "end": v(-7.74, -44.95) * mm});
            skLineSegment(sketch, "E3308", {"start": v(-7.74, -44.95) * mm, "end": v(-7.57, -44.97) * mm});
            skLineSegment(sketch, "E3309", {"start": v(-7.57, -44.97) * mm, "end": v(-7.4, -45) * mm});
            skLineSegment(sketch, "E3310", {"start": v(-7.4, -45) * mm, "end": v(-7.24, -45.02) * mm});
            skLineSegment(sketch, "E3311", {"start": v(-7.24, -45.02) * mm, "end": v(-7.08, -45.04) * mm});
            skLineSegment(sketch, "E3312", {"start": v(-7.08, -45.04) * mm, "end": v(-6.91, -45.06) * mm});
            skLineSegment(sketch, "E3313", {"start": v(-6.91, -45.06) * mm, "end": v(-6.75, -45.09) * mm});
            skLineSegment(sketch, "E3314", {"start": v(-6.75, -45.09) * mm, "end": v(-6.58, -45.11) * mm});
            skLineSegment(sketch, "E3315", {"start": v(-6.58, -45.11) * mm, "end": v(-6.42, -45.13) * mm});
            skLineSegment(sketch, "E3316", {"start": v(-6.42, -45.13) * mm, "end": v(-6.25, -45.16) * mm});
            skLineSegment(sketch, "E3317", {"start": v(-6.25, -45.16) * mm, "end": v(-6.17, -45.17) * mm});
            skLineSegment(sketch, "E3318", {"start": v(-6.17, -45.17) * mm, "end": v(-6.2, -45.33) * mm});
            skLineSegment(sketch, "E3319", {"start": v(-6.2, -45.33) * mm, "end": v(-6.21, -45.5) * mm});
            skLineSegment(sketch, "E3320", {"start": v(-6.21, -45.5) * mm, "end": v(-6.23, -45.67) * mm});
            skLineSegment(sketch, "E3321", {"start": v(-6.23, -45.67) * mm, "end": v(-6.25, -45.83) * mm});
            skLineSegment(sketch, "E3322", {"start": v(-6.25, -45.83) * mm, "end": v(-6.27, -46) * mm});
            skLineSegment(sketch, "E3323", {"start": v(-6.27, -46) * mm, "end": v(-6.3, -46.17) * mm});
            skLineSegment(sketch, "E3324", {"start": v(-6.3, -46.17) * mm, "end": v(-6.31, -46.33) * mm});
            skLineSegment(sketch, "E3325", {"start": v(-6.31, -46.33) * mm, "end": v(-6.33, -46.5) * mm});
            skLineSegment(sketch, "E3326", {"start": v(-6.33, -46.5) * mm, "end": v(-6.35, -46.67) * mm});
            skLineSegment(sketch, "E3327", {"start": v(-6.35, -46.67) * mm, "end": v(-6.37, -46.83) * mm});
            skLineSegment(sketch, "E3328", {"start": v(-6.37, -46.83) * mm, "end": v(-6.4, -47) * mm});
            skLineSegment(sketch, "E3329", {"start": v(-6.4, -47) * mm, "end": v(-6.41, -47.17) * mm});
            skLineSegment(sketch, "E3330", {"start": v(-6.41, -47.17) * mm, "end": v(-6.43, -47.35) * mm});
            skLineSegment(sketch, "E3331", {"start": v(-6.43, -47.35) * mm, "end": v(-6.42, -47.52) * mm});
            skLineSegment(sketch, "E3332", {"start": v(-6.42, -47.52) * mm, "end": v(-6.36, -47.68) * mm});
            skLineSegment(sketch, "E3333", {"start": v(-6.36, -47.68) * mm, "end": v(-6.26, -47.83) * mm});
            skLineSegment(sketch, "E3334", {"start": v(-6.26, -47.83) * mm, "end": v(-6.13, -47.94) * mm});
            skLineSegment(sketch, "E3335", {"start": v(-6.13, -47.94) * mm, "end": v(-5.98, -48.02) * mm});
            skLineSegment(sketch, "E3336", {"start": v(-5.98, -48.02) * mm, "end": v(-5.8, -48.05) * mm});
            skLineSegment(sketch, "E3337", {"start": v(-5.8, -48.05) * mm, "end": v(-5.63, -48.03) * mm});
            skLineSegment(sketch, "E3338", {"start": v(-5.63, -48.03) * mm, "end": v(-5.47, -47.98) * mm});
            skLineSegment(sketch, "E3339", {"start": v(-5.47, -47.98) * mm, "end": v(-5.33, -47.88) * mm});
            skLineSegment(sketch, "E3340", {"start": v(-5.33, -47.88) * mm, "end": v(-5.21, -47.74) * mm});
            skLineSegment(sketch, "E3341", {"start": v(-5.21, -47.74) * mm, "end": v(-5.14, -47.59) * mm});
            skLineSegment(sketch, "E3342", {"start": v(-5.14, -47.59) * mm, "end": v(-5.11, -47.42) * mm});
            skLineSegment(sketch, "E3343", {"start": v(-5.11, -47.42) * mm, "end": v(-5.1, -47.26) * mm});
            skLineSegment(sketch, "E3344", {"start": v(-5.1, -47.26) * mm, "end": v(-5.08, -47.1) * mm});
            skLineSegment(sketch, "E3345", {"start": v(-5.08, -47.1) * mm, "end": v(-5.06, -46.93) * mm});
            skLineSegment(sketch, "E3346", {"start": v(-5.06, -46.93) * mm, "end": v(-5.05, -46.76) * mm});
            skLineSegment(sketch, "E3347", {"start": v(-5.05, -46.76) * mm, "end": v(-5.03, -46.6) * mm});
            skLineSegment(sketch, "E3348", {"start": v(-5.03, -46.6) * mm, "end": v(-5.02, -46.42) * mm});
            skLineSegment(sketch, "E3349", {"start": v(-5.02, -46.42) * mm, "end": v(-5, -46.26) * mm});
            skLineSegment(sketch, "E3350", {"start": v(-5, -46.26) * mm, "end": v(-4.99, -46.09) * mm});
            skLineSegment(sketch, "E3351", {"start": v(-4.99, -46.09) * mm, "end": v(-4.97, -45.92) * mm});
            skLineSegment(sketch, "E3352", {"start": v(-4.97, -45.92) * mm, "end": v(-4.96, -45.76) * mm});
            skLineSegment(sketch, "E3353", {"start": v(-4.96, -45.76) * mm, "end": v(-4.94, -45.59) * mm});
            skLineSegment(sketch, "E3354", {"start": v(-4.94, -45.59) * mm, "end": v(-4.93, -45.42) * mm});
            skLineSegment(sketch, "E3355", {"start": v(-4.93, -45.42) * mm, "end": v(-4.92, -45.3) * mm});
            skLineSegment(sketch, "E3356", {"start": v(-4.92, -45.3) * mm, "end": v(-4.75, -45.31) * mm});
            skLineSegment(sketch, "E3357", {"start": v(-4.75, -45.31) * mm, "end": v(-4.58, -45.32) * mm});
            skLineSegment(sketch, "E3358", {"start": v(-4.58, -45.32) * mm, "end": v(-4.42, -45.33) * mm});
            skLineSegment(sketch, "E3359", {"start": v(-4.42, -45.33) * mm, "end": v(-4.25, -45.35) * mm});
            skLineSegment(sketch, "E3360", {"start": v(-4.25, -45.35) * mm, "end": v(-4.09, -45.36) * mm});
            skLineSegment(sketch, "E3361", {"start": v(-4.09, -45.36) * mm, "end": v(-3.92, -45.37) * mm});
            skLineSegment(sketch, "E3362", {"start": v(-3.92, -45.37) * mm, "end": v(-3.75, -45.38) * mm});
            skLineSegment(sketch, "E3363", {"start": v(-3.75, -45.38) * mm, "end": v(-3.59, -45.4) * mm});
            skLineSegment(sketch, "E3364", {"start": v(-3.59, -45.4) * mm, "end": v(-3.42, -45.4) * mm});
            skLineSegment(sketch, "E3365", {"start": v(-3.42, -45.4) * mm, "end": v(-3.26, -45.42) * mm});
            skLineSegment(sketch, "E3366", {"start": v(-3.26, -45.42) * mm, "end": v(-3.1, -45.43) * mm});
            skLineSegment(sketch, "E3367", {"start": v(-3.1, -45.43) * mm, "end": v(-3, -45.43) * mm});
            skLineSegment(sketch, "E3368", {"start": v(-3, -45.43) * mm, "end": v(-3.02, -45.6) * mm});
            skLineSegment(sketch, "E3369", {"start": v(-3.02, -45.6) * mm, "end": v(-3.03, -45.77) * mm});
            skLineSegment(sketch, "E3370", {"start": v(-3.03, -45.77) * mm, "end": v(-3.03, -45.94) * mm});
            skLineSegment(sketch, "E3371", {"start": v(-3.03, -45.94) * mm, "end": v(-3.04, -46.1) * mm});
            skLineSegment(sketch, "E3372", {"start": v(-3.04, -46.1) * mm, "end": v(-3.05, -46.27) * mm});
            skLineSegment(sketch, "E3373", {"start": v(-3.05, -46.27) * mm, "end": v(-3.06, -46.44) * mm});
            skLineSegment(sketch, "E3374", {"start": v(-3.06, -46.44) * mm, "end": v(-3.07, -46.6) * mm});
            skLineSegment(sketch, "E3375", {"start": v(-3.07, -46.6) * mm, "end": v(-3.08, -46.77) * mm});
            skLineSegment(sketch, "E3376", {"start": v(-3.08, -46.77) * mm, "end": v(-3.08, -46.94) * mm});
            skLineSegment(sketch, "E3377", {"start": v(-3.08, -46.94) * mm, "end": v(-3.1, -47.1) * mm});
            skLineSegment(sketch, "E3378", {"start": v(-3.1, -47.1) * mm, "end": v(-3.1, -47.28) * mm});
            skLineSegment(sketch, "E3379", {"start": v(-3.1, -47.28) * mm, "end": v(-3.1, -47.45) * mm});
            skLineSegment(sketch, "E3380", {"start": v(-3.1, -47.45) * mm, "end": v(-3.12, -47.63) * mm});
            skLineSegment(sketch, "E3381", {"start": v(-3.12, -47.63) * mm, "end": v(-3.1, -47.8) * mm});
            skLineSegment(sketch, "E3382", {"start": v(-3.1, -47.8) * mm, "end": v(-3.02, -47.96) * mm});
            skLineSegment(sketch, "E3383", {"start": v(-3.02, -47.96) * mm, "end": v(-2.92, -48.1) * mm});
            skLineSegment(sketch, "E3384", {"start": v(-2.92, -48.1) * mm, "end": v(-2.78, -48.2) * mm});
            skLineSegment(sketch, "E3385", {"start": v(-2.78, -48.2) * mm, "end": v(-2.61, -48.26) * mm});
            skLineSegment(sketch, "E3386", {"start": v(-2.61, -48.26) * mm, "end": v(-2.44, -48.28) * mm});
            skLineSegment(sketch, "E3387", {"start": v(-2.44, -48.28) * mm, "end": v(-2.27, -48.25) * mm});
            skLineSegment(sketch, "E3388", {"start": v(-2.27, -48.25) * mm, "end": v(-2.11, -48.18) * mm});
            skLineSegment(sketch, "E3389", {"start": v(-2.11, -48.18) * mm, "end": v(-1.98, -48.08) * mm});
            skLineSegment(sketch, "E3390", {"start": v(-1.98, -48.08) * mm, "end": v(-1.87, -47.94) * mm});
            skLineSegment(sketch, "E3391", {"start": v(-1.87, -47.94) * mm, "end": v(-1.81, -47.77) * mm});
            skLineSegment(sketch, "E3392", {"start": v(-1.81, -47.77) * mm, "end": v(-1.8, -47.6) * mm});
            skLineSegment(sketch, "E3393", {"start": v(-1.8, -47.6) * mm, "end": v(-1.79, -47.44) * mm});
            skLineSegment(sketch, "E3394", {"start": v(-1.79, -47.44) * mm, "end": v(-1.78, -47.28) * mm});
            skLineSegment(sketch, "E3395", {"start": v(-1.78, -47.28) * mm, "end": v(-1.78, -47.11) * mm});
            skLineSegment(sketch, "E3396", {"start": v(-1.78, -47.11) * mm, "end": v(-1.78, -46.94) * mm});
            skLineSegment(sketch, "E3397", {"start": v(-1.78, -46.94) * mm, "end": v(-1.77, -46.77) * mm});
            skLineSegment(sketch, "E3398", {"start": v(-1.77, -46.77) * mm, "end": v(-1.77, -46.6) * mm});
            skLineSegment(sketch, "E3399", {"start": v(-1.77, -46.6) * mm, "end": v(-1.77, -46.44) * mm});
            skLineSegment(sketch, "E3400", {"start": v(-1.77, -46.44) * mm, "end": v(-1.76, -46.27) * mm});
            skLineSegment(sketch, "E3401", {"start": v(-1.76, -46.27) * mm, "end": v(-1.76, -46.1) * mm});
            skLineSegment(sketch, "E3402", {"start": v(-1.76, -46.1) * mm, "end": v(-1.76, -45.94) * mm});
            skLineSegment(sketch, "E3403", {"start": v(-1.76, -45.94) * mm, "end": v(-1.75, -45.77) * mm});
            skLineSegment(sketch, "E3404", {"start": v(-1.75, -45.77) * mm, "end": v(-1.75, -45.6) * mm});
            skLineSegment(sketch, "E3405", {"start": v(-1.75, -45.6) * mm, "end": v(-1.75, -45.48) * mm});
            skLineSegment(sketch, "E3406", {"start": v(-1.75, -45.48) * mm, "end": v(-1.58, -45.48) * mm});
            skLineSegment(sketch, "E3407", {"start": v(-1.58, -45.48) * mm, "end": v(-1.41, -45.48) * mm});
            skLineSegment(sketch, "E3408", {"start": v(-1.41, -45.48) * mm, "end": v(-1.25, -45.48) * mm});
            skLineSegment(sketch, "E3409", {"start": v(-1.25, -45.48) * mm, "end": v(-1.08, -45.48) * mm});
            skLineSegment(sketch, "E3410", {"start": v(-1.08, -45.48) * mm, "end": v(-0.91, -45.48) * mm});
            skLineSegment(sketch, "E3411", {"start": v(-0.91, -45.48) * mm, "end": v(-0.75, -45.48) * mm});
            skLineSegment(sketch, "E3412", {"start": v(-0.75, -45.48) * mm, "end": v(-0.58, -45.48) * mm});
            skLineSegment(sketch, "E3413", {"start": v(-0.58, -45.48) * mm, "end": v(-0.42, -45.48) * mm});
            skLineSegment(sketch, "E3414", {"start": v(-0.42, -45.48) * mm, "end": v(-0.25, -45.48) * mm});
            skLineSegment(sketch, "E3415", {"start": v(-0.25, -45.48) * mm, "end": v(-0.08, -45.48) * mm});
            skLineSegment(sketch, "E3416", {"start": v(-0.08, -45.48) * mm, "end": v(0.08, -45.48) * mm});
            skLineSegment(sketch, "E3417", {"start": v(0.08, -45.48) * mm, "end": v(0.16, -45.48) * mm});
            skLineSegment(sketch, "E3418", {"start": v(0.16, -45.48) * mm, "end": v(0.17, -45.64) * mm});
            skLineSegment(sketch, "E3419", {"start": v(0.17, -45.64) * mm, "end": v(0.17, -45.81) * mm});
            skLineSegment(sketch, "E3420", {"start": v(0.17, -45.81) * mm, "end": v(0.18, -45.98) * mm});
            skLineSegment(sketch, "E3421", {"start": v(0.18, -45.98) * mm, "end": v(0.18, -46.15) * mm});
            skLineSegment(sketch, "E3422", {"start": v(0.18, -46.15) * mm, "end": v(0.18, -46.31) * mm});
            skLineSegment(sketch, "E3423", {"start": v(0.18, -46.31) * mm, "end": v(0.19, -46.49) * mm});
            skLineSegment(sketch, "E3424", {"start": v(0.19, -46.49) * mm, "end": v(0.19, -46.65) * mm});
            skLineSegment(sketch, "E3425", {"start": v(0.19, -46.65) * mm, "end": v(0.2, -46.82) * mm});
            skLineSegment(sketch, "E3426", {"start": v(0.2, -46.82) * mm, "end": v(0.2, -46.99) * mm});
            skLineSegment(sketch, "E3427", {"start": v(0.2, -46.99) * mm, "end": v(0.2, -47.16) * mm});
            skLineSegment(sketch, "E3428", {"start": v(0.2, -47.16) * mm, "end": v(0.2, -47.32) * mm});
            skLineSegment(sketch, "E3429", {"start": v(0.2, -47.32) * mm, "end": v(0.2, -47.5) * mm});
            skLineSegment(sketch, "E3430", {"start": v(0.2, -47.5) * mm, "end": v(0.21, -47.67) * mm});
            skLineSegment(sketch, "E3431", {"start": v(0.21, -47.67) * mm, "end": v(0.25, -47.84) * mm});
            skLineSegment(sketch, "E3432", {"start": v(0.25, -47.84) * mm, "end": v(0.33, -48) * mm});
            skLineSegment(sketch, "E3433", {"start": v(0.33, -48) * mm, "end": v(0.44, -48.12) * mm});
            skLineSegment(sketch, "E3434", {"start": v(0.44, -48.12) * mm, "end": v(0.6, -48.22) * mm});
            skLineSegment(sketch, "E3435", {"start": v(0.6, -48.22) * mm, "end": v(0.76, -48.27) * mm});
            skLineSegment(sketch, "E3436", {"start": v(0.76, -48.27) * mm, "end": v(0.93, -48.28) * mm});
            skLineSegment(sketch, "E3437", {"start": v(0.93, -48.28) * mm, "end": v(1.1, -48.24) * mm});
            skLineSegment(sketch, "E3438", {"start": v(1.1, -48.24) * mm, "end": v(1.25, -48.16) * mm});
            skLineSegment(sketch, "E3439", {"start": v(1.25, -48.16) * mm, "end": v(1.38, -48.04) * mm});
            skLineSegment(sketch, "E3440", {"start": v(1.38, -48.04) * mm, "end": v(1.47, -47.9) * mm});
            skLineSegment(sketch, "E3441", {"start": v(1.47, -47.9) * mm, "end": v(1.52, -47.73) * mm});
            skLineSegment(sketch, "E3442", {"start": v(1.52, -47.73) * mm, "end": v(1.53, -47.56) * mm});
            skLineSegment(sketch, "E3443", {"start": v(1.53, -47.56) * mm, "end": v(1.52, -47.4) * mm});
            skLineSegment(sketch, "E3444", {"start": v(1.52, -47.4) * mm, "end": v(1.52, -47.23) * mm});
            skLineSegment(sketch, "E3445", {"start": v(1.52, -47.23) * mm, "end": v(1.5, -47.06) * mm});
            skLineSegment(sketch, "E3446", {"start": v(1.5, -47.06) * mm, "end": v(1.5, -46.9) * mm});
            skLineSegment(sketch, "E3447", {"start": v(1.5, -46.9) * mm, "end": v(1.5, -46.73) * mm});
            skLineSegment(sketch, "E3448", {"start": v(1.5, -46.73) * mm, "end": v(1.48, -46.56) * mm});
            skLineSegment(sketch, "E3449", {"start": v(1.48, -46.56) * mm, "end": v(1.48, -46.4) * mm});
            skLineSegment(sketch, "E3450", {"start": v(1.48, -46.4) * mm, "end": v(1.47, -46.22) * mm});
            skLineSegment(sketch, "E3451", {"start": v(1.47, -46.22) * mm, "end": v(1.46, -46.06) * mm});
            skLineSegment(sketch, "E3452", {"start": v(1.46, -46.06) * mm, "end": v(1.45, -45.9) * mm});
            skLineSegment(sketch, "E3453", {"start": v(1.45, -45.9) * mm, "end": v(1.44, -45.72) * mm});
            skLineSegment(sketch, "E3454", {"start": v(1.44, -45.72) * mm, "end": v(1.43, -45.55) * mm});
            skLineSegment(sketch, "E3455", {"start": v(1.43, -45.55) * mm, "end": v(1.43, -45.43) * mm});
            skLineSegment(sketch, "E3456", {"start": v(1.43, -45.43) * mm, "end": v(1.6, -45.42) * mm});
            skLineSegment(sketch, "E3457", {"start": v(1.6, -45.42) * mm, "end": v(1.76, -45.41) * mm});
            skLineSegment(sketch, "E3458", {"start": v(1.76, -45.41) * mm, "end": v(1.93, -45.4) * mm});
            skLineSegment(sketch, "E3459", {"start": v(1.93, -45.4) * mm, "end": v(2.1, -45.39) * mm});
            skLineSegment(sketch, "E3460", {"start": v(2.1, -45.39) * mm, "end": v(2.26, -45.38) * mm});
            skLineSegment(sketch, "E3461", {"start": v(2.26, -45.38) * mm, "end": v(2.42, -45.36) * mm});
            skLineSegment(sketch, "E3462", {"start": v(2.42, -45.36) * mm, "end": v(2.59, -45.35) * mm});
            skLineSegment(sketch, "E3463", {"start": v(2.59, -45.35) * mm, "end": v(2.76, -45.34) * mm});
            skLineSegment(sketch, "E3464", {"start": v(2.76, -45.34) * mm, "end": v(2.92, -45.33) * mm});
            skLineSegment(sketch, "E3465", {"start": v(2.92, -45.33) * mm, "end": v(3.09, -45.32) * mm});
            skLineSegment(sketch, "E3466", {"start": v(3.09, -45.32) * mm, "end": v(3.25, -45.3) * mm});
            skLineSegment(sketch, "E3467", {"start": v(3.25, -45.3) * mm, "end": v(3.33, -45.3) * mm});
            skLineSegment(sketch, "E3468", {"start": v(3.33, -45.3) * mm, "end": v(3.35, -45.47) * mm});
            skLineSegment(sketch, "E3469", {"start": v(3.35, -45.47) * mm, "end": v(3.37, -45.63) * mm});
            skLineSegment(sketch, "E3470", {"start": v(3.37, -45.63) * mm, "end": v(3.38, -45.8) * mm});
            skLineSegment(sketch, "E3471", {"start": v(3.38, -45.8) * mm, "end": v(3.4, -45.97) * mm});
            skLineSegment(sketch, "E3472", {"start": v(3.4, -45.97) * mm, "end": v(3.41, -46.13) * mm});
            skLineSegment(sketch, "E3473", {"start": v(3.41, -46.13) * mm, "end": v(3.43, -46.3) * mm});
            skLineSegment(sketch, "E3474", {"start": v(3.43, -46.3) * mm, "end": v(3.44, -46.47) * mm});
            skLineSegment(sketch, "E3475", {"start": v(3.44, -46.47) * mm, "end": v(3.46, -46.64) * mm});
            skLineSegment(sketch, "E3476", {"start": v(3.46, -46.64) * mm, "end": v(3.47, -46.8) * mm});
            skLineSegment(sketch, "E3477", {"start": v(3.47, -46.8) * mm, "end": v(3.49, -46.97) * mm});
            skLineSegment(sketch, "E3478", {"start": v(3.49, -46.97) * mm, "end": v(3.5, -47.14) * mm});
            skLineSegment(sketch, "E3479", {"start": v(3.5, -47.14) * mm, "end": v(3.52, -47.3) * mm});
            skLineSegment(sketch, "E3480", {"start": v(3.52, -47.3) * mm, "end": v(3.53, -47.49) * mm});
            skLineSegment(sketch, "E3481", {"start": v(3.53, -47.49) * mm, "end": v(3.58, -47.65) * mm});
            skLineSegment(sketch, "E3482", {"start": v(3.58, -47.65) * mm, "end": v(3.67, -47.8) * mm});
            skLineSegment(sketch, "E3483", {"start": v(3.67, -47.8) * mm, "end": v(3.8, -47.92) * mm});
            skLineSegment(sketch, "E3484", {"start": v(3.8, -47.92) * mm, "end": v(3.95, -48) * mm});
            skLineSegment(sketch, "E3485", {"start": v(3.95, -48) * mm, "end": v(4.12, -48.04) * mm});
            skLineSegment(sketch, "E3486", {"start": v(4.12, -48.04) * mm, "end": v(4.3, -48.04) * mm});
            skLineSegment(sketch, "E3487", {"start": v(4.3, -48.04) * mm, "end": v(4.46, -48) * mm});
            skLineSegment(sketch, "E3488", {"start": v(4.46, -48) * mm, "end": v(4.6, -47.9) * mm});
            skLineSegment(sketch, "E3489", {"start": v(4.6, -47.9) * mm, "end": v(4.73, -47.77) * mm});
            skLineSegment(sketch, "E3490", {"start": v(4.73, -47.77) * mm, "end": v(4.8, -47.62) * mm});
            skLineSegment(sketch, "E3491", {"start": v(4.8, -47.62) * mm, "end": v(4.85, -47.45) * mm});
            skLineSegment(sketch, "E3492", {"start": v(4.85, -47.45) * mm, "end": v(4.84, -47.29) * mm});
            skLineSegment(sketch, "E3493", {"start": v(4.84, -47.29) * mm, "end": v(4.82, -47.12) * mm});
            skLineSegment(sketch, "E3494", {"start": v(4.82, -47.12) * mm, "end": v(4.8, -46.95) * mm});
            skLineSegment(sketch, "E3495", {"start": v(4.8, -46.95) * mm, "end": v(4.79, -46.79) * mm});
            skLineSegment(sketch, "E3496", {"start": v(4.79, -46.79) * mm, "end": v(4.77, -46.62) * mm});
            skLineSegment(sketch, "E3497", {"start": v(4.77, -46.62) * mm, "end": v(4.75, -46.45) * mm});
            skLineSegment(sketch, "E3498", {"start": v(4.75, -46.45) * mm, "end": v(4.73, -46.29) * mm});
            skLineSegment(sketch, "E3499", {"start": v(4.73, -46.29) * mm, "end": v(4.7, -46.12) * mm});
            skLineSegment(sketch, "E3500", {"start": v(4.7, -46.12) * mm, "end": v(4.69, -45.95) * mm});
            skLineSegment(sketch, "E3501", {"start": v(4.69, -45.95) * mm, "end": v(4.67, -45.79) * mm});
            skLineSegment(sketch, "E3502", {"start": v(4.67, -45.79) * mm, "end": v(4.65, -45.62) * mm});
            skLineSegment(sketch, "E3503", {"start": v(4.65, -45.62) * mm, "end": v(4.63, -45.45) * mm});
            skLineSegment(sketch, "E3504", {"start": v(4.63, -45.45) * mm, "end": v(4.6, -45.29) * mm});
            skLineSegment(sketch, "E3505", {"start": v(4.6, -45.29) * mm, "end": v(4.6, -45.17) * mm});
            skLineSegment(sketch, "E3506", {"start": v(4.6, -45.17) * mm, "end": v(4.76, -45.14) * mm});
            skLineSegment(sketch, "E3507", {"start": v(4.76, -45.14) * mm, "end": v(4.92, -45.12) * mm});
            skLineSegment(sketch, "E3508", {"start": v(4.92, -45.12) * mm, "end": v(5.09, -45.1) * mm});
            skLineSegment(sketch, "E3509", {"start": v(5.09, -45.1) * mm, "end": v(5.25, -45.08) * mm});
            skLineSegment(sketch, "E3510", {"start": v(5.25, -45.08) * mm, "end": v(5.42, -45.05) * mm});
            skLineSegment(sketch, "E3511", {"start": v(5.42, -45.05) * mm, "end": v(5.58, -45.03) * mm});
            skLineSegment(sketch, "E3512", {"start": v(5.58, -45.03) * mm, "end": v(5.75, -45) * mm});
            skLineSegment(sketch, "E3513", {"start": v(5.75, -45) * mm, "end": v(5.91, -44.98) * mm});
            skLineSegment(sketch, "E3514", {"start": v(5.91, -44.98) * mm, "end": v(6.07, -44.96) * mm});
            skLineSegment(sketch, "E3515", {"start": v(6.07, -44.96) * mm, "end": v(6.24, -44.94) * mm});
            skLineSegment(sketch, "E3516", {"start": v(6.24, -44.94) * mm, "end": v(6.4, -44.91) * mm});
            skLineSegment(sketch, "E3517", {"start": v(6.4, -44.91) * mm, "end": v(6.48, -44.9) * mm});
            skLineSegment(sketch, "E3518", {"start": v(6.48, -44.9) * mm, "end": v(6.51, -45.07) * mm});
            skLineSegment(sketch, "E3519", {"start": v(6.51, -45.07) * mm, "end": v(6.54, -45.23) * mm});
            skLineSegment(sketch, "E3520", {"start": v(6.54, -45.23) * mm, "end": v(6.57, -45.4) * mm});
            skLineSegment(sketch, "E3521", {"start": v(6.57, -45.4) * mm, "end": v(6.6, -45.56) * mm});
            skLineSegment(sketch, "E3522", {"start": v(6.6, -45.56) * mm, "end": v(6.62, -45.73) * mm});
            skLineSegment(sketch, "E3523", {"start": v(6.62, -45.73) * mm, "end": v(6.65, -45.9) * mm});
            skLineSegment(sketch, "E3524", {"start": v(6.65, -45.9) * mm, "end": v(6.67, -46.06) * mm});
            skLineSegment(sketch, "E3525", {"start": v(6.67, -46.06) * mm, "end": v(6.7, -46.23) * mm});
            skLineSegment(sketch, "E3526", {"start": v(6.7, -46.23) * mm, "end": v(6.73, -46.4) * mm});
            skLineSegment(sketch, "E3527", {"start": v(6.73, -46.4) * mm, "end": v(6.75, -46.56) * mm});
            skLineSegment(sketch, "E3528", {"start": v(6.75, -46.56) * mm, "end": v(6.78, -46.72) * mm});
            skLineSegment(sketch, "E3529", {"start": v(6.78, -46.72) * mm, "end": v(6.8, -46.9) * mm});
            skLineSegment(sketch, "E3530", {"start": v(6.8, -46.9) * mm, "end": v(6.84, -47.07) * mm});
            skLineSegment(sketch, "E3531", {"start": v(6.84, -47.07) * mm, "end": v(6.9, -47.23) * mm});
            skLineSegment(sketch, "E3532", {"start": v(6.9, -47.23) * mm, "end": v(7, -47.37) * mm});
            skLineSegment(sketch, "E3533", {"start": v(7, -47.37) * mm, "end": v(7.13, -47.48) * mm});
            skLineSegment(sketch, "E3534", {"start": v(7.13, -47.48) * mm, "end": v(7.29, -47.56) * mm});
            skLineSegment(sketch, "E3535", {"start": v(7.29, -47.56) * mm, "end": v(7.46, -47.58) * mm});
            skLineSegment(sketch, "E3536", {"start": v(7.46, -47.58) * mm, "end": v(7.63, -47.57) * mm});
            skLineSegment(sketch, "E3537", {"start": v(7.63, -47.57) * mm, "end": v(7.8, -47.5) * mm});
            skLineSegment(sketch, "E3538", {"start": v(7.8, -47.5) * mm, "end": v(7.94, -47.4) * mm});
            skLineSegment(sketch, "E3539", {"start": v(7.94, -47.4) * mm, "end": v(8.05, -47.27) * mm});
            skLineSegment(sketch, "E3540", {"start": v(8.05, -47.27) * mm, "end": v(8.12, -47.11) * mm});
            skLineSegment(sketch, "E3541", {"start": v(8.12, -47.11) * mm, "end": v(8.14, -46.94) * mm});
            skLineSegment(sketch, "E3542", {"start": v(8.14, -46.94) * mm, "end": v(8.13, -46.78) * mm});
            skLineSegment(sketch, "E3543", {"start": v(8.13, -46.78) * mm, "end": v(8.1, -46.61) * mm});
            skLineSegment(sketch, "E3544", {"start": v(8.1, -46.61) * mm, "end": v(8.07, -46.45) * mm});
            skLineSegment(sketch, "E3545", {"start": v(8.07, -46.45) * mm, "end": v(8.04, -46.29) * mm});
            skLineSegment(sketch, "E3546", {"start": v(8.04, -46.29) * mm, "end": v(8, -46.12) * mm});
            skLineSegment(sketch, "E3547", {"start": v(8, -46.12) * mm, "end": v(7.97, -45.96) * mm});
            skLineSegment(sketch, "E3548", {"start": v(7.97, -45.96) * mm, "end": v(7.94, -45.8) * mm});
            skLineSegment(sketch, "E3549", {"start": v(7.94, -45.8) * mm, "end": v(7.91, -45.63) * mm});
            skLineSegment(sketch, "E3550", {"start": v(7.91, -45.63) * mm, "end": v(7.88, -45.46) * mm});
            skLineSegment(sketch, "E3551", {"start": v(7.88, -45.46) * mm, "end": v(7.85, -45.3) * mm});
            skLineSegment(sketch, "E3552", {"start": v(7.85, -45.3) * mm, "end": v(7.82, -45.13) * mm});
            skLineSegment(sketch, "E3553", {"start": v(7.82, -45.13) * mm, "end": v(7.78, -44.97) * mm});
            skLineSegment(sketch, "E3554", {"start": v(7.78, -44.97) * mm, "end": v(7.75, -44.8) * mm});
            skLineSegment(sketch, "E3555", {"start": v(7.75, -44.8) * mm, "end": v(7.73, -44.68) * mm});
            skLineSegment(sketch, "E3556", {"start": v(7.73, -44.68) * mm, "end": v(7.9, -44.65) * mm});
            skLineSegment(sketch, "E3557", {"start": v(7.9, -44.65) * mm, "end": v(8.06, -44.61) * mm});
            skLineSegment(sketch, "E3558", {"start": v(8.06, -44.61) * mm, "end": v(8.22, -44.58) * mm});
            skLineSegment(sketch, "E3559", {"start": v(8.22, -44.58) * mm, "end": v(8.38, -44.54) * mm});
            skLineSegment(sketch, "E3560", {"start": v(8.38, -44.54) * mm, "end": v(8.54, -44.5) * mm});
            skLineSegment(sketch, "E3561", {"start": v(8.54, -44.5) * mm, "end": v(8.7, -44.47) * mm});
            skLineSegment(sketch, "E3562", {"start": v(8.7, -44.47) * mm, "end": v(8.87, -44.44) * mm});
            skLineSegment(sketch, "E3563", {"start": v(8.87, -44.44) * mm, "end": v(9.03, -44.4) * mm});
            skLineSegment(sketch, "E3564", {"start": v(9.03, -44.4) * mm, "end": v(9.2, -44.37) * mm});
            skLineSegment(sketch, "E3565", {"start": v(9.2, -44.37) * mm, "end": v(9.36, -44.34) * mm});
            skLineSegment(sketch, "E3566", {"start": v(9.36, -44.34) * mm, "end": v(9.52, -44.3) * mm});
            skLineSegment(sketch, "E3567", {"start": v(9.52, -44.3) * mm, "end": v(9.6, -44.29) * mm});
            skLineSegment(sketch, "E3568", {"start": v(9.6, -44.29) * mm, "end": v(9.64, -44.45) * mm});
            skLineSegment(sketch, "E3569", {"start": v(9.64, -44.45) * mm, "end": v(9.68, -44.6) * mm});
            skLineSegment(sketch, "E3570", {"start": v(9.68, -44.6) * mm, "end": v(9.71, -44.78) * mm});
            skLineSegment(sketch, "E3571", {"start": v(9.71, -44.78) * mm, "end": v(9.75, -44.94) * mm});
            skLineSegment(sketch, "E3572", {"start": v(9.75, -44.94) * mm, "end": v(9.8, -45.1) * mm});
            skLineSegment(sketch, "E3573", {"start": v(9.8, -45.1) * mm, "end": v(9.83, -45.27) * mm});
            skLineSegment(sketch, "E3574", {"start": v(9.83, -45.27) * mm, "end": v(9.87, -45.43) * mm});
            skLineSegment(sketch, "E3575", {"start": v(9.87, -45.43) * mm, "end": v(9.9, -45.6) * mm});
            skLineSegment(sketch, "E3576", {"start": v(9.9, -45.6) * mm, "end": v(9.94, -45.76) * mm});
            skLineSegment(sketch, "E3577", {"start": v(9.94, -45.76) * mm, "end": v(9.98, -45.92) * mm});
            skLineSegment(sketch, "E3578", {"start": v(9.98, -45.92) * mm, "end": v(10.02, -46.08) * mm});
            skLineSegment(sketch, "E3579", {"start": v(10.02, -46.08) * mm, "end": v(10.06, -46.25) * mm});
            skLineSegment(sketch, "E3580", {"start": v(10.06, -46.25) * mm, "end": v(10.1, -46.42) * mm});
            skLineSegment(sketch, "E3581", {"start": v(10.1, -46.42) * mm, "end": v(10.17, -46.58) * mm});
            skLineSegment(sketch, "E3582", {"start": v(10.17, -46.58) * mm, "end": v(10.28, -46.71) * mm});
            skLineSegment(sketch, "E3583", {"start": v(10.28, -46.71) * mm, "end": v(10.42, -46.82) * mm});
            skLineSegment(sketch, "E3584", {"start": v(10.42, -46.82) * mm, "end": v(10.59, -46.88) * mm});
            skLineSegment(sketch, "E3585", {"start": v(10.59, -46.88) * mm, "end": v(10.76, -46.9) * mm});
            skLineSegment(sketch, "E3586", {"start": v(10.76, -46.9) * mm, "end": v(10.93, -46.86) * mm});
            skLineSegment(sketch, "E3587", {"start": v(10.93, -46.86) * mm, "end": v(11.09, -46.8) * mm});
            skLineSegment(sketch, "E3588", {"start": v(11.09, -46.8) * mm, "end": v(11.22, -46.68) * mm});
            skLineSegment(sketch, "E3589", {"start": v(11.22, -46.68) * mm, "end": v(11.32, -46.54) * mm});
            skLineSegment(sketch, "E3590", {"start": v(11.32, -46.54) * mm, "end": v(11.38, -46.38) * mm});
            skLineSegment(sketch, "E3591", {"start": v(11.38, -46.38) * mm, "end": v(11.4, -46.2) * mm});
            skLineSegment(sketch, "E3592", {"start": v(11.4, -46.2) * mm, "end": v(11.37, -46.04) * mm});
            skLineSegment(sketch, "E3593", {"start": v(11.37, -46.04) * mm, "end": v(11.33, -45.88) * mm});
            skLineSegment(sketch, "E3594", {"start": v(11.33, -45.88) * mm, "end": v(11.29, -45.72) * mm});
            skLineSegment(sketch, "E3595", {"start": v(11.29, -45.72) * mm, "end": v(11.24, -45.56) * mm});
            skLineSegment(sketch, "E3596", {"start": v(11.24, -45.56) * mm, "end": v(11.2, -45.4) * mm});
            skLineSegment(sketch, "E3597", {"start": v(11.2, -45.4) * mm, "end": v(11.16, -45.23) * mm});
            skLineSegment(sketch, "E3598", {"start": v(11.16, -45.23) * mm, "end": v(11.11, -45.07) * mm});
            skLineSegment(sketch, "E3599", {"start": v(11.11, -45.07) * mm, "end": v(11.07, -44.91) * mm});
            skLineSegment(sketch, "E3600", {"start": v(11.07, -44.91) * mm, "end": v(11.03, -44.74) * mm});
            skLineSegment(sketch, "E3601", {"start": v(11.03, -44.74) * mm, "end": v(10.99, -44.58) * mm});
            skLineSegment(sketch, "E3602", {"start": v(10.99, -44.58) * mm, "end": v(10.94, -44.42) * mm});
            skLineSegment(sketch, "E3603", {"start": v(10.94, -44.42) * mm, "end": v(10.9, -44.26) * mm});
            skLineSegment(sketch, "E3604", {"start": v(10.9, -44.26) * mm, "end": v(10.86, -44.1) * mm});
            skLineSegment(sketch, "E3605", {"start": v(10.86, -44.1) * mm, "end": v(10.83, -43.98) * mm});
            skLineSegment(sketch, "E3606", {"start": v(10.83, -43.98) * mm, "end": v(10.99, -43.93) * mm});
            skLineSegment(sketch, "E3607", {"start": v(10.99, -43.93) * mm, "end": v(11.15, -43.89) * mm});
            skLineSegment(sketch, "E3608", {"start": v(11.15, -43.89) * mm, "end": v(11.3, -43.84) * mm});
            skLineSegment(sketch, "E3609", {"start": v(11.3, -43.84) * mm, "end": v(11.47, -43.8) * mm});
            skLineSegment(sketch, "E3610", {"start": v(11.47, -43.8) * mm, "end": v(11.63, -43.75) * mm});
            skLineSegment(sketch, "E3611", {"start": v(11.63, -43.75) * mm, "end": v(11.79, -43.7) * mm});
            skLineSegment(sketch, "E3612", {"start": v(11.79, -43.7) * mm, "end": v(11.95, -43.66) * mm});
            skLineSegment(sketch, "E3613", {"start": v(11.95, -43.66) * mm, "end": v(12.1, -43.61) * mm});
            skLineSegment(sketch, "E3614", {"start": v(12.1, -43.61) * mm, "end": v(12.27, -43.57) * mm});
            skLineSegment(sketch, "E3615", {"start": v(12.27, -43.57) * mm, "end": v(12.43, -43.52) * mm});
            skLineSegment(sketch, "E3616", {"start": v(12.43, -43.52) * mm, "end": v(12.59, -43.47) * mm});
            skLineSegment(sketch, "E3617", {"start": v(12.59, -43.47) * mm, "end": v(12.66, -43.45) * mm});
            skLineSegment(sketch, "E3618", {"start": v(12.66, -43.45) * mm, "end": v(12.71, -43.61) * mm});
            skLineSegment(sketch, "E3619", {"start": v(12.71, -43.61) * mm, "end": v(12.76, -43.77) * mm});
            skLineSegment(sketch, "E3620", {"start": v(12.76, -43.77) * mm, "end": v(12.81, -43.93) * mm});
            skLineSegment(sketch, "E3621", {"start": v(12.81, -43.93) * mm, "end": v(12.86, -44.1) * mm});
            skLineSegment(sketch, "E3622", {"start": v(12.86, -44.1) * mm, "end": v(12.91, -44.25) * mm});
            skLineSegment(sketch, "E3623", {"start": v(12.91, -44.25) * mm, "end": v(12.96, -44.42) * mm});
            skLineSegment(sketch, "E3624", {"start": v(12.96, -44.42) * mm, "end": v(13.01, -44.57) * mm});
            skLineSegment(sketch, "E3625", {"start": v(13.01, -44.57) * mm, "end": v(13.06, -44.73) * mm});
            skLineSegment(sketch, "E3626", {"start": v(13.06, -44.73) * mm, "end": v(13.11, -44.9) * mm});
            skLineSegment(sketch, "E3627", {"start": v(13.11, -44.9) * mm, "end": v(13.16, -45.06) * mm});
            skLineSegment(sketch, "E3628", {"start": v(13.16, -45.06) * mm, "end": v(13.2, -45.21) * mm});
            skLineSegment(sketch, "E3629", {"start": v(13.2, -45.21) * mm, "end": v(13.26, -45.38) * mm});
            skLineSegment(sketch, "E3630", {"start": v(13.26, -45.38) * mm, "end": v(13.31, -45.55) * mm});
            skLineSegment(sketch, "E3631", {"start": v(13.31, -45.55) * mm, "end": v(13.4, -45.7) * mm});
            skLineSegment(sketch, "E3632", {"start": v(13.4, -45.7) * mm, "end": v(13.51, -45.83) * mm});
            skLineSegment(sketch, "E3633", {"start": v(13.51, -45.83) * mm, "end": v(13.66, -45.92) * mm});
            skLineSegment(sketch, "E3634", {"start": v(13.66, -45.92) * mm, "end": v(13.83, -45.97) * mm});
            skLineSegment(sketch, "E3635", {"start": v(13.83, -45.97) * mm, "end": v(14, -45.97) * mm});
            skLineSegment(sketch, "E3636", {"start": v(14, -45.97) * mm, "end": v(14.17, -45.93) * mm});
            skLineSegment(sketch, "E3637", {"start": v(14.17, -45.93) * mm, "end": v(14.32, -45.85) * mm});
            skLineSegment(sketch, "E3638", {"start": v(14.32, -45.85) * mm, "end": v(14.45, -45.73) * mm});
            skLineSegment(sketch, "E3639", {"start": v(14.45, -45.73) * mm, "end": v(14.54, -45.58) * mm});
            skLineSegment(sketch, "E3640", {"start": v(14.54, -45.58) * mm, "end": v(14.59, -45.42) * mm});
            skLineSegment(sketch, "E3641", {"start": v(14.59, -45.42) * mm, "end": v(14.6, -45.24) * mm});
            skLineSegment(sketch, "E3642", {"start": v(14.6, -45.24) * mm, "end": v(14.55, -45.08) * mm});
            skLineSegment(sketch, "E3643", {"start": v(14.55, -45.08) * mm, "end": v(14.5, -44.92) * mm});
            skLineSegment(sketch, "E3644", {"start": v(14.5, -44.92) * mm, "end": v(14.45, -44.77) * mm});
            skLineSegment(sketch, "E3645", {"start": v(14.45, -44.77) * mm, "end": v(14.4, -44.6) * mm});
            skLineSegment(sketch, "E3646", {"start": v(14.4, -44.6) * mm, "end": v(14.34, -44.45) * mm});
            skLineSegment(sketch, "E3647", {"start": v(14.34, -44.45) * mm, "end": v(14.28, -44.29) * mm});
            skLineSegment(sketch, "E3648", {"start": v(14.28, -44.29) * mm, "end": v(14.23, -44.13) * mm});
            skLineSegment(sketch, "E3649", {"start": v(14.23, -44.13) * mm, "end": v(14.18, -43.97) * mm});
            skLineSegment(sketch, "E3650", {"start": v(14.18, -43.97) * mm, "end": v(14.12, -43.81) * mm});
            skLineSegment(sketch, "E3651", {"start": v(14.12, -43.81) * mm, "end": v(14.07, -43.65) * mm});
            skLineSegment(sketch, "E3652", {"start": v(14.07, -43.65) * mm, "end": v(14.01, -43.5) * mm});
            skLineSegment(sketch, "E3653", {"start": v(14.01, -43.5) * mm, "end": v(13.96, -43.33) * mm});
            skLineSegment(sketch, "E3654", {"start": v(13.96, -43.33) * mm, "end": v(13.9, -43.18) * mm});
            skLineSegment(sketch, "E3655", {"start": v(13.9, -43.18) * mm, "end": v(13.87, -43.06) * mm});
            skLineSegment(sketch, "E3656", {"start": v(13.87, -43.06) * mm, "end": v(14.02, -43) * mm});
            skLineSegment(sketch, "E3657", {"start": v(14.02, -43) * mm, "end": v(14.18, -42.95) * mm});
            skLineSegment(sketch, "E3658", {"start": v(14.18, -42.95) * mm, "end": v(14.33, -42.9) * mm});
            skLineSegment(sketch, "E3659", {"start": v(14.33, -42.9) * mm, "end": v(14.5, -42.83) * mm});
            skLineSegment(sketch, "E3660", {"start": v(14.5, -42.83) * mm, "end": v(14.65, -42.78) * mm});
            skLineSegment(sketch, "E3661", {"start": v(14.65, -42.78) * mm, "end": v(14.8, -42.72) * mm});
            skLineSegment(sketch, "E3662", {"start": v(14.8, -42.72) * mm, "end": v(14.96, -42.66) * mm});
            skLineSegment(sketch, "E3663", {"start": v(14.96, -42.66) * mm, "end": v(15.12, -42.6) * mm});
            skLineSegment(sketch, "E3664", {"start": v(15.12, -42.6) * mm, "end": v(15.27, -42.55) * mm});
            skLineSegment(sketch, "E3665", {"start": v(15.27, -42.55) * mm, "end": v(15.43, -42.5) * mm});
            skLineSegment(sketch, "E3666", {"start": v(15.43, -42.5) * mm, "end": v(15.59, -42.44) * mm});
            skLineSegment(sketch, "E3667", {"start": v(15.59, -42.44) * mm, "end": v(15.66, -42.4) * mm});
            skLineSegment(sketch, "E3668", {"start": v(15.66, -42.4) * mm, "end": v(15.72, -42.56) * mm});
            skLineSegment(sketch, "E3669", {"start": v(15.72, -42.56) * mm, "end": v(15.78, -42.72) * mm});
            skLineSegment(sketch, "E3670", {"start": v(15.78, -42.72) * mm, "end": v(15.84, -42.88) * mm});
            skLineSegment(sketch, "E3671", {"start": v(15.84, -42.88) * mm, "end": v(15.9, -43.03) * mm});
            skLineSegment(sketch, "E3672", {"start": v(15.9, -43.03) * mm, "end": v(15.96, -43.19) * mm});
            skLineSegment(sketch, "E3673", {"start": v(15.96, -43.19) * mm, "end": v(16.03, -43.35) * mm});
            skLineSegment(sketch, "E3674", {"start": v(16.03, -43.35) * mm, "end": v(16.09, -43.5) * mm});
            skLineSegment(sketch, "E3675", {"start": v(16.09, -43.5) * mm, "end": v(16.15, -43.66) * mm});
            skLineSegment(sketch, "E3676", {"start": v(16.15, -43.66) * mm, "end": v(16.2, -43.82) * mm});
            skLineSegment(sketch, "E3677", {"start": v(16.2, -43.82) * mm, "end": v(16.27, -43.97) * mm});
            skLineSegment(sketch, "E3678", {"start": v(16.27, -43.97) * mm, "end": v(16.33, -44.13) * mm});
            skLineSegment(sketch, "E3679", {"start": v(16.33, -44.13) * mm, "end": v(16.4, -44.29) * mm});
            skLineSegment(sketch, "E3680", {"start": v(16.4, -44.29) * mm, "end": v(16.46, -44.45) * mm});
            skLineSegment(sketch, "E3681", {"start": v(16.46, -44.45) * mm, "end": v(16.55, -44.6) * mm});
            skLineSegment(sketch, "E3682", {"start": v(16.55, -44.6) * mm, "end": v(16.68, -44.72) * mm});
            skLineSegment(sketch, "E3683", {"start": v(16.68, -44.72) * mm, "end": v(16.83, -44.8) * mm});
            skLineSegment(sketch, "E3684", {"start": v(16.83, -44.8) * mm, "end": v(17, -44.84) * mm});
            skLineSegment(sketch, "E3685", {"start": v(17, -44.84) * mm, "end": v(17.17, -44.83) * mm});
            skLineSegment(sketch, "E3686", {"start": v(17.17, -44.83) * mm, "end": v(17.34, -44.78) * mm});
            skLineSegment(sketch, "E3687", {"start": v(17.34, -44.78) * mm, "end": v(17.48, -44.68) * mm});
            skLineSegment(sketch, "E3688", {"start": v(17.48, -44.68) * mm, "end": v(17.6, -44.56) * mm});
            skLineSegment(sketch, "E3689", {"start": v(17.6, -44.56) * mm, "end": v(17.68, -44.4) * mm});
            skLineSegment(sketch, "E3690", {"start": v(17.68, -44.4) * mm, "end": v(17.72, -44.23) * mm});
            skLineSegment(sketch, "E3691", {"start": v(17.72, -44.23) * mm, "end": v(17.7, -44.06) * mm});
            skLineSegment(sketch, "E3692", {"start": v(17.7, -44.06) * mm, "end": v(17.66, -43.9) * mm});
            skLineSegment(sketch, "E3693", {"start": v(17.66, -43.9) * mm, "end": v(17.6, -43.75) * mm});
            skLineSegment(sketch, "E3694", {"start": v(17.6, -43.75) * mm, "end": v(17.53, -43.6) * mm});
            skLineSegment(sketch, "E3695", {"start": v(17.53, -43.6) * mm, "end": v(17.47, -43.44) * mm});
            skLineSegment(sketch, "E3696", {"start": v(17.47, -43.44) * mm, "end": v(17.4, -43.29) * mm});
            skLineSegment(sketch, "E3697", {"start": v(17.4, -43.29) * mm, "end": v(17.34, -43.13) * mm});
            skLineSegment(sketch, "E3698", {"start": v(17.34, -43.13) * mm, "end": v(17.27, -42.98) * mm});
            skLineSegment(sketch, "E3699", {"start": v(17.27, -42.98) * mm, "end": v(17.2, -42.82) * mm});
            skLineSegment(sketch, "E3700", {"start": v(17.2, -42.82) * mm, "end": v(17.14, -42.66) * mm});
            skLineSegment(sketch, "E3701", {"start": v(17.14, -42.66) * mm, "end": v(17.08, -42.51) * mm});
            skLineSegment(sketch, "E3702", {"start": v(17.08, -42.51) * mm, "end": v(17.01, -42.36) * mm});
            skLineSegment(sketch, "E3703", {"start": v(17.01, -42.36) * mm, "end": v(16.95, -42.2) * mm});
            skLineSegment(sketch, "E3704", {"start": v(16.95, -42.2) * mm, "end": v(16.88, -42.05) * mm});
            skLineSegment(sketch, "E3705", {"start": v(16.88, -42.05) * mm, "end": v(16.83, -41.93) * mm});
            skLineSegment(sketch, "E3706", {"start": v(16.83, -41.93) * mm, "end": v(16.99, -41.87) * mm});
            skLineSegment(sketch, "E3707", {"start": v(16.99, -41.87) * mm, "end": v(17.14, -41.8) * mm});
            skLineSegment(sketch, "E3708", {"start": v(17.14, -41.8) * mm, "end": v(17.29, -41.73) * mm});
            skLineSegment(sketch, "E3709", {"start": v(17.29, -41.73) * mm, "end": v(17.44, -41.66) * mm});
            skLineSegment(sketch, "E3710", {"start": v(17.44, -41.66) * mm, "end": v(17.6, -41.6) * mm});
            skLineSegment(sketch, "E3711", {"start": v(17.6, -41.6) * mm, "end": v(17.75, -41.53) * mm});
            skLineSegment(sketch, "E3712", {"start": v(17.75, -41.53) * mm, "end": v(17.9, -41.46) * mm});
            skLineSegment(sketch, "E3713", {"start": v(17.9, -41.46) * mm, "end": v(18.05, -41.4) * mm});
            skLineSegment(sketch, "E3714", {"start": v(18.05, -41.4) * mm, "end": v(18.2, -41.33) * mm});
            skLineSegment(sketch, "E3715", {"start": v(18.2, -41.33) * mm, "end": v(18.35, -41.26) * mm});
            skLineSegment(sketch, "E3716", {"start": v(18.35, -41.26) * mm, "end": v(18.5, -41.2) * mm});
            skLineSegment(sketch, "E3717", {"start": v(18.5, -41.2) * mm, "end": v(18.58, -41.16) * mm});
            skLineSegment(sketch, "E3718", {"start": v(18.58, -41.16) * mm, "end": v(18.65, -41.3) * mm});
            skLineSegment(sketch, "E3719", {"start": v(18.65, -41.3) * mm, "end": v(18.72, -41.46) * mm});
            skLineSegment(sketch, "E3720", {"start": v(18.72, -41.46) * mm, "end": v(18.8, -41.61) * mm});
            skLineSegment(sketch, "E3721", {"start": v(18.8, -41.61) * mm, "end": v(18.86, -41.76) * mm});
            skLineSegment(sketch, "E3722", {"start": v(18.86, -41.76) * mm, "end": v(18.94, -41.91) * mm});
            skLineSegment(sketch, "E3723", {"start": v(18.94, -41.91) * mm, "end": v(19, -42.07) * mm});
            skLineSegment(sketch, "E3724", {"start": v(19, -42.07) * mm, "end": v(19.08, -42.22) * mm});
            skLineSegment(sketch, "E3725", {"start": v(19.08, -42.22) * mm, "end": v(19.15, -42.37) * mm});
            skLineSegment(sketch, "E3726", {"start": v(19.15, -42.37) * mm, "end": v(19.22, -42.52) * mm});
            skLineSegment(sketch, "E3727", {"start": v(19.22, -42.52) * mm, "end": v(19.3, -42.68) * mm});
            skLineSegment(sketch, "E3728", {"start": v(19.3, -42.68) * mm, "end": v(19.36, -42.83) * mm});
            skLineSegment(sketch, "E3729", {"start": v(19.36, -42.83) * mm, "end": v(19.44, -42.98) * mm});
            skLineSegment(sketch, "E3730", {"start": v(19.44, -42.98) * mm, "end": v(19.52, -43.14) * mm});
            skLineSegment(sketch, "E3731", {"start": v(19.52, -43.14) * mm, "end": v(19.62, -43.28) * mm});
            skLineSegment(sketch, "E3732", {"start": v(19.62, -43.28) * mm, "end": v(19.75, -43.4) * mm});
            skLineSegment(sketch, "E3733", {"start": v(19.75, -43.4) * mm, "end": v(19.91, -43.46) * mm});
            skLineSegment(sketch, "E3734", {"start": v(19.91, -43.46) * mm, "end": v(20.08, -43.49) * mm});
            skLineSegment(sketch, "E3735", {"start": v(20.08, -43.49) * mm, "end": v(20.26, -43.47) * mm});
            skLineSegment(sketch, "E3736", {"start": v(20.26, -43.47) * mm, "end": v(20.42, -43.4) * mm});
            skLineSegment(sketch, "E3737", {"start": v(20.42, -43.4) * mm, "end": v(20.56, -43.3) * mm});
            skLineSegment(sketch, "E3738", {"start": v(20.56, -43.3) * mm, "end": v(20.66, -43.16) * mm});
            skLineSegment(sketch, "E3739", {"start": v(20.66, -43.16) * mm, "end": v(20.73, -43) * mm});
            skLineSegment(sketch, "E3740", {"start": v(20.73, -43) * mm, "end": v(20.76, -42.83) * mm});
            skLineSegment(sketch, "E3741", {"start": v(20.76, -42.83) * mm, "end": v(20.74, -42.66) * mm});
            skLineSegment(sketch, "E3742", {"start": v(20.74, -42.66) * mm, "end": v(20.67, -42.5) * mm});
            skLineSegment(sketch, "E3743", {"start": v(20.67, -42.5) * mm, "end": v(20.6, -42.36) * mm});
            skLineSegment(sketch, "E3744", {"start": v(20.6, -42.36) * mm, "end": v(20.53, -42.2) * mm});
            skLineSegment(sketch, "E3745", {"start": v(20.53, -42.2) * mm, "end": v(20.45, -42.06) * mm});
            skLineSegment(sketch, "E3746", {"start": v(20.45, -42.06) * mm, "end": v(20.38, -41.91) * mm});
            skLineSegment(sketch, "E3747", {"start": v(20.38, -41.91) * mm, "end": v(20.3, -41.76) * mm});
            skLineSegment(sketch, "E3748", {"start": v(20.3, -41.76) * mm, "end": v(20.22, -41.61) * mm});
            skLineSegment(sketch, "E3749", {"start": v(20.22, -41.61) * mm, "end": v(20.15, -41.46) * mm});
            skLineSegment(sketch, "E3750", {"start": v(20.15, -41.46) * mm, "end": v(20.07, -41.3) * mm});
            skLineSegment(sketch, "E3751", {"start": v(20.07, -41.3) * mm, "end": v(20, -41.16) * mm});
            skLineSegment(sketch, "E3752", {"start": v(20, -41.16) * mm, "end": v(19.92, -41.01) * mm});
            skLineSegment(sketch, "E3753", {"start": v(19.92, -41.01) * mm, "end": v(19.85, -40.86) * mm});
            skLineSegment(sketch, "E3754", {"start": v(19.85, -40.86) * mm, "end": v(19.77, -40.71) * mm});
            skLineSegment(sketch, "E3755", {"start": v(19.77, -40.71) * mm, "end": v(19.72, -40.6) * mm});
            skLineSegment(sketch, "E3756", {"start": v(19.72, -40.6) * mm, "end": v(19.86, -40.52) * mm});
            skLineSegment(sketch, "E3757", {"start": v(19.86, -40.52) * mm, "end": v(20, -40.45) * mm});
            skLineSegment(sketch, "E3758", {"start": v(20, -40.45) * mm, "end": v(20.16, -40.37) * mm});
            skLineSegment(sketch, "E3759", {"start": v(20.16, -40.37) * mm, "end": v(20.3, -40.3) * mm});
            skLineSegment(sketch, "E3760", {"start": v(20.3, -40.3) * mm, "end": v(20.45, -40.21) * mm});
            skLineSegment(sketch, "E3761", {"start": v(20.45, -40.21) * mm, "end": v(20.6, -40.13) * mm});
            skLineSegment(sketch, "E3762", {"start": v(20.6, -40.13) * mm, "end": v(20.74, -40.06) * mm});
            skLineSegment(sketch, "E3763", {"start": v(20.74, -40.06) * mm, "end": v(20.9, -39.98) * mm});
            skLineSegment(sketch, "E3764", {"start": v(20.9, -39.98) * mm, "end": v(21.04, -39.9) * mm});
            skLineSegment(sketch, "E3765", {"start": v(21.04, -39.9) * mm, "end": v(21.18, -39.82) * mm});
            skLineSegment(sketch, "E3766", {"start": v(21.18, -39.82) * mm, "end": v(21.33, -39.74) * mm});
            skLineSegment(sketch, "E3767", {"start": v(21.33, -39.74) * mm, "end": v(21.4, -39.7) * mm});
            skLineSegment(sketch, "E3768", {"start": v(21.4, -39.7) * mm, "end": v(21.48, -39.85) * mm});
            skLineSegment(sketch, "E3769", {"start": v(21.48, -39.85) * mm, "end": v(21.57, -40) * mm});
            skLineSegment(sketch, "E3770", {"start": v(21.57, -40) * mm, "end": v(21.65, -40.15) * mm});
            skLineSegment(sketch, "E3771", {"start": v(21.65, -40.15) * mm, "end": v(21.73, -40.3) * mm});
            skLineSegment(sketch, "E3772", {"start": v(21.73, -40.3) * mm, "end": v(21.81, -40.44) * mm});
            skLineSegment(sketch, "E3773", {"start": v(21.81, -40.44) * mm, "end": v(21.9, -40.59) * mm});
            skLineSegment(sketch, "E3774", {"start": v(21.9, -40.59) * mm, "end": v(21.98, -40.73) * mm});
            skLineSegment(sketch, "E3775", {"start": v(21.98, -40.73) * mm, "end": v(22.06, -40.88) * mm});
            skLineSegment(sketch, "E3776", {"start": v(22.06, -40.88) * mm, "end": v(22.14, -41.03) * mm});
            skLineSegment(sketch, "E3777", {"start": v(22.14, -41.03) * mm, "end": v(22.22, -41.17) * mm});
            skLineSegment(sketch, "E3778", {"start": v(22.22, -41.17) * mm, "end": v(22.3, -41.32) * mm});
            skLineSegment(sketch, "E3779", {"start": v(22.3, -41.32) * mm, "end": v(22.39, -41.46) * mm});
            skLineSegment(sketch, "E3780", {"start": v(22.39, -41.46) * mm, "end": v(22.47, -41.62) * mm});
            skLineSegment(sketch, "E3781", {"start": v(22.47, -41.62) * mm, "end": v(22.59, -41.75) * mm});
            skLineSegment(sketch, "E3782", {"start": v(22.59, -41.75) * mm, "end": v(22.73, -41.85) * mm});
            skLineSegment(sketch, "E3783", {"start": v(22.73, -41.85) * mm, "end": v(22.9, -41.91) * mm});
            skLineSegment(sketch, "E3784", {"start": v(22.9, -41.91) * mm, "end": v(23.07, -41.92) * mm});
            skLineSegment(sketch, "E3785", {"start": v(23.07, -41.92) * mm, "end": v(23.24, -41.9) * mm});
            skLineSegment(sketch, "E3786", {"start": v(23.24, -41.9) * mm, "end": v(23.4, -41.82) * mm});
            skLineSegment(sketch, "E3787", {"start": v(23.4, -41.82) * mm, "end": v(23.53, -41.7) * mm});
            skLineSegment(sketch, "E3788", {"start": v(23.53, -41.7) * mm, "end": v(23.62, -41.56) * mm});
            skLineSegment(sketch, "E3789", {"start": v(23.62, -41.56) * mm, "end": v(23.68, -41.4) * mm});
            skLineSegment(sketch, "E3790", {"start": v(23.68, -41.4) * mm, "end": v(23.7, -41.23) * mm});
            skLineSegment(sketch, "E3791", {"start": v(23.7, -41.23) * mm, "end": v(23.66, -41.06) * mm});
            skLineSegment(sketch, "E3792", {"start": v(23.66, -41.06) * mm, "end": v(23.59, -40.9) * mm});
            skLineSegment(sketch, "E3793", {"start": v(23.59, -40.9) * mm, "end": v(23.5, -40.76) * mm});
            skLineSegment(sketch, "E3794", {"start": v(23.5, -40.76) * mm, "end": v(23.42, -40.62) * mm});
            skLineSegment(sketch, "E3795", {"start": v(23.42, -40.62) * mm, "end": v(23.33, -40.48) * mm});
            skLineSegment(sketch, "E3796", {"start": v(23.33, -40.48) * mm, "end": v(23.25, -40.33) * mm});
            skLineSegment(sketch, "E3797", {"start": v(23.25, -40.33) * mm, "end": v(23.16, -40.19) * mm});
            skLineSegment(sketch, "E3798", {"start": v(23.16, -40.19) * mm, "end": v(23.08, -40.04) * mm});
            skLineSegment(sketch, "E3799", {"start": v(23.08, -40.04) * mm, "end": v(23, -39.9) * mm});
            skLineSegment(sketch, "E3800", {"start": v(23, -39.9) * mm, "end": v(22.9, -39.75) * mm});
            skLineSegment(sketch, "E3801", {"start": v(22.9, -39.75) * mm, "end": v(22.82, -39.61) * mm});
            skLineSegment(sketch, "E3802", {"start": v(22.82, -39.61) * mm, "end": v(22.73, -39.47) * mm});
            skLineSegment(sketch, "E3803", {"start": v(22.73, -39.47) * mm, "end": v(22.65, -39.32) * mm});
            skLineSegment(sketch, "E3804", {"start": v(22.65, -39.32) * mm, "end": v(22.56, -39.18) * mm});
            skLineSegment(sketch, "E3805", {"start": v(22.56, -39.18) * mm, "end": v(22.5, -39.07) * mm});
            skLineSegment(sketch, "E3806", {"start": v(22.5, -39.07) * mm, "end": v(22.64, -38.99) * mm});
            skLineSegment(sketch, "E3807", {"start": v(22.64, -38.99) * mm, "end": v(22.78, -38.9) * mm});
            skLineSegment(sketch, "E3808", {"start": v(22.78, -38.9) * mm, "end": v(22.92, -38.8) * mm});
            skLineSegment(sketch, "E3809", {"start": v(22.92, -38.8) * mm, "end": v(23.06, -38.72) * mm});
            skLineSegment(sketch, "E3810", {"start": v(23.06, -38.72) * mm, "end": v(23.2, -38.63) * mm});
            skLineSegment(sketch, "E3811", {"start": v(23.2, -38.63) * mm, "end": v(23.34, -38.54) * mm});
            skLineSegment(sketch, "E3812", {"start": v(23.34, -38.54) * mm, "end": v(23.49, -38.46) * mm});
            skLineSegment(sketch, "E3813", {"start": v(23.49, -38.46) * mm, "end": v(23.63, -38.37) * mm});
            skLineSegment(sketch, "E3814", {"start": v(23.63, -38.37) * mm, "end": v(23.77, -38.28) * mm});
            skLineSegment(sketch, "E3815", {"start": v(23.77, -38.28) * mm, "end": v(23.9, -38.2) * mm});
            skLineSegment(sketch, "E3816", {"start": v(23.9, -38.2) * mm, "end": v(24.05, -38.1) * mm});
            skLineSegment(sketch, "E3817", {"start": v(24.05, -38.1) * mm, "end": v(24.12, -38.06) * mm});
            skLineSegment(sketch, "E3818", {"start": v(24.12, -38.06) * mm, "end": v(24.21, -38.2) * mm});
            skLineSegment(sketch, "E3819", {"start": v(24.21, -38.2) * mm, "end": v(24.3, -38.34) * mm});
            skLineSegment(sketch, "E3820", {"start": v(24.3, -38.34) * mm, "end": v(24.4, -38.48) * mm});
            skLineSegment(sketch, "E3821", {"start": v(24.4, -38.48) * mm, "end": v(24.49, -38.62) * mm});
            skLineSegment(sketch, "E3822", {"start": v(24.49, -38.62) * mm, "end": v(24.58, -38.76) * mm});
            skLineSegment(sketch, "E3823", {"start": v(24.58, -38.76) * mm, "end": v(24.67, -38.9) * mm});
            skLineSegment(sketch, "E3824", {"start": v(24.67, -38.9) * mm, "end": v(24.76, -39.04) * mm});
            skLineSegment(sketch, "E3825", {"start": v(24.76, -39.04) * mm, "end": v(24.85, -39.18) * mm});
            skLineSegment(sketch, "E3826", {"start": v(24.85, -39.18) * mm, "end": v(24.95, -39.33) * mm});
            skLineSegment(sketch, "E3827", {"start": v(24.95, -39.33) * mm, "end": v(25.04, -39.46) * mm});
            skLineSegment(sketch, "E3828", {"start": v(25.04, -39.46) * mm, "end": v(25.13, -39.6) * mm});
            skLineSegment(sketch, "E3829", {"start": v(25.13, -39.6) * mm, "end": v(25.22, -39.75) * mm});
            skLineSegment(sketch, "E3830", {"start": v(25.22, -39.75) * mm, "end": v(25.32, -39.9) * mm});
            skLineSegment(sketch, "E3831", {"start": v(25.32, -39.9) * mm, "end": v(25.44, -40.02) * mm});
            skLineSegment(sketch, "E3832", {"start": v(25.44, -40.02) * mm, "end": v(25.6, -40.1) * mm});
            skLineSegment(sketch, "E3833", {"start": v(25.6, -40.1) * mm, "end": v(25.76, -40.16) * mm});
            skLineSegment(sketch, "E3834", {"start": v(25.76, -40.16) * mm, "end": v(25.93, -40.16) * mm});
            skLineSegment(sketch, "E3835", {"start": v(25.93, -40.16) * mm, "end": v(26.1, -40.12) * mm});
            skLineSegment(sketch, "E3836", {"start": v(26.1, -40.12) * mm, "end": v(26.25, -40.03) * mm});
            skLineSegment(sketch, "E3837", {"start": v(26.25, -40.03) * mm, "end": v(26.38, -39.9) * mm});
            skLineSegment(sketch, "E3838", {"start": v(26.38, -39.9) * mm, "end": v(26.46, -39.76) * mm});
            skLineSegment(sketch, "E3839", {"start": v(26.46, -39.76) * mm, "end": v(26.5, -39.6) * mm});
            skLineSegment(sketch, "E3840", {"start": v(26.5, -39.6) * mm, "end": v(26.5, -39.42) * mm});
            skLineSegment(sketch, "E3841", {"start": v(26.5, -39.42) * mm, "end": v(26.47, -39.25) * mm});
            skLineSegment(sketch, "E3842", {"start": v(26.47, -39.25) * mm, "end": v(26.38, -39.1) * mm});
            skLineSegment(sketch, "E3843", {"start": v(26.38, -39.1) * mm, "end": v(26.29, -38.97) * mm});
            skLineSegment(sketch, "E3844", {"start": v(26.29, -38.97) * mm, "end": v(26.2, -38.83) * mm});
            skLineSegment(sketch, "E3845", {"start": v(26.2, -38.83) * mm, "end": v(26.1, -38.7) * mm});
            skLineSegment(sketch, "E3846", {"start": v(26.1, -38.7) * mm, "end": v(26, -38.56) * mm});
            skLineSegment(sketch, "E3847", {"start": v(26, -38.56) * mm, "end": v(25.9, -38.42) * mm});
            skLineSegment(sketch, "E3848", {"start": v(25.9, -38.42) * mm, "end": v(25.81, -38.28) * mm});
            skLineSegment(sketch, "E3849", {"start": v(25.81, -38.28) * mm, "end": v(25.72, -38.14) * mm});
            skLineSegment(sketch, "E3850", {"start": v(25.72, -38.14) * mm, "end": v(25.62, -38) * mm});
            skLineSegment(sketch, "E3851", {"start": v(25.62, -38) * mm, "end": v(25.52, -37.87) * mm});
            skLineSegment(sketch, "E3852", {"start": v(25.52, -37.87) * mm, "end": v(25.43, -37.73) * mm});
            skLineSegment(sketch, "E3853", {"start": v(25.43, -37.73) * mm, "end": v(25.33, -37.6) * mm});
            skLineSegment(sketch, "E3854", {"start": v(25.33, -37.6) * mm, "end": v(25.24, -37.45) * mm});
            skLineSegment(sketch, "E3855", {"start": v(25.24, -37.45) * mm, "end": v(25.17, -37.35) * mm});
            skLineSegment(sketch, "E3856", {"start": v(25.17, -37.35) * mm, "end": v(25.3, -37.26) * mm});
            skLineSegment(sketch, "E3857", {"start": v(25.3, -37.26) * mm, "end": v(25.44, -37.16) * mm});
            skLineSegment(sketch, "E3858", {"start": v(25.44, -37.16) * mm, "end": v(25.57, -37.06) * mm});
            skLineSegment(sketch, "E3859", {"start": v(25.57, -37.06) * mm, "end": v(25.7, -36.96) * mm});
            skLineSegment(sketch, "E3860", {"start": v(25.7, -36.96) * mm, "end": v(25.84, -36.86) * mm});
            skLineSegment(sketch, "E3861", {"start": v(25.84, -36.86) * mm, "end": v(25.97, -36.77) * mm});
            skLineSegment(sketch, "E3862", {"start": v(25.97, -36.77) * mm, "end": v(26.1, -36.67) * mm});
            skLineSegment(sketch, "E3863", {"start": v(26.1, -36.67) * mm, "end": v(26.24, -36.57) * mm});
            skLineSegment(sketch, "E3864", {"start": v(26.24, -36.57) * mm, "end": v(26.38, -36.47) * mm});
            skLineSegment(sketch, "E3865", {"start": v(26.38, -36.47) * mm, "end": v(26.51, -36.38) * mm});
            skLineSegment(sketch, "E3866", {"start": v(26.51, -36.38) * mm, "end": v(26.65, -36.28) * mm});
            skLineSegment(sketch, "E3867", {"start": v(26.65, -36.28) * mm, "end": v(26.71, -36.23) * mm});
            skLineSegment(sketch, "E3868", {"start": v(26.71, -36.23) * mm, "end": v(26.81, -36.36) * mm});
            skLineSegment(sketch, "E3869", {"start": v(26.81, -36.36) * mm, "end": v(26.91, -36.5) * mm});
            skLineSegment(sketch, "E3870", {"start": v(26.91, -36.5) * mm, "end": v(27.02, -36.63) * mm});
            skLineSegment(sketch, "E3871", {"start": v(27.02, -36.63) * mm, "end": v(27.12, -36.76) * mm});
            skLineSegment(sketch, "E3872", {"start": v(27.12, -36.76) * mm, "end": v(27.22, -36.9) * mm});
            skLineSegment(sketch, "E3873", {"start": v(27.22, -36.9) * mm, "end": v(27.32, -37.03) * mm});
            skLineSegment(sketch, "E3874", {"start": v(27.32, -37.03) * mm, "end": v(27.42, -37.17) * mm});
            skLineSegment(sketch, "E3875", {"start": v(27.42, -37.17) * mm, "end": v(27.52, -37.3) * mm});
            skLineSegment(sketch, "E3876", {"start": v(27.52, -37.3) * mm, "end": v(27.63, -37.43) * mm});
            skLineSegment(sketch, "E3877", {"start": v(27.63, -37.43) * mm, "end": v(27.73, -37.57) * mm});
            skLineSegment(sketch, "E3878", {"start": v(27.73, -37.57) * mm, "end": v(27.83, -37.7) * mm});
            skLineSegment(sketch, "E3879", {"start": v(27.83, -37.7) * mm, "end": v(27.93, -37.84) * mm});
            skLineSegment(sketch, "E3880", {"start": v(27.93, -37.84) * mm, "end": v(28.04, -37.98) * mm});
            skLineSegment(sketch, "E3881", {"start": v(28.04, -37.98) * mm, "end": v(28.17, -38.1) * mm});
            skLineSegment(sketch, "E3882", {"start": v(28.17, -38.1) * mm, "end": v(28.33, -38.17) * mm});
            skLineSegment(sketch, "E3883", {"start": v(28.33, -38.17) * mm, "end": v(28.5, -38.2) * mm});
            skLineSegment(sketch, "E3884", {"start": v(28.5, -38.2) * mm, "end": v(28.67, -38.2) * mm});
            skLineSegment(sketch, "E3885", {"start": v(28.67, -38.2) * mm, "end": v(28.83, -38.14) * mm});
            skLineSegment(sketch, "E3886", {"start": v(28.83, -38.14) * mm, "end": v(28.98, -38.05) * mm});
            skLineSegment(sketch, "E3887", {"start": v(28.98, -38.05) * mm, "end": v(29.1, -37.92) * mm});
            skLineSegment(sketch, "E3888", {"start": v(29.1, -37.92) * mm, "end": v(29.17, -37.76) * mm});
            skLineSegment(sketch, "E3889", {"start": v(29.17, -37.76) * mm, "end": v(29.2, -37.6) * mm});
            skLineSegment(sketch, "E3890", {"start": v(29.2, -37.6) * mm, "end": v(29.2, -37.42) * mm});
            skLineSegment(sketch, "E3891", {"start": v(29.2, -37.42) * mm, "end": v(29.14, -37.25) * mm});
            skLineSegment(sketch, "E3892", {"start": v(29.14, -37.25) * mm, "end": v(29.04, -37.12) * mm});
            skLineSegment(sketch, "E3893", {"start": v(29.04, -37.12) * mm, "end": v(28.94, -36.98) * mm});
            skLineSegment(sketch, "E3894", {"start": v(28.94, -36.98) * mm, "end": v(28.84, -36.85) * mm});
            skLineSegment(sketch, "E3895", {"start": v(28.84, -36.85) * mm, "end": v(28.73, -36.72) * mm});
            skLineSegment(sketch, "E3896", {"start": v(28.73, -36.72) * mm, "end": v(28.63, -36.6) * mm});
            skLineSegment(sketch, "E3897", {"start": v(28.63, -36.6) * mm, "end": v(28.52, -36.46) * mm});
            skLineSegment(sketch, "E3898", {"start": v(28.52, -36.46) * mm, "end": v(28.42, -36.33) * mm});
            skLineSegment(sketch, "E3899", {"start": v(28.42, -36.33) * mm, "end": v(28.31, -36.2) * mm});
            skLineSegment(sketch, "E3900", {"start": v(28.31, -36.2) * mm, "end": v(28.2, -36.07) * mm});
            skLineSegment(sketch, "E3901", {"start": v(28.2, -36.07) * mm, "end": v(28.1, -35.94) * mm});
            skLineSegment(sketch, "E3902", {"start": v(28.1, -35.94) * mm, "end": v(28, -35.8) * mm});
            skLineSegment(sketch, "E3903", {"start": v(28, -35.8) * mm, "end": v(27.89, -35.68) * mm});
            skLineSegment(sketch, "E3904", {"start": v(27.89, -35.68) * mm, "end": v(27.79, -35.55) * mm});
            skLineSegment(sketch, "E3905", {"start": v(27.79, -35.55) * mm, "end": v(27.7, -35.45) * mm});
            skLineSegment(sketch, "E3906", {"start": v(27.7, -35.45) * mm, "end": v(27.84, -35.35) * mm});
            skLineSegment(sketch, "E3907", {"start": v(27.84, -35.35) * mm, "end": v(27.96, -35.24) * mm});
            skLineSegment(sketch, "E3908", {"start": v(27.96, -35.24) * mm, "end": v(28.1, -35.13) * mm});
            skLineSegment(sketch, "E3909", {"start": v(28.1, -35.13) * mm, "end": v(28.22, -35.02) * mm});
            skLineSegment(sketch, "E3910", {"start": v(28.22, -35.02) * mm, "end": v(28.35, -34.92) * mm});
            skLineSegment(sketch, "E3911", {"start": v(28.35, -34.92) * mm, "end": v(28.47, -34.81) * mm});
            skLineSegment(sketch, "E3912", {"start": v(28.47, -34.81) * mm, "end": v(28.6, -34.7) * mm});
            skLineSegment(sketch, "E3913", {"start": v(28.6, -34.7) * mm, "end": v(28.73, -34.6) * mm});
            skLineSegment(sketch, "E3914", {"start": v(28.73, -34.6) * mm, "end": v(28.86, -34.49) * mm});
            skLineSegment(sketch, "E3915", {"start": v(28.86, -34.49) * mm, "end": v(28.98, -34.38) * mm});
            skLineSegment(sketch, "E3916", {"start": v(28.98, -34.38) * mm, "end": v(29.11, -34.28) * mm});
            skLineSegment(sketch, "E3917", {"start": v(29.11, -34.28) * mm, "end": v(29.17, -34.22) * mm});
            skLineSegment(sketch, "E3918", {"start": v(29.17, -34.22) * mm, "end": v(29.28, -34.35) * mm});
            skLineSegment(sketch, "E3919", {"start": v(29.28, -34.35) * mm, "end": v(29.4, -34.47) * mm});
            skLineSegment(sketch, "E3920", {"start": v(29.4, -34.47) * mm, "end": v(29.5, -34.6) * mm});
            skLineSegment(sketch, "E3921", {"start": v(29.5, -34.6) * mm, "end": v(29.62, -34.73) * mm});
            skLineSegment(sketch, "E3922", {"start": v(29.62, -34.73) * mm, "end": v(29.72, -34.85) * mm});
            skLineSegment(sketch, "E3923", {"start": v(29.72, -34.85) * mm, "end": v(29.84, -34.98) * mm});
            skLineSegment(sketch, "E3924", {"start": v(29.84, -34.98) * mm, "end": v(29.95, -35.1) * mm});
            skLineSegment(sketch, "E3925", {"start": v(29.95, -35.1) * mm, "end": v(30.06, -35.23) * mm});
            skLineSegment(sketch, "E3926", {"start": v(30.06, -35.23) * mm, "end": v(30.17, -35.36) * mm});
            skLineSegment(sketch, "E3927", {"start": v(30.17, -35.36) * mm, "end": v(30.28, -35.49) * mm});
            skLineSegment(sketch, "E3928", {"start": v(30.28, -35.49) * mm, "end": v(30.39, -35.61) * mm});
            skLineSegment(sketch, "E3929", {"start": v(30.39, -35.61) * mm, "end": v(30.5, -35.74) * mm});
            skLineSegment(sketch, "E3930", {"start": v(30.5, -35.74) * mm, "end": v(30.62, -35.87) * mm});
            skLineSegment(sketch, "E3931", {"start": v(30.62, -35.87) * mm, "end": v(30.76, -35.98) * mm});
            skLineSegment(sketch, "E3932", {"start": v(30.76, -35.98) * mm, "end": v(30.92, -36.05) * mm});
            skLineSegment(sketch, "E3933", {"start": v(30.92, -36.05) * mm, "end": v(31.09, -36.07) * mm});
            skLineSegment(sketch, "E3934", {"start": v(31.09, -36.07) * mm, "end": v(31.26, -36.05) * mm});
            skLineSegment(sketch, "E3935", {"start": v(31.26, -36.05) * mm, "end": v(31.42, -35.98) * mm});
            skLineSegment(sketch, "E3936", {"start": v(31.42, -35.98) * mm, "end": v(31.56, -35.88) * mm});
            skLineSegment(sketch, "E3937", {"start": v(31.56, -35.88) * mm, "end": v(31.66, -35.74) * mm});
            skLineSegment(sketch, "E3938", {"start": v(31.66, -35.74) * mm, "end": v(31.73, -35.58) * mm});
            skLineSegment(sketch, "E3939", {"start": v(31.73, -35.58) * mm, "end": v(31.75, -35.4) * mm});
            skLineSegment(sketch, "E3940", {"start": v(31.75, -35.4) * mm, "end": v(31.73, -35.23) * mm});
            skLineSegment(sketch, "E3941", {"start": v(31.73, -35.23) * mm, "end": v(31.66, -35.07) * mm});
            skLineSegment(sketch, "E3942", {"start": v(31.66, -35.07) * mm, "end": v(31.56, -34.94) * mm});
            skLineSegment(sketch, "E3943", {"start": v(31.56, -34.94) * mm, "end": v(31.45, -34.82) * mm});
            skLineSegment(sketch, "E3944", {"start": v(31.45, -34.82) * mm, "end": v(31.34, -34.7) * mm});
            skLineSegment(sketch, "E3945", {"start": v(31.34, -34.7) * mm, "end": v(31.22, -34.58) * mm});
            skLineSegment(sketch, "E3946", {"start": v(31.22, -34.58) * mm, "end": v(31.1, -34.45) * mm});
            skLineSegment(sketch, "E3947", {"start": v(31.1, -34.45) * mm, "end": v(31, -34.33) * mm});
            skLineSegment(sketch, "E3948", {"start": v(31, -34.33) * mm, "end": v(30.88, -34.2) * mm});
            skLineSegment(sketch, "E3949", {"start": v(30.88, -34.2) * mm, "end": v(30.77, -34.08) * mm});
            skLineSegment(sketch, "E3950", {"start": v(30.77, -34.08) * mm, "end": v(30.65, -33.96) * mm});
            skLineSegment(sketch, "E3951", {"start": v(30.65, -33.96) * mm, "end": v(30.54, -33.84) * mm});
            skLineSegment(sketch, "E3952", {"start": v(30.54, -33.84) * mm, "end": v(30.42, -33.71) * mm});
            skLineSegment(sketch, "E3953", {"start": v(30.42, -33.71) * mm, "end": v(30.3, -33.59) * mm});
            skLineSegment(sketch, "E3954", {"start": v(30.3, -33.59) * mm, "end": v(30.2, -33.47) * mm});
            skLineSegment(sketch, "E3955", {"start": v(30.2, -33.47) * mm, "end": v(30.11, -33.38) * mm});
            skLineSegment(sketch, "E3956", {"start": v(30.11, -33.38) * mm, "end": v(30.23, -33.26) * mm});
            skLineSegment(sketch, "E3957", {"start": v(30.23, -33.26) * mm, "end": v(30.35, -33.15) * mm});
            skLineSegment(sketch, "E3958", {"start": v(30.35, -33.15) * mm, "end": v(30.47, -33.03) * mm});
            skLineSegment(sketch, "E3959", {"start": v(30.47, -33.03) * mm, "end": v(30.6, -32.92) * mm});
            skLineSegment(sketch, "E3960", {"start": v(30.6, -32.92) * mm, "end": v(30.71, -32.8) * mm});
            skLineSegment(sketch, "E3961", {"start": v(30.71, -32.8) * mm, "end": v(30.83, -32.68) * mm});
            skLineSegment(sketch, "E3962", {"start": v(30.83, -32.68) * mm, "end": v(30.95, -32.57) * mm});
            skLineSegment(sketch, "E3963", {"start": v(30.95, -32.57) * mm, "end": v(31.07, -32.45) * mm});
            skLineSegment(sketch, "E3964", {"start": v(31.07, -32.45) * mm, "end": v(31.2, -32.34) * mm});
            skLineSegment(sketch, "E3965", {"start": v(31.2, -32.34) * mm, "end": v(31.3, -32.22) * mm});
            skLineSegment(sketch, "E3966", {"start": v(31.3, -32.22) * mm, "end": v(31.43, -32.1) * mm});
            skLineSegment(sketch, "E3967", {"start": v(31.43, -32.1) * mm, "end": v(31.49, -32.05) * mm});
            skLineSegment(sketch, "E3968", {"start": v(31.49, -32.05) * mm, "end": v(31.6, -32.17) * mm});
            skLineSegment(sketch, "E3969", {"start": v(31.6, -32.17) * mm, "end": v(31.72, -32.28) * mm});
            skLineSegment(sketch, "E3970", {"start": v(31.72, -32.28) * mm, "end": v(31.85, -32.4) * mm});
            skLineSegment(sketch, "E3971", {"start": v(31.85, -32.4) * mm, "end": v(31.96, -32.52) * mm});
            skLineSegment(sketch, "E3972", {"start": v(31.96, -32.52) * mm, "end": v(32.08, -32.64) * mm});
            skLineSegment(sketch, "E3973", {"start": v(32.08, -32.64) * mm, "end": v(32.2, -32.76) * mm});
            skLineSegment(sketch, "E3974", {"start": v(32.2, -32.76) * mm, "end": v(32.32, -32.88) * mm});
            skLineSegment(sketch, "E3975", {"start": v(32.32, -32.88) * mm, "end": v(32.44, -33) * mm});
            skLineSegment(sketch, "E3976", {"start": v(32.44, -33) * mm, "end": v(32.56, -33.12) * mm});
            skLineSegment(sketch, "E3977", {"start": v(32.56, -33.12) * mm, "end": v(32.68, -33.23) * mm});
            skLineSegment(sketch, "E3978", {"start": v(32.68, -33.23) * mm, "end": v(32.8, -33.35) * mm});
            skLineSegment(sketch, "E3979", {"start": v(32.8, -33.35) * mm, "end": v(32.92, -33.47) * mm});
            skLineSegment(sketch, "E3980", {"start": v(32.92, -33.47) * mm, "end": v(33.05, -33.6) * mm});
            skLineSegment(sketch, "E3981", {"start": v(33.05, -33.6) * mm, "end": v(33.19, -33.7) * mm});
            skLineSegment(sketch, "E3982", {"start": v(33.19, -33.7) * mm, "end": v(33.35, -33.75) * mm});
            skLineSegment(sketch, "E3983", {"start": v(33.35, -33.75) * mm, "end": v(33.53, -33.76) * mm});
            skLineSegment(sketch, "E3984", {"start": v(33.53, -33.76) * mm, "end": v(33.7, -33.72) * mm});
            skLineSegment(sketch, "E3985", {"start": v(33.7, -33.72) * mm, "end": v(33.85, -33.65) * mm});
            skLineSegment(sketch, "E3986", {"start": v(33.85, -33.65) * mm, "end": v(33.98, -33.53) * mm});
            skLineSegment(sketch, "E3987", {"start": v(33.98, -33.53) * mm, "end": v(34.08, -33.39) * mm});
            skLineSegment(sketch, "E3988", {"start": v(34.08, -33.39) * mm, "end": v(34.13, -33.22) * mm});
            skLineSegment(sketch, "E3989", {"start": v(34.13, -33.22) * mm, "end": v(34.14, -33.05) * mm});
            skLineSegment(sketch, "E3990", {"start": v(34.14, -33.05) * mm, "end": v(34.1, -32.88) * mm});
            skLineSegment(sketch, "E3991", {"start": v(34.1, -32.88) * mm, "end": v(34.03, -32.72) * mm});
            skLineSegment(sketch, "E3992", {"start": v(34.03, -32.72) * mm, "end": v(33.92, -32.6) * mm});
            skLineSegment(sketch, "E3993", {"start": v(33.92, -32.6) * mm, "end": v(33.8, -32.49) * mm});
            skLineSegment(sketch, "E3994", {"start": v(33.8, -32.49) * mm, "end": v(33.68, -32.37) * mm});
            skLineSegment(sketch, "E3995", {"start": v(33.68, -32.37) * mm, "end": v(33.56, -32.26) * mm});
            skLineSegment(sketch, "E3996", {"start": v(33.56, -32.26) * mm, "end": v(33.44, -32.14) * mm});
            skLineSegment(sketch, "E3997", {"start": v(33.44, -32.14) * mm, "end": v(33.31, -32.03) * mm});
            skLineSegment(sketch, "E3998", {"start": v(33.31, -32.03) * mm, "end": v(33.19, -31.91) * mm});
            skLineSegment(sketch, "E3999", {"start": v(33.19, -31.91) * mm, "end": v(33.07, -31.8) * mm});
            skLineSegment(sketch, "E4000", {"start": v(33.07, -31.8) * mm, "end": v(32.94, -31.68) * mm});
            skLineSegment(sketch, "E4001", {"start": v(32.94, -31.68) * mm, "end": v(32.82, -31.57) * mm});
            skLineSegment(sketch, "E4002", {"start": v(32.82, -31.57) * mm, "end": v(32.7, -31.45) * mm});
            skLineSegment(sketch, "E4003", {"start": v(32.7, -31.45) * mm, "end": v(32.58, -31.34) * mm});
            skLineSegment(sketch, "E4004", {"start": v(32.58, -31.34) * mm, "end": v(32.45, -31.22) * mm});
            skLineSegment(sketch, "E4005", {"start": v(32.45, -31.22) * mm, "end": v(32.37, -31.14) * mm});
            skLineSegment(sketch, "E4006", {"start": v(32.37, -31.14) * mm, "end": v(32.48, -31.02) * mm});
            skLineSegment(sketch, "E4007", {"start": v(32.48, -31.02) * mm, "end": v(32.59, -30.9) * mm});
            skLineSegment(sketch, "E4008", {"start": v(32.59, -30.9) * mm, "end": v(32.7, -30.77) * mm});
            skLineSegment(sketch, "E4009", {"start": v(32.7, -30.77) * mm, "end": v(32.81, -30.65) * mm});
            skLineSegment(sketch, "E4010", {"start": v(32.81, -30.65) * mm, "end": v(32.92, -30.52) * mm});
            skLineSegment(sketch, "E4011", {"start": v(32.92, -30.52) * mm, "end": v(33.03, -30.4) * mm});
            skLineSegment(sketch, "E4012", {"start": v(33.03, -30.4) * mm, "end": v(33.15, -30.28) * mm});
            skLineSegment(sketch, "E4013", {"start": v(33.15, -30.28) * mm, "end": v(33.26, -30.15) * mm});
            skLineSegment(sketch, "E4014", {"start": v(33.26, -30.15) * mm, "end": v(33.37, -30.03) * mm});
            skLineSegment(sketch, "E4015", {"start": v(33.37, -30.03) * mm, "end": v(33.48, -29.9) * mm});
            skLineSegment(sketch, "E4016", {"start": v(33.48, -29.9) * mm, "end": v(33.6, -29.78) * mm});
            skLineSegment(sketch, "E4017", {"start": v(33.6, -29.78) * mm, "end": v(33.65, -29.72) * mm});
            skLineSegment(sketch, "E4018", {"start": v(33.65, -29.72) * mm, "end": v(33.77, -29.83) * mm});
            skLineSegment(sketch, "E4019", {"start": v(33.77, -29.83) * mm, "end": v(33.9, -29.94) * mm});
            skLineSegment(sketch, "E4020", {"start": v(33.9, -29.94) * mm, "end": v(34.03, -30.05) * mm});
            skLineSegment(sketch, "E4021", {"start": v(34.03, -30.05) * mm, "end": v(34.15, -30.16) * mm});
            skLineSegment(sketch, "E4022", {"start": v(34.15, -30.16) * mm, "end": v(34.28, -30.27) * mm});
            skLineSegment(sketch, "E4023", {"start": v(34.28, -30.27) * mm, "end": v(34.4, -30.38) * mm});
            skLineSegment(sketch, "E4024", {"start": v(34.4, -30.38) * mm, "end": v(34.53, -30.49) * mm});
            skLineSegment(sketch, "E4025", {"start": v(34.53, -30.49) * mm, "end": v(34.66, -30.6) * mm});
            skLineSegment(sketch, "E4026", {"start": v(34.66, -30.6) * mm, "end": v(34.79, -30.7) * mm});
            skLineSegment(sketch, "E4027", {"start": v(34.79, -30.7) * mm, "end": v(34.92, -30.82) * mm});
            skLineSegment(sketch, "E4028", {"start": v(34.92, -30.82) * mm, "end": v(35.04, -30.93) * mm});
            skLineSegment(sketch, "E4029", {"start": v(35.04, -30.93) * mm, "end": v(35.17, -31.04) * mm});
            skLineSegment(sketch, "E4030", {"start": v(35.17, -31.04) * mm, "end": v(35.3, -31.15) * mm});
            skLineSegment(sketch, "E4031", {"start": v(35.3, -31.15) * mm, "end": v(35.46, -31.24) * mm});
            skLineSegment(sketch, "E4032", {"start": v(35.46, -31.24) * mm, "end": v(35.63, -31.28) * mm});
            skLineSegment(sketch, "E4033", {"start": v(35.63, -31.28) * mm, "end": v(35.8, -31.28) * mm});
            skLineSegment(sketch, "E4034", {"start": v(35.8, -31.28) * mm, "end": v(35.97, -31.24) * mm});
            skLineSegment(sketch, "E4035", {"start": v(35.97, -31.24) * mm, "end": v(36.12, -31.15) * mm});
            skLineSegment(sketch, "E4036", {"start": v(36.12, -31.15) * mm, "end": v(36.24, -31.03) * mm});
            skLineSegment(sketch, "E4037", {"start": v(36.24, -31.03) * mm, "end": v(36.32, -30.87) * mm});
            skLineSegment(sketch, "E4038", {"start": v(36.32, -30.87) * mm, "end": v(36.37, -30.7) * mm});
            skLineSegment(sketch, "E4039", {"start": v(36.37, -30.7) * mm, "end": v(36.36, -30.53) * mm});
            skLineSegment(sketch, "E4040", {"start": v(36.36, -30.53) * mm, "end": v(36.32, -30.37) * mm});
            skLineSegment(sketch, "E4041", {"start": v(36.32, -30.37) * mm, "end": v(36.23, -30.22) * mm});
            skLineSegment(sketch, "E4042", {"start": v(36.23, -30.22) * mm, "end": v(36.1, -30.1) * mm});
            skLineSegment(sketch, "E4043", {"start": v(36.1, -30.1) * mm, "end": v(35.98, -30) * mm});
            skLineSegment(sketch, "E4044", {"start": v(35.98, -30) * mm, "end": v(35.85, -29.89) * mm});
            skLineSegment(sketch, "E4045", {"start": v(35.85, -29.89) * mm, "end": v(35.72, -29.78) * mm});
            skLineSegment(sketch, "E4046", {"start": v(35.72, -29.78) * mm, "end": v(35.6, -29.68) * mm});
            skLineSegment(sketch, "E4047", {"start": v(35.6, -29.68) * mm, "end": v(35.46, -29.57) * mm});
            skLineSegment(sketch, "E4048", {"start": v(35.46, -29.57) * mm, "end": v(35.33, -29.47) * mm});
            skLineSegment(sketch, "E4049", {"start": v(35.33, -29.47) * mm, "end": v(35.2, -29.36) * mm});
            skLineSegment(sketch, "E4050", {"start": v(35.2, -29.36) * mm, "end": v(35.07, -29.25) * mm});
            skLineSegment(sketch, "E4051", {"start": v(35.07, -29.25) * mm, "end": v(34.94, -29.15) * mm});
            skLineSegment(sketch, "E4052", {"start": v(34.94, -29.15) * mm, "end": v(34.81, -29.04) * mm});
            skLineSegment(sketch, "E4053", {"start": v(34.81, -29.04) * mm, "end": v(34.68, -28.93) * mm});
            skLineSegment(sketch, "E4054", {"start": v(34.68, -28.93) * mm, "end": v(34.55, -28.83) * mm});
            skLineSegment(sketch, "E4055", {"start": v(34.55, -28.83) * mm, "end": v(34.46, -28.75) * mm});
            skLineSegment(sketch, "E4056", {"start": v(34.46, -28.75) * mm, "end": v(34.56, -28.62) * mm});
            skLineSegment(sketch, "E4057", {"start": v(34.56, -28.62) * mm, "end": v(34.66, -28.49) * mm});
            skLineSegment(sketch, "E4058", {"start": v(34.66, -28.49) * mm, "end": v(34.76, -28.36) * mm});
            skLineSegment(sketch, "E4059", {"start": v(34.76, -28.36) * mm, "end": v(34.87, -28.23) * mm});
            skLineSegment(sketch, "E4060", {"start": v(34.87, -28.23) * mm, "end": v(34.97, -28.1) * mm});
            skLineSegment(sketch, "E4061", {"start": v(34.97, -28.1) * mm, "end": v(35.07, -27.97) * mm});
            skLineSegment(sketch, "E4062", {"start": v(35.07, -27.97) * mm, "end": v(35.17, -27.83) * mm});
            skLineSegment(sketch, "E4063", {"start": v(35.17, -27.83) * mm, "end": v(35.28, -27.7) * mm});
            skLineSegment(sketch, "E4064", {"start": v(35.28, -27.7) * mm, "end": v(35.38, -27.57) * mm});
            skLineSegment(sketch, "E4065", {"start": v(35.38, -27.57) * mm, "end": v(35.48, -27.44) * mm});
            skLineSegment(sketch, "E4066", {"start": v(35.48, -27.44) * mm, "end": v(35.58, -27.3) * mm});
            skLineSegment(sketch, "E4067", {"start": v(35.58, -27.3) * mm, "end": v(35.63, -27.25) * mm});
            skLineSegment(sketch, "E4068", {"start": v(35.63, -27.25) * mm, "end": v(35.77, -27.35) * mm});
            skLineSegment(sketch, "E4069", {"start": v(35.77, -27.35) * mm, "end": v(35.9, -27.45) * mm});
            skLineSegment(sketch, "E4070", {"start": v(35.9, -27.45) * mm, "end": v(36.04, -27.55) * mm});
            skLineSegment(sketch, "E4071", {"start": v(36.04, -27.55) * mm, "end": v(36.17, -27.65) * mm});
            skLineSegment(sketch, "E4072", {"start": v(36.17, -27.65) * mm, "end": v(36.3, -27.75) * mm});
            skLineSegment(sketch, "E4073", {"start": v(36.3, -27.75) * mm, "end": v(36.44, -27.85) * mm});
            skLineSegment(sketch, "E4074", {"start": v(36.44, -27.85) * mm, "end": v(36.57, -27.95) * mm});
            skLineSegment(sketch, "E4075", {"start": v(36.57, -27.95) * mm, "end": v(36.7, -28.05) * mm});
            skLineSegment(sketch, "E4076", {"start": v(36.7, -28.05) * mm, "end": v(36.84, -28.15) * mm});
            skLineSegment(sketch, "E4077", {"start": v(36.84, -28.15) * mm, "end": v(36.98, -28.25) * mm});
            skLineSegment(sketch, "E4078", {"start": v(36.98, -28.25) * mm, "end": v(37.11, -28.35) * mm});
            skLineSegment(sketch, "E4079", {"start": v(37.11, -28.35) * mm, "end": v(37.25, -28.45) * mm});
            skLineSegment(sketch, "E4080", {"start": v(37.25, -28.45) * mm, "end": v(37.4, -28.56) * mm});
            skLineSegment(sketch, "E4081", {"start": v(37.4, -28.56) * mm, "end": v(37.55, -28.63) * mm});
            skLineSegment(sketch, "E4082", {"start": v(37.55, -28.63) * mm, "end": v(37.72, -28.67) * mm});
            skLineSegment(sketch, "E4083", {"start": v(37.72, -28.67) * mm, "end": v(37.9, -28.65) * mm});
            skLineSegment(sketch, "E4084", {"start": v(37.9, -28.65) * mm, "end": v(38.06, -28.6) * mm});
            skLineSegment(sketch, "E4085", {"start": v(38.06, -28.6) * mm, "end": v(38.2, -28.5) * mm});
            skLineSegment(sketch, "E4086", {"start": v(38.2, -28.5) * mm, "end": v(38.31, -28.37) * mm});
            skLineSegment(sketch, "E4087", {"start": v(38.31, -28.37) * mm, "end": v(38.39, -28.2) * mm});
            skLineSegment(sketch, "E4088", {"start": v(38.39, -28.2) * mm, "end": v(38.42, -28.04) * mm});
            skLineSegment(sketch, "E4089", {"start": v(38.42, -28.04) * mm, "end": v(38.4, -27.87) * mm});
            skLineSegment(sketch, "E4090", {"start": v(38.4, -27.87) * mm, "end": v(38.34, -27.7) * mm});
            skLineSegment(sketch, "E4091", {"start": v(38.34, -27.7) * mm, "end": v(38.25, -27.56) * mm});
            skLineSegment(sketch, "E4092", {"start": v(38.25, -27.56) * mm, "end": v(38.12, -27.45) * mm});
            skLineSegment(sketch, "E4093", {"start": v(38.12, -27.45) * mm, "end": v(37.98, -27.36) * mm});
            skLineSegment(sketch, "E4094", {"start": v(37.98, -27.36) * mm, "end": v(37.85, -27.26) * mm});
            skLineSegment(sketch, "E4095", {"start": v(37.85, -27.26) * mm, "end": v(37.71, -27.16) * mm});
            skLineSegment(sketch, "E4096", {"start": v(37.71, -27.16) * mm, "end": v(37.58, -27.07) * mm});
            skLineSegment(sketch, "E4097", {"start": v(37.58, -27.07) * mm, "end": v(37.44, -26.97) * mm});
            skLineSegment(sketch, "E4098", {"start": v(37.44, -26.97) * mm, "end": v(37.3, -26.87) * mm});
            skLineSegment(sketch, "E4099", {"start": v(37.3, -26.87) * mm, "end": v(37.16, -26.78) * mm});
            skLineSegment(sketch, "E4100", {"start": v(37.16, -26.78) * mm, "end": v(37.02, -26.68) * mm});
            skLineSegment(sketch, "E4101", {"start": v(37.02, -26.68) * mm, "end": v(36.89, -26.58) * mm});
            skLineSegment(sketch, "E4102", {"start": v(36.89, -26.58) * mm, "end": v(36.75, -26.49) * mm});
            skLineSegment(sketch, "E4103", {"start": v(36.75, -26.49) * mm, "end": v(36.61, -26.39) * mm});
            skLineSegment(sketch, "E4104", {"start": v(36.61, -26.39) * mm, "end": v(36.48, -26.3) * mm});
            skLineSegment(sketch, "E4105", {"start": v(36.48, -26.3) * mm, "end": v(36.38, -26.22) * mm});
            skLineSegment(sketch, "E4106", {"start": v(36.38, -26.22) * mm, "end": v(36.47, -26.09) * mm});
            skLineSegment(sketch, "E4107", {"start": v(36.47, -26.09) * mm, "end": v(36.56, -25.95) * mm});
            skLineSegment(sketch, "E4108", {"start": v(36.56, -25.95) * mm, "end": v(36.66, -25.8) * mm});
            skLineSegment(sketch, "E4109", {"start": v(36.66, -25.8) * mm, "end": v(36.75, -25.67) * mm});
            skLineSegment(sketch, "E4110", {"start": v(36.75, -25.67) * mm, "end": v(36.84, -25.53) * mm});
            skLineSegment(sketch, "E4111", {"start": v(36.84, -25.53) * mm, "end": v(36.94, -25.4) * mm});
            skLineSegment(sketch, "E4112", {"start": v(36.94, -25.4) * mm, "end": v(37.03, -25.26) * mm});
            skLineSegment(sketch, "E4113", {"start": v(37.03, -25.26) * mm, "end": v(37.12, -25.12) * mm});
            skLineSegment(sketch, "E4114", {"start": v(37.12, -25.12) * mm, "end": v(37.21, -24.98) * mm});
            skLineSegment(sketch, "E4115", {"start": v(37.21, -24.98) * mm, "end": v(37.3, -24.84) * mm});
            skLineSegment(sketch, "E4116", {"start": v(37.3, -24.84) * mm, "end": v(37.4, -24.7) * mm});
            skLineSegment(sketch, "E4117", {"start": v(37.4, -24.7) * mm, "end": v(37.45, -24.64) * mm});
            skLineSegment(sketch, "E4118", {"start": v(37.45, -24.64) * mm, "end": v(37.59, -24.73) * mm});
            skLineSegment(sketch, "E4119", {"start": v(37.59, -24.73) * mm, "end": v(37.73, -24.82) * mm});
            skLineSegment(sketch, "E4120", {"start": v(37.73, -24.82) * mm, "end": v(37.87, -24.91) * mm});
            skLineSegment(sketch, "E4121", {"start": v(37.87, -24.91) * mm, "end": v(38, -25) * mm});
            skLineSegment(sketch, "E4122", {"start": v(38, -25) * mm, "end": v(38.15, -25.1) * mm});
            skLineSegment(sketch, "E4123", {"start": v(38.15, -25.1) * mm, "end": v(38.3, -25.18) * mm});
            skLineSegment(sketch, "E4124", {"start": v(38.3, -25.18) * mm, "end": v(38.43, -25.27) * mm});
            skLineSegment(sketch, "E4125", {"start": v(38.43, -25.27) * mm, "end": v(38.57, -25.36) * mm});
            skLineSegment(sketch, "E4126", {"start": v(38.57, -25.36) * mm, "end": v(38.72, -25.46) * mm});
            skLineSegment(sketch, "E4127", {"start": v(38.72, -25.46) * mm, "end": v(38.86, -25.55) * mm});
            skLineSegment(sketch, "E4128", {"start": v(38.86, -25.55) * mm, "end": v(39, -25.64) * mm});
            skLineSegment(sketch, "E4129", {"start": v(39, -25.64) * mm, "end": v(39.14, -25.73) * mm});
            skLineSegment(sketch, "E4130", {"start": v(39.14, -25.73) * mm, "end": v(39.3, -25.83) * mm});
            skLineSegment(sketch, "E4131", {"start": v(39.3, -25.83) * mm, "end": v(39.45, -25.9) * mm});
            skLineSegment(sketch, "E4132", {"start": v(39.45, -25.9) * mm, "end": v(39.62, -25.91) * mm});
            skLineSegment(sketch, "E4133", {"start": v(39.62, -25.91) * mm, "end": v(39.8, -25.89) * mm});
            skLineSegment(sketch, "E4134", {"start": v(39.8, -25.89) * mm, "end": v(39.96, -25.82) * mm});
            skLineSegment(sketch, "E4135", {"start": v(39.96, -25.82) * mm, "end": v(40.1, -25.7) * mm});
            skLineSegment(sketch, "E4136", {"start": v(40.1, -25.7) * mm, "end": v(40.2, -25.57) * mm});
            skLineSegment(sketch, "E4137", {"start": v(40.2, -25.57) * mm, "end": v(40.26, -25.4) * mm});
            skLineSegment(sketch, "E4138", {"start": v(40.26, -25.4) * mm, "end": v(40.28, -25.24) * mm});
            skLineSegment(sketch, "E4139", {"start": v(40.28, -25.24) * mm, "end": v(40.25, -25.06) * mm});
            skLineSegment(sketch, "E4140", {"start": v(40.25, -25.06) * mm, "end": v(40.18, -24.9) * mm});
            skLineSegment(sketch, "E4141", {"start": v(40.18, -24.9) * mm, "end": v(40.07, -24.77) * mm});
            skLineSegment(sketch, "E4142", {"start": v(40.07, -24.77) * mm, "end": v(39.94, -24.67) * mm});
            skLineSegment(sketch, "E4143", {"start": v(39.94, -24.67) * mm, "end": v(39.8, -24.58) * mm});
            skLineSegment(sketch, "E4144", {"start": v(39.8, -24.58) * mm, "end": v(39.66, -24.5) * mm});
            skLineSegment(sketch, "E4145", {"start": v(39.66, -24.5) * mm, "end": v(39.51, -24.41) * mm});
            skLineSegment(sketch, "E4146", {"start": v(39.51, -24.41) * mm, "end": v(39.37, -24.33) * mm});
            skLineSegment(sketch, "E4147", {"start": v(39.37, -24.33) * mm, "end": v(39.22, -24.24) * mm});
            skLineSegment(sketch, "E4148", {"start": v(39.22, -24.24) * mm, "end": v(39.08, -24.15) * mm});
            skLineSegment(sketch, "E4149", {"start": v(39.08, -24.15) * mm, "end": v(38.94, -24.07) * mm});
            skLineSegment(sketch, "E4150", {"start": v(38.94, -24.07) * mm, "end": v(38.8, -23.98) * mm});
            skLineSegment(sketch, "E4151", {"start": v(38.8, -23.98) * mm, "end": v(38.65, -23.9) * mm});
            skLineSegment(sketch, "E4152", {"start": v(38.65, -23.9) * mm, "end": v(38.5, -23.8) * mm});
            skLineSegment(sketch, "E4153", {"start": v(38.5, -23.8) * mm, "end": v(38.36, -23.72) * mm});
            skLineSegment(sketch, "E4154", {"start": v(38.36, -23.72) * mm, "end": v(38.22, -23.63) * mm});
            skLineSegment(sketch, "E4155", {"start": v(38.22, -23.63) * mm, "end": v(38.12, -23.57) * mm});
            skLineSegment(sketch, "E4156", {"start": v(38.12, -23.57) * mm, "end": v(38.2, -23.42) * mm});
            skLineSegment(sketch, "E4157", {"start": v(38.2, -23.42) * mm, "end": v(38.28, -23.28) * mm});
            skLineSegment(sketch, "E4158", {"start": v(38.28, -23.28) * mm, "end": v(38.37, -23.13) * mm});
            skLineSegment(sketch, "E4159", {"start": v(38.37, -23.13) * mm, "end": v(38.45, -23) * mm});
            skLineSegment(sketch, "E4160", {"start": v(38.45, -23) * mm, "end": v(38.53, -22.85) * mm});
            skLineSegment(sketch, "E4161", {"start": v(38.53, -22.85) * mm, "end": v(38.62, -22.7) * mm});
            skLineSegment(sketch, "E4162", {"start": v(38.62, -22.7) * mm, "end": v(38.7, -22.56) * mm});
            skLineSegment(sketch, "E4163", {"start": v(38.7, -22.56) * mm, "end": v(38.78, -22.41) * mm});
            skLineSegment(sketch, "E4164", {"start": v(38.78, -22.41) * mm, "end": v(38.86, -22.27) * mm});
            skLineSegment(sketch, "E4165", {"start": v(38.86, -22.27) * mm, "end": v(38.95, -22.13) * mm});
            skLineSegment(sketch, "E4166", {"start": v(38.95, -22.13) * mm, "end": v(39.03, -21.98) * mm});
            skLineSegment(sketch, "E4167", {"start": v(39.03, -21.98) * mm, "end": v(39.07, -21.91) * mm});
            skLineSegment(sketch, "E4168", {"start": v(39.07, -21.91) * mm, "end": v(39.22, -22) * mm});
            skLineSegment(sketch, "E4169", {"start": v(39.22, -22) * mm, "end": v(39.36, -22.07) * mm});
            skLineSegment(sketch, "E4170", {"start": v(39.36, -22.07) * mm, "end": v(39.51, -22.15) * mm});
            skLineSegment(sketch, "E4171", {"start": v(39.51, -22.15) * mm, "end": v(39.66, -22.23) * mm});
            skLineSegment(sketch, "E4172", {"start": v(39.66, -22.23) * mm, "end": v(39.8, -22.31) * mm});
            skLineSegment(sketch, "E4173", {"start": v(39.8, -22.31) * mm, "end": v(39.95, -22.4) * mm});
            skLineSegment(sketch, "E4174", {"start": v(39.95, -22.4) * mm, "end": v(40.1, -22.48) * mm});
            skLineSegment(sketch, "E4175", {"start": v(40.1, -22.48) * mm, "end": v(40.25, -22.56) * mm});
            skLineSegment(sketch, "E4176", {"start": v(40.25, -22.56) * mm, "end": v(40.4, -22.64) * mm});
            skLineSegment(sketch, "E4177", {"start": v(40.4, -22.64) * mm, "end": v(40.54, -22.72) * mm});
            skLineSegment(sketch, "E4178", {"start": v(40.54, -22.72) * mm, "end": v(40.69, -22.8) * mm});
            skLineSegment(sketch, "E4179", {"start": v(40.69, -22.8) * mm, "end": v(40.84, -22.88) * mm});
            skLineSegment(sketch, "E4180", {"start": v(40.84, -22.88) * mm, "end": v(41, -22.97) * mm});
            skLineSegment(sketch, "E4181", {"start": v(41, -22.97) * mm, "end": v(41.16, -23.02) * mm});
            skLineSegment(sketch, "E4182", {"start": v(41.16, -23.02) * mm, "end": v(41.33, -23.03) * mm});
            skLineSegment(sketch, "E4183", {"start": v(41.33, -23.03) * mm, "end": v(41.5, -23) * mm});
            skLineSegment(sketch, "E4184", {"start": v(41.5, -23) * mm, "end": v(41.66, -22.91) * mm});
            skLineSegment(sketch, "E4185", {"start": v(41.66, -22.91) * mm, "end": v(41.79, -22.8) * mm});
            skLineSegment(sketch, "E4186", {"start": v(41.79, -22.8) * mm, "end": v(41.88, -22.65) * mm});
            skLineSegment(sketch, "E4187", {"start": v(41.88, -22.65) * mm, "end": v(41.93, -22.48) * mm});
            skLineSegment(sketch, "E4188", {"start": v(41.93, -22.48) * mm, "end": v(41.94, -22.3) * mm});
            skLineSegment(sketch, "E4189", {"start": v(41.94, -22.3) * mm, "end": v(41.9, -22.14) * mm});
            skLineSegment(sketch, "E4190", {"start": v(41.9, -22.14) * mm, "end": v(41.82, -21.99) * mm});
            skLineSegment(sketch, "E4191", {"start": v(41.82, -21.99) * mm, "end": v(41.7, -21.86) * mm});
            skLineSegment(sketch, "E4192", {"start": v(41.7, -21.86) * mm, "end": v(41.56, -21.77) * mm});
            skLineSegment(sketch, "E4193", {"start": v(41.56, -21.77) * mm, "end": v(41.41, -21.7) * mm});
            skLineSegment(sketch, "E4194", {"start": v(41.41, -21.7) * mm, "end": v(41.27, -21.62) * mm});
            skLineSegment(sketch, "E4195", {"start": v(41.27, -21.62) * mm, "end": v(41.12, -21.54) * mm});
            skLineSegment(sketch, "E4196", {"start": v(41.12, -21.54) * mm, "end": v(40.97, -21.47) * mm});
            skLineSegment(sketch, "E4197", {"start": v(40.97, -21.47) * mm, "end": v(40.82, -21.39) * mm});
            skLineSegment(sketch, "E4198", {"start": v(40.82, -21.39) * mm, "end": v(40.67, -21.31) * mm});
            skLineSegment(sketch, "E4199", {"start": v(40.67, -21.31) * mm, "end": v(40.52, -21.24) * mm});
            skLineSegment(sketch, "E4200", {"start": v(40.52, -21.24) * mm, "end": v(40.37, -21.16) * mm});
            skLineSegment(sketch, "E4201", {"start": v(40.37, -21.16) * mm, "end": v(40.22, -21.08) * mm});
            skLineSegment(sketch, "E4202", {"start": v(40.22, -21.08) * mm, "end": v(40.07, -21) * mm});
            skLineSegment(sketch, "E4203", {"start": v(40.07, -21) * mm, "end": v(39.92, -20.93) * mm});
            skLineSegment(sketch, "E4204", {"start": v(39.92, -20.93) * mm, "end": v(39.77, -20.85) * mm});
            skLineSegment(sketch, "E4205", {"start": v(39.77, -20.85) * mm, "end": v(39.67, -20.8) * mm});
            skLineSegment(sketch, "E4206", {"start": v(39.67, -20.8) * mm, "end": v(39.74, -20.65) * mm});
            skLineSegment(sketch, "E4207", {"start": v(39.74, -20.65) * mm, "end": v(39.81, -20.5) * mm});
            skLineSegment(sketch, "E4208", {"start": v(39.81, -20.5) * mm, "end": v(39.88, -20.35) * mm});
            skLineSegment(sketch, "E4209", {"start": v(39.88, -20.35) * mm, "end": v(39.96, -20.2) * mm});
            skLineSegment(sketch, "E4210", {"start": v(39.96, -20.2) * mm, "end": v(40.03, -20.05) * mm});
            skLineSegment(sketch, "E4211", {"start": v(40.03, -20.05) * mm, "end": v(40.1, -19.9) * mm});
            skLineSegment(sketch, "E4212", {"start": v(40.1, -19.9) * mm, "end": v(40.18, -19.75) * mm});
            skLineSegment(sketch, "E4213", {"start": v(40.18, -19.75) * mm, "end": v(40.25, -19.6) * mm});
            skLineSegment(sketch, "E4214", {"start": v(40.25, -19.6) * mm, "end": v(40.32, -19.45) * mm});
            skLineSegment(sketch, "E4215", {"start": v(40.32, -19.45) * mm, "end": v(40.4, -19.3) * mm});
            skLineSegment(sketch, "E4216", {"start": v(40.4, -19.3) * mm, "end": v(40.47, -19.15) * mm});
            skLineSegment(sketch, "E4217", {"start": v(40.47, -19.15) * mm, "end": v(40.5, -19.08) * mm});
            skLineSegment(sketch, "E4218", {"start": v(40.5, -19.08) * mm, "end": v(40.65, -19.15) * mm});
            skLineSegment(sketch, "E4219", {"start": v(40.65, -19.15) * mm, "end": v(40.8, -19.22) * mm});
            skLineSegment(sketch, "E4220", {"start": v(40.8, -19.22) * mm, "end": v(40.96, -19.29) * mm});
            skLineSegment(sketch, "E4221", {"start": v(40.96, -19.29) * mm, "end": v(41.11, -19.36) * mm});
            skLineSegment(sketch, "E4222", {"start": v(41.11, -19.36) * mm, "end": v(41.26, -19.43) * mm});
            skLineSegment(sketch, "E4223", {"start": v(41.26, -19.43) * mm, "end": v(41.42, -19.5) * mm});
            skLineSegment(sketch, "E4224", {"start": v(41.42, -19.5) * mm, "end": v(41.57, -19.57) * mm});
            skLineSegment(sketch, "E4225", {"start": v(41.57, -19.57) * mm, "end": v(41.72, -19.64) * mm});
            skLineSegment(sketch, "E4226", {"start": v(41.72, -19.64) * mm, "end": v(41.88, -19.71) * mm});
            skLineSegment(sketch, "E4227", {"start": v(41.88, -19.71) * mm, "end": v(42.03, -19.78) * mm});
            skLineSegment(sketch, "E4228", {"start": v(42.03, -19.78) * mm, "end": v(42.18, -19.85) * mm});
            skLineSegment(sketch, "E4229", {"start": v(42.18, -19.85) * mm, "end": v(42.33, -19.92) * mm});
            skLineSegment(sketch, "E4230", {"start": v(42.33, -19.92) * mm, "end": v(42.5, -20) * mm});
            skLineSegment(sketch, "E4231", {"start": v(42.5, -20) * mm, "end": v(42.66, -20.04) * mm});
            skLineSegment(sketch, "E4232", {"start": v(42.66, -20.04) * mm, "end": v(42.84, -20.03) * mm});
            skLineSegment(sketch, "E4233", {"start": v(42.84, -20.03) * mm, "end": v(43, -19.99) * mm});
            skLineSegment(sketch, "E4234", {"start": v(43, -19.99) * mm, "end": v(43.15, -19.9) * mm});
            skLineSegment(sketch, "E4235", {"start": v(43.15, -19.9) * mm, "end": v(43.27, -19.77) * mm});
            skLineSegment(sketch, "E4236", {"start": v(43.27, -19.77) * mm, "end": v(43.35, -19.62) * mm});
            skLineSegment(sketch, "E4237", {"start": v(43.35, -19.62) * mm, "end": v(43.4, -19.45) * mm});
            skLineSegment(sketch, "E4238", {"start": v(43.4, -19.45) * mm, "end": v(43.4, -19.27) * mm});
            skLineSegment(sketch, "E4239", {"start": v(43.4, -19.27) * mm, "end": v(43.34, -19.1) * mm});
            skLineSegment(sketch, "E4240", {"start": v(43.34, -19.1) * mm, "end": v(43.25, -18.96) * mm});
            skLineSegment(sketch, "E4241", {"start": v(43.25, -18.96) * mm, "end": v(43.12, -18.84) * mm});
            skLineSegment(sketch, "E4242", {"start": v(43.12, -18.84) * mm, "end": v(42.98, -18.77) * mm});
            skLineSegment(sketch, "E4243", {"start": v(42.98, -18.77) * mm, "end": v(42.82, -18.7) * mm});
            skLineSegment(sketch, "E4244", {"start": v(42.82, -18.7) * mm, "end": v(42.67, -18.63) * mm});
            skLineSegment(sketch, "E4245", {"start": v(42.67, -18.63) * mm, "end": v(42.52, -18.57) * mm});
            skLineSegment(sketch, "E4246", {"start": v(42.52, -18.57) * mm, "end": v(42.37, -18.5) * mm});
            skLineSegment(sketch, "E4247", {"start": v(42.37, -18.5) * mm, "end": v(42.2, -18.43) * mm});
            skLineSegment(sketch, "E4248", {"start": v(42.2, -18.43) * mm, "end": v(42.06, -18.37) * mm});
            skLineSegment(sketch, "E4249", {"start": v(42.06, -18.37) * mm, "end": v(41.9, -18.3) * mm});
            skLineSegment(sketch, "E4250", {"start": v(41.9, -18.3) * mm, "end": v(41.74, -18.23) * mm});
            skLineSegment(sketch, "E4251", {"start": v(41.74, -18.23) * mm, "end": v(41.6, -18.17) * mm});
            skLineSegment(sketch, "E4252", {"start": v(41.6, -18.17) * mm, "end": v(41.44, -18.1) * mm});
            skLineSegment(sketch, "E4253", {"start": v(41.44, -18.1) * mm, "end": v(41.28, -18.04) * mm});
            skLineSegment(sketch, "E4254", {"start": v(41.28, -18.04) * mm, "end": v(41.13, -17.97) * mm});
            skLineSegment(sketch, "E4255", {"start": v(41.13, -17.97) * mm, "end": v(41.02, -17.92) * mm});
            skLineSegment(sketch, "E4256", {"start": v(41.02, -17.92) * mm, "end": v(41.08, -17.77) * mm});
            skLineSegment(sketch, "E4257", {"start": v(41.08, -17.77) * mm, "end": v(41.14, -17.61) * mm});
            skLineSegment(sketch, "E4258", {"start": v(41.14, -17.61) * mm, "end": v(41.2, -17.46) * mm});
            skLineSegment(sketch, "E4259", {"start": v(41.2, -17.46) * mm, "end": v(41.27, -17.3) * mm});
            skLineSegment(sketch, "E4260", {"start": v(41.27, -17.3) * mm, "end": v(41.33, -17.15) * mm});
            skLineSegment(sketch, "E4261", {"start": v(41.33, -17.15) * mm, "end": v(41.4, -17) * mm});
            skLineSegment(sketch, "E4262", {"start": v(41.4, -17) * mm, "end": v(41.45, -16.84) * mm});
            skLineSegment(sketch, "E4263", {"start": v(41.45, -16.84) * mm, "end": v(41.52, -16.69) * mm});
            skLineSegment(sketch, "E4264", {"start": v(41.52, -16.69) * mm, "end": v(41.58, -16.53) * mm});
            skLineSegment(sketch, "E4265", {"start": v(41.58, -16.53) * mm, "end": v(41.64, -16.38) * mm});
            skLineSegment(sketch, "E4266", {"start": v(41.64, -16.38) * mm, "end": v(41.7, -16.23) * mm});
            skLineSegment(sketch, "E4267", {"start": v(41.7, -16.23) * mm, "end": v(41.73, -16.15) * mm});
            skLineSegment(sketch, "E4268", {"start": v(41.73, -16.15) * mm, "end": v(41.89, -16.2) * mm});
            skLineSegment(sketch, "E4269", {"start": v(41.89, -16.2) * mm, "end": v(42.04, -16.27) * mm});
            skLineSegment(sketch, "E4270", {"start": v(42.04, -16.27) * mm, "end": v(42.2, -16.33) * mm});
            skLineSegment(sketch, "E4271", {"start": v(42.2, -16.33) * mm, "end": v(42.36, -16.39) * mm});
            skLineSegment(sketch, "E4272", {"start": v(42.36, -16.39) * mm, "end": v(42.52, -16.45) * mm});
            skLineSegment(sketch, "E4273", {"start": v(42.52, -16.45) * mm, "end": v(42.68, -16.5) * mm});
            skLineSegment(sketch, "E4274", {"start": v(42.68, -16.5) * mm, "end": v(42.83, -16.57) * mm});
            skLineSegment(sketch, "E4275", {"start": v(42.83, -16.57) * mm, "end": v(42.99, -16.63) * mm});
            skLineSegment(sketch, "E4276", {"start": v(42.99, -16.63) * mm, "end": v(43.15, -16.69) * mm});
            skLineSegment(sketch, "E4277", {"start": v(43.15, -16.69) * mm, "end": v(43.3, -16.75) * mm});
            skLineSegment(sketch, "E4278", {"start": v(43.3, -16.75) * mm, "end": v(43.46, -16.8) * mm});
            skLineSegment(sketch, "E4279", {"start": v(43.46, -16.8) * mm, "end": v(43.62, -16.87) * mm});
            skLineSegment(sketch, "E4280", {"start": v(43.62, -16.87) * mm, "end": v(43.78, -16.93) * mm});
            skLineSegment(sketch, "E4281", {"start": v(43.78, -16.93) * mm, "end": v(43.96, -16.96) * mm});
            skLineSegment(sketch, "E4282", {"start": v(43.96, -16.96) * mm, "end": v(44.13, -16.94) * mm});
            skLineSegment(sketch, "E4283", {"start": v(44.13, -16.94) * mm, "end": v(44.3, -16.88) * mm});
            skLineSegment(sketch, "E4284", {"start": v(44.3, -16.88) * mm, "end": v(44.43, -16.78) * mm});
            skLineSegment(sketch, "E4285", {"start": v(44.43, -16.78) * mm, "end": v(44.54, -16.65) * mm});
            skLineSegment(sketch, "E4286", {"start": v(44.54, -16.65) * mm, "end": v(44.62, -16.49) * mm});
            skLineSegment(sketch, "E4287", {"start": v(44.62, -16.49) * mm, "end": v(44.64, -16.32) * mm});
            skLineSegment(sketch, "E4288", {"start": v(44.64, -16.32) * mm, "end": v(44.63, -16.15) * mm});
            skLineSegment(sketch, "E4289", {"start": v(44.63, -16.15) * mm, "end": v(44.57, -15.98) * mm});
            skLineSegment(sketch, "E4290", {"start": v(44.57, -15.98) * mm, "end": v(44.46, -15.84) * mm});
            skLineSegment(sketch, "E4291", {"start": v(44.46, -15.84) * mm, "end": v(44.33, -15.73) * mm});
            skLineSegment(sketch, "E4292", {"start": v(44.33, -15.73) * mm, "end": v(44.18, -15.67) * mm});
            skLineSegment(sketch, "E4293", {"start": v(44.18, -15.67) * mm, "end": v(44.02, -15.6) * mm});
            skLineSegment(sketch, "E4294", {"start": v(44.02, -15.6) * mm, "end": v(43.86, -15.55) * mm});
            skLineSegment(sketch, "E4295", {"start": v(43.86, -15.55) * mm, "end": v(43.7, -15.5) * mm});
            skLineSegment(sketch, "E4296", {"start": v(43.7, -15.5) * mm, "end": v(43.55, -15.44) * mm});
            skLineSegment(sketch, "E4297", {"start": v(43.55, -15.44) * mm, "end": v(43.39, -15.39) * mm});
            skLineSegment(sketch, "E4298", {"start": v(43.39, -15.39) * mm, "end": v(43.23, -15.33) * mm});
            skLineSegment(sketch, "E4299", {"start": v(43.23, -15.33) * mm, "end": v(43.07, -15.28) * mm});
            skLineSegment(sketch, "E4300", {"start": v(43.07, -15.28) * mm, "end": v(42.91, -15.22) * mm});
            skLineSegment(sketch, "E4301", {"start": v(42.91, -15.22) * mm, "end": v(42.76, -15.17) * mm});
            skLineSegment(sketch, "E4302", {"start": v(42.76, -15.17) * mm, "end": v(42.6, -15.11) * mm});
            skLineSegment(sketch, "E4303", {"start": v(42.6, -15.11) * mm, "end": v(42.44, -15.06) * mm});
            skLineSegment(sketch, "E4304", {"start": v(42.44, -15.06) * mm, "end": v(42.28, -15) * mm});
            skLineSegment(sketch, "E4305", {"start": v(42.28, -15) * mm, "end": v(42.17, -14.96) * mm});
            skLineSegment(sketch, "E4306", {"start": v(42.17, -14.96) * mm, "end": v(42.22, -14.8) * mm});
            skLineSegment(sketch, "E4307", {"start": v(42.22, -14.8) * mm, "end": v(42.27, -14.65) * mm});
            skLineSegment(sketch, "E4308", {"start": v(42.27, -14.65) * mm, "end": v(42.32, -14.49) * mm});
            skLineSegment(sketch, "E4309", {"start": v(42.32, -14.49) * mm, "end": v(42.37, -14.33) * mm});
            skLineSegment(sketch, "E4310", {"start": v(42.37, -14.33) * mm, "end": v(42.42, -14.17) * mm});
            skLineSegment(sketch, "E4311", {"start": v(42.42, -14.17) * mm, "end": v(42.47, -14.01) * mm});
            skLineSegment(sketch, "E4312", {"start": v(42.47, -14.01) * mm, "end": v(42.53, -13.85) * mm});
            skLineSegment(sketch, "E4313", {"start": v(42.53, -13.85) * mm, "end": v(42.58, -13.7) * mm});
            skLineSegment(sketch, "E4314", {"start": v(42.58, -13.7) * mm, "end": v(42.63, -13.54) * mm});
            skLineSegment(sketch, "E4315", {"start": v(42.63, -13.54) * mm, "end": v(42.68, -13.38) * mm});
            skLineSegment(sketch, "E4316", {"start": v(42.68, -13.38) * mm, "end": v(42.73, -13.22) * mm});
            skLineSegment(sketch, "E4317", {"start": v(42.73, -13.22) * mm, "end": v(42.76, -13.14) * mm});
            skLineSegment(sketch, "E4318", {"start": v(42.76, -13.14) * mm, "end": v(42.92, -13.2) * mm});
            skLineSegment(sketch, "E4319", {"start": v(42.92, -13.2) * mm, "end": v(43.07, -13.24) * mm});
            skLineSegment(sketch, "E4320", {"start": v(43.07, -13.24) * mm, "end": v(43.24, -13.3) * mm});
            skLineSegment(sketch, "E4321", {"start": v(43.24, -13.3) * mm, "end": v(43.4, -13.34) * mm});
            skLineSegment(sketch, "E4322", {"start": v(43.4, -13.34) * mm, "end": v(43.56, -13.39) * mm});
            skLineSegment(sketch, "E4323", {"start": v(43.56, -13.39) * mm, "end": v(43.72, -13.44) * mm});
            skLineSegment(sketch, "E4324", {"start": v(43.72, -13.44) * mm, "end": v(43.88, -13.48) * mm});
            skLineSegment(sketch, "E4325", {"start": v(43.88, -13.48) * mm, "end": v(44.04, -13.53) * mm});
            skLineSegment(sketch, "E4326", {"start": v(44.04, -13.53) * mm, "end": v(44.2, -13.58) * mm});
            skLineSegment(sketch, "E4327", {"start": v(44.2, -13.58) * mm, "end": v(44.36, -13.63) * mm});
            skLineSegment(sketch, "E4328", {"start": v(44.36, -13.63) * mm, "end": v(44.52, -13.68) * mm});
            skLineSegment(sketch, "E4329", {"start": v(44.52, -13.68) * mm, "end": v(44.69, -13.73) * mm});
            skLineSegment(sketch, "E4330", {"start": v(44.69, -13.73) * mm, "end": v(44.86, -13.78) * mm});
            skLineSegment(sketch, "E4331", {"start": v(44.86, -13.78) * mm, "end": v(45.03, -13.8) * mm});
            skLineSegment(sketch, "E4332", {"start": v(45.03, -13.8) * mm, "end": v(45.2, -13.77) * mm});
            skLineSegment(sketch, "E4333", {"start": v(45.2, -13.77) * mm, "end": v(45.36, -13.7) * mm});
            skLineSegment(sketch, "E4334", {"start": v(45.36, -13.7) * mm, "end": v(45.5, -13.59) * mm});
            skLineSegment(sketch, "E4335", {"start": v(45.5, -13.59) * mm, "end": v(45.6, -13.44) * mm});
            skLineSegment(sketch, "E4336", {"start": v(45.6, -13.44) * mm, "end": v(45.66, -13.28) * mm});
            skLineSegment(sketch, "E4337", {"start": v(45.66, -13.28) * mm, "end": v(45.67, -13.1) * mm});
            skLineSegment(sketch, "E4338", {"start": v(45.67, -13.1) * mm, "end": v(45.64, -12.94) * mm});
            skLineSegment(sketch, "E4339", {"start": v(45.64, -12.94) * mm, "end": v(45.57, -12.78) * mm});
            skLineSegment(sketch, "E4340", {"start": v(45.57, -12.78) * mm, "end": v(45.46, -12.65) * mm});
            skLineSegment(sketch, "E4341", {"start": v(45.46, -12.65) * mm, "end": v(45.32, -12.55) * mm});
            skLineSegment(sketch, "E4342", {"start": v(45.32, -12.55) * mm, "end": v(45.16, -12.5) * mm});
            skLineSegment(sketch, "E4343", {"start": v(45.16, -12.5) * mm, "end": v(45, -12.45) * mm});
            skLineSegment(sketch, "E4344", {"start": v(45, -12.45) * mm, "end": v(44.84, -12.4) * mm});
            skLineSegment(sketch, "E4345", {"start": v(44.84, -12.4) * mm, "end": v(44.68, -12.36) * mm});
            skLineSegment(sketch, "E4346", {"start": v(44.68, -12.36) * mm, "end": v(44.52, -12.31) * mm});
            skLineSegment(sketch, "E4347", {"start": v(44.52, -12.31) * mm, "end": v(44.35, -12.27) * mm});
            skLineSegment(sketch, "E4348", {"start": v(44.35, -12.27) * mm, "end": v(44.2, -12.23) * mm});
            skLineSegment(sketch, "E4349", {"start": v(44.2, -12.23) * mm, "end": v(44.03, -12.18) * mm});
            skLineSegment(sketch, "E4350", {"start": v(44.03, -12.18) * mm, "end": v(43.87, -12.14) * mm});
            skLineSegment(sketch, "E4351", {"start": v(43.87, -12.14) * mm, "end": v(43.7, -12.1) * mm});
            skLineSegment(sketch, "E4352", {"start": v(43.7, -12.1) * mm, "end": v(43.55, -12.05) * mm});
            skLineSegment(sketch, "E4353", {"start": v(43.55, -12.05) * mm, "end": v(43.38, -12) * mm});
            skLineSegment(sketch, "E4354", {"start": v(43.38, -12) * mm, "end": v(43.22, -11.96) * mm});
            skLineSegment(sketch, "E4355", {"start": v(43.22, -11.96) * mm, "end": v(43.1, -11.93) * mm});
            skLineSegment(sketch, "E4356", {"start": v(43.1, -11.93) * mm, "end": v(43.14, -11.77) * mm});
            skLineSegment(sketch, "E4357", {"start": v(43.14, -11.77) * mm, "end": v(43.19, -11.6) * mm});
            skLineSegment(sketch, "E4358", {"start": v(43.19, -11.6) * mm, "end": v(43.23, -11.44) * mm});
            skLineSegment(sketch, "E4359", {"start": v(43.23, -11.44) * mm, "end": v(43.27, -11.28) * mm});
            skLineSegment(sketch, "E4360", {"start": v(43.27, -11.28) * mm, "end": v(43.3, -11.12) * mm});
            skLineSegment(sketch, "E4361", {"start": v(43.3, -11.12) * mm, "end": v(43.35, -10.96) * mm});
            skLineSegment(sketch, "E4362", {"start": v(43.35, -10.96) * mm, "end": v(43.39, -10.8) * mm});
            skLineSegment(sketch, "E4363", {"start": v(43.39, -10.8) * mm, "end": v(43.43, -10.64) * mm});
            skLineSegment(sketch, "E4364", {"start": v(43.43, -10.64) * mm, "end": v(43.47, -10.48) * mm});
            skLineSegment(sketch, "E4365", {"start": v(43.47, -10.48) * mm, "end": v(43.5, -10.31) * mm});
            skLineSegment(sketch, "E4366", {"start": v(43.5, -10.31) * mm, "end": v(43.55, -10.15) * mm});
            skLineSegment(sketch, "E4367", {"start": v(43.55, -10.15) * mm, "end": v(43.57, -10.07) * mm});
            skLineSegment(sketch, "E4368", {"start": v(43.57, -10.07) * mm, "end": v(43.73, -10.11) * mm});
            skLineSegment(sketch, "E4369", {"start": v(43.73, -10.11) * mm, "end": v(43.9, -10.15) * mm});
            skLineSegment(sketch, "E4370", {"start": v(43.9, -10.15) * mm, "end": v(44.06, -10.19) * mm});
            skLineSegment(sketch, "E4371", {"start": v(44.06, -10.19) * mm, "end": v(44.22, -10.22) * mm});
            skLineSegment(sketch, "E4372", {"start": v(44.22, -10.22) * mm, "end": v(44.38, -10.26) * mm});
            skLineSegment(sketch, "E4373", {"start": v(44.38, -10.26) * mm, "end": v(44.55, -10.3) * mm});
            skLineSegment(sketch, "E4374", {"start": v(44.55, -10.3) * mm, "end": v(44.71, -10.33) * mm});
            skLineSegment(sketch, "E4375", {"start": v(44.71, -10.33) * mm, "end": v(44.87, -10.37) * mm});
            skLineSegment(sketch, "E4376", {"start": v(44.87, -10.37) * mm, "end": v(45.04, -10.4) * mm});
            skLineSegment(sketch, "E4377", {"start": v(45.04, -10.4) * mm, "end": v(45.2, -10.45) * mm});
            skLineSegment(sketch, "E4378", {"start": v(45.2, -10.45) * mm, "end": v(45.37, -10.48) * mm});
            skLineSegment(sketch, "E4379", {"start": v(45.37, -10.48) * mm, "end": v(45.53, -10.52) * mm});
            skLineSegment(sketch, "E4380", {"start": v(45.53, -10.52) * mm, "end": v(45.7, -10.56) * mm});
            skLineSegment(sketch, "E4381", {"start": v(45.7, -10.56) * mm, "end": v(45.88, -10.57) * mm});
            skLineSegment(sketch, "E4382", {"start": v(45.88, -10.57) * mm, "end": v(46.05, -10.53) * mm});
            skLineSegment(sketch, "E4383", {"start": v(46.05, -10.53) * mm, "end": v(46.2, -10.44) * mm});
            skLineSegment(sketch, "E4384", {"start": v(46.2, -10.44) * mm, "end": v(46.33, -10.32) * mm});
            skLineSegment(sketch, "E4385", {"start": v(46.33, -10.32) * mm, "end": v(46.42, -10.18) * mm});
            skLineSegment(sketch, "E4386", {"start": v(46.42, -10.18) * mm, "end": v(46.47, -10) * mm});
            skLineSegment(sketch, "E4387", {"start": v(46.47, -10) * mm, "end": v(46.47, -9.84) * mm});
            skLineSegment(sketch, "E4388", {"start": v(46.47, -9.84) * mm, "end": v(46.43, -9.67) * mm});
            skLineSegment(sketch, "E4389", {"start": v(46.43, -9.67) * mm, "end": v(46.35, -9.52) * mm});
            skLineSegment(sketch, "E4390", {"start": v(46.35, -9.52) * mm, "end": v(46.23, -9.39) * mm});
            skLineSegment(sketch, "E4391", {"start": v(46.23, -9.39) * mm, "end": v(46.08, -9.3) * mm});
            skLineSegment(sketch, "E4392", {"start": v(46.08, -9.3) * mm, "end": v(45.92, -9.26) * mm});
            skLineSegment(sketch, "E4393", {"start": v(45.92, -9.26) * mm, "end": v(45.76, -9.22) * mm});
            skLineSegment(sketch, "E4394", {"start": v(45.76, -9.22) * mm, "end": v(45.6, -9.19) * mm});
            skLineSegment(sketch, "E4395", {"start": v(45.6, -9.19) * mm, "end": v(45.43, -9.16) * mm});
            skLineSegment(sketch, "E4396", {"start": v(45.43, -9.16) * mm, "end": v(45.27, -9.12) * mm});
            skLineSegment(sketch, "E4397", {"start": v(45.27, -9.12) * mm, "end": v(45.1, -9.09) * mm});
            skLineSegment(sketch, "E4398", {"start": v(45.1, -9.09) * mm, "end": v(44.94, -9.06) * mm});
            skLineSegment(sketch, "E4399", {"start": v(44.94, -9.06) * mm, "end": v(44.77, -9.03) * mm});
            skLineSegment(sketch, "E4400", {"start": v(44.77, -9.03) * mm, "end": v(44.6, -9) * mm});
            skLineSegment(sketch, "E4401", {"start": v(44.6, -9) * mm, "end": v(44.44, -8.96) * mm});
            skLineSegment(sketch, "E4402", {"start": v(44.44, -8.96) * mm, "end": v(44.28, -8.93) * mm});
            skLineSegment(sketch, "E4403", {"start": v(44.28, -8.93) * mm, "end": v(44.11, -8.9) * mm});
            skLineSegment(sketch, "E4404", {"start": v(44.11, -8.9) * mm, "end": v(43.95, -8.86) * mm});
            skLineSegment(sketch, "E4405", {"start": v(43.95, -8.86) * mm, "end": v(43.83, -8.84) * mm});
            skLineSegment(sketch, "E4406", {"start": v(43.83, -8.84) * mm, "end": v(43.86, -8.67) * mm});
            skLineSegment(sketch, "E4407", {"start": v(43.86, -8.67) * mm, "end": v(43.89, -8.51) * mm});
            skLineSegment(sketch, "E4408", {"start": v(43.89, -8.51) * mm, "end": v(43.92, -8.35) * mm});
            skLineSegment(sketch, "E4409", {"start": v(43.92, -8.35) * mm, "end": v(43.95, -8.18) * mm});
            skLineSegment(sketch, "E4410", {"start": v(43.95, -8.18) * mm, "end": v(43.97, -8.02) * mm});
            skLineSegment(sketch, "E4411", {"start": v(43.97, -8.02) * mm, "end": v(44, -7.86) * mm});
            skLineSegment(sketch, "E4412", {"start": v(44, -7.86) * mm, "end": v(44.03, -7.7) * mm});
            skLineSegment(sketch, "E4413", {"start": v(44.03, -7.7) * mm, "end": v(44.06, -7.53) * mm});
            skLineSegment(sketch, "E4414", {"start": v(44.06, -7.53) * mm, "end": v(44.09, -7.36) * mm});
            skLineSegment(sketch, "E4415", {"start": v(44.09, -7.36) * mm, "end": v(44.12, -7.2) * mm});
            skLineSegment(sketch, "E4416", {"start": v(44.12, -7.2) * mm, "end": v(44.15, -7.04) * mm});
            skLineSegment(sketch, "E4417", {"start": v(44.15, -7.04) * mm, "end": v(44.16, -6.96) * mm});
            skLineSegment(sketch, "E4418", {"start": v(44.16, -6.96) * mm, "end": v(44.33, -6.98) * mm});
            skLineSegment(sketch, "E4419", {"start": v(44.33, -6.98) * mm, "end": v(44.5, -7) * mm});
            skLineSegment(sketch, "E4420", {"start": v(44.5, -7) * mm, "end": v(44.66, -7.03) * mm});
            skLineSegment(sketch, "E4421", {"start": v(44.66, -7.03) * mm, "end": v(44.82, -7.06) * mm});
            skLineSegment(sketch, "E4422", {"start": v(44.82, -7.06) * mm, "end": v(44.99, -7.08) * mm});
            skLineSegment(sketch, "E4423", {"start": v(44.99, -7.08) * mm, "end": v(45.16, -7.11) * mm});
            skLineSegment(sketch, "E4424", {"start": v(45.16, -7.11) * mm, "end": v(45.32, -7.14) * mm});
            skLineSegment(sketch, "E4425", {"start": v(45.32, -7.14) * mm, "end": v(45.49, -7.16) * mm});
            skLineSegment(sketch, "E4426", {"start": v(45.49, -7.16) * mm, "end": v(45.66, -7.19) * mm});
            skLineSegment(sketch, "E4427", {"start": v(45.66, -7.19) * mm, "end": v(45.82, -7.21) * mm});
            skLineSegment(sketch, "E4428", {"start": v(45.82, -7.21) * mm, "end": v(45.98, -7.24) * mm});
            skLineSegment(sketch, "E4429", {"start": v(45.98, -7.24) * mm, "end": v(46.15, -7.26) * mm});
            skLineSegment(sketch, "E4430", {"start": v(46.15, -7.26) * mm, "end": v(46.33, -7.3) * mm});
            skLineSegment(sketch, "E4431", {"start": v(46.33, -7.3) * mm, "end": v(46.5, -7.28) * mm});
            skLineSegment(sketch, "E4432", {"start": v(46.5, -7.28) * mm, "end": v(46.67, -7.23) * mm});
            skLineSegment(sketch, "E4433", {"start": v(46.67, -7.23) * mm, "end": v(46.82, -7.14) * mm});
            skLineSegment(sketch, "E4434", {"start": v(46.82, -7.14) * mm, "end": v(46.93, -7.01) * mm});
            skLineSegment(sketch, "E4435", {"start": v(46.93, -7.01) * mm, "end": v(47.01, -6.86) * mm});
            skLineSegment(sketch, "E4436", {"start": v(47.01, -6.86) * mm, "end": v(47.05, -6.69) * mm});
            skLineSegment(sketch, "E4437", {"start": v(47.05, -6.69) * mm, "end": v(47.04, -6.52) * mm});
            skLineSegment(sketch, "E4438", {"start": v(47.04, -6.52) * mm, "end": v(47, -6.35) * mm});
            skLineSegment(sketch, "E4439", {"start": v(47, -6.35) * mm, "end": v(46.9, -6.2) * mm});
            skLineSegment(sketch, "E4440", {"start": v(46.9, -6.2) * mm, "end": v(46.77, -6.09) * mm});
            skLineSegment(sketch, "E4441", {"start": v(46.77, -6.09) * mm, "end": v(46.62, -6) * mm});
            skLineSegment(sketch, "E4442", {"start": v(46.62, -6) * mm, "end": v(46.45, -5.97) * mm});
            skLineSegment(sketch, "E4443", {"start": v(46.45, -5.97) * mm, "end": v(46.29, -5.95) * mm});
            skLineSegment(sketch, "E4444", {"start": v(46.29, -5.95) * mm, "end": v(46.12, -5.93) * mm});
            skLineSegment(sketch, "E4445", {"start": v(46.12, -5.93) * mm, "end": v(45.96, -5.9) * mm});
            skLineSegment(sketch, "E4446", {"start": v(45.96, -5.9) * mm, "end": v(45.8, -5.89) * mm});
            skLineSegment(sketch, "E4447", {"start": v(45.8, -5.89) * mm, "end": v(45.62, -5.87) * mm});
            skLineSegment(sketch, "E4448", {"start": v(45.62, -5.87) * mm, "end": v(45.46, -5.85) * mm});
            skLineSegment(sketch, "E4449", {"start": v(45.46, -5.85) * mm, "end": v(45.3, -5.82) * mm});
            skLineSegment(sketch, "E4450", {"start": v(45.3, -5.82) * mm, "end": v(45.12, -5.8) * mm});
            skLineSegment(sketch, "E4451", {"start": v(45.12, -5.8) * mm, "end": v(44.96, -5.78) * mm});
            skLineSegment(sketch, "E4452", {"start": v(44.96, -5.78) * mm, "end": v(44.8, -5.76) * mm});
            skLineSegment(sketch, "E4453", {"start": v(44.8, -5.76) * mm, "end": v(44.62, -5.74) * mm});
            skLineSegment(sketch, "E4454", {"start": v(44.62, -5.74) * mm, "end": v(44.46, -5.72) * mm});
            skLineSegment(sketch, "E4455", {"start": v(44.46, -5.72) * mm, "end": v(44.34, -5.7) * mm});
            skLineSegment(sketch, "E4456", {"start": v(44.34, -5.7) * mm, "end": v(44.36, -5.54) * mm});
            skLineSegment(sketch, "E4457", {"start": v(44.36, -5.54) * mm, "end": v(44.37, -5.37) * mm});
            skLineSegment(sketch, "E4458", {"start": v(44.37, -5.37) * mm, "end": v(44.39, -5.2) * mm});
            skLineSegment(sketch, "E4459", {"start": v(44.39, -5.2) * mm, "end": v(44.4, -5.04) * mm});
            skLineSegment(sketch, "E4460", {"start": v(44.4, -5.04) * mm, "end": v(44.42, -4.88) * mm});
            skLineSegment(sketch, "E4461", {"start": v(44.42, -4.88) * mm, "end": v(44.44, -4.71) * mm});
            skLineSegment(sketch, "E4462", {"start": v(44.44, -4.71) * mm, "end": v(44.46, -4.55) * mm});
            skLineSegment(sketch, "E4463", {"start": v(44.46, -4.55) * mm, "end": v(44.48, -4.38) * mm});
            skLineSegment(sketch, "E4464", {"start": v(44.48, -4.38) * mm, "end": v(44.5, -4.21) * mm});
            skLineSegment(sketch, "E4465", {"start": v(44.5, -4.21) * mm, "end": v(44.51, -4.05) * mm});
            skLineSegment(sketch, "E4466", {"start": v(44.51, -4.05) * mm, "end": v(44.53, -3.88) * mm});
            skLineSegment(sketch, "E4467", {"start": v(44.53, -3.88) * mm, "end": v(44.54, -3.8) * mm});
            skLineSegment(sketch, "E4468", {"start": v(44.54, -3.8) * mm, "end": v(44.7, -3.82) * mm});
            skLineSegment(sketch, "E4469", {"start": v(44.7, -3.82) * mm, "end": v(44.87, -3.83) * mm});
            skLineSegment(sketch, "E4470", {"start": v(44.87, -3.83) * mm, "end": v(45.04, -3.85) * mm});
            skLineSegment(sketch, "E4471", {"start": v(45.04, -3.85) * mm, "end": v(45.2, -3.86) * mm});
            skLineSegment(sketch, "E4472", {"start": v(45.2, -3.86) * mm, "end": v(45.37, -3.87) * mm});
            skLineSegment(sketch, "E4473", {"start": v(45.37, -3.87) * mm, "end": v(45.54, -3.89) * mm});
            skLineSegment(sketch, "E4474", {"start": v(45.54, -3.89) * mm, "end": v(45.7, -3.9) * mm});
            skLineSegment(sketch, "E4475", {"start": v(45.7, -3.9) * mm, "end": v(45.87, -3.92) * mm});
            skLineSegment(sketch, "E4476", {"start": v(45.87, -3.92) * mm, "end": v(46.04, -3.93) * mm});
            skLineSegment(sketch, "E4477", {"start": v(46.04, -3.93) * mm, "end": v(46.2, -3.94) * mm});
            skLineSegment(sketch, "E4478", {"start": v(46.2, -3.94) * mm, "end": v(46.38, -3.96) * mm});
            skLineSegment(sketch, "E4479", {"start": v(46.38, -3.96) * mm, "end": v(46.55, -3.97) * mm});
            skLineSegment(sketch, "E4480", {"start": v(46.55, -3.97) * mm, "end": v(46.72, -3.99) * mm});
            skLineSegment(sketch, "E4481", {"start": v(46.72, -3.99) * mm, "end": v(46.9, -3.97) * mm});
            skLineSegment(sketch, "E4482", {"start": v(46.9, -3.97) * mm, "end": v(47.06, -3.9) * mm});
            skLineSegment(sketch, "E4483", {"start": v(47.06, -3.9) * mm, "end": v(47.2, -3.8) * mm});
            skLineSegment(sketch, "E4484", {"start": v(47.2, -3.8) * mm, "end": v(47.3, -3.67) * mm});
            skLineSegment(sketch, "E4485", {"start": v(47.3, -3.67) * mm, "end": v(47.38, -3.5) * mm});
            skLineSegment(sketch, "E4486", {"start": v(47.38, -3.5) * mm, "end": v(47.4, -3.34) * mm});
            skLineSegment(sketch, "E4487", {"start": v(47.4, -3.34) * mm, "end": v(47.38, -3.16) * mm});
            skLineSegment(sketch, "E4488", {"start": v(47.38, -3.16) * mm, "end": v(47.32, -3) * mm});
            skLineSegment(sketch, "E4489", {"start": v(47.32, -3) * mm, "end": v(47.21, -2.86) * mm});
            skLineSegment(sketch, "E4490", {"start": v(47.21, -2.86) * mm, "end": v(47.08, -2.75) * mm});
            skLineSegment(sketch, "E4491", {"start": v(47.08, -2.75) * mm, "end": v(46.92, -2.69) * mm});
            skLineSegment(sketch, "E4492", {"start": v(46.92, -2.69) * mm, "end": v(46.75, -2.66) * mm});
            skLineSegment(sketch, "E4493", {"start": v(46.75, -2.66) * mm, "end": v(46.59, -2.65) * mm});
            skLineSegment(sketch, "E4494", {"start": v(46.59, -2.65) * mm, "end": v(46.42, -2.64) * mm});
            skLineSegment(sketch, "E4495", {"start": v(46.42, -2.64) * mm, "end": v(46.26, -2.63) * mm});
            skLineSegment(sketch, "E4496", {"start": v(46.26, -2.63) * mm, "end": v(46.1, -2.62) * mm});
            skLineSegment(sketch, "E4497", {"start": v(46.1, -2.62) * mm, "end": v(45.92, -2.61) * mm});
            skLineSegment(sketch, "E4498", {"start": v(45.92, -2.61) * mm, "end": v(45.75, -2.6) * mm});
            skLineSegment(sketch, "E4499", {"start": v(45.75, -2.6) * mm, "end": v(45.59, -2.6) * mm});
            skLineSegment(sketch, "E4500", {"start": v(45.59, -2.6) * mm, "end": v(45.42, -2.59) * mm});
            skLineSegment(sketch, "E4501", {"start": v(45.42, -2.59) * mm, "end": v(45.25, -2.58) * mm});
            skLineSegment(sketch, "E4502", {"start": v(45.25, -2.58) * mm, "end": v(45.08, -2.57) * mm});
            skLineSegment(sketch, "E4503", {"start": v(45.08, -2.57) * mm, "end": v(44.91, -2.56) * mm});
            skLineSegment(sketch, "E4504", {"start": v(44.91, -2.56) * mm, "end": v(44.75, -2.55) * mm});
            skLineSegment(sketch, "E4505", {"start": v(44.75, -2.55) * mm, "end": v(44.63, -2.54) * mm});
            skLineSegment(sketch, "E4506", {"start": v(44.63, -2.54) * mm, "end": v(44.63, -2.38) * mm});
            skLineSegment(sketch, "E4507", {"start": v(44.63, -2.38) * mm, "end": v(44.64, -2.2) * mm});
            skLineSegment(sketch, "E4508", {"start": v(44.64, -2.2) * mm, "end": v(44.64, -2.04) * mm});
            skLineSegment(sketch, "E4509", {"start": v(44.64, -2.04) * mm, "end": v(44.65, -1.88) * mm});
            skLineSegment(sketch, "E4510", {"start": v(44.65, -1.88) * mm, "end": v(44.65, -1.71) * mm});
            skLineSegment(sketch, "E4511", {"start": v(44.65, -1.71) * mm, "end": v(44.66, -1.54) * mm});
            skLineSegment(sketch, "E4512", {"start": v(44.66, -1.54) * mm, "end": v(44.67, -1.38) * mm});
            skLineSegment(sketch, "E4513", {"start": v(44.67, -1.38) * mm, "end": v(44.67, -1.21) * mm});
            skLineSegment(sketch, "E4514", {"start": v(44.67, -1.21) * mm, "end": v(44.68, -1.05) * mm});
            skLineSegment(sketch, "E4515", {"start": v(44.68, -1.05) * mm, "end": v(44.68, -0.88) * mm});
            skLineSegment(sketch, "E4516", {"start": v(44.68, -0.88) * mm, "end": v(44.69, -0.71) * mm});
            skLineSegment(sketch, "E4517", {"start": v(44.69, -0.71) * mm, "end": v(44.7, -0.63) * mm});
            skLineSegment(sketch, "E4518", {"start": v(-5.64, 3.08) * mm, "end": v(-5.44, 3.38) * mm});
            skLineSegment(sketch, "E4519", {"start": v(-5.44, 3.38) * mm, "end": v(-5.22, 3.66) * mm});
            skLineSegment(sketch, "E4520", {"start": v(-5.22, 3.66) * mm, "end": v(-4.98, 3.94) * mm});
            skLineSegment(sketch, "E4521", {"start": v(-4.98, 3.94) * mm, "end": v(-4.73, 4.2) * mm});
            skLineSegment(sketch, "E4522", {"start": v(-4.73, 4.2) * mm, "end": v(-4.46, 4.43) * mm});
            skLineSegment(sketch, "E4523", {"start": v(-4.46, 4.43) * mm, "end": v(-4.17, 4.65) * mm});
            skLineSegment(sketch, "E4524", {"start": v(-4.17, 4.65) * mm, "end": v(-3.87, 4.85) * mm});
            skLineSegment(sketch, "E4525", {"start": v(-3.87, 4.85) * mm, "end": v(-3.56, 5.04) * mm});
            skLineSegment(sketch, "E4526", {"start": v(-3.56, 5.04) * mm, "end": v(-3.28, 5.18) * mm});
            skLineSegment(sketch, "E4527", {"start": v(-3.28, 5.18) * mm, "end": v(-3.39, 5.38) * mm});
            skLineSegment(sketch, "E4528", {"start": v(-3.39, 5.38) * mm, "end": v(-3.67, 5.94) * mm});
            skLineSegment(sketch, "E4529", {"start": v(-3.67, 5.94) * mm, "end": v(-3.94, 6.5) * mm});
            skLineSegment(sketch, "E4530", {"start": v(-3.94, 6.5) * mm, "end": v(-4.2, 7.07) * mm});
            skLineSegment(sketch, "E4531", {"start": v(-4.2, 7.07) * mm, "end": v(-4.45, 7.63) * mm});
            skLineSegment(sketch, "E4532", {"start": v(-4.45, 7.63) * mm, "end": v(-4.7, 8.2) * mm});
            skLineSegment(sketch, "E4533", {"start": v(-4.7, 8.2) * mm, "end": v(-4.93, 8.76) * mm});
            skLineSegment(sketch, "E4534", {"start": v(-4.93, 8.76) * mm, "end": v(-5.16, 9.33) * mm});
            skLineSegment(sketch, "E4535", {"start": v(-5.16, 9.33) * mm, "end": v(-5.38, 9.9) * mm});
            skLineSegment(sketch, "E4536", {"start": v(-5.38, 9.9) * mm, "end": v(-5.58, 10.47) * mm});
            skLineSegment(sketch, "E4537", {"start": v(-5.58, 10.47) * mm, "end": v(-5.78, 11.04) * mm});
            skLineSegment(sketch, "E4538", {"start": v(-5.78, 11.04) * mm, "end": v(-5.97, 11.6) * mm});
            skLineSegment(sketch, "E4539", {"start": v(-5.97, 11.6) * mm, "end": v(-6.15, 12.18) * mm});
            skLineSegment(sketch, "E4540", {"start": v(-6.15, 12.18) * mm, "end": v(-6.33, 12.75) * mm});
            skLineSegment(sketch, "E4541", {"start": v(-6.33, 12.75) * mm, "end": v(-6.49, 13.32) * mm});
            skLineSegment(sketch, "E4542", {"start": v(-6.49, 13.32) * mm, "end": v(-6.64, 13.89) * mm});
            skLineSegment(sketch, "E4543", {"start": v(-6.64, 13.89) * mm, "end": v(-6.79, 14.46) * mm});
            skLineSegment(sketch, "E4544", {"start": v(-6.79, 14.46) * mm, "end": v(-6.92, 15.03) * mm});
            skLineSegment(sketch, "E4545", {"start": v(-6.92, 15.03) * mm, "end": v(-7.05, 15.6) * mm});
            skLineSegment(sketch, "E4546", {"start": v(-7.05, 15.6) * mm, "end": v(-7.16, 16.18) * mm});
            skLineSegment(sketch, "E4547", {"start": v(-7.16, 16.18) * mm, "end": v(-7.27, 16.75) * mm});
            skLineSegment(sketch, "E4548", {"start": v(-7.27, 16.75) * mm, "end": v(-7.37, 17.33) * mm});
            skLineSegment(sketch, "E4549", {"start": v(-7.37, 17.33) * mm, "end": v(-7.46, 17.9) * mm});
            skLineSegment(sketch, "E4550", {"start": v(-7.46, 17.9) * mm, "end": v(-7.54, 18.48) * mm});
            skLineSegment(sketch, "E4551", {"start": v(-7.54, 18.48) * mm, "end": v(-7.6, 19.05) * mm});
            skLineSegment(sketch, "E4552", {"start": v(-7.6, 19.05) * mm, "end": v(-7.67, 19.63) * mm});
            skLineSegment(sketch, "E4553", {"start": v(-7.67, 19.63) * mm, "end": v(-7.72, 20.2) * mm});
            skLineSegment(sketch, "E4554", {"start": v(-7.72, 20.2) * mm, "end": v(-7.76, 20.79) * mm});
            skLineSegment(sketch, "E4555", {"start": v(-7.76, 20.79) * mm, "end": v(-7.8, 21.36) * mm});
            skLineSegment(sketch, "E4556", {"start": v(-7.8, 21.36) * mm, "end": v(-7.82, 21.94) * mm});
            skLineSegment(sketch, "E4557", {"start": v(-7.82, 21.94) * mm, "end": v(-7.83, 22.52) * mm});
            skLineSegment(sketch, "E4558", {"start": v(-7.83, 22.52) * mm, "end": v(-7.84, 23.1) * mm});
            skLineSegment(sketch, "E4559", {"start": v(-7.84, 23.1) * mm, "end": v(-7.83, 23.69) * mm});
            skLineSegment(sketch, "E4560", {"start": v(-7.83, 23.69) * mm, "end": v(-7.82, 24.28) * mm});
            skLineSegment(sketch, "E4561", {"start": v(-7.82, 24.28) * mm, "end": v(-7.8, 24.86) * mm});
            skLineSegment(sketch, "E4562", {"start": v(-7.8, 24.86) * mm, "end": v(-7.76, 25.45) * mm});
            skLineSegment(sketch, "E4563", {"start": v(-7.76, 25.45) * mm, "end": v(-7.72, 26.04) * mm});
            skLineSegment(sketch, "E4564", {"start": v(-7.72, 26.04) * mm, "end": v(-7.66, 26.62) * mm});
            skLineSegment(sketch, "E4565", {"start": v(-7.66, 26.62) * mm, "end": v(-7.6, 27.2) * mm});
            skLineSegment(sketch, "E4566", {"start": v(-7.6, 27.2) * mm, "end": v(-7.53, 27.8) * mm});
            skLineSegment(sketch, "E4567", {"start": v(-7.53, 27.8) * mm, "end": v(-7.45, 28.37) * mm});
            skLineSegment(sketch, "E4568", {"start": v(-7.45, 28.37) * mm, "end": v(-7.36, 28.96) * mm});
            skLineSegment(sketch, "E4569", {"start": v(-7.36, 28.96) * mm, "end": v(-7.25, 29.54) * mm});
            skLineSegment(sketch, "E4570", {"start": v(-7.25, 29.54) * mm, "end": v(-7.14, 30.12) * mm});
            skLineSegment(sketch, "E4571", {"start": v(-7.14, 30.12) * mm, "end": v(-7.02, 30.7) * mm});
            skLineSegment(sketch, "E4572", {"start": v(-7.02, 30.7) * mm, "end": v(-6.9, 31.29) * mm});
            skLineSegment(sketch, "E4573", {"start": v(-6.9, 31.29) * mm, "end": v(-6.76, 31.87) * mm});
            skLineSegment(sketch, "E4574", {"start": v(-6.76, 31.87) * mm, "end": v(-6.6, 32.45) * mm});
            skLineSegment(sketch, "E4575", {"start": v(-6.6, 32.45) * mm, "end": v(-6.45, 33.03) * mm});
            skLineSegment(sketch, "E4576", {"start": v(-6.45, 33.03) * mm, "end": v(-6.28, 33.6) * mm});
            skLineSegment(sketch, "E4577", {"start": v(-6.28, 33.6) * mm, "end": v(-6.1, 34.18) * mm});
            skLineSegment(sketch, "E4578", {"start": v(-6.1, 34.18) * mm, "end": v(-5.92, 34.76) * mm});
            skLineSegment(sketch, "E4579", {"start": v(-5.92, 34.76) * mm, "end": v(-5.72, 35.34) * mm});
            skLineSegment(sketch, "E4580", {"start": v(-5.72, 35.34) * mm, "end": v(-5.52, 35.91) * mm});
            skLineSegment(sketch, "E4581", {"start": v(-5.52, 35.91) * mm, "end": v(-5.3, 36.5) * mm});
            skLineSegment(sketch, "E4582", {"start": v(-5.3, 36.5) * mm, "end": v(-5.08, 37.07) * mm});
            skLineSegment(sketch, "E4583", {"start": v(-5.08, 37.07) * mm, "end": v(-4.85, 37.64) * mm});
            skLineSegment(sketch, "E4584", {"start": v(-4.85, 37.64) * mm, "end": v(-4.6, 38.21) * mm});
            skLineSegment(sketch, "E4585", {"start": v(-4.6, 38.21) * mm, "end": v(-4.36, 38.79) * mm});
            skLineSegment(sketch, "E4586", {"start": v(-4.36, 38.79) * mm, "end": v(-4.1, 39.36) * mm});
            skLineSegment(sketch, "E4587", {"start": v(-4.1, 39.36) * mm, "end": v(-3.83, 39.93) * mm});
            skLineSegment(sketch, "E4588", {"start": v(-3.83, 39.93) * mm, "end": v(-3.55, 40.5) * mm});
            skLineSegment(sketch, "E4589", {"start": v(-3.55, 40.5) * mm, "end": v(-3.37, 40.85) * mm});
            skLineSegment(sketch, "E4590", {"start": v(-3.37, 40.85) * mm, "end": v(-5.92, 40.61) * mm});
            skLineSegment(sketch, "E4591", {"start": v(-5.92, 40.61) * mm, "end": v(-8.46, 40.21) * mm});
            skLineSegment(sketch, "E4592", {"start": v(-8.46, 40.21) * mm, "end": v(-10.97, 39.65) * mm});
            skLineSegment(sketch, "E4593", {"start": v(-10.97, 39.65) * mm, "end": v(-13.44, 38.93) * mm});
            skLineSegment(sketch, "E4594", {"start": v(-13.44, 38.93) * mm, "end": v(-15.86, 38.06) * mm});
            skLineSegment(sketch, "E4595", {"start": v(-15.86, 38.06) * mm, "end": v(-18.22, 37.04) * mm});
            skLineSegment(sketch, "E4596", {"start": v(-18.22, 37.04) * mm, "end": v(-20.51, 35.87) * mm});
            skLineSegment(sketch, "E4597", {"start": v(-20.51, 35.87) * mm, "end": v(-22.73, 34.56) * mm});
            skLineSegment(sketch, "E4598", {"start": v(-22.73, 34.56) * mm, "end": v(-24.85, 33.12) * mm});
            skLineSegment(sketch, "E4599", {"start": v(-24.85, 33.12) * mm, "end": v(-26.88, 31.54) * mm});
            skLineSegment(sketch, "E4600", {"start": v(-26.88, 31.54) * mm, "end": v(-28.81, 29.84) * mm});
            skLineSegment(sketch, "E4601", {"start": v(-28.81, 29.84) * mm, "end": v(-30.63, 28.02) * mm});
            skLineSegment(sketch, "E4602", {"start": v(-30.63, 28.02) * mm, "end": v(-32.33, 26.1) * mm});
            skLineSegment(sketch, "E4603", {"start": v(-32.33, 26.1) * mm, "end": v(-33.9, 24.06) * mm});
            skLineSegment(sketch, "E4604", {"start": v(-33.9, 24.06) * mm, "end": v(-35.35, 21.93) * mm});
            skLineSegment(sketch, "E4605", {"start": v(-35.35, 21.93) * mm, "end": v(-36.66, 19.72) * mm});
            skLineSegment(sketch, "E4606", {"start": v(-36.66, 19.72) * mm, "end": v(-37.83, 17.43) * mm});
            skLineSegment(sketch, "E4607", {"start": v(-37.83, 17.43) * mm, "end": v(-38.85, 15.07) * mm});
            skLineSegment(sketch, "E4608", {"start": v(-38.85, 15.07) * mm, "end": v(-39.72, 12.65) * mm});
            skLineSegment(sketch, "E4609", {"start": v(-39.72, 12.65) * mm, "end": v(-40.44, 10.18) * mm});
            skLineSegment(sketch, "E4610", {"start": v(-40.44, 10.18) * mm, "end": v(-41, 7.67) * mm});
            skLineSegment(sketch, "E4611", {"start": v(-41, 7.67) * mm, "end": v(-41.4, 5.13) * mm});
            skLineSegment(sketch, "E4612", {"start": v(-41.4, 5.13) * mm, "end": v(-41.61, 2.92) * mm});
            skLineSegment(sketch, "E4613", {"start": v(-41.61, 2.92) * mm, "end": v(-41.3, 3.06) * mm});
            skLineSegment(sketch, "E4614", {"start": v(-41.3, 3.06) * mm, "end": v(-40.72, 3.3) * mm});
            skLineSegment(sketch, "E4615", {"start": v(-40.72, 3.3) * mm, "end": v(-40.15, 3.53) * mm});
            skLineSegment(sketch, "E4616", {"start": v(-40.15, 3.53) * mm, "end": v(-39.58, 3.76) * mm});
            skLineSegment(sketch, "E4617", {"start": v(-39.58, 3.76) * mm, "end": v(-39, 3.97) * mm});
            skLineSegment(sketch, "E4618", {"start": v(-39, 3.97) * mm, "end": v(-38.43, 4.18) * mm});
            skLineSegment(sketch, "E4619", {"start": v(-38.43, 4.18) * mm, "end": v(-37.86, 4.38) * mm});
            skLineSegment(sketch, "E4620", {"start": v(-37.86, 4.38) * mm, "end": v(-37.28, 4.57) * mm});
            skLineSegment(sketch, "E4621", {"start": v(-37.28, 4.57) * mm, "end": v(-36.7, 4.76) * mm});
            skLineSegment(sketch, "E4622", {"start": v(-36.7, 4.76) * mm, "end": v(-36.13, 4.93) * mm});
            skLineSegment(sketch, "E4623", {"start": v(-36.13, 4.93) * mm, "end": v(-35.55, 5.1) * mm});
            skLineSegment(sketch, "E4624", {"start": v(-35.55, 5.1) * mm, "end": v(-34.97, 5.26) * mm});
            skLineSegment(sketch, "E4625", {"start": v(-34.97, 5.26) * mm, "end": v(-34.4, 5.41) * mm});
            skLineSegment(sketch, "E4626", {"start": v(-34.4, 5.41) * mm, "end": v(-33.82, 5.56) * mm});
            skLineSegment(sketch, "E4627", {"start": v(-33.82, 5.56) * mm, "end": v(-33.24, 5.7) * mm});
            skLineSegment(sketch, "E4628", {"start": v(-33.24, 5.7) * mm, "end": v(-32.66, 5.82) * mm});
            skLineSegment(sketch, "E4629", {"start": v(-32.66, 5.82) * mm, "end": v(-32.08, 5.94) * mm});
            skLineSegment(sketch, "E4630", {"start": v(-32.08, 5.94) * mm, "end": v(-31.5, 6.05) * mm});
            skLineSegment(sketch, "E4631", {"start": v(-31.5, 6.05) * mm, "end": v(-30.91, 6.15) * mm});
            skLineSegment(sketch, "E4632", {"start": v(-30.91, 6.15) * mm, "end": v(-30.33, 6.25) * mm});
            skLineSegment(sketch, "E4633", {"start": v(-30.33, 6.25) * mm, "end": v(-29.75, 6.33) * mm});
            skLineSegment(sketch, "E4634", {"start": v(-29.75, 6.33) * mm, "end": v(-29.17, 6.41) * mm});
            skLineSegment(sketch, "E4635", {"start": v(-29.17, 6.41) * mm, "end": v(-28.58, 6.48) * mm});
            skLineSegment(sketch, "E4636", {"start": v(-28.58, 6.48) * mm, "end": v(-28, 6.54) * mm});
            skLineSegment(sketch, "E4637", {"start": v(-28, 6.54) * mm, "end": v(-27.41, 6.6) * mm});
            skLineSegment(sketch, "E4638", {"start": v(-27.41, 6.6) * mm, "end": v(-26.83, 6.64) * mm});
            skLineSegment(sketch, "E4639", {"start": v(-26.83, 6.64) * mm, "end": v(-26.24, 6.68) * mm});
            skLineSegment(sketch, "E4640", {"start": v(-26.24, 6.68) * mm, "end": v(-25.65, 6.71) * mm});
            skLineSegment(sketch, "E4641", {"start": v(-25.65, 6.71) * mm, "end": v(-25.07, 6.73) * mm});
            skLineSegment(sketch, "E4642", {"start": v(-25.07, 6.73) * mm, "end": v(-24.48, 6.74) * mm});
            skLineSegment(sketch, "E4643", {"start": v(-24.48, 6.74) * mm, "end": v(-23.9, 6.75) * mm});
            skLineSegment(sketch, "E4644", {"start": v(-23.9, 6.75) * mm, "end": v(-23.31, 6.74) * mm});
            skLineSegment(sketch, "E4645", {"start": v(-23.31, 6.74) * mm, "end": v(-22.73, 6.73) * mm});
            skLineSegment(sketch, "E4646", {"start": v(-22.73, 6.73) * mm, "end": v(-22.15, 6.71) * mm});
            skLineSegment(sketch, "E4647", {"start": v(-22.15, 6.71) * mm, "end": v(-21.58, 6.68) * mm});
            skLineSegment(sketch, "E4648", {"start": v(-21.58, 6.68) * mm, "end": v(-21, 6.65) * mm});
            skLineSegment(sketch, "E4649", {"start": v(-21, 6.65) * mm, "end": v(-20.42, 6.6) * mm});
            skLineSegment(sketch, "E4650", {"start": v(-20.42, 6.6) * mm, "end": v(-19.85, 6.55) * mm});
            skLineSegment(sketch, "E4651", {"start": v(-19.85, 6.55) * mm, "end": v(-19.27, 6.5) * mm});
            skLineSegment(sketch, "E4652", {"start": v(-19.27, 6.5) * mm, "end": v(-18.7, 6.42) * mm});
            skLineSegment(sketch, "E4653", {"start": v(-18.7, 6.42) * mm, "end": v(-18.12, 6.35) * mm});
            skLineSegment(sketch, "E4654", {"start": v(-18.12, 6.35) * mm, "end": v(-17.54, 6.26) * mm});
            skLineSegment(sketch, "E4655", {"start": v(-17.54, 6.26) * mm, "end": v(-16.97, 6.17) * mm});
            skLineSegment(sketch, "E4656", {"start": v(-16.97, 6.17) * mm, "end": v(-16.4, 6.07) * mm});
            skLineSegment(sketch, "E4657", {"start": v(-16.4, 6.07) * mm, "end": v(-15.82, 5.96) * mm});
            skLineSegment(sketch, "E4658", {"start": v(-15.82, 5.96) * mm, "end": v(-15.25, 5.84) * mm});
            skLineSegment(sketch, "E4659", {"start": v(-15.25, 5.84) * mm, "end": v(-14.68, 5.72) * mm});
            skLineSegment(sketch, "E4660", {"start": v(-14.68, 5.72) * mm, "end": v(-14.1, 5.59) * mm});
            skLineSegment(sketch, "E4661", {"start": v(-14.1, 5.59) * mm, "end": v(-13.54, 5.45) * mm});
            skLineSegment(sketch, "E4662", {"start": v(-13.54, 5.45) * mm, "end": v(-12.97, 5.3) * mm});
            skLineSegment(sketch, "E4663", {"start": v(-12.97, 5.3) * mm, "end": v(-12.4, 5.15) * mm});
            skLineSegment(sketch, "E4664", {"start": v(-12.4, 5.15) * mm, "end": v(-11.83, 4.98) * mm});
            skLineSegment(sketch, "E4665", {"start": v(-11.83, 4.98) * mm, "end": v(-11.26, 4.81) * mm});
            skLineSegment(sketch, "E4666", {"start": v(-11.26, 4.81) * mm, "end": v(-10.7, 4.63) * mm});
            skLineSegment(sketch, "E4667", {"start": v(-10.7, 4.63) * mm, "end": v(-10.12, 4.45) * mm});
            skLineSegment(sketch, "E4668", {"start": v(-10.12, 4.45) * mm, "end": v(-9.56, 4.25) * mm});
            skLineSegment(sketch, "E4669", {"start": v(-9.56, 4.25) * mm, "end": v(-8.99, 4.05) * mm});
            skLineSegment(sketch, "E4670", {"start": v(-8.99, 4.05) * mm, "end": v(-8.42, 3.84) * mm});
            skLineSegment(sketch, "E4671", {"start": v(-8.42, 3.84) * mm, "end": v(-7.86, 3.62) * mm});
            skLineSegment(sketch, "E4672", {"start": v(-7.86, 3.62) * mm, "end": v(-7.3, 3.4) * mm});
            skLineSegment(sketch, "E4673", {"start": v(-7.3, 3.4) * mm, "end": v(-6.73, 3.16) * mm});
            skLineSegment(sketch, "E4674", {"start": v(-6.73, 3.16) * mm, "end": v(-6.17, 2.92) * mm});
            skLineSegment(sketch, "E4675", {"start": v(-6.17, 2.92) * mm, "end": v(-5.83, 2.77) * mm});
            skLineSegment(sketch, "E4676", {"start": v(-5.83, 2.77) * mm, "end": v(-5.64, 3.08) * mm});
            skLineSegment(sketch, "E4677", {"start": v(4.58, 2.6) * mm, "end": v(5.15, 2.87) * mm});
            skLineSegment(sketch, "E4678", {"start": v(5.15, 2.87) * mm, "end": v(5.71, 3.15) * mm});
            skLineSegment(sketch, "E4679", {"start": v(5.71, 3.15) * mm, "end": v(6.28, 3.4) * mm});
            skLineSegment(sketch, "E4680", {"start": v(6.28, 3.4) * mm, "end": v(6.84, 3.66) * mm});
            skLineSegment(sketch, "E4681", {"start": v(6.84, 3.66) * mm, "end": v(7.4, 3.9) * mm});
            skLineSegment(sketch, "E4682", {"start": v(7.4, 3.9) * mm, "end": v(7.97, 4.14) * mm});
            skLineSegment(sketch, "E4683", {"start": v(7.97, 4.14) * mm, "end": v(8.54, 4.37) * mm});
            skLineSegment(sketch, "E4684", {"start": v(8.54, 4.37) * mm, "end": v(9.1, 4.58) * mm});
            skLineSegment(sketch, "E4685", {"start": v(9.1, 4.58) * mm, "end": v(9.68, 4.8) * mm});
            skLineSegment(sketch, "E4686", {"start": v(9.68, 4.8) * mm, "end": v(10.25, 5) * mm});
            skLineSegment(sketch, "E4687", {"start": v(10.25, 5) * mm, "end": v(10.81, 5.18) * mm});
            skLineSegment(sketch, "E4688", {"start": v(10.81, 5.18) * mm, "end": v(11.38, 5.36) * mm});
            skLineSegment(sketch, "E4689", {"start": v(11.38, 5.36) * mm, "end": v(11.95, 5.53) * mm});
            skLineSegment(sketch, "E4690", {"start": v(11.95, 5.53) * mm, "end": v(12.53, 5.7) * mm});
            skLineSegment(sketch, "E4691", {"start": v(12.53, 5.7) * mm, "end": v(13.1, 5.85) * mm});
            skLineSegment(sketch, "E4692", {"start": v(13.1, 5.85) * mm, "end": v(13.67, 6) * mm});
            skLineSegment(sketch, "E4693", {"start": v(13.67, 6) * mm, "end": v(14.24, 6.13) * mm});
            skLineSegment(sketch, "E4694", {"start": v(14.24, 6.13) * mm, "end": v(14.81, 6.26) * mm});
            skLineSegment(sketch, "E4695", {"start": v(14.81, 6.26) * mm, "end": v(15.39, 6.37) * mm});
            skLineSegment(sketch, "E4696", {"start": v(15.39, 6.37) * mm, "end": v(15.96, 6.48) * mm});
            skLineSegment(sketch, "E4697", {"start": v(15.96, 6.48) * mm, "end": v(16.54, 6.58) * mm});
            skLineSegment(sketch, "E4698", {"start": v(16.54, 6.58) * mm, "end": v(17.11, 6.67) * mm});
            skLineSegment(sketch, "E4699", {"start": v(17.11, 6.67) * mm, "end": v(17.69, 6.75) * mm});
            skLineSegment(sketch, "E4700", {"start": v(17.69, 6.75) * mm, "end": v(18.26, 6.82) * mm});
            skLineSegment(sketch, "E4701", {"start": v(18.26, 6.82) * mm, "end": v(18.84, 6.88) * mm});
            skLineSegment(sketch, "E4702", {"start": v(18.84, 6.88) * mm, "end": v(19.42, 6.93) * mm});
            skLineSegment(sketch, "E4703", {"start": v(19.42, 6.93) * mm, "end": v(20, 6.97) * mm});
            skLineSegment(sketch, "E4704", {"start": v(20, 6.97) * mm, "end": v(20.57, 7) * mm});
            skLineSegment(sketch, "E4705", {"start": v(20.57, 7) * mm, "end": v(21.15, 7.03) * mm});
            skLineSegment(sketch, "E4706", {"start": v(21.15, 7.03) * mm, "end": v(21.73, 7.04) * mm});
            skLineSegment(sketch, "E4707", {"start": v(21.73, 7.04) * mm, "end": v(22.31, 7.05) * mm});
            skLineSegment(sketch, "E4708", {"start": v(22.31, 7.05) * mm, "end": v(22.9, 7.04) * mm});
            skLineSegment(sketch, "E4709", {"start": v(22.9, 7.04) * mm, "end": v(23.49, 7.03) * mm});
            skLineSegment(sketch, "E4710", {"start": v(23.49, 7.03) * mm, "end": v(24.07, 7) * mm});
            skLineSegment(sketch, "E4711", {"start": v(24.07, 7) * mm, "end": v(24.66, 6.97) * mm});
            skLineSegment(sketch, "E4712", {"start": v(24.66, 6.97) * mm, "end": v(25.25, 6.93) * mm});
            skLineSegment(sketch, "E4713", {"start": v(25.25, 6.93) * mm, "end": v(25.83, 6.87) * mm});
            skLineSegment(sketch, "E4714", {"start": v(25.83, 6.87) * mm, "end": v(26.42, 6.81) * mm});
            skLineSegment(sketch, "E4715", {"start": v(26.42, 6.81) * mm, "end": v(27, 6.74) * mm});
            skLineSegment(sketch, "E4716", {"start": v(27, 6.74) * mm, "end": v(27.58, 6.66) * mm});
            skLineSegment(sketch, "E4717", {"start": v(27.58, 6.66) * mm, "end": v(28.17, 6.56) * mm});
            skLineSegment(sketch, "E4718", {"start": v(28.17, 6.56) * mm, "end": v(28.75, 6.46) * mm});
            skLineSegment(sketch, "E4719", {"start": v(28.75, 6.46) * mm, "end": v(29.33, 6.35) * mm});
            skLineSegment(sketch, "E4720", {"start": v(29.33, 6.35) * mm, "end": v(29.91, 6.23) * mm});
            skLineSegment(sketch, "E4721", {"start": v(29.91, 6.23) * mm, "end": v(30.5, 6.1) * mm});
            skLineSegment(sketch, "E4722", {"start": v(30.5, 6.1) * mm, "end": v(31.08, 5.97) * mm});
            skLineSegment(sketch, "E4723", {"start": v(31.08, 5.97) * mm, "end": v(31.66, 5.82) * mm});
            skLineSegment(sketch, "E4724", {"start": v(31.66, 5.82) * mm, "end": v(32.23, 5.66) * mm});
            skLineSegment(sketch, "E4725", {"start": v(32.23, 5.66) * mm, "end": v(32.81, 5.5) * mm});
            skLineSegment(sketch, "E4726", {"start": v(32.81, 5.5) * mm, "end": v(33.4, 5.31) * mm});
            skLineSegment(sketch, "E4727", {"start": v(33.4, 5.31) * mm, "end": v(33.97, 5.13) * mm});
            skLineSegment(sketch, "E4728", {"start": v(33.97, 5.13) * mm, "end": v(34.55, 4.93) * mm});
            skLineSegment(sketch, "E4729", {"start": v(34.55, 4.93) * mm, "end": v(35.12, 4.73) * mm});
            skLineSegment(sketch, "E4730", {"start": v(35.12, 4.73) * mm, "end": v(35.7, 4.51) * mm});
            skLineSegment(sketch, "E4731", {"start": v(35.7, 4.51) * mm, "end": v(36.27, 4.3) * mm});
            skLineSegment(sketch, "E4732", {"start": v(36.27, 4.3) * mm, "end": v(36.85, 4.06) * mm});
            skLineSegment(sketch, "E4733", {"start": v(36.85, 4.06) * mm, "end": v(37.42, 3.82) * mm});
            skLineSegment(sketch, "E4734", {"start": v(37.42, 3.82) * mm, "end": v(38, 3.57) * mm});
            skLineSegment(sketch, "E4735", {"start": v(38, 3.57) * mm, "end": v(38.57, 3.3) * mm});
            skLineSegment(sketch, "E4736", {"start": v(38.57, 3.3) * mm, "end": v(39.14, 3.03) * mm});
            skLineSegment(sketch, "E4737", {"start": v(39.14, 3.03) * mm, "end": v(39.72, 2.76) * mm});
            skLineSegment(sketch, "E4738", {"start": v(39.72, 2.76) * mm, "end": v(40.06, 2.58) * mm});
            skLineSegment(sketch, "E4739", {"start": v(40.06, 2.58) * mm, "end": v(39.82, 5.13) * mm});
            skLineSegment(sketch, "E4740", {"start": v(39.82, 5.13) * mm, "end": v(39.42, 7.67) * mm});
            skLineSegment(sketch, "E4741", {"start": v(39.42, 7.67) * mm, "end": v(38.86, 10.18) * mm});
            skLineSegment(sketch, "E4742", {"start": v(38.86, 10.18) * mm, "end": v(38.14, 12.65) * mm});
            skLineSegment(sketch, "E4743", {"start": v(38.14, 12.65) * mm, "end": v(37.27, 15.07) * mm});
            skLineSegment(sketch, "E4744", {"start": v(37.27, 15.07) * mm, "end": v(36.25, 17.43) * mm});
            skLineSegment(sketch, "E4745", {"start": v(36.25, 17.43) * mm, "end": v(35.08, 19.72) * mm});
            skLineSegment(sketch, "E4746", {"start": v(35.08, 19.72) * mm, "end": v(33.77, 21.93) * mm});
            skLineSegment(sketch, "E4747", {"start": v(33.77, 21.93) * mm, "end": v(32.33, 24.06) * mm});
            skLineSegment(sketch, "E4748", {"start": v(32.33, 24.06) * mm, "end": v(30.75, 26.1) * mm});
            skLineSegment(sketch, "E4749", {"start": v(30.75, 26.1) * mm, "end": v(29.05, 28.02) * mm});
            skLineSegment(sketch, "E4750", {"start": v(29.05, 28.02) * mm, "end": v(27.23, 29.84) * mm});
            skLineSegment(sketch, "E4751", {"start": v(27.23, 29.84) * mm, "end": v(25.3, 31.54) * mm});
            skLineSegment(sketch, "E4752", {"start": v(25.3, 31.54) * mm, "end": v(23.27, 33.12) * mm});
            skLineSegment(sketch, "E4753", {"start": v(23.27, 33.12) * mm, "end": v(21.14, 34.56) * mm});
            skLineSegment(sketch, "E4754", {"start": v(21.14, 34.56) * mm, "end": v(18.93, 35.87) * mm});
            skLineSegment(sketch, "E4755", {"start": v(18.93, 35.87) * mm, "end": v(16.64, 37.04) * mm});
            skLineSegment(sketch, "E4756", {"start": v(16.64, 37.04) * mm, "end": v(14.28, 38.06) * mm});
            skLineSegment(sketch, "E4757", {"start": v(14.28, 38.06) * mm, "end": v(11.86, 38.93) * mm});
            skLineSegment(sketch, "E4758", {"start": v(11.86, 38.93) * mm, "end": v(9.39, 39.65) * mm});
            skLineSegment(sketch, "E4759", {"start": v(9.39, 39.65) * mm, "end": v(6.88, 40.21) * mm});
            skLineSegment(sketch, "E4760", {"start": v(6.88, 40.21) * mm, "end": v(4.34, 40.61) * mm});
            skLineSegment(sketch, "E4761", {"start": v(4.34, 40.61) * mm, "end": v(2.13, 40.82) * mm});
            skLineSegment(sketch, "E4762", {"start": v(2.13, 40.82) * mm, "end": v(2.27, 40.5) * mm});
            skLineSegment(sketch, "E4763", {"start": v(2.27, 40.5) * mm, "end": v(2.5, 39.93) * mm});
            skLineSegment(sketch, "E4764", {"start": v(2.5, 39.93) * mm, "end": v(2.74, 39.36) * mm});
            skLineSegment(sketch, "E4765", {"start": v(2.74, 39.36) * mm, "end": v(2.97, 38.79) * mm});
            skLineSegment(sketch, "E4766", {"start": v(2.97, 38.79) * mm, "end": v(3.18, 38.21) * mm});
            skLineSegment(sketch, "E4767", {"start": v(3.18, 38.21) * mm, "end": v(3.39, 37.64) * mm});
            skLineSegment(sketch, "E4768", {"start": v(3.39, 37.64) * mm, "end": v(3.59, 37.07) * mm});
            skLineSegment(sketch, "E4769", {"start": v(3.59, 37.07) * mm, "end": v(3.78, 36.5) * mm});
            skLineSegment(sketch, "E4770", {"start": v(3.78, 36.5) * mm, "end": v(3.97, 35.91) * mm});
            skLineSegment(sketch, "E4771", {"start": v(3.97, 35.91) * mm, "end": v(4.14, 35.34) * mm});
            skLineSegment(sketch, "E4772", {"start": v(4.14, 35.34) * mm, "end": v(4.3, 34.76) * mm});
            skLineSegment(sketch, "E4773", {"start": v(4.3, 34.76) * mm, "end": v(4.47, 34.18) * mm});
            skLineSegment(sketch, "E4774", {"start": v(4.47, 34.18) * mm, "end": v(4.62, 33.6) * mm});
            skLineSegment(sketch, "E4775", {"start": v(4.62, 33.6) * mm, "end": v(4.76, 33.03) * mm});
            skLineSegment(sketch, "E4776", {"start": v(4.76, 33.03) * mm, "end": v(4.9, 32.45) * mm});
            skLineSegment(sketch, "E4777", {"start": v(4.9, 32.45) * mm, "end": v(5.03, 31.87) * mm});
            skLineSegment(sketch, "E4778", {"start": v(5.03, 31.87) * mm, "end": v(5.15, 31.29) * mm});
            skLineSegment(sketch, "E4779", {"start": v(5.15, 31.29) * mm, "end": v(5.26, 30.7) * mm});
            skLineSegment(sketch, "E4780", {"start": v(5.26, 30.7) * mm, "end": v(5.36, 30.12) * mm});
            skLineSegment(sketch, "E4781", {"start": v(5.36, 30.12) * mm, "end": v(5.46, 29.54) * mm});
            skLineSegment(sketch, "E4782", {"start": v(5.46, 29.54) * mm, "end": v(5.54, 28.96) * mm});
            skLineSegment(sketch, "E4783", {"start": v(5.54, 28.96) * mm, "end": v(5.62, 28.37) * mm});
            skLineSegment(sketch, "E4784", {"start": v(5.62, 28.37) * mm, "end": v(5.7, 27.8) * mm});
            skLineSegment(sketch, "E4785", {"start": v(5.7, 27.8) * mm, "end": v(5.75, 27.2) * mm});
            skLineSegment(sketch, "E4786", {"start": v(5.75, 27.2) * mm, "end": v(5.8, 26.62) * mm});
            skLineSegment(sketch, "E4787", {"start": v(5.8, 26.62) * mm, "end": v(5.85, 26.04) * mm});
            skLineSegment(sketch, "E4788", {"start": v(5.85, 26.04) * mm, "end": v(5.9, 25.45) * mm});
            skLineSegment(sketch, "E4789", {"start": v(5.9, 25.45) * mm, "end": v(5.92, 24.86) * mm});
            skLineSegment(sketch, "E4790", {"start": v(5.92, 24.86) * mm, "end": v(5.94, 24.28) * mm});
            skLineSegment(sketch, "E4791", {"start": v(5.94, 24.28) * mm, "end": v(5.95, 23.69) * mm});
            skLineSegment(sketch, "E4792", {"start": v(5.95, 23.69) * mm, "end": v(5.96, 23.1) * mm});
            skLineSegment(sketch, "E4793", {"start": v(5.96, 23.1) * mm, "end": v(5.95, 22.52) * mm});
            skLineSegment(sketch, "E4794", {"start": v(5.95, 22.52) * mm, "end": v(5.94, 21.94) * mm});
            skLineSegment(sketch, "E4795", {"start": v(5.94, 21.94) * mm, "end": v(5.92, 21.36) * mm});
            skLineSegment(sketch, "E4796", {"start": v(5.92, 21.36) * mm, "end": v(5.9, 20.79) * mm});
            skLineSegment(sketch, "E4797", {"start": v(5.9, 20.79) * mm, "end": v(5.86, 20.2) * mm});
            skLineSegment(sketch, "E4798", {"start": v(5.86, 20.2) * mm, "end": v(5.81, 19.63) * mm});
            skLineSegment(sketch, "E4799", {"start": v(5.81, 19.63) * mm, "end": v(5.76, 19.05) * mm});
            skLineSegment(sketch, "E4800", {"start": v(5.76, 19.05) * mm, "end": v(5.7, 18.48) * mm});
            skLineSegment(sketch, "E4801", {"start": v(5.7, 18.48) * mm, "end": v(5.63, 17.9) * mm});
            skLineSegment(sketch, "E4802", {"start": v(5.63, 17.9) * mm, "end": v(5.55, 17.33) * mm});
            skLineSegment(sketch, "E4803", {"start": v(5.55, 17.33) * mm, "end": v(5.47, 16.75) * mm});
            skLineSegment(sketch, "E4804", {"start": v(5.47, 16.75) * mm, "end": v(5.38, 16.18) * mm});
            skLineSegment(sketch, "E4805", {"start": v(5.38, 16.18) * mm, "end": v(5.28, 15.6) * mm});
            skLineSegment(sketch, "E4806", {"start": v(5.28, 15.6) * mm, "end": v(5.17, 15.03) * mm});
            skLineSegment(sketch, "E4807", {"start": v(5.17, 15.03) * mm, "end": v(5.05, 14.46) * mm});
            skLineSegment(sketch, "E4808", {"start": v(5.05, 14.46) * mm, "end": v(4.93, 13.89) * mm});
            skLineSegment(sketch, "E4809", {"start": v(4.93, 13.89) * mm, "end": v(4.8, 13.32) * mm});
            skLineSegment(sketch, "E4810", {"start": v(4.8, 13.32) * mm, "end": v(4.66, 12.75) * mm});
            skLineSegment(sketch, "E4811", {"start": v(4.66, 12.75) * mm, "end": v(4.51, 12.18) * mm});
            skLineSegment(sketch, "E4812", {"start": v(4.51, 12.18) * mm, "end": v(4.35, 11.6) * mm});
            skLineSegment(sketch, "E4813", {"start": v(4.35, 11.6) * mm, "end": v(4.2, 11.04) * mm});
            skLineSegment(sketch, "E4814", {"start": v(4.2, 11.04) * mm, "end": v(4.02, 10.47) * mm});
            skLineSegment(sketch, "E4815", {"start": v(4.02, 10.47) * mm, "end": v(3.84, 9.9) * mm});
            skLineSegment(sketch, "E4816", {"start": v(3.84, 9.9) * mm, "end": v(3.65, 9.33) * mm});
            skLineSegment(sketch, "E4817", {"start": v(3.65, 9.33) * mm, "end": v(3.46, 8.76) * mm});
            skLineSegment(sketch, "E4818", {"start": v(3.46, 8.76) * mm, "end": v(3.26, 8.2) * mm});
            skLineSegment(sketch, "E4819", {"start": v(3.26, 8.2) * mm, "end": v(3.05, 7.63) * mm});
            skLineSegment(sketch, "E4820", {"start": v(3.05, 7.63) * mm, "end": v(2.83, 7.07) * mm});
            skLineSegment(sketch, "E4821", {"start": v(2.83, 7.07) * mm, "end": v(2.6, 6.5) * mm});
            skLineSegment(sketch, "E4822", {"start": v(2.6, 6.5) * mm, "end": v(2.37, 5.94) * mm});
            skLineSegment(sketch, "E4823", {"start": v(2.37, 5.94) * mm, "end": v(2.13, 5.38) * mm});
            skLineSegment(sketch, "E4824", {"start": v(2.13, 5.38) * mm, "end": v(1.98, 5.04) * mm});
            skLineSegment(sketch, "E4825", {"start": v(1.98, 5.04) * mm, "end": v(2.29, 4.85) * mm});
            skLineSegment(sketch, "E4826", {"start": v(2.29, 4.85) * mm, "end": v(2.59, 4.65) * mm});
            skLineSegment(sketch, "E4827", {"start": v(2.59, 4.65) * mm, "end": v(2.87, 4.43) * mm});
            skLineSegment(sketch, "E4828", {"start": v(2.87, 4.43) * mm, "end": v(3.14, 4.2) * mm});
            skLineSegment(sketch, "E4829", {"start": v(3.14, 4.2) * mm, "end": v(3.4, 3.94) * mm});
            skLineSegment(sketch, "E4830", {"start": v(3.4, 3.94) * mm, "end": v(3.64, 3.66) * mm});
            skLineSegment(sketch, "E4831", {"start": v(3.64, 3.66) * mm, "end": v(3.86, 3.38) * mm});
            skLineSegment(sketch, "E4832", {"start": v(3.86, 3.38) * mm, "end": v(4.06, 3.08) * mm});
            skLineSegment(sketch, "E4833", {"start": v(4.06, 3.08) * mm, "end": v(4.25, 2.77) * mm});
            skLineSegment(sketch, "E4834", {"start": v(4.25, 2.77) * mm, "end": v(4.39, 2.5) * mm});
            skLineSegment(sketch, "E4835", {"start": v(4.39, 2.5) * mm, "end": v(4.58, 2.6) * mm});
            skLineSegment(sketch, "E4836", {"start": v(0.15, 14.08) * mm, "end": v(0.28, 14.38) * mm});
            skLineSegment(sketch, "E4837", {"start": v(0.28, 14.38) * mm, "end": v(0.4, 14.68) * mm});
            skLineSegment(sketch, "E4838", {"start": v(0.4, 14.68) * mm, "end": v(0.53, 14.98) * mm});
            skLineSegment(sketch, "E4839", {"start": v(0.53, 14.98) * mm, "end": v(0.66, 15.29) * mm});
            skLineSegment(sketch, "E4840", {"start": v(0.66, 15.29) * mm, "end": v(0.77, 15.59) * mm});
            skLineSegment(sketch, "E4841", {"start": v(0.77, 15.59) * mm, "end": v(0.88, 15.89) * mm});
            skLineSegment(sketch, "E4842", {"start": v(0.88, 15.89) * mm, "end": v(0.99, 16.2) * mm});
            skLineSegment(sketch, "E4843", {"start": v(0.99, 16.2) * mm, "end": v(1.1, 16.5) * mm});
            skLineSegment(sketch, "E4844", {"start": v(1.1, 16.5) * mm, "end": v(1.2, 16.8) * mm});
            skLineSegment(sketch, "E4845", {"start": v(1.2, 16.8) * mm, "end": v(1.28, 17.1) * mm});
            skLineSegment(sketch, "E4846", {"start": v(1.28, 17.1) * mm, "end": v(1.37, 17.4) * mm});
            skLineSegment(sketch, "E4847", {"start": v(1.37, 17.4) * mm, "end": v(1.46, 17.7) * mm});
            skLineSegment(sketch, "E4848", {"start": v(1.46, 17.7) * mm, "end": v(1.54, 18.01) * mm});
            skLineSegment(sketch, "E4849", {"start": v(1.54, 18.01) * mm, "end": v(1.61, 18.32) * mm});
            skLineSegment(sketch, "E4850", {"start": v(1.61, 18.32) * mm, "end": v(1.68, 18.62) * mm});
            skLineSegment(sketch, "E4851", {"start": v(1.68, 18.62) * mm, "end": v(1.75, 18.92) * mm});
            skLineSegment(sketch, "E4852", {"start": v(1.75, 18.92) * mm, "end": v(1.81, 19.23) * mm});
            skLineSegment(sketch, "E4853", {"start": v(1.81, 19.23) * mm, "end": v(1.87, 19.53) * mm});
            skLineSegment(sketch, "E4854", {"start": v(1.87, 19.53) * mm, "end": v(1.92, 19.84) * mm});
            skLineSegment(sketch, "E4855", {"start": v(1.92, 19.84) * mm, "end": v(1.97, 20.14) * mm});
            skLineSegment(sketch, "E4856", {"start": v(1.97, 20.14) * mm, "end": v(2.01, 20.45) * mm});
            skLineSegment(sketch, "E4857", {"start": v(2.01, 20.45) * mm, "end": v(2.05, 20.75) * mm});
            skLineSegment(sketch, "E4858", {"start": v(2.05, 20.75) * mm, "end": v(2.09, 21.06) * mm});
            skLineSegment(sketch, "E4859", {"start": v(2.09, 21.06) * mm, "end": v(2.12, 21.36) * mm});
            skLineSegment(sketch, "E4860", {"start": v(2.12, 21.36) * mm, "end": v(2.14, 21.67) * mm});
            skLineSegment(sketch, "E4861", {"start": v(2.14, 21.67) * mm, "end": v(2.16, 21.98) * mm});
            skLineSegment(sketch, "E4862", {"start": v(2.16, 21.98) * mm, "end": v(2.18, 22.28) * mm});
            skLineSegment(sketch, "E4863", {"start": v(2.18, 22.28) * mm, "end": v(2.2, 22.6) * mm});
            skLineSegment(sketch, "E4864", {"start": v(2.2, 22.6) * mm, "end": v(2.2, 22.9) * mm});
            skLineSegment(sketch, "E4865", {"start": v(2.2, 22.9) * mm, "end": v(2.2, 23.2) * mm});
            skLineSegment(sketch, "E4866", {"start": v(2.2, 23.2) * mm, "end": v(2.2, 23.52) * mm});
            skLineSegment(sketch, "E4867", {"start": v(2.2, 23.52) * mm, "end": v(2.2, 23.83) * mm});
            skLineSegment(sketch, "E4868", {"start": v(2.2, 23.83) * mm, "end": v(2.18, 24.14) * mm});
            skLineSegment(sketch, "E4869", {"start": v(2.18, 24.14) * mm, "end": v(2.16, 24.45) * mm});
            skLineSegment(sketch, "E4870", {"start": v(2.16, 24.45) * mm, "end": v(2.14, 24.76) * mm});
            skLineSegment(sketch, "E4871", {"start": v(2.14, 24.76) * mm, "end": v(2.12, 25.07) * mm});
            skLineSegment(sketch, "E4872", {"start": v(2.12, 25.07) * mm, "end": v(2.08, 25.38) * mm});
            skLineSegment(sketch, "E4873", {"start": v(2.08, 25.38) * mm, "end": v(2.05, 25.7) * mm});
            skLineSegment(sketch, "E4874", {"start": v(2.05, 25.7) * mm, "end": v(2, 26) * mm});
            skLineSegment(sketch, "E4875", {"start": v(2, 26) * mm, "end": v(1.96, 26.31) * mm});
            skLineSegment(sketch, "E4876", {"start": v(1.96, 26.31) * mm, "end": v(1.91, 26.62) * mm});
            skLineSegment(sketch, "E4877", {"start": v(1.91, 26.62) * mm, "end": v(1.86, 26.93) * mm});
            skLineSegment(sketch, "E4878", {"start": v(1.86, 26.93) * mm, "end": v(1.8, 27.24) * mm});
            skLineSegment(sketch, "E4879", {"start": v(1.8, 27.24) * mm, "end": v(1.74, 27.55) * mm});
            skLineSegment(sketch, "E4880", {"start": v(1.74, 27.55) * mm, "end": v(1.67, 27.86) * mm});
            skLineSegment(sketch, "E4881", {"start": v(1.67, 27.86) * mm, "end": v(1.6, 28.17) * mm});
            skLineSegment(sketch, "E4882", {"start": v(1.6, 28.17) * mm, "end": v(1.52, 28.47) * mm});
            skLineSegment(sketch, "E4883", {"start": v(1.52, 28.47) * mm, "end": v(1.44, 28.78) * mm});
            skLineSegment(sketch, "E4884", {"start": v(1.44, 28.78) * mm, "end": v(1.35, 29.09) * mm});
            skLineSegment(sketch, "E4885", {"start": v(1.35, 29.09) * mm, "end": v(1.26, 29.4) * mm});
            skLineSegment(sketch, "E4886", {"start": v(1.26, 29.4) * mm, "end": v(1.16, 29.7) * mm});
            skLineSegment(sketch, "E4887", {"start": v(1.16, 29.7) * mm, "end": v(1.06, 30.01) * mm});
            skLineSegment(sketch, "E4888", {"start": v(1.06, 30.01) * mm, "end": v(0.96, 30.32) * mm});
            skLineSegment(sketch, "E4889", {"start": v(0.96, 30.32) * mm, "end": v(0.85, 30.63) * mm});
            skLineSegment(sketch, "E4890", {"start": v(0.85, 30.63) * mm, "end": v(0.73, 30.93) * mm});
            skLineSegment(sketch, "E4891", {"start": v(0.73, 30.93) * mm, "end": v(0.61, 31.24) * mm});
            skLineSegment(sketch, "E4892", {"start": v(0.61, 31.24) * mm, "end": v(0.49, 31.54) * mm});
            skLineSegment(sketch, "E4893", {"start": v(0.49, 31.54) * mm, "end": v(0.36, 31.85) * mm});
            skLineSegment(sketch, "E4894", {"start": v(0.36, 31.85) * mm, "end": v(0.22, 32.16) * mm});
            skLineSegment(sketch, "E4895", {"start": v(0.22, 32.16) * mm, "end": v(0.09, 32.46) * mm});
            skLineSegment(sketch, "E4896", {"start": v(0.09, 32.46) * mm, "end": v(0.07, 32.5) * mm});
            skLineSegment(sketch, "E4897", {"start": v(0.07, 32.5) * mm, "end": v(-1.42, 32.5) * mm});
            skLineSegment(sketch, "E4898", {"start": v(-1.42, 32.5) * mm, "end": v(-1.47, 32.41) * mm});
            skLineSegment(sketch, "E4899", {"start": v(-1.47, 32.41) * mm, "end": v(-1.63, 32.1) * mm});
            skLineSegment(sketch, "E4900", {"start": v(-1.63, 32.1) * mm, "end": v(-1.78, 31.8) * mm});
            skLineSegment(sketch, "E4901", {"start": v(-1.78, 31.8) * mm, "end": v(-1.93, 31.5) * mm});
            skLineSegment(sketch, "E4902", {"start": v(-1.93, 31.5) * mm, "end": v(-2.07, 31.2) * mm});
            skLineSegment(sketch, "E4903", {"start": v(-2.07, 31.2) * mm, "end": v(-2.21, 30.89) * mm});
            skLineSegment(sketch, "E4904", {"start": v(-2.21, 30.89) * mm, "end": v(-2.34, 30.58) * mm});
            skLineSegment(sketch, "E4905", {"start": v(-2.34, 30.58) * mm, "end": v(-2.47, 30.27) * mm});
            skLineSegment(sketch, "E4906", {"start": v(-2.47, 30.27) * mm, "end": v(-2.6, 29.97) * mm});
            skLineSegment(sketch, "E4907", {"start": v(-2.6, 29.97) * mm, "end": v(-2.71, 29.66) * mm});
            skLineSegment(sketch, "E4908", {"start": v(-2.71, 29.66) * mm, "end": v(-2.82, 29.36) * mm});
            skLineSegment(sketch, "E4909", {"start": v(-2.82, 29.36) * mm, "end": v(-2.93, 29.05) * mm});
            skLineSegment(sketch, "E4910", {"start": v(-2.93, 29.05) * mm, "end": v(-3.03, 28.74) * mm});
            skLineSegment(sketch, "E4911", {"start": v(-3.03, 28.74) * mm, "end": v(-3.12, 28.44) * mm});
            skLineSegment(sketch, "E4912", {"start": v(-3.12, 28.44) * mm, "end": v(-3.21, 28.13) * mm});
            skLineSegment(sketch, "E4913", {"start": v(-3.21, 28.13) * mm, "end": v(-3.3, 27.83) * mm});
            skLineSegment(sketch, "E4914", {"start": v(-3.3, 27.83) * mm, "end": v(-3.38, 27.52) * mm});
            skLineSegment(sketch, "E4915", {"start": v(-3.38, 27.52) * mm, "end": v(-3.45, 27.21) * mm});
            skLineSegment(sketch, "E4916", {"start": v(-3.45, 27.21) * mm, "end": v(-3.52, 26.9) * mm});
            skLineSegment(sketch, "E4917", {"start": v(-3.52, 26.9) * mm, "end": v(-3.58, 26.6) * mm});
            skLineSegment(sketch, "E4918", {"start": v(-3.58, 26.6) * mm, "end": v(-3.64, 26.3) * mm});
            skLineSegment(sketch, "E4919", {"start": v(-3.64, 26.3) * mm, "end": v(-3.7, 25.98) * mm});
            skLineSegment(sketch, "E4920", {"start": v(-3.7, 25.98) * mm, "end": v(-3.74, 25.68) * mm});
            skLineSegment(sketch, "E4921", {"start": v(-3.74, 25.68) * mm, "end": v(-3.78, 25.37) * mm});
            skLineSegment(sketch, "E4922", {"start": v(-3.78, 25.37) * mm, "end": v(-3.81, 25.06) * mm});
            skLineSegment(sketch, "E4923", {"start": v(-3.81, 25.06) * mm, "end": v(-3.84, 24.75) * mm});
            skLineSegment(sketch, "E4924", {"start": v(-3.84, 24.75) * mm, "end": v(-3.87, 24.44) * mm});
            skLineSegment(sketch, "E4925", {"start": v(-3.87, 24.44) * mm, "end": v(-3.89, 24.13) * mm});
            skLineSegment(sketch, "E4926", {"start": v(-3.89, 24.13) * mm, "end": v(-3.9, 23.82) * mm});
            skLineSegment(sketch, "E4927", {"start": v(-3.9, 23.82) * mm, "end": v(-3.91, 23.52) * mm});
            skLineSegment(sketch, "E4928", {"start": v(-3.91, 23.52) * mm, "end": v(-3.91, 23.2) * mm});
            skLineSegment(sketch, "E4929", {"start": v(-3.91, 23.2) * mm, "end": v(-3.91, 22.9) * mm});
            skLineSegment(sketch, "E4930", {"start": v(-3.91, 22.9) * mm, "end": v(-3.9, 22.6) * mm});
            skLineSegment(sketch, "E4931", {"start": v(-3.9, 22.6) * mm, "end": v(-3.89, 22.3) * mm});
            skLineSegment(sketch, "E4932", {"start": v(-3.89, 22.3) * mm, "end": v(-3.87, 21.99) * mm});
            skLineSegment(sketch, "E4933", {"start": v(-3.87, 21.99) * mm, "end": v(-3.85, 21.68) * mm});
            skLineSegment(sketch, "E4934", {"start": v(-3.85, 21.68) * mm, "end": v(-3.82, 21.38) * mm});
            skLineSegment(sketch, "E4935", {"start": v(-3.82, 21.38) * mm, "end": v(-3.78, 21.07) * mm});
            skLineSegment(sketch, "E4936", {"start": v(-3.78, 21.07) * mm, "end": v(-3.74, 20.77) * mm});
            skLineSegment(sketch, "E4937", {"start": v(-3.74, 20.77) * mm, "end": v(-3.7, 20.47) * mm});
            skLineSegment(sketch, "E4938", {"start": v(-3.7, 20.47) * mm, "end": v(-3.65, 20.16) * mm});
            skLineSegment(sketch, "E4939", {"start": v(-3.65, 20.16) * mm, "end": v(-3.6, 19.86) * mm});
            skLineSegment(sketch, "E4940", {"start": v(-3.6, 19.86) * mm, "end": v(-3.53, 19.56) * mm});
            skLineSegment(sketch, "E4941", {"start": v(-3.53, 19.56) * mm, "end": v(-3.46, 19.26) * mm});
            skLineSegment(sketch, "E4942", {"start": v(-3.46, 19.26) * mm, "end": v(-3.4, 18.95) * mm});
            skLineSegment(sketch, "E4943", {"start": v(-3.4, 18.95) * mm, "end": v(-3.32, 18.65) * mm});
            skLineSegment(sketch, "E4944", {"start": v(-3.32, 18.65) * mm, "end": v(-3.23, 18.35) * mm});
            skLineSegment(sketch, "E4945", {"start": v(-3.23, 18.35) * mm, "end": v(-3.15, 18.05) * mm});
            skLineSegment(sketch, "E4946", {"start": v(-3.15, 18.05) * mm, "end": v(-3.05, 17.74) * mm});
            skLineSegment(sketch, "E4947", {"start": v(-3.05, 17.74) * mm, "end": v(-2.96, 17.44) * mm});
            skLineSegment(sketch, "E4948", {"start": v(-2.96, 17.44) * mm, "end": v(-2.85, 17.14) * mm});
            skLineSegment(sketch, "E4949", {"start": v(-2.85, 17.14) * mm, "end": v(-2.74, 16.84) * mm});
            skLineSegment(sketch, "E4950", {"start": v(-2.74, 16.84) * mm, "end": v(-2.63, 16.54) * mm});
            skLineSegment(sketch, "E4951", {"start": v(-2.63, 16.54) * mm, "end": v(-2.51, 16.24) * mm});
            skLineSegment(sketch, "E4952", {"start": v(-2.51, 16.24) * mm, "end": v(-2.39, 15.93) * mm});
            skLineSegment(sketch, "E4953", {"start": v(-2.39, 15.93) * mm, "end": v(-2.26, 15.63) * mm});
            skLineSegment(sketch, "E4954", {"start": v(-2.26, 15.63) * mm, "end": v(-2.12, 15.33) * mm});
            skLineSegment(sketch, "E4955", {"start": v(-2.12, 15.33) * mm, "end": v(-1.98, 15.03) * mm});
            skLineSegment(sketch, "E4956", {"start": v(-1.98, 15.03) * mm, "end": v(-1.84, 14.73) * mm});
            skLineSegment(sketch, "E4957", {"start": v(-1.84, 14.73) * mm, "end": v(-1.69, 14.43) * mm});
            skLineSegment(sketch, "E4958", {"start": v(-1.69, 14.43) * mm, "end": v(-1.53, 14.13) * mm});
            skLineSegment(sketch, "E4959", {"start": v(-1.53, 14.13) * mm, "end": v(-1.5, 14.05) * mm});
            skLineSegment(sketch, "E4960", {"start": v(-1.5, 14.05) * mm, "end": v(0.13, 14.05) * mm});
            skLineSegment(sketch, "E4961", {"start": v(0.13, 14.05) * mm, "end": v(0.15, 14.08) * mm});
            skLineSegment(sketch, "E4962", {"start": v(22.73, -2.99) * mm, "end": v(23.04, -2.98) * mm});
            skLineSegment(sketch, "E4963", {"start": v(23.04, -2.98) * mm, "end": v(23.35, -2.97) * mm});
            skLineSegment(sketch, "E4964", {"start": v(23.35, -2.97) * mm, "end": v(23.66, -2.95) * mm});
            skLineSegment(sketch, "E4965", {"start": v(23.66, -2.95) * mm, "end": v(23.97, -2.93) * mm});
            skLineSegment(sketch, "E4966", {"start": v(23.97, -2.93) * mm, "end": v(24.28, -2.9) * mm});
            skLineSegment(sketch, "E4967", {"start": v(24.28, -2.9) * mm, "end": v(24.6, -2.88) * mm});
            skLineSegment(sketch, "E4968", {"start": v(24.6, -2.88) * mm, "end": v(24.9, -2.84) * mm});
            skLineSegment(sketch, "E4969", {"start": v(24.9, -2.84) * mm, "end": v(25.21, -2.8) * mm});
            skLineSegment(sketch, "E4970", {"start": v(25.21, -2.8) * mm, "end": v(25.52, -2.75) * mm});
            skLineSegment(sketch, "E4971", {"start": v(25.52, -2.75) * mm, "end": v(25.83, -2.7) * mm});
            skLineSegment(sketch, "E4972", {"start": v(25.83, -2.7) * mm, "end": v(26.14, -2.65) * mm});
            skLineSegment(sketch, "E4973", {"start": v(26.14, -2.65) * mm, "end": v(26.45, -2.6) * mm});
            skLineSegment(sketch, "E4974", {"start": v(26.45, -2.6) * mm, "end": v(26.76, -2.53) * mm});
            skLineSegment(sketch, "E4975", {"start": v(26.76, -2.53) * mm, "end": v(27.07, -2.46) * mm});
            skLineSegment(sketch, "E4976", {"start": v(27.07, -2.46) * mm, "end": v(27.37, -2.39) * mm});
            skLineSegment(sketch, "E4977", {"start": v(27.37, -2.39) * mm, "end": v(27.68, -2.3) * mm});
            skLineSegment(sketch, "E4978", {"start": v(27.68, -2.3) * mm, "end": v(28, -2.23) * mm});
            skLineSegment(sketch, "E4979", {"start": v(28, -2.23) * mm, "end": v(28.3, -2.14) * mm});
            skLineSegment(sketch, "E4980", {"start": v(28.3, -2.14) * mm, "end": v(28.6, -2.05) * mm});
            skLineSegment(sketch, "E4981", {"start": v(28.6, -2.05) * mm, "end": v(28.91, -1.95) * mm});
            skLineSegment(sketch, "E4982", {"start": v(28.91, -1.95) * mm, "end": v(29.22, -1.85) * mm});
            skLineSegment(sketch, "E4983", {"start": v(29.22, -1.85) * mm, "end": v(29.53, -1.75) * mm});
            skLineSegment(sketch, "E4984", {"start": v(29.53, -1.75) * mm, "end": v(29.83, -1.64) * mm});
            skLineSegment(sketch, "E4985", {"start": v(29.83, -1.64) * mm, "end": v(30.14, -1.52) * mm});
            skLineSegment(sketch, "E4986", {"start": v(30.14, -1.52) * mm, "end": v(30.45, -1.4) * mm});
            skLineSegment(sketch, "E4987", {"start": v(30.45, -1.4) * mm, "end": v(30.75, -1.28) * mm});
            skLineSegment(sketch, "E4988", {"start": v(30.75, -1.28) * mm, "end": v(31.06, -1.15) * mm});
            skLineSegment(sketch, "E4989", {"start": v(31.06, -1.15) * mm, "end": v(31.37, -1.02) * mm});
            skLineSegment(sketch, "E4990", {"start": v(31.37, -1.02) * mm, "end": v(31.67, -0.88) * mm});
            skLineSegment(sketch, "E4991", {"start": v(31.67, -0.88) * mm, "end": v(31.7, -0.86) * mm});
            skLineSegment(sketch, "E4992", {"start": v(31.7, -0.86) * mm, "end": v(31.7, 0.63) * mm});
            skLineSegment(sketch, "E4993", {"start": v(31.7, 0.63) * mm, "end": v(31.62, 0.67) * mm});
            skLineSegment(sketch, "E4994", {"start": v(31.62, 0.67) * mm, "end": v(31.32, 0.83) * mm});
            skLineSegment(sketch, "E4995", {"start": v(31.32, 0.83) * mm, "end": v(31.01, 0.99) * mm});
            skLineSegment(sketch, "E4996", {"start": v(31.01, 0.99) * mm, "end": v(30.7, 1.14) * mm});
            skLineSegment(sketch, "E4997", {"start": v(30.7, 1.14) * mm, "end": v(30.4, 1.28) * mm});
            skLineSegment(sketch, "E4998", {"start": v(30.4, 1.28) * mm, "end": v(30.1, 1.42) * mm});
            skLineSegment(sketch, "E4999", {"start": v(30.1, 1.42) * mm, "end": v(29.79, 1.55) * mm});
            skLineSegment(sketch, "E5000", {"start": v(29.79, 1.55) * mm, "end": v(29.48, 1.68) * mm});
            skLineSegment(sketch, "E5001", {"start": v(29.48, 1.68) * mm, "end": v(29.18, 1.8) * mm});
            skLineSegment(sketch, "E5002", {"start": v(29.18, 1.8) * mm, "end": v(28.87, 1.92) * mm});
            skLineSegment(sketch, "E5003", {"start": v(28.87, 1.92) * mm, "end": v(28.57, 2.03) * mm});
            skLineSegment(sketch, "E5004", {"start": v(28.57, 2.03) * mm, "end": v(28.26, 2.14) * mm});
            skLineSegment(sketch, "E5005", {"start": v(28.26, 2.14) * mm, "end": v(27.95, 2.24) * mm});
            skLineSegment(sketch, "E5006", {"start": v(27.95, 2.24) * mm, "end": v(27.65, 2.33) * mm});
            skLineSegment(sketch, "E5007", {"start": v(27.65, 2.33) * mm, "end": v(27.34, 2.42) * mm});
            skLineSegment(sketch, "E5008", {"start": v(27.34, 2.42) * mm, "end": v(27.03, 2.5) * mm});
            skLineSegment(sketch, "E5009", {"start": v(27.03, 2.5) * mm, "end": v(26.73, 2.59) * mm});
            skLineSegment(sketch, "E5010", {"start": v(26.73, 2.59) * mm, "end": v(26.42, 2.66) * mm});
            skLineSegment(sketch, "E5011", {"start": v(26.42, 2.66) * mm, "end": v(26.11, 2.73) * mm});
            skLineSegment(sketch, "E5012", {"start": v(26.11, 2.73) * mm, "end": v(25.8, 2.8) * mm});
            skLineSegment(sketch, "E5013", {"start": v(25.8, 2.8) * mm, "end": v(25.5, 2.85) * mm});
            skLineSegment(sketch, "E5014", {"start": v(25.5, 2.85) * mm, "end": v(25.2, 2.9) * mm});
            skLineSegment(sketch, "E5015", {"start": v(25.2, 2.9) * mm, "end": v(24.88, 2.95) * mm});
            skLineSegment(sketch, "E5016", {"start": v(24.88, 2.95) * mm, "end": v(24.58, 2.99) * mm});
            skLineSegment(sketch, "E5017", {"start": v(24.58, 2.99) * mm, "end": v(24.27, 3.02) * mm});
            skLineSegment(sketch, "E5018", {"start": v(24.27, 3.02) * mm, "end": v(23.96, 3.05) * mm});
            skLineSegment(sketch, "E5019", {"start": v(23.96, 3.05) * mm, "end": v(23.65, 3.08) * mm});
            skLineSegment(sketch, "E5020", {"start": v(23.65, 3.08) * mm, "end": v(23.34, 3.1) * mm});
            skLineSegment(sketch, "E5021", {"start": v(23.34, 3.1) * mm, "end": v(23.03, 3.11) * mm});
            skLineSegment(sketch, "E5022", {"start": v(23.03, 3.11) * mm, "end": v(22.72, 3.12) * mm});
            skLineSegment(sketch, "E5023", {"start": v(22.72, 3.12) * mm, "end": v(22.41, 3.12) * mm});
            skLineSegment(sketch, "E5024", {"start": v(22.41, 3.12) * mm, "end": v(22.1, 3.12) * mm});
            skLineSegment(sketch, "E5025", {"start": v(22.1, 3.12) * mm, "end": v(21.8, 3.11) * mm});
            skLineSegment(sketch, "E5026", {"start": v(21.8, 3.11) * mm, "end": v(21.5, 3.1) * mm});
            skLineSegment(sketch, "E5027", {"start": v(21.5, 3.1) * mm, "end": v(21.2, 3.08) * mm});
            skLineSegment(sketch, "E5028", {"start": v(21.2, 3.08) * mm, "end": v(20.9, 3.06) * mm});
            skLineSegment(sketch, "E5029", {"start": v(20.9, 3.06) * mm, "end": v(20.59, 3.03) * mm});
            skLineSegment(sketch, "E5030", {"start": v(20.59, 3.03) * mm, "end": v(20.28, 3) * mm});
            skLineSegment(sketch, "E5031", {"start": v(20.28, 3) * mm, "end": v(19.98, 2.95) * mm});
            skLineSegment(sketch, "E5032", {"start": v(19.98, 2.95) * mm, "end": v(19.68, 2.9) * mm});
            skLineSegment(sketch, "E5033", {"start": v(19.68, 2.9) * mm, "end": v(19.37, 2.86) * mm});
            skLineSegment(sketch, "E5034", {"start": v(19.37, 2.86) * mm, "end": v(19.07, 2.8) * mm});
            skLineSegment(sketch, "E5035", {"start": v(19.07, 2.8) * mm, "end": v(18.77, 2.74) * mm});
            skLineSegment(sketch, "E5036", {"start": v(18.77, 2.74) * mm, "end": v(18.46, 2.67) * mm});
            skLineSegment(sketch, "E5037", {"start": v(18.46, 2.67) * mm, "end": v(18.16, 2.6) * mm});
            skLineSegment(sketch, "E5038", {"start": v(18.16, 2.6) * mm, "end": v(17.86, 2.53) * mm});
            skLineSegment(sketch, "E5039", {"start": v(17.86, 2.53) * mm, "end": v(17.56, 2.44) * mm});
            skLineSegment(sketch, "E5040", {"start": v(17.56, 2.44) * mm, "end": v(17.26, 2.36) * mm});
            skLineSegment(sketch, "E5041", {"start": v(17.26, 2.36) * mm, "end": v(16.95, 2.26) * mm});
            skLineSegment(sketch, "E5042", {"start": v(16.95, 2.26) * mm, "end": v(16.65, 2.17) * mm});
            skLineSegment(sketch, "E5043", {"start": v(16.65, 2.17) * mm, "end": v(16.35, 2.06) * mm});
            skLineSegment(sketch, "E5044", {"start": v(16.35, 2.06) * mm, "end": v(16.05, 1.95) * mm});
            skLineSegment(sketch, "E5045", {"start": v(16.05, 1.95) * mm, "end": v(15.75, 1.84) * mm});
            skLineSegment(sketch, "E5046", {"start": v(15.75, 1.84) * mm, "end": v(15.44, 1.72) * mm});
            skLineSegment(sketch, "E5047", {"start": v(15.44, 1.72) * mm, "end": v(15.14, 1.6) * mm});
            skLineSegment(sketch, "E5048", {"start": v(15.14, 1.6) * mm, "end": v(14.84, 1.47) * mm});
            skLineSegment(sketch, "E5049", {"start": v(14.84, 1.47) * mm, "end": v(14.54, 1.33) * mm});
            skLineSegment(sketch, "E5050", {"start": v(14.54, 1.33) * mm, "end": v(14.24, 1.2) * mm});
            skLineSegment(sketch, "E5051", {"start": v(14.24, 1.2) * mm, "end": v(13.94, 1.05) * mm});
            skLineSegment(sketch, "E5052", {"start": v(13.94, 1.05) * mm, "end": v(13.64, 0.9) * mm});
            skLineSegment(sketch, "E5053", {"start": v(13.64, 0.9) * mm, "end": v(13.34, 0.74) * mm});
            skLineSegment(sketch, "E5054", {"start": v(13.34, 0.74) * mm, "end": v(13.26, 0.7) * mm});
            skLineSegment(sketch, "E5055", {"start": v(13.26, 0.7) * mm, "end": v(13.26, -0.93) * mm});
            skLineSegment(sketch, "E5056", {"start": v(13.26, -0.93) * mm, "end": v(13.29, -0.94) * mm});
            skLineSegment(sketch, "E5057", {"start": v(13.29, -0.94) * mm, "end": v(13.59, -1.07) * mm});
            skLineSegment(sketch, "E5058", {"start": v(13.59, -1.07) * mm, "end": v(13.9, -1.2) * mm});
            skLineSegment(sketch, "E5059", {"start": v(13.9, -1.2) * mm, "end": v(14.2, -1.33) * mm});
            skLineSegment(sketch, "E5060", {"start": v(14.2, -1.33) * mm, "end": v(14.5, -1.45) * mm});
            skLineSegment(sketch, "E5061", {"start": v(14.5, -1.45) * mm, "end": v(14.8, -1.56) * mm});
            skLineSegment(sketch, "E5062", {"start": v(14.8, -1.56) * mm, "end": v(15.1, -1.67) * mm});
            skLineSegment(sketch, "E5063", {"start": v(15.1, -1.67) * mm, "end": v(15.4, -1.78) * mm});
            skLineSegment(sketch, "E5064", {"start": v(15.4, -1.78) * mm, "end": v(15.7, -1.88) * mm});
            skLineSegment(sketch, "E5065", {"start": v(15.7, -1.88) * mm, "end": v(16, -1.98) * mm});
            skLineSegment(sketch, "E5066", {"start": v(16, -1.98) * mm, "end": v(16.31, -2.08) * mm});
            skLineSegment(sketch, "E5067", {"start": v(16.31, -2.08) * mm, "end": v(16.61, -2.16) * mm});
            skLineSegment(sketch, "E5068", {"start": v(16.61, -2.16) * mm, "end": v(16.92, -2.25) * mm});
            skLineSegment(sketch, "E5069", {"start": v(16.92, -2.25) * mm, "end": v(17.22, -2.33) * mm});
            skLineSegment(sketch, "E5070", {"start": v(17.22, -2.33) * mm, "end": v(17.52, -2.4) * mm});
            skLineSegment(sketch, "E5071", {"start": v(17.52, -2.4) * mm, "end": v(17.83, -2.47) * mm});
            skLineSegment(sketch, "E5072", {"start": v(17.83, -2.47) * mm, "end": v(18.13, -2.54) * mm});
            skLineSegment(sketch, "E5073", {"start": v(18.13, -2.54) * mm, "end": v(18.44, -2.6) * mm});
            skLineSegment(sketch, "E5074", {"start": v(18.44, -2.6) * mm, "end": v(18.74, -2.66) * mm});
            skLineSegment(sketch, "E5075", {"start": v(18.74, -2.66) * mm, "end": v(19.05, -2.71) * mm});
            skLineSegment(sketch, "E5076", {"start": v(19.05, -2.71) * mm, "end": v(19.35, -2.76) * mm});
            skLineSegment(sketch, "E5077", {"start": v(19.35, -2.76) * mm, "end": v(19.66, -2.8) * mm});
            skLineSegment(sketch, "E5078", {"start": v(19.66, -2.8) * mm, "end": v(19.96, -2.84) * mm});
            skLineSegment(sketch, "E5079", {"start": v(19.96, -2.84) * mm, "end": v(20.27, -2.88) * mm});
            skLineSegment(sketch, "E5080", {"start": v(20.27, -2.88) * mm, "end": v(20.57, -2.9) * mm});
            skLineSegment(sketch, "E5081", {"start": v(20.57, -2.9) * mm, "end": v(20.88, -2.93) * mm});
            skLineSegment(sketch, "E5082", {"start": v(20.88, -2.93) * mm, "end": v(21.19, -2.95) * mm});
            skLineSegment(sketch, "E5083", {"start": v(21.19, -2.95) * mm, "end": v(21.5, -2.97) * mm});
            skLineSegment(sketch, "E5084", {"start": v(21.5, -2.97) * mm, "end": v(21.8, -2.98) * mm});
            skLineSegment(sketch, "E5085", {"start": v(21.8, -2.98) * mm, "end": v(22.1, -2.99) * mm});
            skLineSegment(sketch, "E5086", {"start": v(22.1, -2.99) * mm, "end": v(22.41, -3) * mm});
            skLineSegment(sketch, "E5087", {"start": v(22.41, -3) * mm, "end": v(22.73, -2.99) * mm});
            skLineSegment(sketch, "E5088", {"start": v(-23.7, -3.12) * mm, "end": v(-23.39, -3.11) * mm});
            skLineSegment(sketch, "E5089", {"start": v(-23.39, -3.11) * mm, "end": v(-23.08, -3.1) * mm});
            skLineSegment(sketch, "E5090", {"start": v(-23.08, -3.1) * mm, "end": v(-22.78, -3.08) * mm});
            skLineSegment(sketch, "E5091", {"start": v(-22.78, -3.08) * mm, "end": v(-22.47, -3.06) * mm});
            skLineSegment(sketch, "E5092", {"start": v(-22.47, -3.06) * mm, "end": v(-22.17, -3.03) * mm});
            skLineSegment(sketch, "E5093", {"start": v(-22.17, -3.03) * mm, "end": v(-21.87, -3) * mm});
            skLineSegment(sketch, "E5094", {"start": v(-21.87, -3) * mm, "end": v(-21.56, -2.95) * mm});
            skLineSegment(sketch, "E5095", {"start": v(-21.56, -2.95) * mm, "end": v(-21.26, -2.9) * mm});
            skLineSegment(sketch, "E5096", {"start": v(-21.26, -2.9) * mm, "end": v(-20.96, -2.86) * mm});
            skLineSegment(sketch, "E5097", {"start": v(-20.96, -2.86) * mm, "end": v(-20.65, -2.8) * mm});
            skLineSegment(sketch, "E5098", {"start": v(-20.65, -2.8) * mm, "end": v(-20.35, -2.74) * mm});
            skLineSegment(sketch, "E5099", {"start": v(-20.35, -2.74) * mm, "end": v(-20.05, -2.67) * mm});
            skLineSegment(sketch, "E5100", {"start": v(-20.05, -2.67) * mm, "end": v(-19.74, -2.6) * mm});
            skLineSegment(sketch, "E5101", {"start": v(-19.74, -2.6) * mm, "end": v(-19.44, -2.53) * mm});
            skLineSegment(sketch, "E5102", {"start": v(-19.44, -2.53) * mm, "end": v(-19.14, -2.44) * mm});
            skLineSegment(sketch, "E5103", {"start": v(-19.14, -2.44) * mm, "end": v(-18.84, -2.36) * mm});
            skLineSegment(sketch, "E5104", {"start": v(-18.84, -2.36) * mm, "end": v(-18.54, -2.26) * mm});
            skLineSegment(sketch, "E5105", {"start": v(-18.54, -2.26) * mm, "end": v(-18.23, -2.17) * mm});
            skLineSegment(sketch, "E5106", {"start": v(-18.23, -2.17) * mm, "end": v(-17.93, -2.06) * mm});
            skLineSegment(sketch, "E5107", {"start": v(-17.93, -2.06) * mm, "end": v(-17.63, -1.95) * mm});
            skLineSegment(sketch, "E5108", {"start": v(-17.63, -1.95) * mm, "end": v(-17.33, -1.84) * mm});
            skLineSegment(sketch, "E5109", {"start": v(-17.33, -1.84) * mm, "end": v(-17.03, -1.72) * mm});
            skLineSegment(sketch, "E5110", {"start": v(-17.03, -1.72) * mm, "end": v(-16.73, -1.6) * mm});
            skLineSegment(sketch, "E5111", {"start": v(-16.73, -1.6) * mm, "end": v(-16.42, -1.47) * mm});
            skLineSegment(sketch, "E5112", {"start": v(-16.42, -1.47) * mm, "end": v(-16.12, -1.33) * mm});
            skLineSegment(sketch, "E5113", {"start": v(-16.12, -1.33) * mm, "end": v(-15.82, -1.2) * mm});
            skLineSegment(sketch, "E5114", {"start": v(-15.82, -1.2) * mm, "end": v(-15.52, -1.05) * mm});
            skLineSegment(sketch, "E5115", {"start": v(-15.52, -1.05) * mm, "end": v(-15.22, -0.9) * mm});
            skLineSegment(sketch, "E5116", {"start": v(-15.22, -0.9) * mm, "end": v(-14.92, -0.74) * mm});
            skLineSegment(sketch, "E5117", {"start": v(-14.92, -0.74) * mm, "end": v(-14.85, -0.7) * mm});
            skLineSegment(sketch, "E5118", {"start": v(-14.85, -0.7) * mm, "end": v(-14.85, 0.93) * mm});
            skLineSegment(sketch, "E5119", {"start": v(-14.85, 0.93) * mm, "end": v(-14.87, 0.94) * mm});
            skLineSegment(sketch, "E5120", {"start": v(-14.87, 0.94) * mm, "end": v(-15.17, 1.07) * mm});
            skLineSegment(sketch, "E5121", {"start": v(-15.17, 1.07) * mm, "end": v(-15.47, 1.2) * mm});
            skLineSegment(sketch, "E5122", {"start": v(-15.47, 1.2) * mm, "end": v(-15.77, 1.33) * mm});
            skLineSegment(sketch, "E5123", {"start": v(-15.77, 1.33) * mm, "end": v(-16.08, 1.45) * mm});
            skLineSegment(sketch, "E5124", {"start": v(-16.08, 1.45) * mm, "end": v(-16.38, 1.56) * mm});
            skLineSegment(sketch, "E5125", {"start": v(-16.38, 1.56) * mm, "end": v(-16.68, 1.67) * mm});
            skLineSegment(sketch, "E5126", {"start": v(-16.68, 1.67) * mm, "end": v(-16.98, 1.78) * mm});
            skLineSegment(sketch, "E5127", {"start": v(-16.98, 1.78) * mm, "end": v(-17.29, 1.88) * mm});
            skLineSegment(sketch, "E5128", {"start": v(-17.29, 1.88) * mm, "end": v(-17.59, 1.98) * mm});
            skLineSegment(sketch, "E5129", {"start": v(-17.59, 1.98) * mm, "end": v(-17.9, 2.08) * mm});
            skLineSegment(sketch, "E5130", {"start": v(-17.9, 2.08) * mm, "end": v(-18.2, 2.16) * mm});
            skLineSegment(sketch, "E5131", {"start": v(-18.2, 2.16) * mm, "end": v(-18.5, 2.25) * mm});
            skLineSegment(sketch, "E5132", {"start": v(-18.5, 2.25) * mm, "end": v(-18.8, 2.33) * mm});
            skLineSegment(sketch, "E5133", {"start": v(-18.8, 2.33) * mm, "end": v(-19.1, 2.4) * mm});
            skLineSegment(sketch, "E5134", {"start": v(-19.1, 2.4) * mm, "end": v(-19.41, 2.47) * mm});
            skLineSegment(sketch, "E5135", {"start": v(-19.41, 2.47) * mm, "end": v(-19.71, 2.54) * mm});
            skLineSegment(sketch, "E5136", {"start": v(-19.71, 2.54) * mm, "end": v(-20.02, 2.6) * mm});
            skLineSegment(sketch, "E5137", {"start": v(-20.02, 2.6) * mm, "end": v(-20.32, 2.66) * mm});
            skLineSegment(sketch, "E5138", {"start": v(-20.32, 2.66) * mm, "end": v(-20.63, 2.71) * mm});
            skLineSegment(sketch, "E5139", {"start": v(-20.63, 2.71) * mm, "end": v(-20.93, 2.76) * mm});
            skLineSegment(sketch, "E5140", {"start": v(-20.93, 2.76) * mm, "end": v(-21.24, 2.8) * mm});
            skLineSegment(sketch, "E5141", {"start": v(-21.24, 2.8) * mm, "end": v(-21.54, 2.84) * mm});
            skLineSegment(sketch, "E5142", {"start": v(-21.54, 2.84) * mm, "end": v(-21.85, 2.88) * mm});
            skLineSegment(sketch, "E5143", {"start": v(-21.85, 2.88) * mm, "end": v(-22.16, 2.9) * mm});
            skLineSegment(sketch, "E5144", {"start": v(-22.16, 2.9) * mm, "end": v(-22.46, 2.93) * mm});
            skLineSegment(sketch, "E5145", {"start": v(-22.46, 2.93) * mm, "end": v(-22.77, 2.95) * mm});
            skLineSegment(sketch, "E5146", {"start": v(-22.77, 2.95) * mm, "end": v(-23.08, 2.97) * mm});
            skLineSegment(sketch, "E5147", {"start": v(-23.08, 2.97) * mm, "end": v(-23.38, 2.98) * mm});
            skLineSegment(sketch, "E5148", {"start": v(-23.38, 2.98) * mm, "end": v(-23.69, 2.99) * mm});
            skLineSegment(sketch, "E5149", {"start": v(-23.69, 2.99) * mm, "end": v(-24, 3) * mm});
            skLineSegment(sketch, "E5150", {"start": v(-24, 3) * mm, "end": v(-24.3, 2.99) * mm});
            skLineSegment(sketch, "E5151", {"start": v(-24.3, 2.99) * mm, "end": v(-24.62, 2.98) * mm});
            skLineSegment(sketch, "E5152", {"start": v(-24.62, 2.98) * mm, "end": v(-24.93, 2.97) * mm});
            skLineSegment(sketch, "E5153", {"start": v(-24.93, 2.97) * mm, "end": v(-25.24, 2.95) * mm});
            skLineSegment(sketch, "E5154", {"start": v(-25.24, 2.95) * mm, "end": v(-25.55, 2.93) * mm});
            skLineSegment(sketch, "E5155", {"start": v(-25.55, 2.93) * mm, "end": v(-25.86, 2.9) * mm});
            skLineSegment(sketch, "E5156", {"start": v(-25.86, 2.9) * mm, "end": v(-26.17, 2.88) * mm});
            skLineSegment(sketch, "E5157", {"start": v(-26.17, 2.88) * mm, "end": v(-26.48, 2.84) * mm});
            skLineSegment(sketch, "E5158", {"start": v(-26.48, 2.84) * mm, "end": v(-26.8, 2.8) * mm});
            skLineSegment(sketch, "E5159", {"start": v(-26.8, 2.8) * mm, "end": v(-27.1, 2.75) * mm});
            skLineSegment(sketch, "E5160", {"start": v(-27.1, 2.75) * mm, "end": v(-27.41, 2.7) * mm});
            skLineSegment(sketch, "E5161", {"start": v(-27.41, 2.7) * mm, "end": v(-27.72, 2.65) * mm});
            skLineSegment(sketch, "E5162", {"start": v(-27.72, 2.65) * mm, "end": v(-28.03, 2.6) * mm});
            skLineSegment(sketch, "E5163", {"start": v(-28.03, 2.6) * mm, "end": v(-28.34, 2.53) * mm});
            skLineSegment(sketch, "E5164", {"start": v(-28.34, 2.53) * mm, "end": v(-28.65, 2.46) * mm});
            skLineSegment(sketch, "E5165", {"start": v(-28.65, 2.46) * mm, "end": v(-28.96, 2.39) * mm});
            skLineSegment(sketch, "E5166", {"start": v(-28.96, 2.39) * mm, "end": v(-29.26, 2.3) * mm});
            skLineSegment(sketch, "E5167", {"start": v(-29.26, 2.3) * mm, "end": v(-29.57, 2.23) * mm});
            skLineSegment(sketch, "E5168", {"start": v(-29.57, 2.23) * mm, "end": v(-29.88, 2.14) * mm});
            skLineSegment(sketch, "E5169", {"start": v(-29.88, 2.14) * mm, "end": v(-30.19, 2.05) * mm});
            skLineSegment(sketch, "E5170", {"start": v(-30.19, 2.05) * mm, "end": v(-30.5, 1.95) * mm});
            skLineSegment(sketch, "E5171", {"start": v(-30.5, 1.95) * mm, "end": v(-30.8, 1.85) * mm});
            skLineSegment(sketch, "E5172", {"start": v(-30.8, 1.85) * mm, "end": v(-31.1, 1.75) * mm});
            skLineSegment(sketch, "E5173", {"start": v(-31.1, 1.75) * mm, "end": v(-31.42, 1.64) * mm});
            skLineSegment(sketch, "E5174", {"start": v(-31.42, 1.64) * mm, "end": v(-31.72, 1.52) * mm});
            skLineSegment(sketch, "E5175", {"start": v(-31.72, 1.52) * mm, "end": v(-32.03, 1.4) * mm});
            skLineSegment(sketch, "E5176", {"start": v(-32.03, 1.4) * mm, "end": v(-32.34, 1.28) * mm});
            skLineSegment(sketch, "E5177", {"start": v(-32.34, 1.28) * mm, "end": v(-32.64, 1.15) * mm});
            skLineSegment(sketch, "E5178", {"start": v(-32.64, 1.15) * mm, "end": v(-32.95, 1.02) * mm});
            skLineSegment(sketch, "E5179", {"start": v(-32.95, 1.02) * mm, "end": v(-33.25, 0.88) * mm});
            skLineSegment(sketch, "E5180", {"start": v(-33.25, 0.88) * mm, "end": v(-33.3, 0.86) * mm});
            skLineSegment(sketch, "E5181", {"start": v(-33.3, 0.86) * mm, "end": v(-33.3, -0.63) * mm});
            skLineSegment(sketch, "E5182", {"start": v(-33.3, -0.63) * mm, "end": v(-33.2, -0.67) * mm});
            skLineSegment(sketch, "E5183", {"start": v(-33.2, -0.67) * mm, "end": v(-32.9, -0.83) * mm});
            skLineSegment(sketch, "E5184", {"start": v(-32.9, -0.83) * mm, "end": v(-32.6, -0.99) * mm});
            skLineSegment(sketch, "E5185", {"start": v(-32.6, -0.99) * mm, "end": v(-32.29, -1.14) * mm});
            skLineSegment(sketch, "E5186", {"start": v(-32.29, -1.14) * mm, "end": v(-31.98, -1.28) * mm});
            skLineSegment(sketch, "E5187", {"start": v(-31.98, -1.28) * mm, "end": v(-31.68, -1.42) * mm});
            skLineSegment(sketch, "E5188", {"start": v(-31.68, -1.42) * mm, "end": v(-31.37, -1.55) * mm});
            skLineSegment(sketch, "E5189", {"start": v(-31.37, -1.55) * mm, "end": v(-31.07, -1.68) * mm});
            skLineSegment(sketch, "E5190", {"start": v(-31.07, -1.68) * mm, "end": v(-30.76, -1.8) * mm});
            skLineSegment(sketch, "E5191", {"start": v(-30.76, -1.8) * mm, "end": v(-30.45, -1.92) * mm});
            skLineSegment(sketch, "E5192", {"start": v(-30.45, -1.92) * mm, "end": v(-30.15, -2.03) * mm});
            skLineSegment(sketch, "E5193", {"start": v(-30.15, -2.03) * mm, "end": v(-29.84, -2.14) * mm});
            skLineSegment(sketch, "E5194", {"start": v(-29.84, -2.14) * mm, "end": v(-29.54, -2.24) * mm});
            skLineSegment(sketch, "E5195", {"start": v(-29.54, -2.24) * mm, "end": v(-29.23, -2.33) * mm});
            skLineSegment(sketch, "E5196", {"start": v(-29.23, -2.33) * mm, "end": v(-28.92, -2.42) * mm});
            skLineSegment(sketch, "E5197", {"start": v(-28.92, -2.42) * mm, "end": v(-28.62, -2.5) * mm});
            skLineSegment(sketch, "E5198", {"start": v(-28.62, -2.5) * mm, "end": v(-28.3, -2.59) * mm});
            skLineSegment(sketch, "E5199", {"start": v(-28.3, -2.59) * mm, "end": v(-28, -2.66) * mm});
            skLineSegment(sketch, "E5200", {"start": v(-28, -2.66) * mm, "end": v(-27.7, -2.73) * mm});
            skLineSegment(sketch, "E5201", {"start": v(-27.7, -2.73) * mm, "end": v(-27.39, -2.8) * mm});
            skLineSegment(sketch, "E5202", {"start": v(-27.39, -2.8) * mm, "end": v(-27.08, -2.85) * mm});
            skLineSegment(sketch, "E5203", {"start": v(-27.08, -2.85) * mm, "end": v(-26.77, -2.9) * mm});
            skLineSegment(sketch, "E5204", {"start": v(-26.77, -2.9) * mm, "end": v(-26.47, -2.95) * mm});
            skLineSegment(sketch, "E5205", {"start": v(-26.47, -2.95) * mm, "end": v(-26.16, -2.99) * mm});
            skLineSegment(sketch, "E5206", {"start": v(-26.16, -2.99) * mm, "end": v(-25.85, -3.02) * mm});
            skLineSegment(sketch, "E5207", {"start": v(-25.85, -3.02) * mm, "end": v(-25.54, -3.05) * mm});
            skLineSegment(sketch, "E5208", {"start": v(-25.54, -3.05) * mm, "end": v(-25.23, -3.08) * mm});
            skLineSegment(sketch, "E5209", {"start": v(-25.23, -3.08) * mm, "end": v(-24.92, -3.1) * mm});
            skLineSegment(sketch, "E5210", {"start": v(-24.92, -3.1) * mm, "end": v(-24.62, -3.11) * mm});
            skLineSegment(sketch, "E5211", {"start": v(-24.62, -3.11) * mm, "end": v(-24.3, -3.12) * mm});
            skLineSegment(sketch, "E5212", {"start": v(-24.3, -3.12) * mm, "end": v(-24, -3.12) * mm});
            skLineSegment(sketch, "E5213", {"start": v(-24, -3.12) * mm, "end": v(-23.7, -3.12) * mm});
            skLineSegment(sketch, "E5214", {"start": v(-3.85, -40.5) * mm, "end": v(-4.1, -39.93) * mm});
            skLineSegment(sketch, "E5215", {"start": v(-4.1, -39.93) * mm, "end": v(-4.32, -39.36) * mm});
            skLineSegment(sketch, "E5216", {"start": v(-4.32, -39.36) * mm, "end": v(-4.55, -38.79) * mm});
            skLineSegment(sketch, "E5217", {"start": v(-4.55, -38.79) * mm, "end": v(-4.76, -38.21) * mm});
            skLineSegment(sketch, "E5218", {"start": v(-4.76, -38.21) * mm, "end": v(-4.97, -37.64) * mm});
            skLineSegment(sketch, "E5219", {"start": v(-4.97, -37.64) * mm, "end": v(-5.17, -37.07) * mm});
            skLineSegment(sketch, "E5220", {"start": v(-5.17, -37.07) * mm, "end": v(-5.36, -36.5) * mm});
            skLineSegment(sketch, "E5221", {"start": v(-5.36, -36.5) * mm, "end": v(-5.55, -35.91) * mm});
            skLineSegment(sketch, "E5222", {"start": v(-5.55, -35.91) * mm, "end": v(-5.72, -35.34) * mm});
            skLineSegment(sketch, "E5223", {"start": v(-5.72, -35.34) * mm, "end": v(-5.9, -34.76) * mm});
            skLineSegment(sketch, "E5224", {"start": v(-5.9, -34.76) * mm, "end": v(-6.05, -34.18) * mm});
            skLineSegment(sketch, "E5225", {"start": v(-6.05, -34.18) * mm, "end": v(-6.2, -33.6) * mm});
            skLineSegment(sketch, "E5226", {"start": v(-6.2, -33.6) * mm, "end": v(-6.35, -33.03) * mm});
            skLineSegment(sketch, "E5227", {"start": v(-6.35, -33.03) * mm, "end": v(-6.48, -32.45) * mm});
            skLineSegment(sketch, "E5228", {"start": v(-6.48, -32.45) * mm, "end": v(-6.6, -31.87) * mm});
            skLineSegment(sketch, "E5229", {"start": v(-6.6, -31.87) * mm, "end": v(-6.73, -31.29) * mm});
            skLineSegment(sketch, "E5230", {"start": v(-6.73, -31.29) * mm, "end": v(-6.84, -30.7) * mm});
            skLineSegment(sketch, "E5231", {"start": v(-6.84, -30.7) * mm, "end": v(-6.94, -30.12) * mm});
            skLineSegment(sketch, "E5232", {"start": v(-6.94, -30.12) * mm, "end": v(-7.04, -29.54) * mm});
            skLineSegment(sketch, "E5233", {"start": v(-7.04, -29.54) * mm, "end": v(-7.12, -28.96) * mm});
            skLineSegment(sketch, "E5234", {"start": v(-7.12, -28.96) * mm, "end": v(-7.2, -28.37) * mm});
            skLineSegment(sketch, "E5235", {"start": v(-7.2, -28.37) * mm, "end": v(-7.27, -27.8) * mm});
            skLineSegment(sketch, "E5236", {"start": v(-7.27, -27.8) * mm, "end": v(-7.34, -27.2) * mm});
            skLineSegment(sketch, "E5237", {"start": v(-7.34, -27.2) * mm, "end": v(-7.39, -26.62) * mm});
            skLineSegment(sketch, "E5238", {"start": v(-7.39, -26.62) * mm, "end": v(-7.44, -26.04) * mm});
            skLineSegment(sketch, "E5239", {"start": v(-7.44, -26.04) * mm, "end": v(-7.47, -25.45) * mm});
            skLineSegment(sketch, "E5240", {"start": v(-7.47, -25.45) * mm, "end": v(-7.5, -24.86) * mm});
            skLineSegment(sketch, "E5241", {"start": v(-7.5, -24.86) * mm, "end": v(-7.52, -24.28) * mm});
            skLineSegment(sketch, "E5242", {"start": v(-7.52, -24.28) * mm, "end": v(-7.54, -23.69) * mm});
            skLineSegment(sketch, "E5243", {"start": v(-7.54, -23.69) * mm, "end": v(-7.54, -23.1) * mm});
            skLineSegment(sketch, "E5244", {"start": v(-7.54, -23.1) * mm, "end": v(-7.54, -22.52) * mm});
            skLineSegment(sketch, "E5245", {"start": v(-7.54, -22.52) * mm, "end": v(-7.52, -21.94) * mm});
            skLineSegment(sketch, "E5246", {"start": v(-7.52, -21.94) * mm, "end": v(-7.5, -21.36) * mm});
            skLineSegment(sketch, "E5247", {"start": v(-7.5, -21.36) * mm, "end": v(-7.47, -20.79) * mm});
            skLineSegment(sketch, "E5248", {"start": v(-7.47, -20.79) * mm, "end": v(-7.44, -20.2) * mm});
            skLineSegment(sketch, "E5249", {"start": v(-7.44, -20.2) * mm, "end": v(-7.4, -19.63) * mm});
            skLineSegment(sketch, "E5250", {"start": v(-7.4, -19.63) * mm, "end": v(-7.34, -19.05) * mm});
            skLineSegment(sketch, "E5251", {"start": v(-7.34, -19.05) * mm, "end": v(-7.28, -18.48) * mm});
            skLineSegment(sketch, "E5252", {"start": v(-7.28, -18.48) * mm, "end": v(-7.21, -17.9) * mm});
            skLineSegment(sketch, "E5253", {"start": v(-7.21, -17.9) * mm, "end": v(-7.14, -17.33) * mm});
            skLineSegment(sketch, "E5254", {"start": v(-7.14, -17.33) * mm, "end": v(-7.05, -16.75) * mm});
            skLineSegment(sketch, "E5255", {"start": v(-7.05, -16.75) * mm, "end": v(-6.96, -16.18) * mm});
            skLineSegment(sketch, "E5256", {"start": v(-6.96, -16.18) * mm, "end": v(-6.86, -15.6) * mm});
            skLineSegment(sketch, "E5257", {"start": v(-6.86, -15.6) * mm, "end": v(-6.75, -15.03) * mm});
            skLineSegment(sketch, "E5258", {"start": v(-6.75, -15.03) * mm, "end": v(-6.64, -14.46) * mm});
            skLineSegment(sketch, "E5259", {"start": v(-6.64, -14.46) * mm, "end": v(-6.51, -13.89) * mm});
            skLineSegment(sketch, "E5260", {"start": v(-6.51, -13.89) * mm, "end": v(-6.38, -13.32) * mm});
            skLineSegment(sketch, "E5261", {"start": v(-6.38, -13.32) * mm, "end": v(-6.24, -12.75) * mm});
            skLineSegment(sketch, "E5262", {"start": v(-6.24, -12.75) * mm, "end": v(-6.1, -12.18) * mm});
            skLineSegment(sketch, "E5263", {"start": v(-6.1, -12.18) * mm, "end": v(-5.94, -11.6) * mm});
            skLineSegment(sketch, "E5264", {"start": v(-5.94, -11.6) * mm, "end": v(-5.77, -11.04) * mm});
            skLineSegment(sketch, "E5265", {"start": v(-5.77, -11.04) * mm, "end": v(-5.6, -10.47) * mm});
            skLineSegment(sketch, "E5266", {"start": v(-5.6, -10.47) * mm, "end": v(-5.42, -9.9) * mm});
            skLineSegment(sketch, "E5267", {"start": v(-5.42, -9.9) * mm, "end": v(-5.24, -9.33) * mm});
            skLineSegment(sketch, "E5268", {"start": v(-5.24, -9.33) * mm, "end": v(-5.04, -8.76) * mm});
            skLineSegment(sketch, "E5269", {"start": v(-5.04, -8.76) * mm, "end": v(-4.84, -8.2) * mm});
            skLineSegment(sketch, "E5270", {"start": v(-4.84, -8.2) * mm, "end": v(-4.63, -7.63) * mm});
            skLineSegment(sketch, "E5271", {"start": v(-4.63, -7.63) * mm, "end": v(-4.41, -7.07) * mm});
            skLineSegment(sketch, "E5272", {"start": v(-4.41, -7.07) * mm, "end": v(-4.19, -6.5) * mm});
            skLineSegment(sketch, "E5273", {"start": v(-4.19, -6.5) * mm, "end": v(-3.95, -5.94) * mm});
            skLineSegment(sketch, "E5274", {"start": v(-3.95, -5.94) * mm, "end": v(-3.71, -5.38) * mm});
            skLineSegment(sketch, "E5275", {"start": v(-3.71, -5.38) * mm, "end": v(-3.56, -5.04) * mm});
            skLineSegment(sketch, "E5276", {"start": v(-3.56, -5.04) * mm, "end": v(-3.87, -4.85) * mm});
            skLineSegment(sketch, "E5277", {"start": v(-3.87, -4.85) * mm, "end": v(-4.17, -4.65) * mm});
            skLineSegment(sketch, "E5278", {"start": v(-4.17, -4.65) * mm, "end": v(-4.46, -4.43) * mm});
            skLineSegment(sketch, "E5279", {"start": v(-4.46, -4.43) * mm, "end": v(-4.73, -4.2) * mm});
            skLineSegment(sketch, "E5280", {"start": v(-4.73, -4.2) * mm, "end": v(-4.98, -3.94) * mm});
            skLineSegment(sketch, "E5281", {"start": v(-4.98, -3.94) * mm, "end": v(-5.22, -3.66) * mm});
            skLineSegment(sketch, "E5282", {"start": v(-5.22, -3.66) * mm, "end": v(-5.44, -3.38) * mm});
            skLineSegment(sketch, "E5283", {"start": v(-5.44, -3.38) * mm, "end": v(-5.64, -3.08) * mm});
            skLineSegment(sketch, "E5284", {"start": v(-5.64, -3.08) * mm, "end": v(-5.83, -2.77) * mm});
            skLineSegment(sketch, "E5285", {"start": v(-5.83, -2.77) * mm, "end": v(-5.97, -2.5) * mm});
            skLineSegment(sketch, "E5286", {"start": v(-5.97, -2.5) * mm, "end": v(-6.17, -2.6) * mm});
            skLineSegment(sketch, "E5287", {"start": v(-6.17, -2.6) * mm, "end": v(-6.73, -2.87) * mm});
            skLineSegment(sketch, "E5288", {"start": v(-6.73, -2.87) * mm, "end": v(-7.3, -3.15) * mm});
            skLineSegment(sketch, "E5289", {"start": v(-7.3, -3.15) * mm, "end": v(-7.86, -3.4) * mm});
            skLineSegment(sketch, "E5290", {"start": v(-7.86, -3.4) * mm, "end": v(-8.42, -3.66) * mm});
            skLineSegment(sketch, "E5291", {"start": v(-8.42, -3.66) * mm, "end": v(-8.99, -3.9) * mm});
            skLineSegment(sketch, "E5292", {"start": v(-8.99, -3.9) * mm, "end": v(-9.56, -4.14) * mm});
            skLineSegment(sketch, "E5293", {"start": v(-9.56, -4.14) * mm, "end": v(-10.12, -4.37) * mm});
            skLineSegment(sketch, "E5294", {"start": v(-10.12, -4.37) * mm, "end": v(-10.7, -4.58) * mm});
            skLineSegment(sketch, "E5295", {"start": v(-10.7, -4.58) * mm, "end": v(-11.26, -4.8) * mm});
            skLineSegment(sketch, "E5296", {"start": v(-11.26, -4.8) * mm, "end": v(-11.83, -5) * mm});
            skLineSegment(sketch, "E5297", {"start": v(-11.83, -5) * mm, "end": v(-12.4, -5.18) * mm});
            skLineSegment(sketch, "E5298", {"start": v(-12.4, -5.18) * mm, "end": v(-12.97, -5.36) * mm});
            skLineSegment(sketch, "E5299", {"start": v(-12.97, -5.36) * mm, "end": v(-13.54, -5.53) * mm});
            skLineSegment(sketch, "E5300", {"start": v(-13.54, -5.53) * mm, "end": v(-14.1, -5.7) * mm});
            skLineSegment(sketch, "E5301", {"start": v(-14.1, -5.7) * mm, "end": v(-14.68, -5.85) * mm});
            skLineSegment(sketch, "E5302", {"start": v(-14.68, -5.85) * mm, "end": v(-15.25, -6) * mm});
            skLineSegment(sketch, "E5303", {"start": v(-15.25, -6) * mm, "end": v(-15.82, -6.13) * mm});
            skLineSegment(sketch, "E5304", {"start": v(-15.82, -6.13) * mm, "end": v(-16.4, -6.26) * mm});
            skLineSegment(sketch, "E5305", {"start": v(-16.4, -6.26) * mm, "end": v(-16.97, -6.37) * mm});
            skLineSegment(sketch, "E5306", {"start": v(-16.97, -6.37) * mm, "end": v(-17.54, -6.48) * mm});
            skLineSegment(sketch, "E5307", {"start": v(-17.54, -6.48) * mm, "end": v(-18.12, -6.58) * mm});
            skLineSegment(sketch, "E5308", {"start": v(-18.12, -6.58) * mm, "end": v(-18.7, -6.67) * mm});
            skLineSegment(sketch, "E5309", {"start": v(-18.7, -6.67) * mm, "end": v(-19.27, -6.75) * mm});
            skLineSegment(sketch, "E5310", {"start": v(-19.27, -6.75) * mm, "end": v(-19.85, -6.82) * mm});
            skLineSegment(sketch, "E5311", {"start": v(-19.85, -6.82) * mm, "end": v(-20.42, -6.88) * mm});
            skLineSegment(sketch, "E5312", {"start": v(-20.42, -6.88) * mm, "end": v(-21, -6.93) * mm});
            skLineSegment(sketch, "E5313", {"start": v(-21, -6.93) * mm, "end": v(-21.58, -6.97) * mm});
            skLineSegment(sketch, "E5314", {"start": v(-21.58, -6.97) * mm, "end": v(-22.15, -7) * mm});
            skLineSegment(sketch, "E5315", {"start": v(-22.15, -7) * mm, "end": v(-22.73, -7.03) * mm});
            skLineSegment(sketch, "E5316", {"start": v(-22.73, -7.03) * mm, "end": v(-23.31, -7.04) * mm});
            skLineSegment(sketch, "E5317", {"start": v(-23.31, -7.04) * mm, "end": v(-23.9, -7.05) * mm});
            skLineSegment(sketch, "E5318", {"start": v(-23.9, -7.05) * mm, "end": v(-24.48, -7.04) * mm});
            skLineSegment(sketch, "E5319", {"start": v(-24.48, -7.04) * mm, "end": v(-25.07, -7.03) * mm});
            skLineSegment(sketch, "E5320", {"start": v(-25.07, -7.03) * mm, "end": v(-25.65, -7) * mm});
            skLineSegment(sketch, "E5321", {"start": v(-25.65, -7) * mm, "end": v(-26.24, -6.97) * mm});
            skLineSegment(sketch, "E5322", {"start": v(-26.24, -6.97) * mm, "end": v(-26.83, -6.93) * mm});
            skLineSegment(sketch, "E5323", {"start": v(-26.83, -6.93) * mm, "end": v(-27.41, -6.87) * mm});
            skLineSegment(sketch, "E5324", {"start": v(-27.41, -6.87) * mm, "end": v(-28, -6.81) * mm});
            skLineSegment(sketch, "E5325", {"start": v(-28, -6.81) * mm, "end": v(-28.58, -6.74) * mm});
            skLineSegment(sketch, "E5326", {"start": v(-28.58, -6.74) * mm, "end": v(-29.17, -6.66) * mm});
            skLineSegment(sketch, "E5327", {"start": v(-29.17, -6.66) * mm, "end": v(-29.75, -6.56) * mm});
            skLineSegment(sketch, "E5328", {"start": v(-29.75, -6.56) * mm, "end": v(-30.33, -6.46) * mm});
            skLineSegment(sketch, "E5329", {"start": v(-30.33, -6.46) * mm, "end": v(-30.91, -6.35) * mm});
            skLineSegment(sketch, "E5330", {"start": v(-30.91, -6.35) * mm, "end": v(-31.5, -6.23) * mm});
            skLineSegment(sketch, "E5331", {"start": v(-31.5, -6.23) * mm, "end": v(-32.08, -6.1) * mm});
            skLineSegment(sketch, "E5332", {"start": v(-32.08, -6.1) * mm, "end": v(-32.66, -5.97) * mm});
            skLineSegment(sketch, "E5333", {"start": v(-32.66, -5.97) * mm, "end": v(-33.24, -5.82) * mm});
            skLineSegment(sketch, "E5334", {"start": v(-33.24, -5.82) * mm, "end": v(-33.82, -5.66) * mm});
            skLineSegment(sketch, "E5335", {"start": v(-33.82, -5.66) * mm, "end": v(-34.4, -5.5) * mm});
            skLineSegment(sketch, "E5336", {"start": v(-34.4, -5.5) * mm, "end": v(-34.97, -5.31) * mm});
            skLineSegment(sketch, "E5337", {"start": v(-34.97, -5.31) * mm, "end": v(-35.55, -5.13) * mm});
            skLineSegment(sketch, "E5338", {"start": v(-35.55, -5.13) * mm, "end": v(-36.13, -4.93) * mm});
            skLineSegment(sketch, "E5339", {"start": v(-36.13, -4.93) * mm, "end": v(-36.7, -4.73) * mm});
            skLineSegment(sketch, "E5340", {"start": v(-36.7, -4.73) * mm, "end": v(-37.28, -4.51) * mm});
            skLineSegment(sketch, "E5341", {"start": v(-37.28, -4.51) * mm, "end": v(-37.86, -4.3) * mm});
            skLineSegment(sketch, "E5342", {"start": v(-37.86, -4.3) * mm, "end": v(-38.43, -4.06) * mm});
            skLineSegment(sketch, "E5343", {"start": v(-38.43, -4.06) * mm, "end": v(-39, -3.82) * mm});
            skLineSegment(sketch, "E5344", {"start": v(-39, -3.82) * mm, "end": v(-39.58, -3.57) * mm});
            skLineSegment(sketch, "E5345", {"start": v(-39.58, -3.57) * mm, "end": v(-40.15, -3.3) * mm});
            skLineSegment(sketch, "E5346", {"start": v(-40.15, -3.3) * mm, "end": v(-40.72, -3.03) * mm});
            skLineSegment(sketch, "E5347", {"start": v(-40.72, -3.03) * mm, "end": v(-41.3, -2.76) * mm});
            skLineSegment(sketch, "E5348", {"start": v(-41.3, -2.76) * mm, "end": v(-41.65, -2.58) * mm});
            skLineSegment(sketch, "E5349", {"start": v(-41.65, -2.58) * mm, "end": v(-41.4, -5.13) * mm});
            skLineSegment(sketch, "E5350", {"start": v(-41.4, -5.13) * mm, "end": v(-41, -7.67) * mm});
            skLineSegment(sketch, "E5351", {"start": v(-41, -7.67) * mm, "end": v(-40.44, -10.18) * mm});
            skLineSegment(sketch, "E5352", {"start": v(-40.44, -10.18) * mm, "end": v(-39.72, -12.65) * mm});
            skLineSegment(sketch, "E5353", {"start": v(-39.72, -12.65) * mm, "end": v(-38.85, -15.07) * mm});
            skLineSegment(sketch, "E5354", {"start": v(-38.85, -15.07) * mm, "end": v(-37.83, -17.43) * mm});
            skLineSegment(sketch, "E5355", {"start": v(-37.83, -17.43) * mm, "end": v(-36.66, -19.72) * mm});
            skLineSegment(sketch, "E5356", {"start": v(-36.66, -19.72) * mm, "end": v(-35.35, -21.93) * mm});
            skLineSegment(sketch, "E5357", {"start": v(-35.35, -21.93) * mm, "end": v(-33.9, -24.06) * mm});
            skLineSegment(sketch, "E5358", {"start": v(-33.9, -24.06) * mm, "end": v(-32.33, -26.1) * mm});
            skLineSegment(sketch, "E5359", {"start": v(-32.33, -26.1) * mm, "end": v(-30.63, -28.02) * mm});
            skLineSegment(sketch, "E5360", {"start": v(-30.63, -28.02) * mm, "end": v(-28.81, -29.84) * mm});
            skLineSegment(sketch, "E5361", {"start": v(-28.81, -29.84) * mm, "end": v(-26.88, -31.54) * mm});
            skLineSegment(sketch, "E5362", {"start": v(-26.88, -31.54) * mm, "end": v(-24.85, -33.12) * mm});
            skLineSegment(sketch, "E5363", {"start": v(-24.85, -33.12) * mm, "end": v(-22.73, -34.56) * mm});
            skLineSegment(sketch, "E5364", {"start": v(-22.73, -34.56) * mm, "end": v(-20.51, -35.87) * mm});
            skLineSegment(sketch, "E5365", {"start": v(-20.51, -35.87) * mm, "end": v(-18.22, -37.04) * mm});
            skLineSegment(sketch, "E5366", {"start": v(-18.22, -37.04) * mm, "end": v(-15.86, -38.06) * mm});
            skLineSegment(sketch, "E5367", {"start": v(-15.86, -38.06) * mm, "end": v(-13.44, -38.93) * mm});
            skLineSegment(sketch, "E5368", {"start": v(-13.44, -38.93) * mm, "end": v(-10.97, -39.65) * mm});
            skLineSegment(sketch, "E5369", {"start": v(-10.97, -39.65) * mm, "end": v(-8.46, -40.21) * mm});
            skLineSegment(sketch, "E5370", {"start": v(-8.46, -40.21) * mm, "end": v(-5.92, -40.61) * mm});
            skLineSegment(sketch, "E5371", {"start": v(-5.92, -40.61) * mm, "end": v(-3.71, -40.82) * mm});
            skLineSegment(sketch, "E5372", {"start": v(-3.71, -40.82) * mm, "end": v(-3.85, -40.5) * mm});
            skLineSegment(sketch, "E5373", {"start": v(4.34, -40.61) * mm, "end": v(6.88, -40.21) * mm});
            skLineSegment(sketch, "E5374", {"start": v(6.88, -40.21) * mm, "end": v(9.39, -39.65) * mm});
            skLineSegment(sketch, "E5375", {"start": v(9.39, -39.65) * mm, "end": v(11.86, -38.93) * mm});
            skLineSegment(sketch, "E5376", {"start": v(11.86, -38.93) * mm, "end": v(14.28, -38.06) * mm});
            skLineSegment(sketch, "E5377", {"start": v(14.28, -38.06) * mm, "end": v(16.64, -37.04) * mm});
            skLineSegment(sketch, "E5378", {"start": v(16.64, -37.04) * mm, "end": v(18.93, -35.87) * mm});
            skLineSegment(sketch, "E5379", {"start": v(18.93, -35.87) * mm, "end": v(21.14, -34.56) * mm});
            skLineSegment(sketch, "E5380", {"start": v(21.14, -34.56) * mm, "end": v(23.27, -33.12) * mm});
            skLineSegment(sketch, "E5381", {"start": v(23.27, -33.12) * mm, "end": v(25.3, -31.54) * mm});
            skLineSegment(sketch, "E5382", {"start": v(25.3, -31.54) * mm, "end": v(27.23, -29.84) * mm});
            skLineSegment(sketch, "E5383", {"start": v(27.23, -29.84) * mm, "end": v(29.05, -28.02) * mm});
            skLineSegment(sketch, "E5384", {"start": v(29.05, -28.02) * mm, "end": v(30.75, -26.1) * mm});
            skLineSegment(sketch, "E5385", {"start": v(30.75, -26.1) * mm, "end": v(32.33, -24.06) * mm});
            skLineSegment(sketch, "E5386", {"start": v(32.33, -24.06) * mm, "end": v(33.77, -21.93) * mm});
            skLineSegment(sketch, "E5387", {"start": v(33.77, -21.93) * mm, "end": v(35.08, -19.72) * mm});
            skLineSegment(sketch, "E5388", {"start": v(35.08, -19.72) * mm, "end": v(36.25, -17.43) * mm});
            skLineSegment(sketch, "E5389", {"start": v(36.25, -17.43) * mm, "end": v(37.27, -15.07) * mm});
            skLineSegment(sketch, "E5390", {"start": v(37.27, -15.07) * mm, "end": v(38.14, -12.65) * mm});
            skLineSegment(sketch, "E5391", {"start": v(38.14, -12.65) * mm, "end": v(38.86, -10.18) * mm});
            skLineSegment(sketch, "E5392", {"start": v(38.86, -10.18) * mm, "end": v(39.42, -7.67) * mm});
            skLineSegment(sketch, "E5393", {"start": v(39.42, -7.67) * mm, "end": v(39.82, -5.13) * mm});
            skLineSegment(sketch, "E5394", {"start": v(39.82, -5.13) * mm, "end": v(40.03, -2.92) * mm});
            skLineSegment(sketch, "E5395", {"start": v(40.03, -2.92) * mm, "end": v(39.72, -3.06) * mm});
            skLineSegment(sketch, "E5396", {"start": v(39.72, -3.06) * mm, "end": v(39.14, -3.3) * mm});
            skLineSegment(sketch, "E5397", {"start": v(39.14, -3.3) * mm, "end": v(38.57, -3.53) * mm});
            skLineSegment(sketch, "E5398", {"start": v(38.57, -3.53) * mm, "end": v(38, -3.76) * mm});
            skLineSegment(sketch, "E5399", {"start": v(38, -3.76) * mm, "end": v(37.42, -3.97) * mm});
            skLineSegment(sketch, "E5400", {"start": v(37.42, -3.97) * mm, "end": v(36.85, -4.18) * mm});
            skLineSegment(sketch, "E5401", {"start": v(36.85, -4.18) * mm, "end": v(36.27, -4.38) * mm});
            skLineSegment(sketch, "E5402", {"start": v(36.27, -4.38) * mm, "end": v(35.7, -4.57) * mm});
            skLineSegment(sketch, "E5403", {"start": v(35.7, -4.57) * mm, "end": v(35.12, -4.76) * mm});
            skLineSegment(sketch, "E5404", {"start": v(35.12, -4.76) * mm, "end": v(34.55, -4.93) * mm});
            skLineSegment(sketch, "E5405", {"start": v(34.55, -4.93) * mm, "end": v(33.97, -5.1) * mm});
            skLineSegment(sketch, "E5406", {"start": v(33.97, -5.1) * mm, "end": v(33.4, -5.26) * mm});
            skLineSegment(sketch, "E5407", {"start": v(33.4, -5.26) * mm, "end": v(32.81, -5.41) * mm});
            skLineSegment(sketch, "E5408", {"start": v(32.81, -5.41) * mm, "end": v(32.23, -5.56) * mm});
            skLineSegment(sketch, "E5409", {"start": v(32.23, -5.56) * mm, "end": v(31.66, -5.7) * mm});
            skLineSegment(sketch, "E5410", {"start": v(31.66, -5.7) * mm, "end": v(31.08, -5.82) * mm});
            skLineSegment(sketch, "E5411", {"start": v(31.08, -5.82) * mm, "end": v(30.5, -5.94) * mm});
            skLineSegment(sketch, "E5412", {"start": v(30.5, -5.94) * mm, "end": v(29.91, -6.05) * mm});
            skLineSegment(sketch, "E5413", {"start": v(29.91, -6.05) * mm, "end": v(29.33, -6.15) * mm});
            skLineSegment(sketch, "E5414", {"start": v(29.33, -6.15) * mm, "end": v(28.75, -6.25) * mm});
            skLineSegment(sketch, "E5415", {"start": v(28.75, -6.25) * mm, "end": v(28.17, -6.33) * mm});
            skLineSegment(sketch, "E5416", {"start": v(28.17, -6.33) * mm, "end": v(27.58, -6.41) * mm});
            skLineSegment(sketch, "E5417", {"start": v(27.58, -6.41) * mm, "end": v(27, -6.48) * mm});
            skLineSegment(sketch, "E5418", {"start": v(27, -6.48) * mm, "end": v(26.42, -6.54) * mm});
            skLineSegment(sketch, "E5419", {"start": v(26.42, -6.54) * mm, "end": v(25.83, -6.6) * mm});
            skLineSegment(sketch, "E5420", {"start": v(25.83, -6.6) * mm, "end": v(25.25, -6.64) * mm});
            skLineSegment(sketch, "E5421", {"start": v(25.25, -6.64) * mm, "end": v(24.66, -6.68) * mm});
            skLineSegment(sketch, "E5422", {"start": v(24.66, -6.68) * mm, "end": v(24.07, -6.71) * mm});
            skLineSegment(sketch, "E5423", {"start": v(24.07, -6.71) * mm, "end": v(23.49, -6.73) * mm});
            skLineSegment(sketch, "E5424", {"start": v(23.49, -6.73) * mm, "end": v(22.9, -6.74) * mm});
            skLineSegment(sketch, "E5425", {"start": v(22.9, -6.74) * mm, "end": v(22.31, -6.75) * mm});
            skLineSegment(sketch, "E5426", {"start": v(22.31, -6.75) * mm, "end": v(21.73, -6.74) * mm});
            skLineSegment(sketch, "E5427", {"start": v(21.73, -6.74) * mm, "end": v(21.15, -6.73) * mm});
            skLineSegment(sketch, "E5428", {"start": v(21.15, -6.73) * mm, "end": v(20.57, -6.71) * mm});
            skLineSegment(sketch, "E5429", {"start": v(20.57, -6.71) * mm, "end": v(20, -6.68) * mm});
            skLineSegment(sketch, "E5430", {"start": v(20, -6.68) * mm, "end": v(19.42, -6.65) * mm});
            skLineSegment(sketch, "E5431", {"start": v(19.42, -6.65) * mm, "end": v(18.84, -6.6) * mm});
            skLineSegment(sketch, "E5432", {"start": v(18.84, -6.6) * mm, "end": v(18.26, -6.55) * mm});
            skLineSegment(sketch, "E5433", {"start": v(18.26, -6.55) * mm, "end": v(17.69, -6.5) * mm});
            skLineSegment(sketch, "E5434", {"start": v(17.69, -6.5) * mm, "end": v(17.11, -6.42) * mm});
            skLineSegment(sketch, "E5435", {"start": v(17.11, -6.42) * mm, "end": v(16.54, -6.35) * mm});
            skLineSegment(sketch, "E5436", {"start": v(16.54, -6.35) * mm, "end": v(15.96, -6.26) * mm});
            skLineSegment(sketch, "E5437", {"start": v(15.96, -6.26) * mm, "end": v(15.39, -6.17) * mm});
            skLineSegment(sketch, "E5438", {"start": v(15.39, -6.17) * mm, "end": v(14.81, -6.07) * mm});
            skLineSegment(sketch, "E5439", {"start": v(14.81, -6.07) * mm, "end": v(14.24, -5.96) * mm});
            skLineSegment(sketch, "E5440", {"start": v(14.24, -5.96) * mm, "end": v(13.67, -5.84) * mm});
            skLineSegment(sketch, "E5441", {"start": v(13.67, -5.84) * mm, "end": v(13.1, -5.72) * mm});
            skLineSegment(sketch, "E5442", {"start": v(13.1, -5.72) * mm, "end": v(12.53, -5.59) * mm});
            skLineSegment(sketch, "E5443", {"start": v(12.53, -5.59) * mm, "end": v(11.95, -5.45) * mm});
            skLineSegment(sketch, "E5444", {"start": v(11.95, -5.45) * mm, "end": v(11.38, -5.3) * mm});
            skLineSegment(sketch, "E5445", {"start": v(11.38, -5.3) * mm, "end": v(10.81, -5.15) * mm});
            skLineSegment(sketch, "E5446", {"start": v(10.81, -5.15) * mm, "end": v(10.25, -4.98) * mm});
            skLineSegment(sketch, "E5447", {"start": v(10.25, -4.98) * mm, "end": v(9.68, -4.81) * mm});
            skLineSegment(sketch, "E5448", {"start": v(9.68, -4.81) * mm, "end": v(9.1, -4.63) * mm});
            skLineSegment(sketch, "E5449", {"start": v(9.1, -4.63) * mm, "end": v(8.54, -4.45) * mm});
            skLineSegment(sketch, "E5450", {"start": v(8.54, -4.45) * mm, "end": v(7.97, -4.25) * mm});
            skLineSegment(sketch, "E5451", {"start": v(7.97, -4.25) * mm, "end": v(7.4, -4.05) * mm});
            skLineSegment(sketch, "E5452", {"start": v(7.4, -4.05) * mm, "end": v(6.84, -3.84) * mm});
            skLineSegment(sketch, "E5453", {"start": v(6.84, -3.84) * mm, "end": v(6.28, -3.62) * mm});
            skLineSegment(sketch, "E5454", {"start": v(6.28, -3.62) * mm, "end": v(5.71, -3.4) * mm});
            skLineSegment(sketch, "E5455", {"start": v(5.71, -3.4) * mm, "end": v(5.15, -3.16) * mm});
            skLineSegment(sketch, "E5456", {"start": v(5.15, -3.16) * mm, "end": v(4.58, -2.92) * mm});
            skLineSegment(sketch, "E5457", {"start": v(4.58, -2.92) * mm, "end": v(4.25, -2.77) * mm});
            skLineSegment(sketch, "E5458", {"start": v(4.25, -2.77) * mm, "end": v(4.06, -3.08) * mm});
            skLineSegment(sketch, "E5459", {"start": v(4.06, -3.08) * mm, "end": v(3.86, -3.38) * mm});
            skLineSegment(sketch, "E5460", {"start": v(3.86, -3.38) * mm, "end": v(3.64, -3.66) * mm});
            skLineSegment(sketch, "E5461", {"start": v(3.64, -3.66) * mm, "end": v(3.4, -3.94) * mm});
            skLineSegment(sketch, "E5462", {"start": v(3.4, -3.94) * mm, "end": v(3.14, -4.2) * mm});
            skLineSegment(sketch, "E5463", {"start": v(3.14, -4.2) * mm, "end": v(2.87, -4.43) * mm});
            skLineSegment(sketch, "E5464", {"start": v(2.87, -4.43) * mm, "end": v(2.59, -4.65) * mm});
            skLineSegment(sketch, "E5465", {"start": v(2.59, -4.65) * mm, "end": v(2.29, -4.85) * mm});
            skLineSegment(sketch, "E5466", {"start": v(2.29, -4.85) * mm, "end": v(1.98, -5.04) * mm});
            skLineSegment(sketch, "E5467", {"start": v(1.98, -5.04) * mm, "end": v(1.7, -5.18) * mm});
            skLineSegment(sketch, "E5468", {"start": v(1.7, -5.18) * mm, "end": v(1.8, -5.38) * mm});
            skLineSegment(sketch, "E5469", {"start": v(1.8, -5.38) * mm, "end": v(2.08, -5.94) * mm});
            skLineSegment(sketch, "E5470", {"start": v(2.08, -5.94) * mm, "end": v(2.35, -6.5) * mm});
            skLineSegment(sketch, "E5471", {"start": v(2.35, -6.5) * mm, "end": v(2.62, -7.07) * mm});
            skLineSegment(sketch, "E5472", {"start": v(2.62, -7.07) * mm, "end": v(2.87, -7.63) * mm});
            skLineSegment(sketch, "E5473", {"start": v(2.87, -7.63) * mm, "end": v(3.12, -8.2) * mm});
            skLineSegment(sketch, "E5474", {"start": v(3.12, -8.2) * mm, "end": v(3.35, -8.76) * mm});
            skLineSegment(sketch, "E5475", {"start": v(3.35, -8.76) * mm, "end": v(3.58, -9.33) * mm});
            skLineSegment(sketch, "E5476", {"start": v(3.58, -9.33) * mm, "end": v(3.8, -9.9) * mm});
            skLineSegment(sketch, "E5477", {"start": v(3.8, -9.9) * mm, "end": v(4, -10.47) * mm});
            skLineSegment(sketch, "E5478", {"start": v(4, -10.47) * mm, "end": v(4.2, -11.04) * mm});
            skLineSegment(sketch, "E5479", {"start": v(4.2, -11.04) * mm, "end": v(4.4, -11.6) * mm});
            skLineSegment(sketch, "E5480", {"start": v(4.4, -11.6) * mm, "end": v(4.57, -12.18) * mm});
            skLineSegment(sketch, "E5481", {"start": v(4.57, -12.18) * mm, "end": v(4.74, -12.75) * mm});
            skLineSegment(sketch, "E5482", {"start": v(4.74, -12.75) * mm, "end": v(4.9, -13.32) * mm});
            skLineSegment(sketch, "E5483", {"start": v(4.9, -13.32) * mm, "end": v(5.06, -13.89) * mm});
            skLineSegment(sketch, "E5484", {"start": v(5.06, -13.89) * mm, "end": v(5.2, -14.46) * mm});
            skLineSegment(sketch, "E5485", {"start": v(5.2, -14.46) * mm, "end": v(5.34, -15.03) * mm});
            skLineSegment(sketch, "E5486", {"start": v(5.34, -15.03) * mm, "end": v(5.47, -15.6) * mm});
            skLineSegment(sketch, "E5487", {"start": v(5.47, -15.6) * mm, "end": v(5.58, -16.18) * mm});
            skLineSegment(sketch, "E5488", {"start": v(5.58, -16.18) * mm, "end": v(5.69, -16.75) * mm});
            skLineSegment(sketch, "E5489", {"start": v(5.69, -16.75) * mm, "end": v(5.79, -17.33) * mm});
            skLineSegment(sketch, "E5490", {"start": v(5.79, -17.33) * mm, "end": v(5.88, -17.9) * mm});
            skLineSegment(sketch, "E5491", {"start": v(5.88, -17.9) * mm, "end": v(5.96, -18.48) * mm});
            skLineSegment(sketch, "E5492", {"start": v(5.96, -18.48) * mm, "end": v(6.03, -19.05) * mm});
            skLineSegment(sketch, "E5493", {"start": v(6.03, -19.05) * mm, "end": v(6.09, -19.63) * mm});
            skLineSegment(sketch, "E5494", {"start": v(6.09, -19.63) * mm, "end": v(6.14, -20.2) * mm});
            skLineSegment(sketch, "E5495", {"start": v(6.14, -20.2) * mm, "end": v(6.18, -20.79) * mm});
            skLineSegment(sketch, "E5496", {"start": v(6.18, -20.79) * mm, "end": v(6.21, -21.36) * mm});
            skLineSegment(sketch, "E5497", {"start": v(6.21, -21.36) * mm, "end": v(6.24, -21.94) * mm});
            skLineSegment(sketch, "E5498", {"start": v(6.24, -21.94) * mm, "end": v(6.25, -22.52) * mm});
            skLineSegment(sketch, "E5499", {"start": v(6.25, -22.52) * mm, "end": v(6.26, -23.1) * mm});
            skLineSegment(sketch, "E5500", {"start": v(6.26, -23.1) * mm, "end": v(6.25, -23.69) * mm});
            skLineSegment(sketch, "E5501", {"start": v(6.25, -23.69) * mm, "end": v(6.24, -24.28) * mm});
            skLineSegment(sketch, "E5502", {"start": v(6.24, -24.28) * mm, "end": v(6.21, -24.86) * mm});
            skLineSegment(sketch, "E5503", {"start": v(6.21, -24.86) * mm, "end": v(6.18, -25.45) * mm});
            skLineSegment(sketch, "E5504", {"start": v(6.18, -25.45) * mm, "end": v(6.14, -26.04) * mm});
            skLineSegment(sketch, "E5505", {"start": v(6.14, -26.04) * mm, "end": v(6.08, -26.62) * mm});
            skLineSegment(sketch, "E5506", {"start": v(6.08, -26.62) * mm, "end": v(6.02, -27.2) * mm});
            skLineSegment(sketch, "E5507", {"start": v(6.02, -27.2) * mm, "end": v(5.95, -27.8) * mm});
            skLineSegment(sketch, "E5508", {"start": v(5.95, -27.8) * mm, "end": v(5.87, -28.37) * mm});
            skLineSegment(sketch, "E5509", {"start": v(5.87, -28.37) * mm, "end": v(5.77, -28.96) * mm});
            skLineSegment(sketch, "E5510", {"start": v(5.77, -28.96) * mm, "end": v(5.67, -29.54) * mm});
            skLineSegment(sketch, "E5511", {"start": v(5.67, -29.54) * mm, "end": v(5.56, -30.12) * mm});
            skLineSegment(sketch, "E5512", {"start": v(5.56, -30.12) * mm, "end": v(5.44, -30.7) * mm});
            skLineSegment(sketch, "E5513", {"start": v(5.44, -30.7) * mm, "end": v(5.31, -31.29) * mm});
            skLineSegment(sketch, "E5514", {"start": v(5.31, -31.29) * mm, "end": v(5.17, -31.87) * mm});
            skLineSegment(sketch, "E5515", {"start": v(5.17, -31.87) * mm, "end": v(5.03, -32.45) * mm});
            skLineSegment(sketch, "E5516", {"start": v(5.03, -32.45) * mm, "end": v(4.87, -33.03) * mm});
            skLineSegment(sketch, "E5517", {"start": v(4.87, -33.03) * mm, "end": v(4.7, -33.6) * mm});
            skLineSegment(sketch, "E5518", {"start": v(4.7, -33.6) * mm, "end": v(4.52, -34.18) * mm});
            skLineSegment(sketch, "E5519", {"start": v(4.52, -34.18) * mm, "end": v(4.34, -34.76) * mm});
            skLineSegment(sketch, "E5520", {"start": v(4.34, -34.76) * mm, "end": v(4.14, -35.34) * mm});
            skLineSegment(sketch, "E5521", {"start": v(4.14, -35.34) * mm, "end": v(3.94, -35.91) * mm});
            skLineSegment(sketch, "E5522", {"start": v(3.94, -35.91) * mm, "end": v(3.72, -36.5) * mm});
            skLineSegment(sketch, "E5523", {"start": v(3.72, -36.5) * mm, "end": v(3.5, -37.07) * mm});
            skLineSegment(sketch, "E5524", {"start": v(3.5, -37.07) * mm, "end": v(3.27, -37.64) * mm});
            skLineSegment(sketch, "E5525", {"start": v(3.27, -37.64) * mm, "end": v(3.03, -38.21) * mm});
            skLineSegment(sketch, "E5526", {"start": v(3.03, -38.21) * mm, "end": v(2.77, -38.79) * mm});
            skLineSegment(sketch, "E5527", {"start": v(2.77, -38.79) * mm, "end": v(2.51, -39.36) * mm});
            skLineSegment(sketch, "E5528", {"start": v(2.51, -39.36) * mm, "end": v(2.24, -39.93) * mm});
            skLineSegment(sketch, "E5529", {"start": v(2.24, -39.93) * mm, "end": v(1.96, -40.5) * mm});
            skLineSegment(sketch, "E5530", {"start": v(1.96, -40.5) * mm, "end": v(1.79, -40.85) * mm});
            skLineSegment(sketch, "E5531", {"start": v(1.79, -40.85) * mm, "end": v(4.34, -40.61) * mm});
            skLineSegment(sketch, "E5532", {"start": v(-0.12, -32.41) * mm, "end": v(0.04, -32.1) * mm});
            skLineSegment(sketch, "E5533", {"start": v(0.04, -32.1) * mm, "end": v(0.2, -31.8) * mm});
            skLineSegment(sketch, "E5534", {"start": v(0.2, -31.8) * mm, "end": v(0.35, -31.5) * mm});
            skLineSegment(sketch, "E5535", {"start": v(0.35, -31.5) * mm, "end": v(0.5, -31.2) * mm});
            skLineSegment(sketch, "E5536", {"start": v(0.5, -31.2) * mm, "end": v(0.63, -30.89) * mm});
            skLineSegment(sketch, "E5537", {"start": v(0.63, -30.89) * mm, "end": v(0.76, -30.58) * mm});
            skLineSegment(sketch, "E5538", {"start": v(0.76, -30.58) * mm, "end": v(0.9, -30.27) * mm});
            skLineSegment(sketch, "E5539", {"start": v(0.9, -30.27) * mm, "end": v(1.01, -29.97) * mm});
            skLineSegment(sketch, "E5540", {"start": v(1.01, -29.97) * mm, "end": v(1.13, -29.66) * mm});
            skLineSegment(sketch, "E5541", {"start": v(1.13, -29.66) * mm, "end": v(1.24, -29.36) * mm});
            skLineSegment(sketch, "E5542", {"start": v(1.24, -29.36) * mm, "end": v(1.35, -29.05) * mm});
            skLineSegment(sketch, "E5543", {"start": v(1.35, -29.05) * mm, "end": v(1.45, -28.74) * mm});
            skLineSegment(sketch, "E5544", {"start": v(1.45, -28.74) * mm, "end": v(1.54, -28.44) * mm});
            skLineSegment(sketch, "E5545", {"start": v(1.54, -28.44) * mm, "end": v(1.63, -28.13) * mm});
            skLineSegment(sketch, "E5546", {"start": v(1.63, -28.13) * mm, "end": v(1.72, -27.83) * mm});
            skLineSegment(sketch, "E5547", {"start": v(1.72, -27.83) * mm, "end": v(1.8, -27.52) * mm});
            skLineSegment(sketch, "E5548", {"start": v(1.8, -27.52) * mm, "end": v(1.87, -27.21) * mm});
            skLineSegment(sketch, "E5549", {"start": v(1.87, -27.21) * mm, "end": v(1.94, -26.9) * mm});
            skLineSegment(sketch, "E5550", {"start": v(1.94, -26.9) * mm, "end": v(2, -26.6) * mm});
            skLineSegment(sketch, "E5551", {"start": v(2, -26.6) * mm, "end": v(2.06, -26.3) * mm});
            skLineSegment(sketch, "E5552", {"start": v(2.06, -26.3) * mm, "end": v(2.1, -25.98) * mm});
            skLineSegment(sketch, "E5553", {"start": v(2.1, -25.98) * mm, "end": v(2.16, -25.68) * mm});
            skLineSegment(sketch, "E5554", {"start": v(2.16, -25.68) * mm, "end": v(2.2, -25.37) * mm});
            skLineSegment(sketch, "E5555", {"start": v(2.2, -25.37) * mm, "end": v(2.23, -25.06) * mm});
            skLineSegment(sketch, "E5556", {"start": v(2.23, -25.06) * mm, "end": v(2.26, -24.75) * mm});
            skLineSegment(sketch, "E5557", {"start": v(2.26, -24.75) * mm, "end": v(2.29, -24.44) * mm});
            skLineSegment(sketch, "E5558", {"start": v(2.29, -24.44) * mm, "end": v(2.3, -24.13) * mm});
            skLineSegment(sketch, "E5559", {"start": v(2.3, -24.13) * mm, "end": v(2.32, -23.82) * mm});
            skLineSegment(sketch, "E5560", {"start": v(2.32, -23.82) * mm, "end": v(2.33, -23.52) * mm});
            skLineSegment(sketch, "E5561", {"start": v(2.33, -23.52) * mm, "end": v(2.33, -23.2) * mm});
            skLineSegment(sketch, "E5562", {"start": v(2.33, -23.2) * mm, "end": v(2.33, -22.9) * mm});
            skLineSegment(sketch, "E5563", {"start": v(2.33, -22.9) * mm, "end": v(2.32, -22.6) * mm});
            skLineSegment(sketch, "E5564", {"start": v(2.32, -22.6) * mm, "end": v(2.3, -22.3) * mm});
            skLineSegment(sketch, "E5565", {"start": v(2.3, -22.3) * mm, "end": v(2.29, -21.99) * mm});
            skLineSegment(sketch, "E5566", {"start": v(2.29, -21.99) * mm, "end": v(2.26, -21.68) * mm});
            skLineSegment(sketch, "E5567", {"start": v(2.26, -21.68) * mm, "end": v(2.24, -21.38) * mm});
            skLineSegment(sketch, "E5568", {"start": v(2.24, -21.38) * mm, "end": v(2.2, -21.07) * mm});
            skLineSegment(sketch, "E5569", {"start": v(2.2, -21.07) * mm, "end": v(2.16, -20.77) * mm});
            skLineSegment(sketch, "E5570", {"start": v(2.16, -20.77) * mm, "end": v(2.12, -20.47) * mm});
            skLineSegment(sketch, "E5571", {"start": v(2.12, -20.47) * mm, "end": v(2.07, -20.16) * mm});
            skLineSegment(sketch, "E5572", {"start": v(2.07, -20.16) * mm, "end": v(2, -19.86) * mm});
            skLineSegment(sketch, "E5573", {"start": v(2, -19.86) * mm, "end": v(1.95, -19.56) * mm});
            skLineSegment(sketch, "E5574", {"start": v(1.95, -19.56) * mm, "end": v(1.88, -19.26) * mm});
            skLineSegment(sketch, "E5575", {"start": v(1.88, -19.26) * mm, "end": v(1.81, -18.95) * mm});
            skLineSegment(sketch, "E5576", {"start": v(1.81, -18.95) * mm, "end": v(1.73, -18.65) * mm});
            skLineSegment(sketch, "E5577", {"start": v(1.73, -18.65) * mm, "end": v(1.65, -18.35) * mm});
            skLineSegment(sketch, "E5578", {"start": v(1.65, -18.35) * mm, "end": v(1.57, -18.05) * mm});
            skLineSegment(sketch, "E5579", {"start": v(1.57, -18.05) * mm, "end": v(1.47, -17.74) * mm});
            skLineSegment(sketch, "E5580", {"start": v(1.47, -17.74) * mm, "end": v(1.37, -17.44) * mm});
            skLineSegment(sketch, "E5581", {"start": v(1.37, -17.44) * mm, "end": v(1.27, -17.14) * mm});
            skLineSegment(sketch, "E5582", {"start": v(1.27, -17.14) * mm, "end": v(1.16, -16.84) * mm});
            skLineSegment(sketch, "E5583", {"start": v(1.16, -16.84) * mm, "end": v(1.05, -16.54) * mm});
            skLineSegment(sketch, "E5584", {"start": v(1.05, -16.54) * mm, "end": v(0.93, -16.24) * mm});
            skLineSegment(sketch, "E5585", {"start": v(0.93, -16.24) * mm, "end": v(0.8, -15.93) * mm});
            skLineSegment(sketch, "E5586", {"start": v(0.8, -15.93) * mm, "end": v(0.68, -15.63) * mm});
            skLineSegment(sketch, "E5587", {"start": v(0.68, -15.63) * mm, "end": v(0.54, -15.33) * mm});
            skLineSegment(sketch, "E5588", {"start": v(0.54, -15.33) * mm, "end": v(0.4, -15.03) * mm});
            skLineSegment(sketch, "E5589", {"start": v(0.4, -15.03) * mm, "end": v(0.26, -14.73) * mm});
            skLineSegment(sketch, "E5590", {"start": v(0.26, -14.73) * mm, "end": v(0.1, -14.43) * mm});
            skLineSegment(sketch, "E5591", {"start": v(0.1, -14.43) * mm, "end": v(-0.05, -14.13) * mm});
            skLineSegment(sketch, "E5592", {"start": v(-0.05, -14.13) * mm, "end": v(-0.09, -14.05) * mm});
            skLineSegment(sketch, "E5593", {"start": v(-0.09, -14.05) * mm, "end": v(-1.72, -14.05) * mm});
            skLineSegment(sketch, "E5594", {"start": v(-1.72, -14.05) * mm, "end": v(-1.73, -14.08) * mm});
            skLineSegment(sketch, "E5595", {"start": v(-1.73, -14.08) * mm, "end": v(-1.86, -14.38) * mm});
            skLineSegment(sketch, "E5596", {"start": v(-1.86, -14.38) * mm, "end": v(-2, -14.68) * mm});
            skLineSegment(sketch, "E5597", {"start": v(-2, -14.68) * mm, "end": v(-2.12, -14.98) * mm});
            skLineSegment(sketch, "E5598", {"start": v(-2.12, -14.98) * mm, "end": v(-2.24, -15.29) * mm});
            skLineSegment(sketch, "E5599", {"start": v(-2.24, -15.29) * mm, "end": v(-2.35, -15.59) * mm});
            skLineSegment(sketch, "E5600", {"start": v(-2.35, -15.59) * mm, "end": v(-2.46, -15.89) * mm});
            skLineSegment(sketch, "E5601", {"start": v(-2.46, -15.89) * mm, "end": v(-2.57, -16.2) * mm});
            skLineSegment(sketch, "E5602", {"start": v(-2.57, -16.2) * mm, "end": v(-2.67, -16.5) * mm});
            skLineSegment(sketch, "E5603", {"start": v(-2.67, -16.5) * mm, "end": v(-2.77, -16.8) * mm});
            skLineSegment(sketch, "E5604", {"start": v(-2.77, -16.8) * mm, "end": v(-2.87, -17.1) * mm});
            skLineSegment(sketch, "E5605", {"start": v(-2.87, -17.1) * mm, "end": v(-2.95, -17.4) * mm});
            skLineSegment(sketch, "E5606", {"start": v(-2.95, -17.4) * mm, "end": v(-3.04, -17.7) * mm});
            skLineSegment(sketch, "E5607", {"start": v(-3.04, -17.7) * mm, "end": v(-3.12, -18.01) * mm});
            skLineSegment(sketch, "E5608", {"start": v(-3.12, -18.01) * mm, "end": v(-3.2, -18.32) * mm});
            skLineSegment(sketch, "E5609", {"start": v(-3.2, -18.32) * mm, "end": v(-3.27, -18.62) * mm});
            skLineSegment(sketch, "E5610", {"start": v(-3.27, -18.62) * mm, "end": v(-3.33, -18.92) * mm});
            skLineSegment(sketch, "E5611", {"start": v(-3.33, -18.92) * mm, "end": v(-3.4, -19.23) * mm});
            skLineSegment(sketch, "E5612", {"start": v(-3.4, -19.23) * mm, "end": v(-3.45, -19.53) * mm});
            skLineSegment(sketch, "E5613", {"start": v(-3.45, -19.53) * mm, "end": v(-3.5, -19.84) * mm});
            skLineSegment(sketch, "E5614", {"start": v(-3.5, -19.84) * mm, "end": v(-3.55, -20.14) * mm});
            skLineSegment(sketch, "E5615", {"start": v(-3.55, -20.14) * mm, "end": v(-3.6, -20.45) * mm});
            skLineSegment(sketch, "E5616", {"start": v(-3.6, -20.45) * mm, "end": v(-3.63, -20.75) * mm});
            skLineSegment(sketch, "E5617", {"start": v(-3.63, -20.75) * mm, "end": v(-3.67, -21.06) * mm});
            skLineSegment(sketch, "E5618", {"start": v(-3.67, -21.06) * mm, "end": v(-3.7, -21.36) * mm});
            skLineSegment(sketch, "E5619", {"start": v(-3.7, -21.36) * mm, "end": v(-3.72, -21.67) * mm});
            skLineSegment(sketch, "E5620", {"start": v(-3.72, -21.67) * mm, "end": v(-3.75, -21.98) * mm});
            skLineSegment(sketch, "E5621", {"start": v(-3.75, -21.98) * mm, "end": v(-3.76, -22.28) * mm});
            skLineSegment(sketch, "E5622", {"start": v(-3.76, -22.28) * mm, "end": v(-3.77, -22.6) * mm});
            skLineSegment(sketch, "E5623", {"start": v(-3.77, -22.6) * mm, "end": v(-3.78, -22.9) * mm});
            skLineSegment(sketch, "E5624", {"start": v(-3.78, -22.9) * mm, "end": v(-3.78, -23.2) * mm});
            skLineSegment(sketch, "E5625", {"start": v(-3.78, -23.2) * mm, "end": v(-3.78, -23.52) * mm});
            skLineSegment(sketch, "E5626", {"start": v(-3.78, -23.52) * mm, "end": v(-3.77, -23.83) * mm});
            skLineSegment(sketch, "E5627", {"start": v(-3.77, -23.83) * mm, "end": v(-3.76, -24.14) * mm});
            skLineSegment(sketch, "E5628", {"start": v(-3.76, -24.14) * mm, "end": v(-3.74, -24.45) * mm});
            skLineSegment(sketch, "E5629", {"start": v(-3.74, -24.45) * mm, "end": v(-3.72, -24.76) * mm});
            skLineSegment(sketch, "E5630", {"start": v(-3.72, -24.76) * mm, "end": v(-3.7, -25.07) * mm});
            skLineSegment(sketch, "E5631", {"start": v(-3.7, -25.07) * mm, "end": v(-3.67, -25.38) * mm});
            skLineSegment(sketch, "E5632", {"start": v(-3.67, -25.38) * mm, "end": v(-3.63, -25.7) * mm});
            skLineSegment(sketch, "E5633", {"start": v(-3.63, -25.7) * mm, "end": v(-3.6, -26) * mm});
            skLineSegment(sketch, "E5634", {"start": v(-3.6, -26) * mm, "end": v(-3.55, -26.31) * mm});
            skLineSegment(sketch, "E5635", {"start": v(-3.55, -26.31) * mm, "end": v(-3.5, -26.62) * mm});
            skLineSegment(sketch, "E5636", {"start": v(-3.5, -26.62) * mm, "end": v(-3.44, -26.93) * mm});
            skLineSegment(sketch, "E5637", {"start": v(-3.44, -26.93) * mm, "end": v(-3.38, -27.24) * mm});
            skLineSegment(sketch, "E5638", {"start": v(-3.38, -27.24) * mm, "end": v(-3.32, -27.55) * mm});
            skLineSegment(sketch, "E5639", {"start": v(-3.32, -27.55) * mm, "end": v(-3.25, -27.86) * mm});
            skLineSegment(sketch, "E5640", {"start": v(-3.25, -27.86) * mm, "end": v(-3.18, -28.17) * mm});
            skLineSegment(sketch, "E5641", {"start": v(-3.18, -28.17) * mm, "end": v(-3.1, -28.47) * mm});
            skLineSegment(sketch, "E5642", {"start": v(-3.1, -28.47) * mm, "end": v(-3.02, -28.78) * mm});
            skLineSegment(sketch, "E5643", {"start": v(-3.02, -28.78) * mm, "end": v(-2.93, -29.09) * mm});
            skLineSegment(sketch, "E5644", {"start": v(-2.93, -29.09) * mm, "end": v(-2.84, -29.4) * mm});
            skLineSegment(sketch, "E5645", {"start": v(-2.84, -29.4) * mm, "end": v(-2.74, -29.7) * mm});
            skLineSegment(sketch, "E5646", {"start": v(-2.74, -29.7) * mm, "end": v(-2.64, -30.01) * mm});
            skLineSegment(sketch, "E5647", {"start": v(-2.64, -30.01) * mm, "end": v(-2.54, -30.32) * mm});
            skLineSegment(sketch, "E5648", {"start": v(-2.54, -30.32) * mm, "end": v(-2.43, -30.63) * mm});
            skLineSegment(sketch, "E5649", {"start": v(-2.43, -30.63) * mm, "end": v(-2.31, -30.93) * mm});
            skLineSegment(sketch, "E5650", {"start": v(-2.31, -30.93) * mm, "end": v(-2.2, -31.24) * mm});
            skLineSegment(sketch, "E5651", {"start": v(-2.2, -31.24) * mm, "end": v(-2.07, -31.54) * mm});
            skLineSegment(sketch, "E5652", {"start": v(-2.07, -31.54) * mm, "end": v(-1.94, -31.85) * mm});
            skLineSegment(sketch, "E5653", {"start": v(-1.94, -31.85) * mm, "end": v(-1.8, -32.16) * mm});
            skLineSegment(sketch, "E5654", {"start": v(-1.8, -32.16) * mm, "end": v(-1.67, -32.46) * mm});
            skLineSegment(sketch, "E5655", {"start": v(-1.67, -32.46) * mm, "end": v(-1.65, -32.5) * mm});
            skLineSegment(sketch, "E5656", {"start": v(-1.65, -32.5) * mm, "end": v(-0.16, -32.5) * mm});
            skLineSegment(sketch, "E5657", {"start": v(-0.16, -32.5) * mm, "end": v(-0.12, -32.41) * mm});
            skPoint(sketch, "E5658", {"position": v(-0.8, 0) * mm});
            skLineSegment(sketch, "E5659", {"start": v(-0.8, 3) * mm, "end": v(-0.8, -2.5) * mm, "construction": true});
            skLineSegment(sketch, "E5660", {"start": v(-2.45, -2.5) * mm, "end": v(0.87, -2.5) * mm});
            skCircle(sketch, "E5661", {"center": v(-0.8, 0) * mm, "radius": 1.5 * mm});
            skCircle(sketch, "E5662", {"center": v(-0.8, 0) * mm, "radius": 3 * mm});
            skSolve(sketch);
        }
        {
            var Q0;
            Q0=makeQuery(id+"F0.imprint","IMPRINT",FACE,{"disambiguationData":[TD([[makeQuery(id+"F0.imprint","IMPRINT",EDGE,{"derivedFrom":sQuery(id+"F0.wireOp",EDGE,"E0")}),1.0]])]});
            var Q1;
            {var subQ0=sQuery(id+"F0.wireOp",EDGE,"E5660");Q1=makeQuery(id+"F0.imprint","IMPRINT",FACE,{"disambiguationData":[TD([[makeQuery(id+"F0.imprint","IMPRINT",EDGE,{"derivedFrom":subQ0}),-1.0]])]});}
            extrude(context, id + "F1", {"entities" : qUnion([Q0, Q1]), "depth" : 5 * mm});
        }
    });
